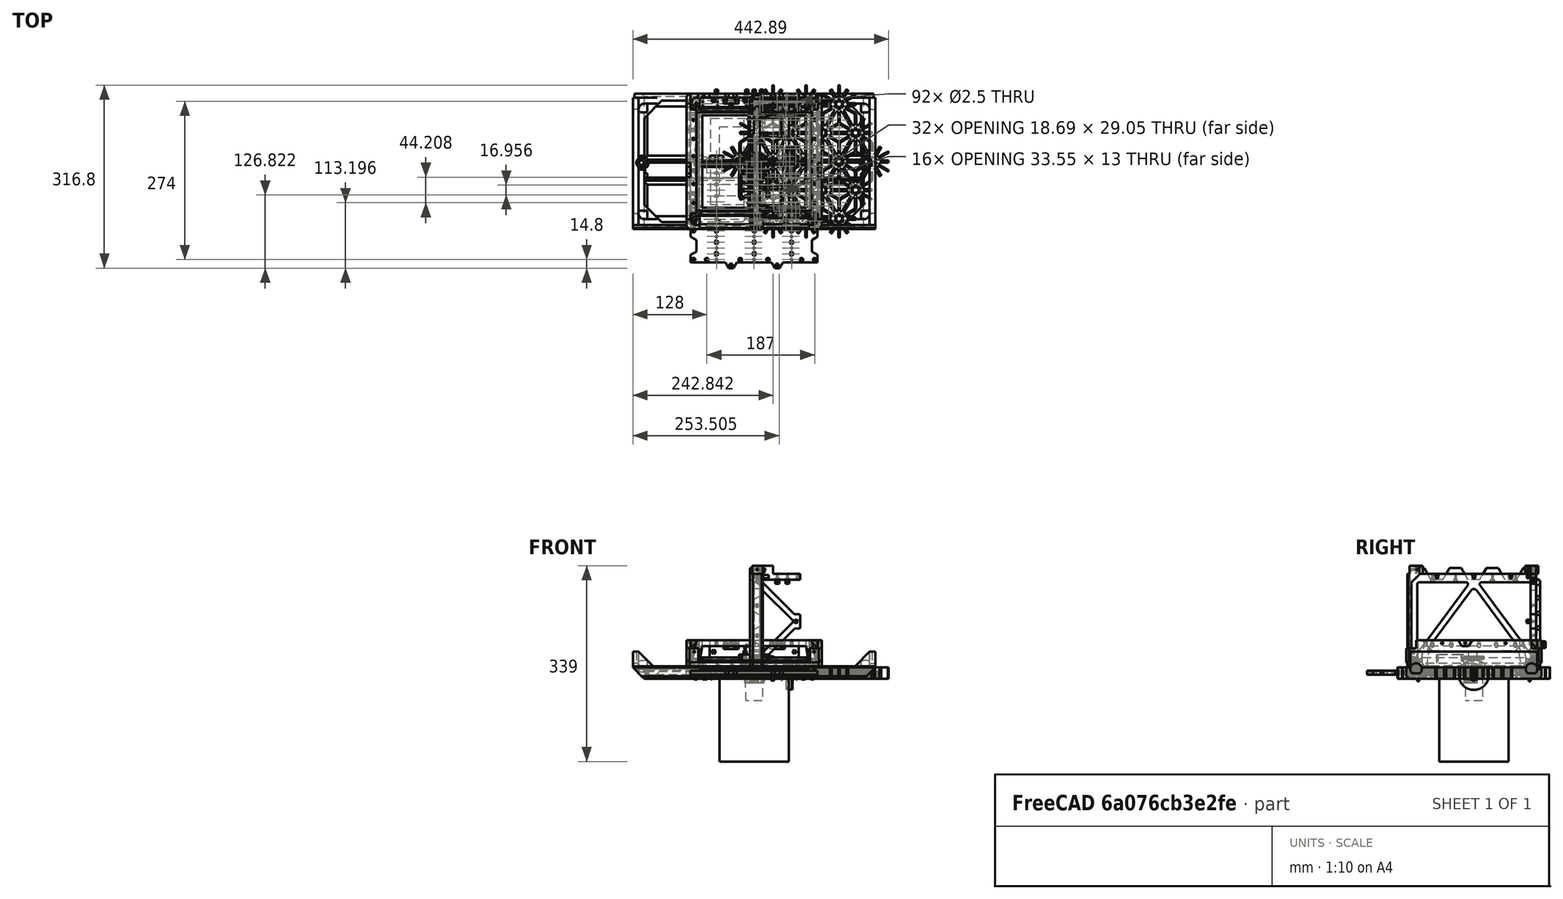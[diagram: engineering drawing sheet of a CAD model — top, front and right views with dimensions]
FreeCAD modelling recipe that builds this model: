
FCSTD DOCUMENT  (FreeCAD 0.20R29177 (Git))
Label: miniXY-Frame
License: All rights reserved
LicenseURL: http://en.wikipedia.org/wiki/All_rights_reserved
objects: Sketcher::SketchObject×115, Part::FeaturePython×91, PartDesign::Pad×45, PartDesign::CoordinateSystem×41, PartDesign::Pocket×41, PartDesign::Hole×37, PartDesign::Body×31, App::Link×25, App::Part×25, PartDesign::ShapeBinder×13, PartDesign::SubShapeBinder×9, PartDesign::Boolean×9, PartDesign::AdditiveBox×5, PartDesign::AdditivePrism×5, PartDesign::Chamfer×4, PartDesign::SubtractiveBox×4, PartDesign::Line×4, Part::Mirroring×4, App::DocumentObjectGroup×3, PartDesign::PolarPattern×3, +8 more types
note: 623 computed .brp shape members not serialized (recipe doc carries the construction recipe); baked Part::Feature solids carry a one-line shape summary decoded from their .brp
EXTERNAL_REF file=../../AppData/Local/Temp/FreeCAD/Cache/FreeCAD_Doc_066654b6-2272-45e0-8b84-83cefede7382_da39a3_1616 obj=Assembly
EXTERNAL_REF file=MGN9.FCStd obj=Assembly
EXTERNAL_REF file=../../AppData/Local/Temp/FreeCAD/Cache/FreeCAD_Doc_a19bdf6e-7e4a-4f2c-907a-7fb10fbe9d93_da39a3_1616 obj=Assembly
EXTERNAL_REF file=../../AppData/Local/Temp/FreeCAD/Cache/FreeCAD_Doc_1e8708ad-fd8b-4a5b-8716-75e4b405d050_da39a3_1616 obj=Assembly
EXTERNAL_REF file=Drive.FCStd obj=LCS_Nema17_Origin
EXTERNAL_REF file=Drive.FCStd obj=Part
EXTERNAL_REF file=../../AppData/Local/Temp/FreeCAD/Cache/FreeCAD_Doc_5f10fd76-f536-416b-8568-16cb6060fa77_da39a3_1616 obj=Assembly
EXTERNAL_REF file=../../AppData/Local/Temp/FreeCAD/Cache/FreeCAD_Doc_b771bde3-d604-4bf0-b2c0-fa68c06b88b6_da39a3_1616 obj=Assembly
EXTERNAL_REF file=../../AppData/Local/Temp/FreeCAD/Cache/FreeCAD_Doc_0e739f10-988f-47ea-a0ae-2bb79bd32ce8_da39a3_1616 obj=Assembly
EXTERNAL_REF file=miniXY-ZDrive.FCStd obj=LCS_Origin
EXTERNAL_REF file=miniXY-ZDrive.FCStd obj=Model

FEATURE [PartDesign::CoordinateSystem] LCS_Origin
  AttacherType = Attacher::AttachEngine3D
  MapMode = 2
  Support = -> [X_Axis]
FEATURE [App::FeaturePython] Variables  # WARN: FeaturePython — macro-defined, semantics opaque (R4)
  CavitySpacingX = 10
  CavitySpacingY = 10
  FittingGap = 0.2
  GantorySpacing = 200
  HeightFromBase = 230
  KumikoBaseWidth = 3
  M3TapDiameter = 2.5
  PositionX = 0
  PositionY = 0
  PositionZ = 0
  PrintBedPosition = 140
  PullyDiameterDrive = 12.73
  PullyDiameterIdler = 12.73
  TopThickness = 10
  Type = App::PropertyContainer
  WallThickness = 7
FEATURE [App::DocumentObjectGroup] Constraints
FEATURE [App::DocumentObjectGroup] Configurations
FEATURE [Part::FeaturePython] MGN9_X  # link proxy (typed FeaturePython)
  AttachedBy = #LCS_Origin
  AttachedTo = Gantory#LCS_GantoryOrigin
  Length = 175
  LinkedObject = -> <external ../../AppData/Local/Temp/FreeCAD/Cache/FreeCAD_Doc_066654b6-2272-45e0-8b84-83cefede7382_da39a3_1616>#Assembly
  Placement = pos=(-2.4e-15,0,-20) rot=(0,0,1;0rad)
  Position = 0
  SolverId = Asm4EE
  SourceObject = -> <external MGN9.FCStd>#Assembly
  expr: Placement = Gantory.Placement * LCS_GantoryOrigin.Placement * AttachmentOffset * varTmpDoc_6#LCS_Origin.Placement ^ -1
FEATURE [PartDesign::CoordinateSystem] LCS_GantoryOrigin
  AttacherType = Attacher::AttachEngine3D
  MapMode = 2
  Support = -> [X_Axis001]
FEATURE [App::Link] Gantory  label="Gantory001"
  AssemblyType = Part::Link
  AttachedBy = #LCS_GantoryOrigin
  AttachedTo = TopPanel#LCS_TopPanelGantoryOrigin
  LinkPlacement = pos=(-2.4e-15,0,-20) rot=(0,0,1;0rad)
  LinkedObject = -> Part
  Placement = pos=(-2.4e-15,0,-20) rot=(0,0,1;0rad)
  SolverId = Asm4EE
  expr: Placement = TopPanel.Placement * LCS_TopPanelGantoryOrigin.Placement * AttachmentOffset * LCS_GantoryOrigin.Placement ^ -1
FEATURE [PartDesign::CoordinateSystem] LCS_LeftRailOrigin
  AttacherType = Attacher::AttachEngine3D
  AttachmentOffset = pos=(0,-100,-10) rot=(0,0,1;0rad)
  MapMode = 3
  Placement = pos=(-100,2.33e-14,10) rot=(0.707107,0.707107,0;3.14159rad)
  Support = -> [Y_Axis001]
  expr: .AttachmentOffset.Base.y = -<<Variables>>.GantorySpacing / 2
FEATURE [PartDesign::CoordinateSystem] LCS_RightRailOrigin
  AttacherType = Attacher::AttachEngine3D
  AttachmentOffset = pos=(0,100,-10) rot=(0,0,1;0rad)
  MapMode = 3
  Placement = pos=(100,-2.11e-14,10) rot=(0.707107,0.707107,0;3.14159rad)
  Support = -> [Y_Axis001]
  expr: .AttachmentOffset.Base.y = <<Variables>>.GantorySpacing / 2
FEATURE [Part::FeaturePython] MGN9_Y_Left  # link proxy (typed FeaturePython)
  AttachedBy = #LCS_Origin
  AttachedTo = Gantory#LCS_LeftRailOrigin
  Length = 175
  LinkedObject = -> <external ../../AppData/Local/Temp/FreeCAD/Cache/FreeCAD_Doc_a19bdf6e-7e4a-4f2c-907a-7fb10fbe9d93_da39a3_1616>#Assembly
  Placement = pos=(-100,2.33e-14,-10) rot=(0.707107,0.707107,0;3.14159rad)
  Position = 0
  SolverId = Asm4EE
  SourceObject = -> <external MGN9.FCStd>#Assembly
  expr: Placement = Gantory.Placement * LCS_LeftRailOrigin.Placement * AttachmentOffset * varTmpDoc_7#LCS_Origin.Placement ^ -1
FEATURE [Part::FeaturePython] MGN9_Y_Right  # link proxy (typed FeaturePython)
  AttachedBy = #LCS_Origin
  AttachedTo = Gantory#LCS_RightRailOrigin
  Length = 175
  LinkedObject = -> <external ../../AppData/Local/Temp/FreeCAD/Cache/FreeCAD_Doc_1e8708ad-fd8b-4a5b-8716-75e4b405d050_da39a3_1616>#Assembly
  Placement = pos=(100,-2.11e-14,-10) rot=(0.707107,0.707107,0;3.14159rad)
  Position = 0
  SolverId = Asm4EE
  SourceObject = -> <external MGN9.FCStd>#Assembly
  expr: Placement = Gantory.Placement * LCS_RightRailOrigin.Placement * AttachmentOffset * varTmpDoc_8#LCS_Origin.Placement ^ -1
FEATURE [Sketcher::SketchObject] Sketch
  FullyConstrained = true
  MapMode = 5
  Support = -> [XY_Plane006]
  sketch-geometry (19):
    g0: LineSegment StartX=-7.5 StartY=16 StartZ=0 EndX=7.5 EndY=16 EndZ=0
    g1: LineSegment StartX=7.5 StartY=-16 StartZ=0 EndX=-7.5 EndY=-16 EndZ=0
    g2: LineSegment StartX=-10 StartY=-13.5 StartZ=0 EndX=-10 EndY=13.5 EndZ=0
    g3: LineSegment StartX=20.7665 StartY=5 StartZ=0 EndX=48 EndY=5 EndZ=0
    g4: LineSegment StartX=50 StartY=3 StartZ=0 EndX=50 EndY=-3 EndZ=0
    g5: LineSegment StartX=48 StartY=-5 StartZ=0 EndX=20.7665 EndY=-5 EndZ=0
    g6: ArcOfCircle CenterX=20.7665 CenterY=-16 CenterZ=0 NormalX=0 NormalY=0 NormalZ=1 AngleXU=0 Radius=11 StartAngle=1.5708 EndAngle=2.95533
    g7: ArcOfCircle CenterX=20.7665 CenterY=16 CenterZ=0 NormalX=0 NormalY=0 NormalZ=1 AngleXU=0 Radius=11 StartAngle=3.32785 EndAngle=4.71239
    g8: ArcOfCircle CenterX=-7.5 CenterY=13.5 CenterZ=0 NormalX=0 NormalY=0 NormalZ=1 AngleXU=0 Radius=2.5 StartAngle=1.5708 EndAngle=3.14159
    g9: GeomPoint X=-10 Y=16 Z=0
    g10: ArcOfCircle CenterX=-7.5 CenterY=-13.5 CenterZ=0 NormalX=0 NormalY=0 NormalZ=1 AngleXU=0 Radius=2.5 StartAngle=3.14159 EndAngle=4.71239
    g11: GeomPoint X=-10 Y=-16 Z=0
    g12: ArcOfCircle CenterX=7.5 CenterY=-13.5 CenterZ=0 NormalX=0 NormalY=0 NormalZ=1 AngleXU=0 Radius=2.5 StartAngle=4.71239 EndAngle=6.09693
    g13: ArcOfCircle CenterX=7.5 CenterY=13.5 CenterZ=0 NormalX=0 NormalY=0 NormalZ=1 AngleXU=0 Radius=2.5 StartAngle=0.18626 EndAngle=1.5708
    g14: GeomPoint X=10 Y=16 Z=0
    g15: ArcOfCircle CenterX=48 CenterY=3 CenterZ=0 NormalX=0 NormalY=0 NormalZ=1 AngleXU=0 Radius=2 StartAngle=-9e-16 EndAngle=1.5708
    g16: GeomPoint X=50 Y=5 Z=0
    g17: ArcOfCircle CenterX=48 CenterY=-3 CenterZ=0 NormalX=0 NormalY=0 NormalZ=1 AngleXU=0 Radius=2 StartAngle=4.71239 EndAngle=6.28319
    g18: GeomPoint X=50 Y=-5 Z=0
  constraints (40):
    c: Horizontal(g3)
    c: Symmetric(g9,g11,g-1)
    c: Symmetric(g16,g18,g-1)
    c: DistanceY(g11,g9) = 32
    c: Symmetric(g9,g14,g-2)
    c: DistanceY(g18,g16) = 10
    c: DistanceX(g-1,g16) = 50
    c: Symmetric(g7,g6,g-1)
    c: PointOnObject(g9,g0)
    c: PointOnObject(g9,g2)
    c: Tangent(g0,g8) = 1.5708
    c: Tangent(g2,g8) = 1.5708
    c: PointOnObject(g11,g2)
    c: PointOnObject(g11,g1)
    c: Tangent(g2,g10) = 1.5708
    c: Tangent(g1,g10) = 1.5708
    c: Tangent(g1,g12) = 1.5708
    c: PointOnObject(g14,g0)
    c: Tangent(g0,g13) = 1.5708
    c: Equal(g8,g10)
    c: Equal(g8,g12)
    c: Radius(g8) = 2.5
    c: DistanceX(g9,g14) = 20
    c: Tangent(g13,g7) = 1.5708
    c: Tangent(g12,g6) = 1.5708
    c: PointOnObject(g7,g0)
    c: Symmetric(g8,g13,g-2)
    c: Symmetric(g12,g13,g-1)
    c: Tangent(g7,g3) = -1.5708
    c: Tangent(g6,g5) = -1.5708
    c: PointOnObject(g16,g3)
    c: PointOnObject(g16,g4)
    c: Tangent(g3,g15) = 1.5708
    c: Tangent(g4,g15) = 1.5708
    c: PointOnObject(g18,g5)
    c: PointOnObject(g18,g4)
    c: Tangent(g5,g17) = 1.5708
    c: Tangent(g4,g17) = 1.5708
    c: Equal(g15,g17)
    c: Radius(g15) = 2
FEATURE [PartDesign::Pad] Pad
  Direction = (0,0,1)
  Length = 7
  Length2 = 10
  Profile = -> Sketch
  ReferenceAxis = -> Sketch [N_Axis]
  Type = 0
FEATURE [Sketcher::SketchObject] Sketch005
  AttachmentOffset = pos=(0,0,10) rot=(0,0,1;0rad)
  FullyConstrained = true
  MapMode = 5
  Placement = pos=(0,0,10) rot=(0,0,1;0rad)
  Support = -> [XY_Plane006]
  sketch-geometry (4):
    g0: Circle CenterX=-7.5 CenterY=5 CenterZ=0 NormalX=0 NormalY=0 NormalZ=1 AngleXU=0 Radius=1.5
    g1: Circle CenterX=-7.5 CenterY=-5 CenterZ=0 NormalX=0 NormalY=0 NormalZ=1 AngleXU=0 Radius=1.5
    g2: Circle CenterX=7.5 CenterY=-5 CenterZ=0 NormalX=0 NormalY=0 NormalZ=1 AngleXU=0 Radius=1.5
    g3: Circle CenterX=7.5 CenterY=5 CenterZ=0 NormalX=0 NormalY=0 NormalZ=1 AngleXU=0 Radius=1.5
  constraints (9):
    c: Symmetric(g0,g1,g-1)
    c: Symmetric(g3,g2,g-1)
    c: Symmetric(g0,g3,g-2)
    c: DistanceX(g0,g3) = 15
    c: DistanceY(g1,g0) = 10
    c: Equal(g0,g1)
    c: Equal(g0,g2)
    c: Equal(g0,g3)
    c: Diameter(g0) = 3
FEATURE [Sketcher::SketchObject] Sketch006
  FullyConstrained = true
  MapMode = 5
  Support = -> [XY_Plane006]
  sketch-geometry (2):
    g0: Circle CenterX=0 CenterY=0 CenterZ=0 NormalX=0 NormalY=0 NormalZ=1 AngleXU=0 Radius=1.5
    g1: Circle CenterX=12.73 CenterY=0 CenterZ=0 NormalX=0 NormalY=0 NormalZ=1 AngleXU=0 Radius=1.5
  constraints (5):
    c: Coincident(g0,g-1)
    c: PointOnObject(g1,g-1)
    c: Equal(g0,g1)
    c: Diameter(g0) = 3
    c: DistanceX(g0,g1) = 12.73
FEATURE [PartDesign::Chamfer] Chamfer
  Angle = 45
  Base = -> Pad [Face16]
  BaseFeature = -> Pad
  ChamferType = 0
  FlipDirection = false
  Size = 1
  Size2 = 1
  SupportTransform = false
  UseAllEdges = false
FEATURE [Sketcher::SketchObject] Sketch007
  FullyConstrained = true
  MapMode = 5
  Support = -> [XY_Plane006]
  sketch-geometry (2):
    g0: Circle CenterX=20 CenterY=0 CenterZ=0 NormalX=0 NormalY=0 NormalZ=1 AngleXU=0 Radius=1.5
    g1: Circle CenterX=40 CenterY=0 CenterZ=0 NormalX=0 NormalY=0 NormalZ=1 AngleXU=0 Radius=1.5
  constraints (6):
    c: PointOnObject(g0,g-1)
    c: PointOnObject(g1,g-1)
    c: DistanceX(g-1,g0) = 20
    c: DistanceX(g0,g1) = 20
    c: Equal(g0,g1)
    c: Diameter(g0) = 3
FEATURE [Sketcher::SketchObject] Sketch008
  AttachmentOffset = pos=(0,0,16.5) rot=(0,0,1;0rad)
  FullyConstrained = true
  MapMode = 5
  Placement = pos=(0,0,16.5) rot=(0,0,1;0rad)
  Support = -> [XY_Plane006]
  sketch-geometry (6):
    g0: LineSegment StartX=9.5 StartY=5 StartZ=0 EndX=26 EndY=5 EndZ=0
    g1: LineSegment StartX=24 StartY=3 StartZ=0 EndX=24 EndY=-3 EndZ=0
    g2: LineSegment StartX=26 StartY=-5 StartZ=0 EndX=9.5 EndY=-5 EndZ=0
    g3: LineSegment StartX=9.5 StartY=-5 StartZ=0 EndX=9.5 EndY=5 EndZ=0
    g4: ArcOfCircle CenterX=26 CenterY=3 CenterZ=0 NormalX=0 NormalY=0 NormalZ=1 AngleXU=0 Radius=2 StartAngle=1.5708 EndAngle=3.14159
    g5: ArcOfCircle CenterX=26 CenterY=-3 CenterZ=0 NormalX=0 NormalY=0 NormalZ=1 AngleXU=0 Radius=2 StartAngle=3.14159 EndAngle=4.71239
  constraints (14):
    c: Horizontal(g0)
    c: Coincident(g0,g3)
    c: Symmetric(g2,g0,g-1)
    c: Coincident(g3,g2)
    c: Tangent(g4,g1) = -1.5708
    c: Tangent(g4,g0) = 1.5708
    c: Tangent(g5,g1) = -1.5708
    c: Tangent(g5,g2) = 1.5708
    c: Symmetric(g4,g5,g-1)
    c: Equal(g4,g5)
    c: Radius(g4) = 2
    c: DistanceY(g3,g3) = 10
    c: DistanceX(g0,g1) = 14.5
    c: DistanceX(g-1,g0) = 9.5
FEATURE [Sketcher::SketchObject] Sketch009
  FullyConstrained = true
  MapMode = 5
  Support = -> [XY_Plane006]
  sketch-geometry (36):
    g0: LineSegment StartX=11.5 StartY=5 StartZ=0 EndX=30 EndY=5 EndZ=0
    g1: LineSegment StartX=32 StartY=3 StartZ=0 EndX=32 EndY=-3 EndZ=0
    g2: LineSegment StartX=30 StartY=-5 StartZ=0 EndX=11.5 EndY=-5 EndZ=0
    g3: LineSegment StartX=9.5 StartY=-3 StartZ=0 EndX=9.5 EndY=3 EndZ=0
    g4: LineSegment StartX=-3 StartY=16 StartZ=0 EndX=3 EndY=16 EndZ=0
    g5: LineSegment StartX=5 StartY=14 StartZ=0 EndX=5 EndY=12 EndZ=0
    g6: LineSegment StartX=3 StartY=10 StartZ=0 EndX=-3 EndY=10 EndZ=0
    g7: LineSegment StartX=-5 StartY=12 StartZ=0 EndX=-5 EndY=14 EndZ=0
    g8: LineSegment StartX=-3 StartY=-10 StartZ=0 EndX=3 EndY=-10 EndZ=0
    g9: LineSegment StartX=5 StartY=-12 StartZ=0 EndX=5 EndY=-14 EndZ=0
    g10: LineSegment StartX=3 StartY=-16 StartZ=0 EndX=-3 EndY=-16 EndZ=0
    g11: LineSegment StartX=-5 StartY=-14 StartZ=0 EndX=-5 EndY=-12 EndZ=0
    g12: ArcOfCircle CenterX=-3 CenterY=14 CenterZ=0 NormalX=0 NormalY=0 NormalZ=1 AngleXU=0 Radius=2 StartAngle=1.5708 EndAngle=3.14159
    g13: GeomPoint X=-5 Y=16 Z=0
    g14: ArcOfCircle CenterX=-3 CenterY=12 CenterZ=0 NormalX=0 NormalY=0 NormalZ=1 AngleXU=0 Radius=2 StartAngle=3.14159 EndAngle=4.71239
    g15: GeomPoint X=-5 Y=10 Z=0
    g16: ArcOfCircle CenterX=3 CenterY=12 CenterZ=0 NormalX=0 NormalY=0 NormalZ=1 AngleXU=0 Radius=2 StartAngle=4.71239 EndAngle=6.28319
    g17: GeomPoint X=5 Y=10 Z=0
    g18: ArcOfCircle CenterX=3 CenterY=14 CenterZ=0 NormalX=0 NormalY=0 NormalZ=1 AngleXU=0 Radius=2 StartAngle=1e-16 EndAngle=1.5708
    g19: GeomPoint X=5 Y=16 Z=0
    g20: ArcOfCircle CenterX=-3 CenterY=-12 CenterZ=0 NormalX=0 NormalY=0 NormalZ=1 AngleXU=0 Radius=2 StartAngle=1.5708 EndAngle=3.14159
    g21: GeomPoint X=-5 Y=-10 Z=0
    g22: ArcOfCircle CenterX=-3 CenterY=-14 CenterZ=0 NormalX=0 NormalY=0 NormalZ=1 AngleXU=0 Radius=2 StartAngle=3.14159 EndAngle=4.71239
    g23: GeomPoint X=-5 Y=-16 Z=0
    g24: ArcOfCircle CenterX=3 CenterY=-14 CenterZ=0 NormalX=0 NormalY=0 NormalZ=1 AngleXU=0 Radius=2 StartAngle=4.71239 EndAngle=6.28319
    g25: GeomPoint X=5 Y=-16 Z=0
    g26: ArcOfCircle CenterX=3 CenterY=-12 CenterZ=0 NormalX=0 NormalY=0 NormalZ=1 AngleXU=0 Radius=2 StartAngle=0 EndAngle=1.5708
    g27: GeomPoint X=5 Y=-10 Z=0
    g28: ArcOfCircle CenterX=11.5 CenterY=3 CenterZ=0 NormalX=0 NormalY=0 NormalZ=1 AngleXU=0 Radius=2 StartAngle=1.5708 EndAngle=3.14159
    g29: GeomPoint X=9.5 Y=5 Z=0
    g30: ArcOfCircle CenterX=11.5 CenterY=-3 CenterZ=0 NormalX=0 NormalY=0 NormalZ=1 AngleXU=0 Radius=2 StartAngle=3.14159 EndAngle=4.71239
    g31: GeomPoint X=9.5 Y=-5 Z=0
    g32: ArcOfCircle CenterX=30 CenterY=-3 CenterZ=0 NormalX=0 NormalY=0 NormalZ=1 AngleXU=0 Radius=2 StartAngle=4.71239 EndAngle=6.28319
    g33: GeomPoint X=32 Y=-5 Z=0
    g34: ArcOfCircle CenterX=30 CenterY=3 CenterZ=0 NormalX=0 NormalY=0 NormalZ=1 AngleXU=0 Radius=2 StartAngle=3e-16 EndAngle=1.5708
    g35: GeomPoint X=32 Y=5 Z=0
  constraints (76):
    c: Horizontal(g0)
    c: Symmetric(g29,g31,g-1)
    c: Symmetric(g35,g33,g-1)
    c: DistanceY(g31,g29) = 10
    c: DistanceX(g29,g35) = 22.5
    c: Vertical(g7)
    c: Symmetric(g13,g19,g-2)
    c: Symmetric(g15,g17,g-2)
    c: Symmetric(g21,g15,g-1)
    c: Symmetric(g13,g23,g-1)
    c: Symmetric(g17,g27,g-1)
    c: Symmetric(g19,g25,g-1)
    c: DistanceY(g23,g13) = 32
    c: DistanceX(g13,g19) = 10
    c: DistanceY(g15,g13) = 6
    c: DistanceX(g-1,g35) = 32
    c: PointOnObject(g13,g4)
    c: PointOnObject(g13,g7)
    c: Tangent(g4,g12) = 1.5708
    c: Tangent(g7,g12) = 1.5708
    c: PointOnObject(g15,g7)
    c: PointOnObject(g15,g6)
    c: Tangent(g7,g14) = 1.5708
    c: Tangent(g6,g14) = 1.5708
    c: PointOnObject(g17,g6)
    c: PointOnObject(g17,g5)
    c: Tangent(g6,g16) = 1.5708
    c: Tangent(g5,g16) = 1.5708
    c: PointOnObject(g19,g5)
    c: PointOnObject(g19,g4)
    c: Tangent(g5,g18) = 1.5708
    c: Tangent(g4,g18) = 1.5708
    c: PointOnObject(g21,g8)
    c: PointOnObject(g21,g11)
    c: Tangent(g8,g20) = 1.5708
    c: Tangent(g11,g20) = 1.5708
    c: PointOnObject(g23,g11)
    c: PointOnObject(g23,g10)
    c: Tangent(g11,g22) = 1.5708
    c: Tangent(g10,g22) = 1.5708
    c: PointOnObject(g25,g10)
    c: PointOnObject(g25,g9)
    c: Tangent(g10,g24) = 1.5708
    c: Tangent(g9,g24) = 1.5708
    c: PointOnObject(g27,g9)
    c: PointOnObject(g27,g8)
    c: Tangent(g9,g26) = 1.5708
    c: Tangent(g8,g26) = 1.5708
    c: PointOnObject(g29,g0)
    c: PointOnObject(g29,g3)
    c: Tangent(g0,g28) = 1.5708
    c: Tangent(g3,g28) = 1.5708
    c: PointOnObject(g31,g3)
    c: PointOnObject(g31,g2)
    c: Tangent(g3,g30) = 1.5708
    c: Tangent(g2,g30) = 1.5708
    c: PointOnObject(g33,g2)
    c: PointOnObject(g33,g1)
    c: Tangent(g2,g32) = 1.5708
    c: Tangent(g1,g32) = 1.5708
    c: PointOnObject(g35,g1)
    c: PointOnObject(g35,g0)
    c: Tangent(g1,g34) = 1.5708
    c: Tangent(g0,g34) = 1.5708
    c: Equal(g12,g14)
    c: Equal(g12,g16)
    c: Equal(g12,g18)
    c: Equal(g12,g20)
    c: Equal(g12,g22)
    c: Equal(g12,g24)
    c: Equal(g12,g26)
    c: Equal(g12,g28)
    c: Equal(g12,g30)
    c: Equal(g12,g32)
    c: Equal(g12,g34)
    c: Radius(g12) = 2
FEATURE [Sketcher::SketchObject] Sketch010
  FullyConstrained = true
  MapMode = 5
  Support = -> [XY_Plane006]
  sketch-geometry (2):
    g0: Circle CenterX=0 CenterY=13 CenterZ=0 NormalX=0 NormalY=0 NormalZ=1 AngleXU=0 Radius=1.5
    g1: Circle CenterX=0 CenterY=-13 CenterZ=0 NormalX=0 NormalY=0 NormalZ=1 AngleXU=0 Radius=1.5
  constraints (5):
    c: PointOnObject(g0,g-2)
    c: Symmetric(g0,g1,g-1)
    c: DistanceY(g1,g0) = 26
    c: Equal(g0,g1)
    c: Diameter(g0) = 3
FEATURE [Sketcher::SketchObject] Sketch011
  AttachmentOffset = pos=(0,0,27) rot=(0,0,1;0rad)
  FullyConstrained = true
  MapMode = 5
  Placement = pos=(0,0,27) rot=(0,0,1;0rad)
  Support = -> [XY_Plane008]
  sketch-geometry (8):
    g0: LineSegment StartX=-5 StartY=18 StartZ=0 EndX=5 EndY=18 EndZ=0
    g1: LineSegment StartX=5 StartY=-18 StartZ=0 EndX=-5 EndY=-18 EndZ=0
    g2: LineSegment StartX=-5 StartY=-18 StartZ=0 EndX=-5 EndY=18 EndZ=0
    g3: LineSegment StartX=18.5 StartY=4.5 StartZ=0 EndX=34 EndY=4.5 EndZ=0
    g4: LineSegment StartX=34 StartY=4.5 StartZ=0 EndX=34 EndY=-4.5 EndZ=0
    g5: LineSegment StartX=34 StartY=-4.5 StartZ=0 EndX=18.5 EndY=-4.5 EndZ=0
    g6: ArcOfCircle CenterX=18.5 CenterY=-18 CenterZ=0 NormalX=0 NormalY=0 NormalZ=1 AngleXU=0 Radius=13.5 StartAngle=1.5708 EndAngle=3.14159
    g7: ArcOfCircle CenterX=18.5 CenterY=18 CenterZ=0 NormalX=0 NormalY=0 NormalZ=1 AngleXU=0 Radius=13.5 StartAngle=3.14159 EndAngle=4.71239
  constraints (21):
    c: Coincident(g1,g2)
    c: Coincident(g2,g0)
    c: Coincident(g3,g4)
    c: Coincident(g4,g5)
    c: Horizontal(g3)
    c: Symmetric(g0,g1,g-1)
    c: Symmetric(g3,g5,g-1)
    c: Symmetric(g3,g4,g-1)
    c: DistanceY(g2,g2) = 36
    c: DistanceX(g0,g0) = 10
    c: Symmetric(g0,g0,g-2)
    c: DistanceY(g4,g4) = 9
    c: Symmetric(g0,g1,g-1)
    c: DistanceX(g-1,g3) = 34
    c: Coincident(g6,g5)
    c: Coincident(g6,g1)
    c: Coincident(g7,g0)
    c: Coincident(g7,g3)
    c: Symmetric(g7,g6,g-1)
    c: Vertical(g7,g3)
    c: Horizontal(g0,g7)
FEATURE [PartDesign::Pad] Pad003
  Direction = (0,0,1)
  Length = 5
  Length2 = 10
  Profile = -> Sketch011
  ReferenceAxis = -> Sketch011 [N_Axis]
  Type = 0
FEATURE [PartDesign::SubtractiveBox] Box003
  AttacherType = Attacher::AttachEngine3D
  AttachmentOffset = pos=(-3.1,9.9,0) rot=(0,0,1;0rad)
  BaseFeature = -> Pad003
  Height = 28
  Length = 6.2
  MapMode = 5
  Placement = pos=(-3.1,9.9,0) rot=(0,0,1;0rad)
  Support = -> [XY_Plane008]
  Width = 6.2
FEATURE [PartDesign::SubtractiveBox] Box004
  AttacherType = Attacher::AttachEngine3D
  AttachmentOffset = pos=(-3.1,-16.1,0) rot=(0,0,1;0rad)
  BaseFeature = -> Box003
  Height = 28
  Length = 6.2
  MapMode = 5
  Placement = pos=(-3.1,-16.1,0) rot=(0,0,1;0rad)
  Support = -> [XY_Plane008]
  Width = 6.2
FEATURE [PartDesign::SubtractiveBox] Box005
  AttacherType = Attacher::AttachEngine3D
  AttachmentOffset = pos=(23.9,-3.1,0) rot=(0,0,1;0rad)
  BaseFeature = -> Box004
  Height = 28
  Length = 8.2
  MapMode = 5
  Placement = pos=(23.9,-3.1,0) rot=(0,0,1;0rad)
  Support = -> [XY_Plane008]
  Width = 6.2
FEATURE [PartDesign::Fillet] Fillet002
  Base = -> Box005 [Edge41,Edge57,Edge49,Edge39,Edge55,Edge47,Edge45,Edge37,Edge53,Edge59,Edge51,Edge43]
  BaseFeature = -> Box005
  Placement = pos=(23.9,-3.1,0) rot=(0,0,1;0rad)
  Radius = 0.8
  SupportTransform = false
  UseAllEdges = false
FEATURE [PartDesign::Fillet] Fillet003
  Base = -> Fillet002 [Edge56,Edge52,Edge62,Edge50,Edge49,Edge58]
  BaseFeature = -> Fillet002
  Placement = pos=(23.9,-3.1,0) rot=(0,0,1;0rad)
  Radius = 2.5
  SupportTransform = false
  UseAllEdges = false
FEATURE [PartDesign::Chamfer] Chamfer001
  Angle = 45
  Base = -> Fillet003 [Edge4]
  BaseFeature = -> Fillet003
  ChamferType = 0
  FlipDirection = false
  Placement = pos=(23.9,-3.1,0) rot=(0,0,1;0rad)
  Size = 1
  Size2 = 1
  SupportTransform = false
  UseAllEdges = false
FEATURE [PartDesign::Chamfer] Chamfer002
  Angle = 45
  Base = -> Chamfer001 [Edge116]
  BaseFeature = -> Chamfer001
  ChamferType = 0
  FlipDirection = false
  Placement = pos=(23.9,-3.1,0) rot=(0,0,1;0rad)
  Size = 1
  Size2 = 1
  SupportTransform = false
  UseAllEdges = false
FEATURE [Sketcher::SketchObject] Sketch012
  AttachmentOffset = pos=(0,0,32) rot=(0,0,1;0rad)
  FullyConstrained = true
  MapMode = 5
  Placement = pos=(0,0,32) rot=(0,0,1;0rad)
  Support = -> [XY_Plane008]
  expr: Constraints[4] = <<Variables>>.PullyDiameterIdler
  sketch-geometry (2):
    g0: Circle CenterX=0 CenterY=0 CenterZ=0 NormalX=0 NormalY=0 NormalZ=1 AngleXU=0 Radius=1.5
    g1: Circle CenterX=12.73 CenterY=0 CenterZ=0 NormalX=0 NormalY=0 NormalZ=1 AngleXU=0 Radius=1.5
  constraints (5):
    c: Coincident(g0,g-1)
    c: PointOnObject(g1,g-1)
    c: Equal(g0,g1)
    c: Diameter(g0) = 3
    c: DistanceX(g0,g1) = 12.73
FEATURE [PartDesign::Hole] Hole004
  BaseFeature = -> Chamfer002
  CustomThreadClearance = 0
  Depth = 98.3182
  DepthType = 1
  Diameter = 5.5
  DrillForDepth = false
  DrillPoint = 1
  DrillPointAngle = 118
  HoleCutCountersinkAngle = 90
  HoleCutCustomValues = false
  HoleCutDepth = 5.4
  HoleCutDiameter = 10.1
  HoleCutType = 0
  ModelThread = false
  Placement = pos=(23.9,-3.1,0) rot=(0,0,1;0rad)
  Profile = -> Sketch012
  Tapered = false
  TaperedAngle = 90
  ThreadClass = 0
  ThreadDepth = 98.3182
  ThreadDepthType = 0
  ThreadDirection = 0
  ThreadFit = 0
  ThreadSize = 13
  ThreadType = 1
  Threaded = false
  UseCustomThreadClearance = false
FEATURE [Sketcher::SketchObject] Sketch013
  AttachmentOffset = pos=(0,0,32) rot=(0,0,1;0rad)
  FullyConstrained = true
  MapMode = 5
  Placement = pos=(0,0,32) rot=(0,0,1;0rad)
  Support = -> [XY_Plane008]
  sketch-geometry (3):
    g0: Circle CenterX=0 CenterY=13 CenterZ=0 NormalX=0 NormalY=0 NormalZ=1 AngleXU=0 Radius=1.5
    g1: Circle CenterX=0 CenterY=-13 CenterZ=0 NormalX=0 NormalY=0 NormalZ=1 AngleXU=0 Radius=1.5
    g2: Circle CenterX=28 CenterY=0 CenterZ=0 NormalX=0 NormalY=0 NormalZ=1 AngleXU=0 Radius=1.5
  constraints (8):
    c: PointOnObject(g0,g-2)
    c: PointOnObject(g2,g-1)
    c: Symmetric(g0,g1,g-1)
    c: DistanceY(g1,g0) = 26
    c: DistanceX(g-1,g2) = 28
    c: Equal(g0,g1)
    c: Equal(g0,g2)
    c: Diameter(g0) = 3
FEATURE [PartDesign::Hole] Hole005
  BaseFeature = -> Hole004
  CustomThreadClearance = 0
  Depth = 98.3182
  DepthType = 1
  Diameter = 3.4
  DrillForDepth = false
  DrillPoint = 1
  DrillPointAngle = 118
  HoleCutCountersinkAngle = 90
  HoleCutCustomValues = false
  HoleCutDepth = 1.7
  HoleCutDiameter = 6
  HoleCutType = 9
  ModelThread = false
  Placement = pos=(23.9,-3.1,0) rot=(0,0,1;0rad)
  Profile = -> Sketch013
  Tapered = false
  TaperedAngle = 90
  ThreadClass = 0
  ThreadDepth = 98.3182
  ThreadDepthType = 0
  ThreadDirection = 0
  ThreadFit = 0
  ThreadSize = 9
  ThreadType = 1
  Threaded = false
  UseCustomThreadClearance = false
FEATURE [PartDesign::CoordinateSystem] GarriageLeftPartOrigin
  AttacherType = Attacher::AttachEngine3D
  AttachmentOffset = pos=(0,0,0) rot=(0,0,-1;1.5708rad)
  MapMode = 2
  Placement = pos=(0,0,0) rot=(0,0,-1;1.5708rad)
  Support = -> [X_Axis004]
FEATURE [PartDesign::CoordinateSystem] LCS_GantoryPosition
  AttacherType = Attacher::AttachEngine3D
  MapMode = 2
  Support = -> [X_Axis001]
  expr: .AttachmentOffset.Base.y = <<Variables>>.PositionX
FEATURE [PartDesign::CoordinateSystem] LCS_LeftCarriagePosition
  AttacherType = Attacher::AttachEngine3D
  AttachmentOffset = pos=(0,-100,0) rot=(0,0,1;0rad)
  MapMode = 3
  Placement = pos=(-100,2.22e-14,-1.11e-14) rot=(0.707107,0.707107,0;3.14159rad)
  Support = -> [Y_Axis001]
  expr: .AttachmentOffset.Base.y = -<<Variables>>.GantorySpacing / 2
FEATURE [App::Link] CarriageLeftOuterIdler
  AssemblyType = Part::Link
  AttachedBy = #LCS_PullyIdlerOrigin
  AttachedTo = Gantory#LCS_LeftCarriagePosition
  AttachmentOffset = pos=(0,0,11.75) rot=(0,0,1;0rad)
  LinkPlacement = pos=(-100,2.09e-14,-31.75) rot=(0.707107,0.707107,0;3.14159rad)
  LinkedObject = -> Part001
  Placement = pos=(-100,2.09e-14,-31.75) rot=(0.707107,0.707107,0;3.14159rad)
  SolverId = Asm4EE
  expr: Placement = Gantory.Placement * LCS_LeftCarriagePosition.Placement * AttachmentOffset * LCS_PullyIdlerOrigin.Placement ^ -1
FEATURE [PartDesign::CoordinateSystem] LCS_PullyIdlerOrigin
  AttacherType = Attacher::AttachEngine3D
  MapMode = 2
  Support = -> [X_Axis002]
FEATURE [App::Link] CarriageLeftInnerIdler
  AssemblyType = Part::Link
  AttachedBy = #LCS_PullyIdlerOrigin
  AttachedTo = Gantory#LCS_LeftCarriagePosition
  AttachmentOffset = pos=(0,12.73,21.25) rot=(0,0,1;0rad)
  LinkPlacement = pos=(-87.27,1.7e-14,-41.25) rot=(0.707107,0.707107,0;3.14159rad)
  LinkedObject = -> Part001
  Placement = pos=(-87.27,1.7e-14,-41.25) rot=(0.707107,0.707107,0;3.14159rad)
  SolverId = Asm4EE
  expr: .AttachmentOffset.Base.y = <<Variables>>.PullyDiameterIdler
  expr: Placement = Gantory.Placement * LCS_LeftCarriagePosition.Placement * AttachmentOffset * LCS_PullyIdlerOrigin.Placement ^ -1
FEATURE [Sketcher::SketchObject] Sketch014
  FullyConstrained = true
  MapMode = 2
  Placement = pos=(0,0,0) rot=(0,1,0;3.14159rad)
  Support = -> [XY_Plane010]
  expr: Constraints[5] = <<Variables>>.GantorySpacing / 2
  sketch-geometry (18):
    g0: Circle CenterX=-100 CenterY=0 CenterZ=0 NormalX=0 NormalY=0 NormalZ=1 AngleXU=0 Radius=3.2
    g1: Circle CenterX=100 CenterY=0 CenterZ=0 NormalX=0 NormalY=0 NormalZ=1 AngleXU=0 Radius=3.2
    g2: Circle CenterX=-100 CenterY=20 CenterZ=0 NormalX=0 NormalY=0 NormalZ=1 AngleXU=0 Radius=3.2
    g3: Circle CenterX=-100 CenterY=40 CenterZ=0 NormalX=0 NormalY=0 NormalZ=1 AngleXU=0 Radius=3.2
    g4: Circle CenterX=-100 CenterY=60 CenterZ=0 NormalX=0 NormalY=0 NormalZ=1 AngleXU=0 Radius=3.2
    g5: Circle CenterX=-100 CenterY=80 CenterZ=0 NormalX=0 NormalY=0 NormalZ=1 AngleXU=0 Radius=3.2
    g6: Circle CenterX=-100 CenterY=-20 CenterZ=0 NormalX=0 NormalY=0 NormalZ=1 AngleXU=0 Radius=3.2
    g7: Circle CenterX=-100 CenterY=-40 CenterZ=0 NormalX=0 NormalY=0 NormalZ=1 AngleXU=0 Radius=3.2
    g8: Circle CenterX=-100 CenterY=-60 CenterZ=0 NormalX=0 NormalY=0 NormalZ=1 AngleXU=0 Radius=3.2
    g9: Circle CenterX=-100 CenterY=-80 CenterZ=0 NormalX=0 NormalY=0 NormalZ=1 AngleXU=0 Radius=3.2
    g10: Circle CenterX=100 CenterY=20 CenterZ=0 NormalX=0 NormalY=0 NormalZ=1 AngleXU=0 Radius=3.2
    g11: Circle CenterX=100 CenterY=40 CenterZ=0 NormalX=0 NormalY=0 NormalZ=1 AngleXU=0 Radius=3.2
    g12: Circle CenterX=100 CenterY=60 CenterZ=0 NormalX=0 NormalY=0 NormalZ=1 AngleXU=0 Radius=3.2
    g13: Circle CenterX=100 CenterY=80 CenterZ=0 NormalX=0 NormalY=0 NormalZ=1 AngleXU=0 Radius=3.2
    g14: Circle CenterX=100 CenterY=-20 CenterZ=0 NormalX=0 NormalY=0 NormalZ=1 AngleXU=0 Radius=3.2
    g15: Circle CenterX=100 CenterY=-40 CenterZ=0 NormalX=0 NormalY=0 NormalZ=1 AngleXU=0 Radius=3.2
    g16: Circle CenterX=100 CenterY=-60 CenterZ=0 NormalX=0 NormalY=0 NormalZ=1 AngleXU=0 Radius=3.2
    g17: Circle CenterX=100 CenterY=-80 CenterZ=0 NormalX=0 NormalY=0 NormalZ=1 AngleXU=0 Radius=3.2
  constraints (25):
    c: PointOnObject(g0,g-1)
    c: Vertical(g0,g2)
    c: Vertical(g2,g3)
    c: Vertical(g3,g4)
    c: Vertical(g4,g5)
    c: DistanceX(g0,g-1) = 100
    c: Equal(g0, g1-g17) x17
    c: Diameter(g0) = 6.4
    c: Symmetric(g1,g0,g-2)
    c: Symmetric(g2,g10,g-2)
    c: Symmetric(g3,g11,g-2)
    c: Symmetric(g4,g12,g-2)
    c: Symmetric(g5,g13,g-2)
    c: Symmetric(g6,g14,g-2)
    c: Symmetric(g7,g15,g-2)
    c: Symmetric(g8,g16,g-2)
    c: Symmetric(g9,g17,g-2)
    c: DistanceY(g0,g2) = 20
    c: DistanceY(g2,g3) = 20
    c: DistanceY(g3,g4) = 20
    c: DistanceY(g4,g5) = 20
    c: Symmetric(g6,g2,g-1)
    c: Symmetric(g7,g3,g-1)
    c: Symmetric(g8,g4,g-1)
    c: Symmetric(g9,g5,g-1)
FEATURE [PartDesign::CoordinateSystem] Local_CS
  AttacherType = Attacher::AttachEngine3D
  AttachmentOffset = pos=(0,0,16) rot=(0,0,1;0rad)
  MapMode = 2
  Placement = pos=(0,0,16) rot=(0,0,1;0rad)
  Support = -> [X_Axis010]
FEATURE [PartDesign::CoordinateSystem] LCS_TopPanelOrigin
  AttacherType = Attacher::AttachEngine3D
  MapMode = 2
  Placement = pos=(0,0,0) rot=(0,1,0;3.14159rad)
  Support = -> [X_Axis010]
FEATURE [PartDesign::CoordinateSystem] LCS_TopPanelGantoryOrigin
  AttacherType = Attacher::AttachEngine3D
  AttachmentOffset = pos=(0,0,-20) rot=(0,0,1;0rad)
  MapMode = 2
  Placement = pos=(0,0,20) rot=(0,1,0;3.14159rad)
  Support = -> [X_Axis009]
FEATURE [App::Link] TopPanel  label="TopPanel001"
  AssemblyType = Part::Link
  AttachedBy = #LCS_TopPanelOrigin
  AttachedTo = Parent Assembly#LCS_Origin
  LinkPlacement = pos=(0,0,0) rot=(0,-1,0;3.14159rad)
  LinkedObject = -> Part004
  Placement = pos=(0,0,0) rot=(0,-1,0;3.14159rad)
  SolverId = Asm4EE
  expr: Placement = LCS_Origin.Placement * AttachmentOffset * LCS_TopPanelOrigin.Placement ^ -1
FEATURE [App::Link] PullyIdlerFrontLeft
  AssemblyType = Part::Link
  AttachedBy = #LCS_PullyIdlerOrigin
  AttachedTo = Parent Assembly#LCS_Origin
  AttachmentOffset = pos=(-100,-100,-41.25) rot=(0,0,1;0rad)
  LinkPlacement = pos=(-100,-100,-41.25) rot=(0,0,1;0rad)
  LinkedObject = -> Part001
  Placement = pos=(-100,-100,-41.25) rot=(0,0,1;0rad)
  SolverId = Asm4EE
  expr: Placement = LCS_Origin.Placement * AttachmentOffset * LCS_PullyIdlerOrigin.Placement ^ -1
FEATURE [App::Link] PullyIdlerFrontRight
  AssemblyType = Part::Link
  AttachedBy = #LCS_PullyIdlerOrigin
  AttachedTo = Parent Assembly#LCS_Origin
  AttachmentOffset = pos=(-100,-100,-31.75) rot=(0,0,1;0rad)
  LinkPlacement = pos=(-100,-100,-31.75) rot=(0,0,1;0rad)
  LinkedObject = -> Part001
  Placement = pos=(-100,-100,-31.75) rot=(0,0,1;0rad)
  SolverId = Asm4EE
  expr: Placement = LCS_Origin.Placement * AttachmentOffset * LCS_PullyIdlerOrigin.Placement ^ -1
FEATURE [App::Link] StepperLeft
  AssemblyType = Part::Link
  AttachedBy = #LCS_Nema17_Origin
  AttachedTo = StepperMountLeft001#LCS_StepperLeftOrigin
  LinkPlacement = pos=(-100,143.5,-51) rot=(0,0,1;0rad)
  LinkedObject = -> <external Drive.FCStd>#Part
  Placement = pos=(-100,143.5,-51) rot=(0,0,1;0rad)
  SolverId = Asm4EE
  expr: Placement = StepperMountLeft001.Placement * LCS_StepperLeftOrigin.Placement * AttachmentOffset * Drive#LCS_Nema17_Origin.Placement ^ -1
FEATURE [PartDesign::CoordinateSystem] LCS_RearPanelOrigin
  AttacherType = Attacher::AttachEngine3D
  AttachmentOffset = pos=(0,-110,235) rot=(0,0,1;0rad)
  MapMode = 3
  Placement = pos=(0,-235,-110) rot=(1,0,0;1.5708rad)
  Support = -> [X_Axis011]
  expr: .AttachmentOffset.Base.y = -(<<Variables>>.GantorySpacing / 2 + <<Variables>>.CavitySpacingY)
FEATURE [App::Link] RearPanel  label="RearPanel001"
  AssemblyType = Part::Link
  AttachedBy = #LCS_RearPanelOrigin
  AttachedTo = Parent Assembly#LCS_Origin
  LinkPlacement = pos=(0,110,-235) rot=(-1,0,0;1.5708rad)
  LinkedObject = -> Part005
  Placement = pos=(0,110,-235) rot=(-1,0,0;1.5708rad)
  SolverId = Asm4EE
  expr: Placement = LCS_Origin.Placement * AttachmentOffset * LCS_RearPanelOrigin.Placement ^ -1
FEATURE [Sketcher::SketchObject] Sketch016
  FullyConstrained = false
  MapMode = 5
  Support = -> [XY_Plane011]
  sketch-geometry (24):
    g0: LineSegment StartX=-17.8707 StartY=32.7328 StartZ=0 EndX=17.8707 EndY=32.7328 EndZ=0
    g1: LineSegment StartX=17.8707 StartY=32.7328 StartZ=0 EndX=17.8707 EndY=0 EndZ=0
    g2: LineSegment StartX=17.8707 StartY=0 StartZ=0 EndX=-17.8707 EndY=0 EndZ=0
    g3: LineSegment StartX=-17.8707 StartY=0 StartZ=0 EndX=-17.8707 EndY=3.2494 EndZ=0
    g4: ArcOfCircle CenterX=-2.36196 CenterY=17.0463 CenterZ=0 NormalX=0 NormalY=0 NormalZ=1 AngleXU=0 Radius=10.6953 StartAngle=1.5708 EndAngle=4.71239
    g5: ArcOfCircle CenterX=2.36196 CenterY=17.0463 CenterZ=0 NormalX=0 NormalY=0 NormalZ=1 AngleXU=0 Radius=10.6953 StartAngle=4.71239 EndAngle=7.85398
    g6: LineSegment StartX=-2.36196 StartY=6.35103 StartZ=0 EndX=2.36196 EndY=6.35103 EndZ=0
    g7: LineSegment StartX=2.36196 StartY=27.7416 StartZ=0 EndX=-2.36196 EndY=27.7416 EndZ=0
    g8: ArcOfCircle CenterX=-13.9129 CenterY=28.3121 CenterZ=0 NormalX=0 NormalY=0 NormalZ=1 AngleXU=0 Radius=0.962578 StartAngle=4.71239 EndAngle=7.85398
    g9: LineSegment StartX=-17.8707 StartY=27.3495 StartZ=0 EndX=-13.9129 EndY=27.3495 EndZ=0
    g10: LineSegment StartX=-13.9129 StartY=29.2746 StartZ=0 EndX=-17.8707 EndY=29.2746 EndZ=0
    g11: ArcOfCircle CenterX=-14.0555 CenterY=4.21198 CenterZ=0 NormalX=0 NormalY=0 NormalZ=1 AngleXU=0 Radius=0.962576 StartAngle=4.71239 EndAngle=7.85398
    g12: LineSegment StartX=-17.8707 StartY=3.2494 StartZ=0 EndX=-14.0555 EndY=3.2494 EndZ=0
    g13: LineSegment StartX=-14.0555 StartY=5.17455 StartZ=0 EndX=-17.8707 EndY=5.17455 EndZ=0
    g14: ArcOfCircle CenterX=9.90199 CenterY=3.35635 CenterZ=0 NormalX=0 NormalY=0 NormalZ=1 AngleXU=0 Radius=1.28344 StartAngle=1.5708 EndAngle=4.71239
    g15: ArcOfCircle CenterX=15.0357 CenterY=3.35635 CenterZ=0 NormalX=0 NormalY=0 NormalZ=1 AngleXU=0 Radius=1.28344 StartAngle=4.71239 EndAngle=7.85398
    g16: LineSegment StartX=9.90199 StartY=2.07292 StartZ=0 EndX=15.0357 EndY=2.07292 EndZ=0
    g17: LineSegment StartX=15.0357 StartY=4.63979 StartZ=0 EndX=9.90199 EndY=4.63979 EndZ=0
    g18: ArcOfCircle CenterX=10.1872 CenterY=29.7381 CenterZ=0 NormalX=0 NormalY=0 NormalZ=1 AngleXU=0 Radius=1.17648 StartAngle=1.5708 EndAngle=4.71239
    g19: ArcOfCircle CenterX=14.8931 CenterY=29.7381 CenterZ=0 NormalX=0 NormalY=0 NormalZ=1 AngleXU=0 Radius=1.17648 StartAngle=4.71239 EndAngle=7.85398
    g20: LineSegment StartX=10.1872 StartY=28.5616 StartZ=0 EndX=14.8931 EndY=28.5616 EndZ=0
    g21: LineSegment StartX=14.8931 StartY=30.9146 StartZ=0 EndX=10.1872 EndY=30.9146 EndZ=0
    g22: LineSegment StartX=-17.8707 StartY=29.2746 StartZ=0 EndX=-17.8707 EndY=32.7328 EndZ=0
    g23: LineSegment StartX=-17.8707 StartY=5.17455 StartZ=0 EndX=-17.8707 EndY=27.3495 EndZ=0
  constraints (36):
    c: Coincident(g0,g1)
    c: Coincident(g1,g2)
    c: Coincident(g2,g3)
    c: Coincident(g22,g0)
    c: Vertical(g3)
    c: PointOnObject(g1,g-1)
    c: Symmetric(g2,g1,g-2)
    c: Symmetric(g0,g0,g-2)
    c: Tangent(g4,g6) = -1.5708
    c: Tangent(g6,g5) = -1.5708
    c: Tangent(g5,g7) = -1.5708
    c: Tangent(g7,g4) = -1.5708
    c: Equal(g4,g5)
    c: Symmetric(g4,g5,g-2)
    c: Tangent(g9,g8) = -1.5708
    c: Tangent(g8,g10) = -1.5708
    c: Horizontal(g9)
    c: Tangent(g12,g11) = -1.5708
    c: Tangent(g11,g13) = -1.5708
    c: Horizontal(g12)
    c: Tangent(g14,g16) = -1.5708
    c: Tangent(g16,g15) = -1.5708
    c: Tangent(g15,g17) = -1.5708
    c: Tangent(g17,g14) = -1.5708
    c: Equal(g14,g15)
    c: Horizontal(g16)
    c: Tangent(g18,g20) = -1.5708
    c: Tangent(g20,g19) = -1.5708
    c: Tangent(g19,g21) = -1.5708
    c: Tangent(g21,g18) = -1.5708
    c: Equal(g18,g19)
    c: Horizontal(g20)
    c: PointOnObject(g23,g9)
    c: PointOnObject(g22,g10)
    c: PointOnObject(g3,g12)
    c: PointOnObject(g23,g13)
FEATURE [PartDesign::CoordinateSystem] LCS_LeftPanelOrigin  label="LCS_LeftPanelOrigin_1st"
  AttacherType = Attacher::AttachEngine3D
  AttachmentOffset = pos=(110,0,235) rot=(0,0,1;0rad)
  MapMode = 2
  Placement = pos=(110,0,235) rot=(0,0,1;0rad)
  Support = -> [X_Axis013]
  expr: .AttachmentOffset.Base.x = (<<Variables>>.GantorySpacing + 20) / 2
FEATURE [App::Link] LeftPanel  label="LeftPanel001"
  AssemblyType = Part::Link
  AttachedBy = #LCS_LeftPanelOrigin
  AttachedTo = Parent Assembly#LCS_Origin
  LinkPlacement = pos=(-110,0,-235) rot=(0,0,1;0rad)
  LinkedObject = -> Part006
  Placement = pos=(-110,0,-235) rot=(0,0,1;0rad)
  SolverId = Asm4EE
  expr: Placement = LCS_Origin.Placement * AttachmentOffset * LCS_LeftPanelOrigin.Placement ^ -1
FEATURE [PartDesign::CoordinateSystem] LCS_RightPanelOrigin
  AttacherType = Attacher::AttachEngine3D
  AttachmentOffset = pos=(60,0,110) rot=(0,1,0;1.5708rad)
  MapMode = 2
  Placement = pos=(60,0,110) rot=(0,1,0;1.5708rad)
  Support = -> [X_Axis035]
  expr: .AttachmentOffset.Base.x = 60
  expr: .AttachmentOffset.Base.z = (<<Variables>>.GantorySpacing + 20) / 2
FEATURE [App::Link] RightPanel  label="RightPanel001"
  AssemblyType = Part::Link
  AttachedBy = #LCS_RightPanelOrigin
  AttachedTo = Parent Assembly#LCS_Origin
  LinkPlacement = pos=(110,0,-60) rot=(0,-1,0;1.5708rad)
  LinkedObject = -> Part007
  Placement = pos=(110,0,-60) rot=(0,-1,0;1.5708rad)
  SolverId = Asm4EE
  expr: Placement = LCS_Origin.Placement * AttachmentOffset * LCS_RightPanelOrigin.Placement ^ -1
FEATURE [PartDesign::CoordinateSystem] LCS_BottomPanelOrigin
  AttacherType = Attacher::AttachEngine3D
  AttachmentOffset = pos=(0,0,270) rot=(0,0,1;0rad)
  MapMode = 2
  Placement = pos=(0,0,270) rot=(0,0,1;0rad)
  Support = -> [X_Axis017]
FEATURE [App::Link] BottomPanel  label="BottomPanel001"
  AssemblyType = Part::Link
  AttachedBy = #LCS_BottomPanelOrigin
  AttachedTo = Parent Assembly#LCS_Origin
  LinkPlacement = pos=(0,0,-270) rot=(0,0,1;0rad)
  LinkedObject = -> Part008
  Placement = pos=(0,0,-270) rot=(0,0,1;0rad)
  SolverId = Asm4EE
  expr: Placement = LCS_Origin.Placement * AttachmentOffset * LCS_BottomPanelOrigin.Placement ^ -1
FEATURE [PartDesign::AdditiveBox] Box037
  AttacherType = Attacher::AttachEngine3D
  AttachmentOffset = pos=(-95,-5,0) rot=(0,0,1;0rad)
  Height = 30
  Length = 190
  MapMode = 5
  Placement = pos=(-95,-5,0) rot=(0,0,1;0rad)
  Support = -> [XY_Plane020]
  Width = 5
  expr: .AttachmentOffset.Base.x = -(<<Variables>>.GantorySpacing - 10) / 2
  expr: .AttachmentOffset.Base.y = -(<<Variables>>.WallThickness - 2)
  expr: Length = <<Variables>>.GantorySpacing - 10
  expr: Width = <<Variables>>.WallThickness - 2
FEATURE [PartDesign::CoordinateSystem] LCS_FrontPanelOrigin
  AttacherType = Attacher::AttachEngine3D
  AttachmentOffset = pos=(0,110,270) rot=(0,0,1;0rad)
  MapMode = 2
  Placement = pos=(0,110,270) rot=(0,0,1;0rad)
  Support = -> [X_Axis019]
  expr: .AttachmentOffset.Base.y = <<Variables>>.GantorySpacing / 2 + <<Variables>>.CavitySpacingY
FEATURE [App::Link] FrontPanel  label="FrontPanel001"
  AssemblyType = Part::Link
  AttachedBy = #LCS_FrontPanelOrigin
  AttachedTo = Parent Assembly#LCS_Origin
  LinkPlacement = pos=(0,-110,-270) rot=(0,0,1;0rad)
  LinkedObject = -> Part009
  Placement = pos=(0,-110,-270) rot=(0,0,1;0rad)
  SolverId = Asm4EE
  expr: Placement = LCS_Origin.Placement * AttachmentOffset * LCS_FrontPanelOrigin.Placement ^ -1
FEATURE [PartDesign::CoordinateSystem] LCS_HatOrigin
  AttacherType = Attacher::AttachEngine3D
  MapMode = 2
  Support = -> [X_Axis021]
FEATURE [Sketcher::SketchObject] Sketch017
  FullyConstrained = true
  MapMode = 5
  Placement = pos=(0,0,0) rot=(0.57735,0.57735,0.57735;2.0944rad)
  Support = -> [YZ_Plane022]
  expr: Constraints[15] = <<Variables>>.GantorySpacing - 30
  expr: Constraints[8] = <<Variables>>.GantorySpacing - 10
  expr: Constraints[9] = <<Variables>>.GantorySpacing - 30
  sketch-geometry (8):
    g0: LineSegment StartX=-85 StartY=60 StartZ=0 EndX=85 EndY=60 EndZ=0
    g1: LineSegment StartX=85 StartY=60 StartZ=0 EndX=95 EndY=0 EndZ=0
    g2: LineSegment StartX=95 StartY=0 StartZ=0 EndX=85 EndY=0 EndZ=0
    g3: LineSegment StartX=-95 StartY=0 StartZ=0 EndX=-85 EndY=60 EndZ=0
    g4: LineSegment StartX=-85 StartY=0 StartZ=0 EndX=-76.6667 EndY=50 EndZ=0
    g5: LineSegment StartX=-76.6667 StartY=50 StartZ=0 EndX=76.6667 EndY=50 EndZ=0
    g6: LineSegment StartX=76.6667 StartY=50 StartZ=0 EndX=85 EndY=0 EndZ=0
    g7: LineSegment StartX=-85 StartY=0 StartZ=0 EndX=-95 EndY=0 EndZ=0
  constraints (20):
    c: Coincident(g0,g1)
    c: Coincident(g1,g2)
    c: Coincident(g7,g3)
    c: Coincident(g3,g0)
    c: PointOnObject(g1,g-1)
    c: Symmetric(g0,g0,g-2)
    c: Symmetric(g7,g1,g-2)
    c: DistanceY(g-1,g0) = 60
    c: DistanceX(g7,g1) = 190
    c: DistanceX(g0,g0) = 170
    c: Coincident(g5,g4)
    c: Coincident(g6,g5)
    c: Symmetric(g4,g5,g-2)
    c: Symmetric(g4,g6,g-2)
    c: Parallel(g4,g3)
    c: DistanceX(g4,g6) = 170
    c: DistanceY(g-1,g4) = 50
    c: Coincident(g7,g4)
    c: Coincident(g2,g6)
    c: PointOnObject(g4,g-1)
FEATURE [PartDesign::Pad] Pad005
  Direction = (1,-2e-16,3e-16)
  Length = 220
  Length2 = 10
  Midplane = true
  Placement = pos=(0,0,0) rot=(0.57735,0.57735,0.57735;2.0944rad)
  Profile = -> Sketch017
  ReferenceAxis = -> Sketch017 [N_Axis]
  Type = 0
  expr: Length = <<Variables>>.GantorySpacing + 20
FEATURE [Sketcher::SketchObject] Sketch018
  FullyConstrained = true
  MapMode = 5
  Placement = pos=(0,0,0) rot=(1,0,0;1.5708rad)
  Support = -> [XZ_Plane022]
  expr: Constraints[26] = <<Variables>>.GantorySpacing + 20
  expr: Constraints[28] = <<Variables>>.GantorySpacing
  expr: Constraints[7] = <<Variables>>.GantorySpacing - 20
  sketch-geometry (12):
    g0: LineSegment StartX=-90 StartY=50 StartZ=0 EndX=90 EndY=50 EndZ=0
    g1: LineSegment StartX=90 StartY=50 StartZ=0 EndX=98.3333 EndY=0 EndZ=0
    g2: LineSegment StartX=98.3333 StartY=0 StartZ=0 EndX=-98.3333 EndY=0 EndZ=0
    g3: LineSegment StartX=-98.3333 StartY=0 StartZ=0 EndX=-90 EndY=50 EndZ=0
    g4: LineSegment StartX=-130 StartY=60 StartZ=0 EndX=-100 EndY=60 EndZ=0
    g5: LineSegment StartX=-100 StartY=60 StartZ=0 EndX=-110 EndY=0 EndZ=0
    g6: LineSegment StartX=-110 StartY=0 StartZ=0 EndX=-130 EndY=0 EndZ=0
    g7: LineSegment StartX=-130 StartY=0 StartZ=0 EndX=-130 EndY=60 EndZ=0
    g8: LineSegment StartX=100 StartY=60 StartZ=0 EndX=130 EndY=60 EndZ=0
    g9: LineSegment StartX=130 StartY=60 StartZ=0 EndX=130 EndY=0 EndZ=0
    g10: LineSegment StartX=130 StartY=0 StartZ=0 EndX=110 EndY=0 EndZ=0
    g11: LineSegment StartX=110 StartY=0 StartZ=0 EndX=100 EndY=60 EndZ=0
  constraints (30):
    c: Coincident(g0,g1)
    c: Coincident(g1,g2)
    c: Coincident(g2,g3)
    c: Coincident(g3,g0)
    c: Symmetric(g2,g1,g-2)
    c: Symmetric(g0,g0,g-2)
    c: DistanceY(g-1,g0) = 50
    c: DistanceX(g0,g0) = 180
    c: Coincident(g4,g5)
    c: Coincident(g5,g6)
    c: Coincident(g6,g7)
    c: Coincident(g7,g4)
    c: Horizontal(g4)
    c: Horizontal(g6)
    c: PointOnObject(g5,g-1)
    c: DistanceY(g7,g7) = 60
    c: DistanceX(g6,g6) = 20
    c: Vertical(g7)
    c: Coincident(g8,g9)
    c: Coincident(g9,g10)
    c: Coincident(g10,g11)
    c: Coincident(g11,g8)
    c: Symmetric(g5,g10,g-2)
    c: Symmetric(g4,g8,g-2)
    c: Symmetric(g4,g8,g-2)
    c: Symmetric(g6,g9,g-2)
    c: DistanceX(g5,g10) = 220
    c: Parallel(g5,g3)
    c: DistanceX(g4,g8) = 200
    c: DistanceY(g-1,g2) = 0
FEATURE [PartDesign::Pocket] Pocket
  BaseFeature = -> Pad005
  Direction = (0,1,2e-16)
  Length = 200
  Length2 = 5
  Midplane = true
  Placement = pos=(0,0,0) rot=(0.57735,0.57735,0.57735;2.0944rad)
  Profile = -> Sketch018
  ReferenceAxis = -> Sketch018 [N_Axis]
  Type = 0
  expr: Length = <<Variables>>.GantorySpacing
FEATURE [PartDesign::SubtractiveBox] Box038
  AttacherType = Attacher::AttachEngine3D
  AttachmentOffset = pos=(-90,-80,0) rot=(0,0,1;0rad)
  BaseFeature = -> Pocket
  Height = 100
  Length = 180
  MapMode = 5
  Placement = pos=(-90,-80,0) rot=(0,0,1;0rad)
  Support = -> [XY_Plane022]
  Width = 160
  expr: .AttachmentOffset.Base.x = -(<<Variables>>.GantorySpacing - 20) / 2
  expr: .AttachmentOffset.Base.y = -(<<Variables>>.GantorySpacing - 40) / 2
  expr: Length = <<Variables>>.GantorySpacing - 20
  expr: Width = <<Variables>>.GantorySpacing - 40
FEATURE [PartDesign::Body] Body010  label="HatFrame"
  Group = -> [Sketch017,Pad005,Sketch018,Pocket,Box038]
  Origin = -> Origin022
  Tip = -> Box038
FEATURE [App::Part] Part010  label="Hat"
  Group = -> [Body010,LCS_HatOrigin]
  Origin = -> Origin021
FEATURE [App::Link] Hat  label="Hat001"
  AssemblyType = Part::Link
  AttachedBy = #LCS_HatOrigin
  AttachedTo = Parent Assembly#LCS_Origin
  LinkedObject = -> Part010
  SolverId = Asm4EE
  expr: Placement = LCS_Origin.Placement * AttachmentOffset * LCS_HatOrigin.Placement ^ -1
FEATURE [Sketcher::SketchObject] Sketch019
  FullyConstrained = true
  MapMode = 5
  Placement = pos=(0,0,0) rot=(1,0,0;1.5708rad)
  Support = -> [XZ_Plane024]
  sketch-geometry (4):
    g0: LineSegment StartX=-15 StartY=0 StartZ=0 EndX=15 EndY=2e-16 EndZ=0
    g1: LineSegment StartX=15 StartY=2e-16 StartZ=0 EndX=14 EndY=-45 EndZ=0
    g2: LineSegment StartX=14 StartY=-45 StartZ=0 EndX=-14 EndY=-45 EndZ=0
    g3: LineSegment StartX=-14 StartY=-45 StartZ=0 EndX=-15 EndY=0 EndZ=0
  constraints (10):
    c: Coincident(g0,g1)
    c: Coincident(g1,g2)
    c: Coincident(g2,g3)
    c: Coincident(g3,g0)
    c: PointOnObject(g0,g-1)
    c: Symmetric(g0,g0,g-2)
    c: Symmetric(g2,g1,g-2)
    c: DistanceX(g2,g2) = 28
    c: DistanceX(g0,g0) = 30
    c: DistanceY(g3,g3) = 45
FEATURE [PartDesign::Pad] Pad006
  Direction = (0,-1,2e-16)
  Length = 30
  Length2 = 10
  Midplane = true
  Placement = pos=(0,0,0) rot=(1,0,0;1.5708rad)
  Profile = -> Sketch019
  ReferenceAxis = -> Sketch019 [N_Axis]
  Type = 0
FEATURE [PartDesign::Body] Body011  label="FootBody"
  Group = -> [Sketch019,Pad006]
  Origin = -> Origin024
  Tip = -> Pad006
FEATURE [App::Part] Part011  label="Foot"
  Group = -> [Body011]
  Origin = -> Origin023
FEATURE [Sketcher::SketchObject] Sketch021
  FullyConstrained = true
  MapMode = 5
  Placement = pos=(0,0,0) rot=(0.57735,0.57735,0.57735;2.0944rad)
  Support = -> [YZ_Plane016]
  expr: Constraints[15] = sqrt(2) * 10
  expr: Constraints[91] = <<Variables>>.TopThickness + 10
  expr: Constraints[93] = <<Variables>>.GantorySpacing + 16 - 20
  expr: Constraints[94] = <<Variables>>.GantorySpacing + 16 - 20
  sketch-geometry (43):
    g0: LineSegment StartX=-98 StartY=190 StartZ=0 EndX=98 EndY=190 EndZ=0
    g1: LineSegment StartX=98 StartY=190 StartZ=0 EndX=98 EndY=175 EndZ=0
    g2: LineSegment StartX=92.0562 StartY=20 StartZ=0 EndX=-92.0562 EndY=20 EndZ=0
    g3: LineSegment StartX=-98 StartY=45.951 StartZ=0 EndX=-98 EndY=157 EndZ=0
    g4: LineSegment StartX=-98 StartY=175 StartZ=0 EndX=98 EndY=175 EndZ=0
    g5: LineSegment StartX=95 StartY=160 StartZ=0 EndX=13.0149 EndY=160 EndZ=0
    g6: LineSegment StartX=-10.6014 StartY=155.218 StartZ=0 EndX=-92.5865 EndY=44.1691 EndZ=0
    g7: LineSegment StartX=10.6014 StartY=155.218 StartZ=0 EndX=92.5865 EndY=44.1691 EndZ=0
    g8: LineSegment StartX=-94.4697 StartY=24.7818 StartZ=0 EndX=-91.5166 EndY=28.7818 EndZ=0
    g9: LineSegment StartX=4.82702 StartY=146.203 StartZ=0 EndX=79.7041 EndY=44.7818 EndZ=0
    g10: LineSegment StartX=-98 StartY=175 StartZ=0 EndX=-98 EndY=190 EndZ=0
    g11: LineSegment StartX=-13.0149 StartY=160 StartZ=0 EndX=-95 EndY=160 EndZ=0
    g12: LineSegment StartX=98 StartY=157 StartZ=0 EndX=98 EndY=45.951 EndZ=0
    g13: ArcOfCircle CenterX=-95 CenterY=45.951 CenterZ=0 NormalX=0 NormalY=0 NormalZ=1 AngleXU=0 Radius=3 StartAngle=3.14159 EndAngle=5.64723
    g14: GeomPoint X=-98 Y=36.8365 Z=0
    g15: ArcOfCircle CenterX=-95 CenterY=157 CenterZ=0 NormalX=0 NormalY=0 NormalZ=1 AngleXU=0 Radius=3 StartAngle=1.5708 EndAngle=3.14159
    g16: GeomPoint X=-98 Y=160 Z=0
    g17: ArcOfCircle CenterX=-13.0149 CenterY=157 CenterZ=0 NormalX=0 NormalY=0 NormalZ=1 AngleXU=0 Radius=3 StartAngle=5.64723 EndAngle=7.85398
    g18: GeomPoint X=-7.07107 Y=160 Z=0
    g19: ArcOfCircle CenterX=13.0149 CenterY=157 CenterZ=0 NormalX=0 NormalY=0 NormalZ=1 AngleXU=0 Radius=3 StartAngle=1.5708 EndAngle=3.77755
    g20: GeomPoint X=7.07107 Y=160 Z=0
    g21: ArcOfCircle CenterX=95 CenterY=45.951 CenterZ=0 NormalX=0 NormalY=0 NormalZ=1 AngleXU=0 Radius=3 StartAngle=3.77755 EndAngle=6.28319
    g22: GeomPoint X=98 Y=36.8365 Z=0
    g23: ArcOfCircle CenterX=95 CenterY=157 CenterZ=0 NormalX=0 NormalY=0 NormalZ=1 AngleXU=0 Radius=3 StartAngle=-3.6e-15 EndAngle=1.5708
    g24: GeomPoint X=98 Y=160 Z=0
    g25: LineSegment StartX=-77.2906 StartY=40 StartZ=0 EndX=77.2906 EndY=40 EndZ=0
    g26: LineSegment StartX=-89.103 StartY=30 StartZ=0 EndX=89.103 EndY=30 EndZ=0
    g27: LineSegment StartX=-79.7041 StartY=44.7818 StartZ=0 EndX=-4.82702 EndY=146.203 EndZ=0
    g28: LineSegment StartX=91.5166 StartY=28.7818 StartZ=0 EndX=94.4697 EndY=24.7818 EndZ=0
    g29: ArcOfCircle CenterX=-89.103 CenterY=27 CenterZ=0 NormalX=0 NormalY=0 NormalZ=1 AngleXU=0 Radius=3 StartAngle=1.5708 EndAngle=2.50564
    g30: GeomPoint X=-90.6172 Y=30 Z=0
    g31: ArcOfCircle CenterX=89.103 CenterY=27 CenterZ=0 NormalX=0 NormalY=0 NormalZ=1 AngleXU=0 Radius=3 StartAngle=0.635957 EndAngle=1.5708
    g32: GeomPoint X=90.6172 Y=30 Z=0
    g33: ArcOfCircle CenterX=-77.2906 CenterY=43 CenterZ=0 NormalX=0 NormalY=0 NormalZ=1 AngleXU=0 Radius=3 StartAngle=2.50564 EndAngle=4.71239
    g34: GeomPoint X=-83.2344 Y=40 Z=0
    g35: ArcOfCircle CenterX=0 CenterY=142.639 CenterZ=0 NormalX=0 NormalY=0 NormalZ=1 AngleXU=0 Radius=6 StartAngle=0.635957 EndAngle=2.50564
    g36: GeomPoint X=2.3e-15 Y=152.741 Z=0
    g37: ArcOfCircle CenterX=-92.0562 CenterY=23 CenterZ=0 NormalX=0 NormalY=0 NormalZ=1 AngleXU=0 Radius=3 StartAngle=2.50564 EndAngle=4.71239
    g38: GeomPoint X=-98 Y=20 Z=0
    g39: ArcOfCircle CenterX=92.0562 CenterY=23 CenterZ=0 NormalX=0 NormalY=0 NormalZ=1 AngleXU=0 Radius=3 StartAngle=4.71239 EndAngle=6.91914
    g40: GeomPoint X=98 Y=20 Z=0
    g41: ArcOfCircle CenterX=77.2906 CenterY=43 CenterZ=0 NormalX=0 NormalY=0 NormalZ=1 AngleXU=0 Radius=3 StartAngle=4.71239 EndAngle=6.91914
    g42: GeomPoint X=83.2344 Y=40 Z=0
  constraints (95):
    c: Coincident(g0,g1)
    c: Coincident(g10,g0)
    c: Coincident(g10,g4)
    c: Coincident(g4,g1)
    c: Symmetric(g0,g0,g-2)
    c: Symmetric(g4,g1,g-2)
    c: Vertical(g10)
    c: Symmetric(g18,g20,g-2)
    c: Symmetric(g16,g24,g-2)
    c: Symmetric(g14,g22,g-2)
    c: Vertical(g3)
    c: Horizontal(g11)
    c: DistanceY(g16,g4) = 15
    c: DistanceY(g-1,g0) = 190
    c: DistanceY(g-1,g4) = 175
    c: DistanceX(g18,g20) = 14.1421
    c: PointOnObject(g14,g3)
    c: PointOnObject(g14,g6)
    c: Tangent(g3,g13) = 1.5708
    c: Tangent(g6,g13) = 1.5708
    c: PointOnObject(g16,g3)
    c: PointOnObject(g16,g11)
    c: Tangent(g3,g15) = 1.5708
    c: Tangent(g11,g15) = -1.5708
    c: PointOnObject(g18,g11)
    c: PointOnObject(g18,g6)
    c: Tangent(g11,g17) = -1.5708
    c: Tangent(g6,g17) = 1.5708
    c: PointOnObject(g20,g7)
    c: PointOnObject(g20,g5)
    c: Tangent(g7,g19) = -1.5708
    c: Tangent(g5,g19) = -1.5708
    c: PointOnObject(g22,g7)
    c: PointOnObject(g22,g12)
    c: Tangent(g7,g21) = -1.5708
    c: Tangent(g12,g21) = 1.5708
    c: PointOnObject(g24,g5)
    c: PointOnObject(g24,g12)
    c: Tangent(g5,g23) = -1.5708
    c: Tangent(g12,g23) = 1.5708
    c: PointOnObject(g30,g8)
    c: PointOnObject(g30,g26)
    c: Tangent(g8,g29) = 1.5708
    c: Tangent(g26,g29) = 1.5708
    c: PointOnObject(g32,g26)
    c: PointOnObject(g32,g28)
    c: Tangent(g26,g31) = 1.5708
    c: Tangent(g28,g31) = 1.5708
    c: PointOnObject(g34,g25)
    c: PointOnObject(g34,g27)
    c: Tangent(g25,g33) = -1.5708
    c: Tangent(g27,g33) = 1.5708
    c: Distance(g34,g26) = 10
    c: Symmetric(g29,g31,g-2)
    c: PointOnObject(g36,g27)
    c: PointOnObject(g36,g9)
    c: Tangent(g27,g35) = 1.5708
    c: Tangent(g9,g35) = 1.5708
    c: PointOnObject(g35,g-2)
    c: Radius(g35) = 6
    c: PointOnObject(g38,g8)
    c: PointOnObject(g38,g2)
    c: Tangent(g8,g37) = 1.5708
    c: Tangent(g2,g37) = 1.5708
    c: PointOnObject(g40,g28)
    c: PointOnObject(g40,g2)
    c: Tangent(g28,g39) = 1.5708
    c: Tangent(g2,g39) = 1.5708
    c: Symmetric(g38,g40,g-2)
    c: Vertical(g38,g3)
    c: Equal(g15,g23)
    c: Radius(g15) = 3
    c: Equal(g17,g19)
    c: Radius(g17) = 3
    c: Equal(g13,g21)
    c: Radius(g13) = 3
    c: PointOnObject(g42,g9)
    c: PointOnObject(g42,g25)
    c: Tangent(g9,g41) = 1.5708
    c: Tangent(g25,g41) = -1.5708
    c: Symmetric(g34,g42,g-2)
    c: Equal(g33,g41)
    c: Radius(g33) = 3
    c: Equal(g29,g31)
    c: Radius(g29) = 3
    c: Equal(g37,g39)
    c: Radius(g37) = 3
    c: Parallel(g6,g27)
    c: Parallel(g6,g8)
    c: Distance(g36,g6) = 10
    c: Distance(g30,g6) = 10
    c: DistanceY(g-1,g38) = 20
    c: DistanceY(g-1,g34) = 40
    c: DistanceX(g16,g24) = 196
    c: DistanceX(g0,g0) = 196
FEATURE [Sketcher::SketchObject] Sketch022
  FullyConstrained = true
  MapMode = 5
  Placement = pos=(0,0,0) rot=(1,0,0;1.5708rad)
  Support = -> [XZ_Plane010]
  expr: Constraints[10] = <<Variables>>.TopThickness
  expr: Constraints[11] = <<Variables>>.GantorySpacing + <<Variables>>.CavitySpacingX * 2
  expr: Constraints[12] = <<Variables>>.GantorySpacing + <<Variables>>.CavitySpacingX * 2 + 4
  expr: Constraints[15] = <<Variables>>.GantorySpacing + <<Variables>>.CavitySpacingX * 2
  expr: Constraints[17] = <<Variables>>.GantorySpacing
  sketch-geometry (38):
    g0: LineSegment StartX=110 StartY=41.0294 StartZ=0 EndX=110 EndY=30.2426 EndZ=0
    g1: LineSegment StartX=108.757 StartY=10 StartZ=0 EndX=-108.757 EndY=10 EndZ=0
    g2: LineSegment StartX=-111.121 StartY=27.8787 StartZ=0 EndX=-110.879 EndY=28.1213 EndZ=0
    g3: LineSegment StartX=112 StartY=25.7574 StartZ=0 EndX=112 EndY=13.2426 EndZ=0
    g4: LineSegment StartX=111.121 StartY=11.1213 StartZ=0 EndX=110.879 EndY=10.8787 EndZ=0
    g5: LineSegment StartX=-112 StartY=13.2426 StartZ=0 EndX=-112 EndY=25.7574 EndZ=0
    g6: LineSegment StartX=-106.485 StartY=49.5147 StartZ=0 EndX=-101.757 EndY=54.2426 EndZ=0
    g7: LineSegment StartX=-100 StartY=60 StartZ=0 EndX=-100 EndY=58.4853 EndZ=0
    g8: LineSegment StartX=106.485 StartY=49.5147 StartZ=0 EndX=101.757 EndY=54.2426 EndZ=0
    g9: LineSegment StartX=100 StartY=60 StartZ=0 EndX=100 EndY=58.4853 EndZ=0
    g10: LineSegment StartX=110.879 StartY=28.1213 StartZ=0 EndX=111.121 EndY=27.8787 EndZ=0
    g11: LineSegment StartX=-110 StartY=30.2426 StartZ=0 EndX=-110 EndY=41.0294 EndZ=0
    g12: LineSegment StartX=-110.879 StartY=10.8787 StartZ=0 EndX=-111.121 EndY=11.1213 EndZ=0
    g13: ArcOfCircle CenterX=-98 CenterY=41.0294 CenterZ=0 NormalX=0 NormalY=0 NormalZ=1 AngleXU=0 Radius=12 StartAngle=2.35619 EndAngle=3.14159
    g14: GeomPoint X=-110 Y=46 Z=0
    g15: ArcOfCircle CenterX=98 CenterY=41.0294 CenterZ=0 NormalX=0 NormalY=0 NormalZ=1 AngleXU=0 Radius=12 StartAngle=-1.8e-15 EndAngle=0.785398
    g16: GeomPoint X=110 Y=46 Z=0
    g17: ArcOfCircle CenterX=113 CenterY=30.2426 CenterZ=0 NormalX=0 NormalY=0 NormalZ=1 AngleXU=0 Radius=3 StartAngle=3.14159 EndAngle=3.92699
    g18: GeomPoint X=110 Y=29 Z=0
    g19: ArcOfCircle CenterX=109 CenterY=25.7574 CenterZ=0 NormalX=0 NormalY=0 NormalZ=1 AngleXU=0 Radius=3 StartAngle=-9e-16 EndAngle=0.785398
    g20: GeomPoint X=112 Y=27 Z=0
    g21: ArcOfCircle CenterX=-113 CenterY=30.2426 CenterZ=0 NormalX=0 NormalY=0 NormalZ=1 AngleXU=0 Radius=3 StartAngle=5.49779 EndAngle=6.28319
    g22: GeomPoint X=-110 Y=29 Z=0
    g23: ArcOfCircle CenterX=-109 CenterY=25.7574 CenterZ=0 NormalX=0 NormalY=0 NormalZ=1 AngleXU=0 Radius=3 StartAngle=2.35619 EndAngle=3.14159
    g24: GeomPoint X=-112 Y=27 Z=0
    g25: ArcOfCircle CenterX=-109 CenterY=13.2426 CenterZ=0 NormalX=0 NormalY=0 NormalZ=1 AngleXU=0 Radius=3 StartAngle=3.14159 EndAngle=3.92699
    g26: GeomPoint X=-112 Y=12 Z=0
    g27: ArcOfCircle CenterX=-108.757 CenterY=13 CenterZ=0 NormalX=0 NormalY=0 NormalZ=1 AngleXU=0 Radius=3 StartAngle=3.92699 EndAngle=4.71239
    g28: GeomPoint X=-110 Y=10 Z=0
    g29: ArcOfCircle CenterX=109 CenterY=13.2426 CenterZ=0 NormalX=0 NormalY=0 NormalZ=1 AngleXU=0 Radius=3 StartAngle=5.49779 EndAngle=6.28319
    g30: GeomPoint X=112 Y=12 Z=0
    g31: ArcOfCircle CenterX=108.757 CenterY=13 CenterZ=0 NormalX=0 NormalY=0 NormalZ=1 AngleXU=0 Radius=3 StartAngle=4.71239 EndAngle=5.49779
    g32: GeomPoint X=110 Y=10 Z=0
    g33: ArcOfCircle CenterX=-106 CenterY=58.4853 CenterZ=0 NormalX=0 NormalY=0 NormalZ=1 AngleXU=0 Radius=6 StartAngle=5.49779 EndAngle=6.28319
    g34: GeomPoint X=-100 Y=56 Z=0
    g35: ArcOfCircle CenterX=106 CenterY=58.4853 CenterZ=0 NormalX=0 NormalY=0 NormalZ=1 AngleXU=0 Radius=6 StartAngle=3.14159 EndAngle=3.92699
    g36: GeomPoint X=100 Y=56 Z=0
    g37: LineSegment StartX=-100 StartY=60 StartZ=0 EndX=100 EndY=60 EndZ=0
  constraints (83):
    c: Symmetric(g28,g32,g-2)
    c: Symmetric(g26,g30,g-2)
    c: Symmetric(g24,g20,g-2)
    c: Symmetric(g22,g18,g-2)
    c: Symmetric(g14,g16,g-2)
    c: Symmetric(g34,g36,g-2)
    c: Symmetric(g7,g9,g-2)
    c: Vertical(g5)
    c: Vertical(g11)
    c: Vertical(g7)
    c: DistanceY(g-1,g28) = 10
    c: DistanceX(g28,g32) = 220
    c: DistanceX(g26,g30) = 224
    c: Angle(g12) = 2.35619
    c: Angle(g2) = 0.785398
    c: DistanceX(g22,g18) = 220
    c: Angle(g6) = 0.785398
    c: DistanceX(g7,g9) = 200
    c: DistanceY(g28,g22) = 19
    c: DistanceY(g-1,g7) = 60
    c: DistanceY(g28,g14) = 36
    c: PointOnObject(g14,g6)
    c: PointOnObject(g14,g11)
    c: Tangent(g6,g13) = 1.5708
    c: Tangent(g11,g13) = 1.5708
    c: PointOnObject(g16,g8)
    c: PointOnObject(g16,g0)
    c: Tangent(g8,g15) = -1.5708
    c: Tangent(g0,g15) = 1.5708
    c: Equal(g13,g15)
    c: Radius(g13) = 12
    c: PointOnObject(g18,g0)
    c: PointOnObject(g18,g10)
    c: Tangent(g0,g17) = -1.5708
    c: Tangent(g10,g17) = -1.5708
    c: PointOnObject(g20,g10)
    c: PointOnObject(g20,g3)
    c: Tangent(g10,g19) = 1.5708
    c: Tangent(g3,g19) = 1.5708
    c: PointOnObject(g22,g11)
    c: PointOnObject(g22,g2)
    c: Tangent(g11,g21) = -1.5708
    c: Tangent(g2,g21) = -1.5708
    c: PointOnObject(g24,g2)
    c: PointOnObject(g24,g5)
    c: Tangent(g2,g23) = 1.5708
    c: Tangent(g5,g23) = 1.5708
    c: Equal(g17,g19)
    c: Equal(g17,g21)
    c: Equal(g17,g23)
    c: Radius(g17) = 3
    c: PointOnObject(g26,g5)
    c: PointOnObject(g26,g12)
    c: Tangent(g5,g25) = 1.5708
    c: Tangent(g12,g25) = 1.5708
    c: PointOnObject(g28,g12)
    c: PointOnObject(g28,g1)
    c: Tangent(g12,g27) = 1.5708
    c: Tangent(g1,g27) = 1.5708
    c: PointOnObject(g30,g3)
    c: PointOnObject(g30,g4)
    c: Tangent(g3,g29) = 1.5708
    c: Tangent(g4,g29) = 1.5708
    c: PointOnObject(g32,g4)
    c: PointOnObject(g32,g1)
    c: Tangent(g4,g31) = 1.5708
    c: Tangent(g1,g31) = 1.5708
    c: Equal(g25,g27)
    c: Equal(g25,g29)
    c: Equal(g25,g31)
    c: Radius(g25) = 3
    c: PointOnObject(g34,g6)
    c: PointOnObject(g34,g7)
    c: Tangent(g6,g33) = -1.5708
    c: Tangent(g7,g33) = 1.5708
    c: PointOnObject(g36,g9)
    c: PointOnObject(g36,g8)
    c: Tangent(g9,g35) = -1.5708
    c: Tangent(g8,g35) = 1.5708
    c: Equal(g33,g35)
    c: Radius(g33) = 6
    c: Coincident(g37,g7)
    c: Coincident(g37,g9)
FEATURE [Sketcher::SketchObject] Sketch023
  FullyConstrained = true
  MapMode = 5
  Placement = pos=(0,0,0) rot=(0.57735,0.57735,0.57735;2.0944rad)
  Support = -> [YZ_Plane010]
  expr: Constraints[16] = <<Variables>>.TopThickness
  expr: Constraints[17] = <<Variables>>.GantorySpacing - 12
  expr: Constraints[18] = <<Variables>>.GantorySpacing - 20
  expr: Constraints[19] = <<Variables>>.TopThickness + 17 + 19 - 6
  expr: Constraints[21] = <<Variables>>.GantorySpacing + <<Variables>>.CavitySpacingY * 2
  sketch-geometry (12):
    g0: LineSegment StartX=-110 StartY=60 StartZ=0 EndX=-90 EndY=60 EndZ=0
    g1: LineSegment StartX=110 StartY=45 StartZ=0 EndX=110 EndY=26 EndZ=0
    g2: LineSegment StartX=94 StartY=10 StartZ=0 EndX=-94 EndY=10 EndZ=0
    g3: LineSegment StartX=-110 StartY=26 StartZ=0 EndX=-110 EndY=60 EndZ=0
    g4: LineSegment StartX=-110 StartY=26 StartZ=0 EndX=-94 EndY=10 EndZ=0
    g5: LineSegment StartX=94 StartY=10 StartZ=0 EndX=110 EndY=26 EndZ=0
    g6: LineSegment StartX=-70 StartY=40 StartZ=0 EndX=70 EndY=40 EndZ=0
    g7: LineSegment StartX=-90 StartY=60 StartZ=0 EndX=-70 EndY=40 EndZ=0
    g8: LineSegment StartX=70 StartY=40 StartZ=0 EndX=90 EndY=60 EndZ=0
    g9: LineSegment StartX=90 StartY=60 StartZ=0 EndX=100 EndY=60 EndZ=0
    g10: LineSegment StartX=110 StartY=45 StartZ=0 EndX=100 EndY=55 EndZ=0
    g11: LineSegment StartX=100 StartY=60 StartZ=0 EndX=100 EndY=55 EndZ=0
  constraints (32):
    c: Coincident(g2,g4)
    c: Coincident(g3,g4)
    c: Coincident(g1,g5)
    c: Coincident(g5,g2)
    c: Coincident(g7,g0)
    c: Coincident(g7,g6)
    c: Coincident(g8,g6)
    c: Coincident(g9,g8)
    c: Symmetric(g2,g2,g-2)
    c: Symmetric(g3,g1,g-2)
    c: Symmetric(g0,g8,g-2)
    c: Symmetric(g6,g6,g-2)
    c: Vertical(g3)
    c: Angle(g4) = -0.785398
    c: Angle(g7) = -0.785398
    c: Horizontal(g0)
    c: DistanceY(g-1,g2) = 10
    c: DistanceX(g2,g2) = 188
    c: DistanceX(g0,g8) = 180
    c: DistanceY(g-1,g6) = 40
    c: Angle(g10) = 2.35619
    c: DistanceX(g3,g1) = 220
    c: Vertical(g11)
    c: DistanceY(g-1,g0) = 60
    c: Coincident(g10,g1)
    c: Coincident(g9,g11)
    c: Horizontal(g9)
    c: Coincident(g10,g11)
    c: Vertical(g1)
    c: Coincident(g3,g0)
    c: DistanceX(g9,g1) = 10
    c: DistanceY(g1,g9) = 15
FEATURE [Part::FeaturePython] MGN9_Z  # link proxy (typed FeaturePython)
  Length = 175
  LinkedObject = -> <external ../../AppData/Local/Temp/FreeCAD/Cache/FreeCAD_Doc_5f10fd76-f536-416b-8568-16cb6060fa77_da39a3_1616>#Assembly
  Placement = pos=(-1.27554e-05,107,-135) rot=(-0.57735,0.57735,-0.57735;4.18879rad)
  Position = 50
  SourceObject = -> <external MGN9.FCStd>#Assembly
FEATURE [Sketcher::SketchObject] Sketch025
  AttachmentOffset = pos=(0,0,117) rot=(0,0,1;0rad)
  FullyConstrained = true
  MapMode = 5
  Placement = pos=(117,-2.6e-14,2.6e-14) rot=(0.57735,0.57735,0.57735;2.0944rad)
  Support = -> [YZ_Plane010]
  expr: .AttachmentOffset.Base.z = (<<Variables>>.GantorySpacing + 20) / 2 + <<Variables>>.WallThickness
  expr: Constraints[16] = <<Variables>>.GantorySpacing + (<<Variables>>.CavitySpacingY + <<Variables>>.WallThickness) * 2
  expr: Constraints[39] = <<Variables>>.GantorySpacing + 10
  sketch-geometry (15):
    g0: LineSegment StartX=-117 StartY=60 StartZ=0 EndX=-27 EndY=60 EndZ=0
    g1: LineSegment StartX=-27 StartY=60 StartZ=0 EndX=-21.2265 EndY=50 EndZ=0
    g2: LineSegment StartX=-21.2265 StartY=50 StartZ=0 EndX=-8.7735 EndY=50 EndZ=0
    g3: LineSegment StartX=-8.7735 StartY=50 StartZ=0 EndX=-3 EndY=60 EndZ=0
    g4: LineSegment StartX=-3 StartY=60 StartZ=0 EndX=117 EndY=60 EndZ=0
    g5: LineSegment StartX=117 StartY=60 StartZ=0 EndX=117 EndY=100 EndZ=0
    g6: LineSegment StartX=117 StartY=100 StartZ=0 EndX=-117 EndY=100 EndZ=0
    g7: LineSegment StartX=-117 StartY=100 StartZ=0 EndX=-117 EndY=60 EndZ=0
    g8: LineSegment StartX=-15 StartY=0 StartZ=0 EndX=-15 EndY=100 EndZ=0
    g9: Circle CenterX=-15 CenterY=55 CenterZ=0 NormalX=0 NormalY=0 NormalZ=1 AngleXU=0 Radius=0.5
    g10: LineSegment StartX=-117 StartY=55 StartZ=0 EndX=117 EndY=55 EndZ=0
    g11: Circle CenterX=-55 CenterY=55 CenterZ=0 NormalX=0 NormalY=0 NormalZ=1 AngleXU=0 Radius=0.5
    g12: Circle CenterX=55 CenterY=55 CenterZ=0 NormalX=0 NormalY=0 NormalZ=1 AngleXU=0 Radius=0.5
    g13: Circle CenterX=105 CenterY=25 CenterZ=0 NormalX=0 NormalY=0 NormalZ=1 AngleXU=0 Radius=0.5
    g14: Circle CenterX=-105 CenterY=25 CenterZ=0 NormalX=0 NormalY=0 NormalZ=1 AngleXU=0 Radius=0.5
  constraints (40):
    c: Horizontal(g0)
    c: Coincident(g0,g1)
    c: Coincident(g1,g2)
    c: Coincident(g2,g3)
    c: Coincident(g3,g4)
    c: Coincident(g4,g5)
    c: Coincident(g5,g6)
    c: Coincident(g6,g7)
    c: Coincident(g7,g0)
    c: Vertical(g7)
    c: Angle(g1) = -1.0472
    c: Symmetric(g0,g4,g-2)
    c: Symmetric(g6,g5,g-2)
    c: DistanceY(g0) = 60
    c: DistanceY(g6) = 100
    c: DistanceX(g0,g3) = 24
    c: DistanceX(g6,g6) = 234
    c: DistanceY(g1,g0) = 10
    c: PointOnObject(g8,g-1)
    c: Vertical(g8)
    c: PointOnObject(g8,g6)
    c: DistanceX(g8) = -15
    c: Symmetric(g1,g2,g8)
    c: Symmetric(g0,g3,g8)
    c: PointOnObject(g9,g8)
    c: Diameter(g9) = 1
    c: Symmetric(g10,g10,g-2)
    c: PointOnObject(g10,g7)
    c: DistanceY(g10) = 55
    c: PointOnObject(g9,g10)
    c: Equal(g11,g9)
    c: Equal(g9,g12)
    c: PointOnObject(g11,g10)
    c: DistanceX(g11,g12) = 110
    c: Symmetric(g11,g12,g-2)
    c: DistanceY(g13) = 25
    c: Equal(g13,g9)
    c: Equal(g9,g14)
    c: Symmetric(g14,g13,g-2)
    c: DistanceX(g14,g13) = 210
FEATURE [Sketcher::SketchObject] Sketch026
  FullyConstrained = true
  MapMode = 5
  Placement = pos=(0,0,0) rot=(0.57735,0.57735,0.57735;2.0944rad)
  Support = -> [YZ_Plane015]
  expr: Constraints[16] = <<Variables>>.WallThickness
  expr: Constraints[19] = -<<Variables>>.WallThickness
  expr: Constraints[56] = <<Variables>>.WallThickness
  expr: Constraints[57] = <<Variables>>.GantorySpacing + <<Variables>>.CavitySpacingY * 2
  sketch-geometry (25):
    g0: LineSegment StartX=-110 StartY=15 StartZ=0 EndX=-115 EndY=15 EndZ=0
    g1: LineSegment StartX=-117 StartY=13 StartZ=0 EndX=-115 EndY=15 EndZ=0
    g2: LineSegment StartX=-117 StartY=13 StartZ=0 EndX=-117 EndY=-2 EndZ=0
    g3: LineSegment StartX=-117 StartY=-2 StartZ=0 EndX=-112 EndY=-7 EndZ=0
    g4: LineSegment StartX=-112 StartY=-7 StartZ=0 EndX=112 EndY=-7 EndZ=0
    g5: LineSegment StartX=112 StartY=-7 StartZ=0 EndX=117 EndY=-2 EndZ=0
    g6: LineSegment StartX=117 StartY=-2 StartZ=0 EndX=117 EndY=10 EndZ=0
    g7: LineSegment StartX=117 StartY=10 StartZ=0 EndX=105 EndY=10 EndZ=0
    g8: LineSegment StartX=-110 StartY=10 StartZ=0 EndX=-110 EndY=15 EndZ=0
    g9: LineSegment StartX=-40 StartY=0 StartZ=0 EndX=-95 EndY=0 EndZ=0
    g10: LineSegment StartX=-33 StartY=7 StartZ=0 EndX=-40 EndY=0 EndZ=0
    g11: LineSegment StartX=-29.5 StartY=7 StartZ=0 EndX=-33 EndY=7 EndZ=0
    g12: LineSegment StartX=-2 StartY=0 StartZ=0 EndX=-28 EndY=0 EndZ=0
    g13: LineSegment StartX=3 StartY=7 StartZ=0 EndX=-0.5 EndY=7 EndZ=0
    g14: LineSegment StartX=10 StartY=0 StartZ=0 EndX=3 EndY=7 EndZ=0
    g15: LineSegment StartX=-95 StartY=0 StartZ=0 EndX=-105 EndY=10 EndZ=0
    g16: LineSegment StartX=-105 StartY=10 StartZ=0 EndX=-110 EndY=10 EndZ=0
    g17: LineSegment StartX=-28 StartY=0 StartZ=0 EndX=-28 EndY=5.5 EndZ=0
    g18: LineSegment StartX=-28 StartY=5.5 StartZ=0 EndX=-29.5 EndY=7 EndZ=0
    g19: LineSegment StartX=-0.5 StartY=7 StartZ=0 EndX=-2 EndY=5.5 EndZ=0
    g20: LineSegment StartX=-2 StartY=5.5 StartZ=0 EndX=-2 EndY=0 EndZ=0
    g21: LineSegment StartX=105 StartY=10 StartZ=0 EndX=95 EndY=0 EndZ=0
    g22: LineSegment StartX=95 StartY=0 StartZ=0 EndX=10 EndY=0 EndZ=0
    g23: GeomPoint X=110 Y=10 Z=0
    g24: LineSegment StartX=-15 StartY=60 StartZ=0 EndX=-15 EndY=-60 EndZ=0
  constraints (66):
    c: Coincident(g9,g15)
    c: Coincident(g8,g0)
    c: Horizontal(g0)
    c: Vertical(g2)
    c: Coincident(g2,g3)
    c: Coincident(g3,g4)
    c: Coincident(g4,g5)
    c: Coincident(g5,g6)
    c: Vertical(g6)
    c: Coincident(g6,g7)
    c: Horizontal(g7)
    c: Angle(g5) = 0.785398
    c: Angle(g3) = -0.785398
    c: Angle(g1) = 0.785398
    c: Coincident(g0,g1)
    c: Coincident(g2,g1)
    c: DistanceX(g1,g8) = 7
    c: DistanceX(g1,g1) = 2
    c: DistanceX(g3,g3) = 5
    c: DistanceY(g3) = -7
    c: DistanceY(g0) = 15
    c: DistanceY(g6) = 10
    c: Coincident(g16,g8)
    c: Vertical(g8)
    c: Coincident(g10,g9)
    c: Coincident(g11,g10)
    c: Coincident(g18,g11)
    c: Coincident(g12,g17)
    c: Coincident(g20,g12)
    c: Coincident(g13,g19)
    c: Coincident(g14,g13)
    c: Coincident(g22,g14)
    c: Coincident(g15,g16)
    c: Parallel(g15,g3)
    c: Coincident(g17,g18)
    c: Coincident(g19,g20)
    c: Coincident(g21,g7)
    c: Coincident(g21,g22)
    c: Symmetric(g9,g21,g-2)
    c: Symmetric(g15,g7,g-2)
    c: Horizontal(g16)
    c: PointOnObject(g9,g-1)
    c: PointOnObject(g9,g-1)
    c: PointOnObject(g12,g-1)
    c: Parallel(g10,g1)
    c: Horizontal(g11)
    c: Vertical(g17)
    c: Parallel(g18,g3)
    c: DistanceX(g12,g12) = 26
    c: DistanceX(g11,g17) = 1.5
    c: DistanceX(g10,g17) = 5
    c: DistanceY(g10) = 7
    c: DistanceX(g16,g16) = 5
    c: Symmetric(g4,g3,g-2)
    c: Symmetric(g2,g5,g-2)
    c: PointOnObject(g23,g7)
    c: DistanceX(g23,g6) = 7
    c: DistanceX(g8,g23) = 220
    c: Symmetric(g24,g24,g-1)
    c: DistanceX(g24) = -15
    c: DistanceY(g24) = -60
    c: Symmetric(g12,g12,g24)
    c: Symmetric(g17,g19,g24)
    c: Symmetric(g11,g13,g24)
    c: Symmetric(g10,g13,g24)
    c: Symmetric(g9,g14,g24)
FEATURE [Sketcher::SketchObject] Sketch027
  FullyConstrained = true
  MapMode = 5
  Placement = pos=(0,0,0) rot=(1,0,0;1.5708rad)
  Support = -> [XZ_Plane010]
  expr: Constraints[13] = <<Variables>>.GantorySpacing + (<<Variables>>.CavitySpacingY + <<Variables>>.WallThickness) * 2
  sketch-geometry (6):
    g0: LineSegment StartX=-117 StartY=2 StartZ=0 EndX=-115 EndY=0 EndZ=0
    g1: LineSegment StartX=-115 StartY=0 StartZ=0 EndX=115 EndY=0 EndZ=0
    g2: LineSegment StartX=115 StartY=0 StartZ=0 EndX=117 EndY=2 EndZ=0
    g3: LineSegment StartX=117 StartY=2 StartZ=0 EndX=117 EndY=-2 EndZ=0
    g4: LineSegment StartX=117 StartY=-2 StartZ=0 EndX=-117 EndY=-2 EndZ=0
    g5: LineSegment StartX=-117 StartY=-2 StartZ=0 EndX=-117 EndY=2 EndZ=0
  constraints (14):
    c: Coincident(g0,g1)
    c: Coincident(g1,g2)
    c: Coincident(g2,g3)
    c: Coincident(g3,g4)
    c: Coincident(g4,g5)
    c: Coincident(g5,g0)
    c: Angle(g0) = -0.785398
    c: PointOnObject(g0,g-1)
    c: Symmetric(g0,g1,g-2)
    c: Symmetric(g0,g2,g-2)
    c: Symmetric(g4,g3,g-2)
    c: Symmetric(g4,g0,g-1)
    c: DistanceX(g0,g0) = 2
    c: DistanceX(g4,g4) = 234
FEATURE [Sketcher::SketchObject] Sketch028
  FullyConstrained = true
  MapMode = 5
  Support = -> [XY_Plane010]
  expr: Constraints[24] = <<Variables>>.GantorySpacing
  expr: Constraints[25] = <<Variables>>.GantorySpacing
  expr: Constraints[26] = <<Variables>>.GantorySpacing + <<Variables>>.CavitySpacingX * 2
  expr: Constraints[27] = <<Variables>>.GantorySpacing + <<Variables>>.CavitySpacingY * 2
  sketch-geometry (32):
    g0: ArcOfCircle CenterX=-100 CenterY=-100 CenterZ=0 NormalX=0 NormalY=0 NormalZ=1 AngleXU=0 Radius=6 StartAngle=-9e-16 EndAngle=2.73056
    g1: LineSegment StartX=-94 StartY=-100 StartZ=0 EndX=-94 EndY=-109.5 EndZ=0
    g2: ArcOfCircle CenterX=100 CenterY=-100 CenterZ=0 NormalX=0 NormalY=0 NormalZ=1 AngleXU=0 Radius=6 StartAngle=0.411029 EndAngle=3.14159
    g3: ArcOfCircle CenterX=-100 CenterY=100 CenterZ=0 NormalX=0 NormalY=0 NormalZ=1 AngleXU=0 Radius=6 StartAngle=3.55262 EndAngle=6.28319
    g4: ArcOfCircle CenterX=100 CenterY=100 CenterZ=0 NormalX=0 NormalY=0 NormalZ=1 AngleXU=0 Radius=6 StartAngle=3.14159 EndAngle=5.87216
    g5: LineSegment StartX=94 StartY=-100 StartZ=0 EndX=94 EndY=-109.5 EndZ=0
    g6: LineSegment StartX=94 StartY=100 StartZ=0 EndX=94 EndY=107 EndZ=0
    g7: LineSegment StartX=-94 StartY=107 StartZ=0 EndX=-94 EndY=100 EndZ=0
    g8: LineSegment StartX=-110 StartY=110 StartZ=0 EndX=-91 EndY=110 EndZ=0
    g9: LineSegment StartX=-107.936 StartY=98.064 StartZ=0 EndX=-110 EndY=96 EndZ=0
    g10: LineSegment StartX=-110 StartY=96 StartZ=0 EndX=-110 EndY=110 EndZ=0
    g11: LineSegment StartX=110 StartY=110 StartZ=0 EndX=110 EndY=96 EndZ=0
    g12: LineSegment StartX=110 StartY=96 StartZ=0 EndX=107.936 EndY=98.064 EndZ=0
    g13: LineSegment StartX=91 StartY=110 StartZ=0 EndX=110 EndY=110 EndZ=0
    g14: LineSegment StartX=-110 StartY=-110 StartZ=0 EndX=-110 EndY=-96 EndZ=0
    g15: LineSegment StartX=-110 StartY=-96 StartZ=0 EndX=-107.936 EndY=-98.064 EndZ=0
    g16: LineSegment StartX=-94.5 StartY=-110 StartZ=0 EndX=-110 EndY=-110 EndZ=0
    g17: LineSegment StartX=110 StartY=-110 StartZ=0 EndX=110 EndY=-96 EndZ=0
    g18: LineSegment StartX=110 StartY=-96 StartZ=0 EndX=107.936 EndY=-98.064 EndZ=0
    g19: LineSegment StartX=94.5 StartY=-110 StartZ=0 EndX=110 EndY=-110 EndZ=0
    g20: ArcOfCircle CenterX=-106.875 CenterY=-97.0034 CenterZ=0 NormalX=0 NormalY=0 NormalZ=1 AngleXU=0 Radius=1.5 StartAngle=3.92699 EndAngle=5.87216
    g21: ArcOfCircle CenterX=-94.5 CenterY=-109.5 CenterZ=0 NormalX=0 NormalY=0 NormalZ=1 AngleXU=0 Radius=0.5 StartAngle=4.71239 EndAngle=6.28319
    g22: ArcOfCircle CenterX=-106.875 CenterY=97.0034 CenterZ=0 NormalX=0 NormalY=0 NormalZ=1 AngleXU=0 Radius=1.5 StartAngle=0.411029 EndAngle=2.35619
    g23: ArcOfCircle CenterX=-91 CenterY=107 CenterZ=0 NormalX=0 NormalY=0 NormalZ=1 AngleXU=0 Radius=3 StartAngle=1.5708 EndAngle=3.14159
    g24: ArcOfCircle CenterX=91 CenterY=107 CenterZ=0 NormalX=0 NormalY=0 NormalZ=1 AngleXU=0 Radius=3 StartAngle=1.5e-15 EndAngle=1.5708
    g25: ArcOfCircle CenterX=106.875 CenterY=97.0034 CenterZ=0 NormalX=0 NormalY=0 NormalZ=1 AngleXU=0 Radius=1.5 StartAngle=0.785398 EndAngle=2.73056
    g26: ArcOfCircle CenterX=94.5 CenterY=-109.5 CenterZ=0 NormalX=0 NormalY=0 NormalZ=1 AngleXU=0 Radius=0.5 StartAngle=3.14159 EndAngle=4.71239
    g27: ArcOfCircle CenterX=106.875 CenterY=-97.0034 CenterZ=0 NormalX=0 NormalY=0 NormalZ=1 AngleXU=0 Radius=1.5 StartAngle=3.55262 EndAngle=5.49779
    g28: Circle CenterX=-100 CenterY=100 CenterZ=0 NormalX=0 NormalY=0 NormalZ=1 AngleXU=0 Radius=1.25
    g29: Circle CenterX=100 CenterY=100 CenterZ=0 NormalX=0 NormalY=0 NormalZ=1 AngleXU=0 Radius=1.25
    g30: Circle CenterX=-100 CenterY=-100 CenterZ=0 NormalX=0 NormalY=0 NormalZ=1 AngleXU=0 Radius=1.25
    g31: Circle CenterX=100 CenterY=-100 CenterZ=0 NormalX=0 NormalY=0 NormalZ=1 AngleXU=0 Radius=1.25
  constraints (68):
    c: Coincident(g9,g10)
    c: Coincident(g10,g8)
    c: Coincident(g11,g12)
    c: Coincident(g13,g11)
    c: Coincident(g14,g15)
    c: Coincident(g16,g14)
    c: Coincident(g17,g18)
    c: Coincident(g19,g17)
    c: Tangent(g20,g15) = -1.5708
    c: Tangent(g20,g0) = 1.5708
    c: Tangent(g22,g3) = 1.5708
    c: Tangent(g9,g22) = -1.5708
    c: Tangent(g8,g23) = 1.5708
    c: Tangent(g23,g7) = -1.5708
    c: Tangent(g24,g13) = 1.5708
    c: Tangent(g24,g6) = -1.5708
    c: Tangent(g12,g25) = -1.5708
    c: Tangent(g25,g4) = 1.5708
    c: Tangent(g18,g27) = 1.5708
    c: Tangent(g27,g2) = 1.5708
    c: Tangent(g2,g5) = -1.5708
    c: Tangent(g3,g7) = 1.5708
    c: Tangent(g4,g6) = 1.5708
    c: Tangent(g0,g1) = 1.5708
    c: DistanceX(g0,g2) = 200
    c: DistanceY(g0,g3) = 200
    c: DistanceX(g14,g17) = 220
    c: DistanceY(g14,g8) = 220
    c: Angle(g15) = -0.785398
    c: DistanceY(g14,g14) = 14
    c: Vertical(g14)
    c: Horizontal(g16)
    c: Vertical(g1)
    c: Diameter(g0) = 12
    c: Diameter(g20) = 3
    c: Diameter(g21) = 1
    c: Symmetric(g14,g17,g-2)
    c: Symmetric(g14,g8,g-1)
    c: Symmetric(g14,g11,g-1)
    c: Symmetric(g14,g17,g-2)
    c: Symmetric(g14,g9,g-1)
    c: Symmetric(g14,g11,g-1)
    c: Symmetric(g0,g2,g-2)
    c: Symmetric(g0,g3,g-1)
    c: Symmetric(g0,g4,g-1)
    c: Symmetric(g16,g19,g-2)
    c: Symmetric(g15,g18,g-2)
    c: Symmetric(g15,g9,g-1)
    c: Symmetric(g15,g12,g-1)
    c: Symmetric(g1,g5,g-2)
    c: Diameter(g23) = 6
    c: Tangent(g21,g16) = 1.5708
    c: Tangent(g21,g1) = 1.5708
    c: Tangent(g26,g19) = -1.5708
    c: Tangent(g26,g5) = -1.5708
    c: Symmetric(g8,g13,g-2)
    c: Symmetric(g7,g6,g-2)
    c: Vertical(g7)
    c: Horizontal(g8)
    c: Equal(g0,g3)
    c: Coincident(g28,g3)
    c: Coincident(g29,g4)
    c: Coincident(g30,g0)
    c: Coincident(g31,g2)
    c: Equal(g28,g29)
    c: Equal(g28,g30)
    c: Equal(g28,g31)
    c: Diameter(g28) = 2.5
FEATURE [Sketcher::SketchObject] Sketch029
  AttachmentOffset = pos=(0,0,-185) rot=(0,0,1;0rad)
  FullyConstrained = true
  MapMode = 5
  Placement = pos=(-185,4.11e-14,-4.11e-14) rot=(0.57735,0.57735,0.57735;2.0944rad)
  Support = -> [YZ_Plane015]
  expr: Constraints[1] = <<Variables>>.GantorySpacing
  sketch-geometry (6):
    g0: ArcOfCircle CenterX=-100 CenterY=10 CenterZ=0 NormalX=0 NormalY=0 NormalZ=1 AngleXU=0 Radius=15 StartAngle=0 EndAngle=1.5708
    g1: ArcOfCircle CenterX=100 CenterY=10 CenterZ=0 NormalX=0 NormalY=0 NormalZ=1 AngleXU=0 Radius=15 StartAngle=1.5708 EndAngle=3.14159
    g2: LineSegment StartX=-100 StartY=25 StartZ=0 EndX=-100 EndY=10 EndZ=0
    g3: LineSegment StartX=-100 StartY=10 StartZ=0 EndX=-85 EndY=10 EndZ=0
    g4: LineSegment StartX=85 StartY=10 StartZ=0 EndX=100 EndY=10 EndZ=0
    g5: LineSegment StartX=100 StartY=25 StartZ=0 EndX=100 EndY=10 EndZ=0
  constraints (17):
    c: Symmetric(g0,g1,g-2)
    c: DistanceX(g0,g1) = 200
    c: DistanceY(g0) = 10
    c: Coincident(g0,g2)
    c: Coincident(g3,g2)
    c: Coincident(g0,g3)
    c: Coincident(g1,g5)
    c: Coincident(g1,g4)
    c: Coincident(g4,g5)
    c: Equal(g0,g1)
    c: Diameter(g0) = 30
    c: Symmetric(g2,g4,g-2)
    c: Vertical(g2)
    c: Horizontal(g3)
    c: Coincident(g2,g0)
    c: Vertical(g5)
    c: Horizontal(g4)
FEATURE [Sketcher::SketchObject] Sketch030
  AttachmentOffset = pos=(0,0,60) rot=(0,0,1;0rad)
  FullyConstrained = true
  MapMode = 5
  Placement = pos=(0,0,60) rot=(0,0,1;0rad)
  Support = -> [XY_Plane010]
  expr: Constraints[14] = <<Variables>>.GantorySpacing + <<Variables>>.CavitySpacingX * 2
  expr: Constraints[23] = Variables.GantorySpacing + (<<Variables>>.CavitySpacingX + <<Variables>>.WallThickness) * 2
  expr: Constraints[24] = <<Variables>>.GantorySpacing / 2 + <<Variables>>.CavitySpacingY
  expr: Constraints[41] = Variables.GantorySpacing / 2 - 6
  expr: Constraints[49] = <<Variables>>.WallThickness
  sketch-geometry (22):
    g0: LineSegment StartX=-110 StartY=122 StartZ=0 EndX=-76.5 EndY=122 EndZ=0
    g1: LineSegment StartX=110 StartY=94 StartZ=0 EndX=-110 EndY=94 EndZ=0
    g2: LineSegment StartX=-110 StartY=94 StartZ=0 EndX=-110 EndY=122 EndZ=0
    g3: LineSegment StartX=76.5 StartY=122 StartZ=0 EndX=110 EndY=122 EndZ=0
    g4: LineSegment StartX=110 StartY=122 StartZ=0 EndX=110 EndY=94 EndZ=0
    g5: LineSegment StartX=-27 StartY=110 StartZ=0 EndX=27 EndY=110 EndZ=0
    g6: LineSegment StartX=27 StartY=110 StartZ=0 EndX=27 EndY=100 EndZ=0
    g7: LineSegment StartX=-27 StartY=100 StartZ=0 EndX=-27 EndY=110 EndZ=0
    g8: LineSegment StartX=-117 StartY=110 StartZ=0 EndX=117 EndY=110 EndZ=0
    g9: LineSegment StartX=-117 StartY=100 StartZ=0 EndX=117 EndY=100 EndZ=0
    g10: LineSegment StartX=-77 StartY=116.5 StartZ=0 EndX=-77 EndY=110 EndZ=0
    g11: LineSegment StartX=-77 StartY=110 StartZ=0 EndX=-53 EndY=110 EndZ=0
    g12: LineSegment StartX=-53 StartY=110 StartZ=0 EndX=-53 EndY=100 EndZ=0
    g13: LineSegment StartX=-53 StartY=100 StartZ=0 EndX=-27 EndY=100 EndZ=0
    g14: LineSegment StartX=27 StartY=100 StartZ=0 EndX=53 EndY=100 EndZ=0
    g15: LineSegment StartX=53 StartY=100 StartZ=0 EndX=53 EndY=110 EndZ=0
    g16: LineSegment StartX=53 StartY=110 StartZ=0 EndX=77 EndY=110 EndZ=0
    g17: LineSegment StartX=76.5 StartY=117 StartZ=0 EndX=76.5 EndY=122 EndZ=0
    g18: ArcOfCircle CenterX=-76.5 CenterY=116.5 CenterZ=0 NormalX=0 NormalY=0 NormalZ=1 AngleXU=0 Radius=0.5 StartAngle=1.5708 EndAngle=3.14159
    g19: LineSegment StartX=-76.5 StartY=122 StartZ=0 EndX=-76.5 EndY=117 EndZ=0
    g20: ArcOfCircle CenterX=76.5 CenterY=116.5 CenterZ=0 NormalX=0 NormalY=0 NormalZ=1 AngleXU=0 Radius=0.5 StartAngle=9e-16 EndAngle=1.5708
    g21: LineSegment StartX=77 StartY=110 StartZ=0 EndX=77 EndY=116.5 EndZ=0
  constraints (57):
    c: Coincident(g1,g2)
    c: Coincident(g2,g0)
    c: Horizontal(g0)
    c: Vertical(g2)
    c: Coincident(g3,g4)
    c: Coincident(g17,g3)
    c: Coincident(g5,g6)
    c: Coincident(g7,g5)
    c: Symmetric(g5,g5,g-2)
    c: Vertical(g7)
    c: Symmetric(g7,g6,g-2)
    c: Symmetric(g0,g3,g-2)
    c: Symmetric(g0,g3,g-2)
    c: Symmetric(g1,g4,g-2)
    c: DistanceX(g0,g3) = 220
    c: DistanceX(g5,g5) = 54
    c: Coincident(g1,g4)
    c: Coincident(g12,g11)
    c: Coincident(g13,g7)
    c: Coincident(g14,g6)
    c: Coincident(g15,g16)
    c: Symmetric(g11,g16,g-2)
    c: Symmetric(g8,g8,g-2)
    c: DistanceX(g8,g8) = 234
    c: DistanceY(g8) = 110
    c: Symmetric(g9,g9,g-2)
    c: Equal(g8,g9)
    c: DistanceY(g9,g8) = 10
    c: PointOnObject(g5,g8)
    c: Coincident(g10,g11)
    c: Vertical(g10)
    c: Coincident(g12,g13)
    c: Coincident(g14,g15)
    c: PointOnObject(g10,g8)
    c: PointOnObject(g11,g8)
    c: Vertical(g12)
    c: Symmetric(g10,g16,g-2)
    c: Symmetric(g12,g14,g-2)
    c: DistanceX(g11,g11) = 24
    c: PointOnObject(g12,g9)
    c: PointOnObject(g7,g9)
    c: DistanceY(g1) = 94
    c: DistanceX(g1,g10) = 33
    c: Tangent(g18,g10) = -1.5708
    c: Coincident(g19,g0)
    c: Vertical(g19)
    c: PointOnObject(g18,g19)
    c: Coincident(g18,g19)
    c: Diameter(g18) = 1
    c: DistanceY(g10,g18) = 7
    c: DistanceY(g19,g19) = 5
    c: Coincident(g20,g17)
    c: Coincident(g21,g16)
    c: Tangent(g21,g20) = -1.5708
    c: PointOnObject(g20,g17)
    c: Symmetric(g18,g20,g-2)
    c: Equal(g20,g18)
FEATURE [Sketcher::SketchObject] Sketch031
  AttachmentOffset = pos=(0,0,-117) rot=(0,0,1;0rad)
  FullyConstrained = true
  MapMode = 5
  Placement = pos=(0,117,2.6e-14) rot=(1,0,0;1.5708rad)
  Support = -> [XZ_Plane010]
  expr: .AttachmentOffset.Base.z = -(<<Variables>>.GantorySpacing / 2 + Variables.CavitySpacingY + <<Variables>>.WallThickness)
  expr: Constraints[26] = <<Variables>>.GantorySpacing + <<Variables>>.CavitySpacingX * 2
  expr: Constraints[68] = <<Variables>>.PullyDiameterDrive + <<Variables>>.PullyDiameterIdler
  sketch-geometry (39):
    g0: LineSegment StartX=-110 StartY=100 StartZ=0 EndX=-110 EndY=60 EndZ=0
    g1: LineSegment StartX=-110 StartY=60 StartZ=0 EndX=-50 EndY=60 EndZ=0
    g2: LineSegment StartX=-50 StartY=60 StartZ=0 EndX=-44.2265 EndY=50 EndZ=0
    g3: LineSegment StartX=-44.2265 StartY=50 StartZ=0 EndX=-35.7735 EndY=50 EndZ=0
    g4: LineSegment StartX=-35.7735 StartY=50 StartZ=0 EndX=-30 EndY=60 EndZ=0
    g5: LineSegment StartX=-30 StartY=60 StartZ=0 EndX=30 EndY=60 EndZ=0
    g6: LineSegment StartX=30 StartY=60 StartZ=0 EndX=35.7735 EndY=50 EndZ=0
    g7: LineSegment StartX=35.7735 StartY=50 StartZ=0 EndX=44.2265 EndY=50 EndZ=0
    g8: LineSegment StartX=44.2265 StartY=50 StartZ=0 EndX=50 EndY=60 EndZ=0
    g9: LineSegment StartX=50 StartY=60 StartZ=0 EndX=110 EndY=60 EndZ=0
    g10: LineSegment StartX=110 StartY=60 StartZ=0 EndX=110 EndY=100 EndZ=0
    g11: LineSegment StartX=110 StartY=100 StartZ=0 EndX=-110 EndY=100 EndZ=0
    g12: Circle CenterX=0 CenterY=55 CenterZ=0 NormalX=0 NormalY=0 NormalZ=1 AngleXU=0 Radius=1.25
    g13: Circle CenterX=-40 CenterY=55 CenterZ=0 NormalX=0 NormalY=0 NormalZ=1 AngleXU=0 Radius=1.25
    g14: Circle CenterX=40 CenterY=55 CenterZ=0 NormalX=0 NormalY=0 NormalZ=1 AngleXU=0 Radius=1.25
    g15: Circle CenterX=12.73 CenterY=50 CenterZ=0 NormalX=0 NormalY=0 NormalZ=1 AngleXU=0 Radius=1.25
    g16: Circle CenterX=-12.73 CenterY=50 CenterZ=0 NormalX=0 NormalY=0 NormalZ=1 AngleXU=0 Radius=1.25
    g17: Circle CenterX=-65 CenterY=55 CenterZ=0 NormalX=0 NormalY=0 NormalZ=1 AngleXU=0 Radius=1.25
    g18: Circle CenterX=65 CenterY=55 CenterZ=0 NormalX=0 NormalY=0 NormalZ=1 AngleXU=0 Radius=1.25
    g19: Circle CenterX=-15.9 CenterY=40 CenterZ=0 NormalX=0 NormalY=0 NormalZ=1 AngleXU=0 Radius=1.25
    g20: Circle CenterX=15.9 CenterY=40 CenterZ=0 NormalX=0 NormalY=0 NormalZ=1 AngleXU=0 Radius=1.25
    g21: LineSegment StartX=-117.5 StartY=55 StartZ=0 EndX=117.5 EndY=55 EndZ=0
    g22: LineSegment StartX=-117.5 StartY=45.9 StartZ=0 EndX=117.5 EndY=45.9 EndZ=0
    g23: LineSegment StartX=-15.9 StartY=0 StartZ=0 EndX=-15.9 EndY=100 EndZ=0
    g24: LineSegment StartX=15.9 StartY=0 StartZ=0 EndX=15.9 EndY=100 EndZ=0
    g25: LineSegment StartX=-65 StartY=0 StartZ=0 EndX=-65 EndY=100 EndZ=0
    g26: LineSegment StartX=65 StartY=0 StartZ=0 EndX=65 EndY=100 EndZ=0
    g27: LineSegment StartX=-12.73 StartY=0 StartZ=0 EndX=-12.73 EndY=100 EndZ=0
    g28: LineSegment StartX=12.73 StartY=0 StartZ=0 EndX=12.73 EndY=100 EndZ=0
    g29: LineSegment StartX=-117.5 StartY=30 StartZ=0 EndX=117.5 EndY=30 EndZ=0
    g30: Circle CenterX=-15.9 CenterY=30 CenterZ=0 NormalX=0 NormalY=0 NormalZ=1 AngleXU=0 Radius=1.25
    g31: Circle CenterX=15.9 CenterY=30 CenterZ=0 NormalX=0 NormalY=0 NormalZ=1 AngleXU=0 Radius=1.25
    g32: Circle CenterX=-15.9 CenterY=45.9 CenterZ=0 NormalX=0 NormalY=0 NormalZ=1 AngleXU=0 Radius=1.25
    g33: Circle CenterX=15.9 CenterY=45.9 CenterZ=0 NormalX=0 NormalY=0 NormalZ=1 AngleXU=0 Radius=1.25
    g34: LineSegment StartX=-117.5 StartY=40 StartZ=0 EndX=117.5 EndY=40 EndZ=0
    g35: Circle CenterX=-70 CenterY=40 CenterZ=0 NormalX=0 NormalY=0 NormalZ=1 AngleXU=0 Radius=1.25
    g36: Circle CenterX=70 CenterY=40 CenterZ=0 NormalX=0 NormalY=0 NormalZ=1 AngleXU=0 Radius=1.25
    g37: LineSegment StartX=-70 StartY=100 StartZ=0 EndX=-70 EndY=0 EndZ=0
    g38: LineSegment StartX=70 StartY=100 StartZ=0 EndX=70 EndY=0 EndZ=0
  constraints (104):
    c: Vertical(g0)
    c: Coincident(g0,g1)
    c: Coincident(g2,g3)
    c: Coincident(g3,g4)
    c: Coincident(g4,g5)
    c: Coincident(g5,g6)
    c: Coincident(g6,g7)
    c: Coincident(g7,g8)
    c: Coincident(g9,g10)
    c: Coincident(g10,g11)
    c: Coincident(g11,g0)
    c: Horizontal(g1)
    c: Horizontal(g3)
    c: Symmetric(g4,g5,g-2)
    c: Symmetric(g3,g6,g-2)
    c: Symmetric(g2,g7,g-2)
    c: Symmetric(g2,g8,g-2)
    c: Symmetric(g0,g9,g-2)
    c: Symmetric(g0,g10,g-2)
    c: DistanceX(g5,g5) = 60
    c: Horizontal(g4,g2)
    c: Angle(g4) = 1.0472
    c: Angle(g2) = -1.0472
    c: DistanceX(g2,g4) = 20
    c: DistanceY(g-1,g4) = 60
    c: DistanceY(g-1,g0) = 100
    c: DistanceX(g11,g11) = 220
    c: DistanceY(g3,g4) = 10
    c: PointOnObject(g12,g-2)
    c: Symmetric(g13,g14,g-2)
    c: DistanceX(g13,g14) = 80
    c: Equal(g12,g13)
    c: Equal(g12,g14)
    c: Diameter(g12) = 2.5
    c: Symmetric(g16,g15,g-2)
    c: DistanceY(g16) = 50
    c: Equal(g15,g16)
    c: Diameter(g15) = 2.5
    c: Symmetric(g17,g18,g-2)
    c: Equal(g17,g18)
    c: Diameter(g17) = 2.5
    c: Symmetric(g19,g20,g-2)
    c: Coincident(g1,g2)
    c: Coincident(g9,g8)
    c: Symmetric(g21,g21,g-2)
    c: Symmetric(g22,g22,g-2)
    c: PointOnObject(g23,g-1)
    c: Vertical(g23)
    c: PointOnObject(g25,g-1)
    c: Vertical(g25)
    c: Symmetric(g23,g24,g-2)
    c: Symmetric(g23,g24,g-2)
    c: DistanceY(g23,g23) = 100
    c: Symmetric(g25,g26,g-2)
    c: Symmetric(g25,g26,g-2)
    c: Equal(g23,g25)
    c: DistanceX(g23,g24) = 31.8
    c: DistanceX(g25,g26) = 130
    c: DistanceY(g21) = 55
    c: DistanceY(g22) = 45.9
    c: PointOnObject(g13,g21)
    c: PointOnObject(g12,g21)
    c: PointOnObject(g17,g21)
    c: PointOnObject(g17,g25)
    c: PointOnObject(g27,g-1)
    c: Vertical(g27)
    c: Symmetric(g27,g28,g-2)
    c: Symmetric(g27,g28,g-2)
    c: DistanceX(g27,g28) = 25.46
    c: Equal(g27,g23)
    c: PointOnObject(g16,g27)
    c: DistanceX(g22,g22) = 235
    c: Equal(g22,g21)
    c: Symmetric(g29,g29,g-2)
    c: Equal(g22,g29)
    c: DistanceY(g29) = 30
    c: Equal(g17,g19)
    c: Equal(g17,g20)
    c: Equal(g32,g12)
    c: Equal(g12,g33)
    c: Equal(g12,g30)
    c: Equal(g12,g31)
    c: Symmetric(g32,g33,g-2)
    c: Symmetric(g30,g31,g-2)
    c: PointOnObject(g30,g23)
    c: PointOnObject(g32,g23)
    c: PointOnObject(g30,g29)
    c: PointOnObject(g32,g22)
    c: PointOnObject(g19,g23)
    c: Symmetric(g34,g34,g-2)
    c: Equal(g34,g22)
    c: DistanceY(g34) = 40
    c: PointOnObject(g19,g34)
    c: PointOnObject(g35,g34)
    c: Symmetric(g35,g36,g-2)
    c: Equal(g35,g16)
    c: Equal(g36,g12)
    c: PointOnObject(g37,g11)
    c: PointOnObject(g37,g-1)
    c: Vertical(g37)
    c: Symmetric(g37,g38,g-2)
    c: Symmetric(g37,g38,g-2)
    c: DistanceX(g37,g38) = 140
    c: PointOnObject(g35,g37)
FEATURE [Sketcher::SketchObject] Sketch032
  AttachmentOffset = pos=(0,0,45) rot=(0,0,1;0rad)
  FullyConstrained = true
  MapMode = 5
  Placement = pos=(0,0,45) rot=(0,0,1;0rad)
  Support = -> [XY_Plane010]
  expr: Constraints[25] = <<Variables>>.GantorySpacing / 2 + <<Variables>>.CavitySpacingY - 4
  expr: Constraints[26] = <<Variables>>.GantorySpacing
  expr: Constraints[8] = <<Variables>>.GantorySpacing + <<Variables>>.CavitySpacingX * 2 - 10
  sketch-geometry (18):
    g0: Circle CenterX=-48 CenterY=106 CenterZ=0 NormalX=0 NormalY=0 NormalZ=1 AngleXU=0 Radius=2.5
    g1: Circle CenterX=-32 CenterY=106 CenterZ=0 NormalX=0 NormalY=0 NormalZ=1 AngleXU=0 Radius=2.5
    g2: Circle CenterX=48 CenterY=106 CenterZ=0 NormalX=0 NormalY=0 NormalZ=1 AngleXU=0 Radius=2.5
    g3: Circle CenterX=32 CenterY=106 CenterZ=0 NormalX=0 NormalY=0 NormalZ=1 AngleXU=0 Radius=2.5
    g4: Circle CenterX=-105 CenterY=9 CenterZ=0 NormalX=0 NormalY=0 NormalZ=1 AngleXU=0 Radius=2.5
    g5: Circle CenterX=-105 CenterY=-39 CenterZ=0 NormalX=0 NormalY=0 NormalZ=1 AngleXU=0 Radius=2.5
    g6: Circle CenterX=105 CenterY=9 CenterZ=0 NormalX=0 NormalY=0 NormalZ=1 AngleXU=0 Radius=2.5
    g7: Circle CenterX=105 CenterY=-39 CenterZ=0 NormalX=0 NormalY=0 NormalZ=1 AngleXU=0 Radius=2.5
    g8: Circle CenterX=105 CenterY=-72 CenterZ=0 NormalX=0 NormalY=0 NormalZ=1 AngleXU=0 Radius=2.5
    g9: Circle CenterX=105 CenterY=72 CenterZ=0 NormalX=0 NormalY=0 NormalZ=1 AngleXU=0 Radius=2.5
    g10: Circle CenterX=-105 CenterY=72 CenterZ=0 NormalX=0 NormalY=0 NormalZ=1 AngleXU=0 Radius=2.5
    g11: Circle CenterX=-105 CenterY=-72 CenterZ=0 NormalX=0 NormalY=0 NormalZ=1 AngleXU=0 Radius=2.5
    g12: LineSegment StartX=-100 StartY=106 StartZ=0 EndX=100 EndY=106 EndZ=0
    g13: GeomPoint X=-40 Y=106 Z=0
    g14: GeomPoint X=40 Y=106 Z=0
    g15: LineSegment StartX=-100 StartY=-15 StartZ=0 EndX=100 EndY=-15 EndZ=0
    g16: Circle CenterX=-105 CenterY=39 CenterZ=0 NormalX=0 NormalY=0 NormalZ=1 AngleXU=0 Radius=2.5
    g17: Circle CenterX=105 CenterY=39 CenterZ=0 NormalX=0 NormalY=0 NormalZ=1 AngleXU=0 Radius=2.5
  constraints (30):
    c: Symmetric(g1,g3,g-2)
    c: Symmetric(g0,g2,g-2)
    c: Symmetric(g10,g9,g-2)
    c: Symmetric(g4,g6,g-2)
    c: Symmetric(g5,g7,g-2)
    c: Symmetric(g11,g8,g-2)
    c: Symmetric(g10,g11,g-1)
    c: Vertical(g10,g4)
    c: DistanceX(g4,g6) = 210
    c: DistanceY(g5,g4) = 48
    c: DistanceY(g11,g10) = 144
    c: DistanceX(g0,g1) = 16
    c: Equal(g0, g1-g11) x11
    c: Diameter(g0) = 5
    c: Symmetric(g12,g12,g-2)
    c: DistanceY(g12) = 106
    c: DistanceX(g12,g12) = 200
    c: PointOnObject(g13,g12)
    c: Symmetric(g13,g14,g-2)
    c: DistanceX(g13,g14) = 80
    c: Symmetric(g0,g1,g13)
    c: PointOnObject(g0,g12)
    c: Symmetric(g15,g15,g-2)
    c: Equal(g15,g12)
    c: Symmetric(g4,g5,g15)
    c: DistanceY(g15) = -15
    c: Equal(g16,g0)
    c: Equal(g0,g17)
    c: Symmetric(g16,g17,g-2)
    c: Symmetric(g5,g16,g-1)
FEATURE [Sketcher::SketchObject] Sketch033
  AttachmentOffset = pos=(0,0,60) rot=(0,0,1;0rad)
  FullyConstrained = true
  MapMode = 5
  Placement = pos=(0,0,60) rot=(0,0,1;0rad)
  Support = -> [XY_Plane010]
  expr: Constraints[32] = <<Variables>>.GantorySpacing + (<<Variables>>.CavitySpacingY + <<Variables>>.WallThickness) * 2
  expr: Constraints[33] = <<Variables>>.GantorySpacing + (<<Variables>>.CavitySpacingX + <<Variables>>.WallThickness) * 2
  expr: Constraints[34] = Variables.GantorySpacing - 10
  expr: Constraints[35] = <<Variables>>.GantorySpacing + <<Variables>>.CavitySpacingY * 2 - 20
  sketch-geometry (16):
    g0: LineSegment StartX=-117 StartY=-100 StartZ=0 EndX=-95 EndY=-100 EndZ=0
    g1: LineSegment StartX=-95 StartY=-100 StartZ=0 EndX=-95 EndY=-117 EndZ=0
    g2: LineSegment StartX=-95 StartY=-117 StartZ=0 EndX=-117 EndY=-117 EndZ=0
    g3: LineSegment StartX=-117 StartY=-117 StartZ=0 EndX=-117 EndY=-100 EndZ=0
    g4: LineSegment StartX=95 StartY=-100 StartZ=0 EndX=117 EndY=-100 EndZ=0
    g5: LineSegment StartX=117 StartY=-100 StartZ=0 EndX=117 EndY=-117 EndZ=0
    g6: LineSegment StartX=117 StartY=-117 StartZ=0 EndX=95 EndY=-117 EndZ=0
    g7: LineSegment StartX=95 StartY=-117 StartZ=0 EndX=95 EndY=-100 EndZ=0
    g8: LineSegment StartX=95 StartY=117 StartZ=0 EndX=117 EndY=117 EndZ=0
    g9: LineSegment StartX=117 StartY=117 StartZ=0 EndX=117 EndY=100 EndZ=0
    g10: LineSegment StartX=117 StartY=100 StartZ=0 EndX=95 EndY=100 EndZ=0
    g11: LineSegment StartX=95 StartY=100 StartZ=0 EndX=95 EndY=117 EndZ=0
    g12: LineSegment StartX=-117 StartY=100 StartZ=0 EndX=-95 EndY=100 EndZ=0
    g13: LineSegment StartX=-95 StartY=100 StartZ=0 EndX=-95 EndY=117 EndZ=0
    g14: LineSegment StartX=-95 StartY=117 StartZ=0 EndX=-117 EndY=117 EndZ=0
    g15: LineSegment StartX=-117 StartY=117 StartZ=0 EndX=-117 EndY=100 EndZ=0
  constraints (36):
    c: Coincident(g0,g1)
    c: Coincident(g1,g2)
    c: Coincident(g2,g3)
    c: Coincident(g3,g0)
    c: Horizontal(g0)
    c: Horizontal(g2)
    c: Vertical(g1)
    c: Vertical(g3)
    c: Coincident(g4,g5)
    c: Coincident(g5,g6)
    c: Coincident(g6,g7)
    c: Coincident(g7,g4)
    c: Coincident(g8,g9)
    c: Coincident(g9,g10)
    c: Coincident(g10,g11)
    c: Coincident(g11,g8)
    c: Coincident(g12,g13)
    c: Coincident(g13,g14)
    c: Coincident(g14,g15)
    c: Coincident(g15,g12)
    c: Symmetric(g0,g12,g-1)
    c: Symmetric(g12,g0,g-1)
    c: Symmetric(g2,g14,g-1)
    c: Symmetric(g1,g13,g-1)
    c: Symmetric(g0,g4,g-2)
    c: Symmetric(g1,g6,g-2)
    c: Symmetric(g0,g4,g-2)
    c: Symmetric(g2,g5,g-2)
    c: Symmetric(g0,g10,g-1)
    c: Symmetric(g0,g9,g-1)
    c: Symmetric(g1,g8,g-1)
    c: Symmetric(g2,g8,g-1)
    c: DistanceY(g2,g14) = 234
    c: DistanceX(g2,g5) = 234
    c: DistanceX(g1,g6) = 190
    c: DistanceY(g0,g12) = 200
FEATURE [Sketcher::SketchObject] Sketch035
  FullyConstrained = true
  MapMode = 5
  Support = -> [XY_Plane015]
  expr: Constraints[10] = <<Variables>>.GantorySpacing + <<Variables>>.CavitySpacingY * 2
  expr: Constraints[14] = <<Variables>>.PullyDiameterDrive + <<Variables>>.PullyDiameterIdler
  sketch-geometry (28):
    g0: LineSegment StartX=-25 StartY=110 StartZ=0 EndX=-10 EndY=95 EndZ=0
    g1: LineSegment StartX=-10 StartY=95 StartZ=0 EndX=-10 EndY=-95 EndZ=0
    g2: LineSegment StartX=0 StartY=-110 StartZ=0 EndX=0 EndY=110 EndZ=0
    g3: LineSegment StartX=0 StartY=110 StartZ=0 EndX=-25 EndY=110 EndZ=0
    g4: LineSegment StartX=-25 StartY=-110 StartZ=0 EndX=-10 EndY=-95 EndZ=0
    g5: LineSegment StartX=0 StartY=-110 StartZ=0 EndX=-25 EndY=-110 EndZ=0
    g6: Circle CenterX=-5 CenterY=-2.27 CenterZ=0 NormalX=0 NormalY=0 NormalZ=1 AngleXU=0 Radius=1.25
    g7: Circle CenterX=-5 CenterY=-27.73 CenterZ=0 NormalX=0 NormalY=0 NormalZ=1 AngleXU=0 Radius=1.25
    g8: LineSegment StartX=-100 StartY=110 StartZ=0 EndX=-100 EndY=-110 EndZ=0
    g9: LineSegment StartX=-190 StartY=75 StartZ=0 EndX=-155 EndY=110 EndZ=0
    g10: LineSegment StartX=-155 StartY=110 StartZ=0 EndX=-200 EndY=110 EndZ=0
    g11: LineSegment StartX=-200 StartY=110 StartZ=0 EndX=-200 EndY=8.63871 EndZ=0
    g12: LineSegment StartX=-200 StartY=-110 StartZ=0 EndX=-155 EndY=-110 EndZ=0
    g13: LineSegment StartX=-155 StartY=-110 StartZ=0 EndX=-190 EndY=-75 EndZ=0
    g14: GeomPoint X=-195 Y=-27.73 Z=0
    g15: ArcOfCircle CenterX=-195 CenterY=-2.27 CenterZ=0 NormalX=0 NormalY=0 NormalZ=1 AngleXU=0 Radius=12 StartAngle=5.27493 EndAngle=7.29145
    g16: ArcOfCircle CenterX=-187 CenterY=10.4186 CenterZ=0 NormalX=0 NormalY=0 NormalZ=1 AngleXU=0 Radius=3 StartAngle=3.14159 EndAngle=4.14985
    g17: ArcOfCircle CenterX=-187 CenterY=-14.9586 CenterZ=0 NormalX=0 NormalY=0 NormalZ=1 AngleXU=0 Radius=3 StartAngle=2.13333 EndAngle=3.14159
    g18: LineSegment StartX=-190 StartY=-75 StartZ=0 EndX=-190 EndY=-14.9586 EndZ=0
    g19: LineSegment StartX=-190 StartY=10.4186 StartZ=0 EndX=-190 EndY=75 EndZ=0
    g20: LineSegment StartX=-200 StartY=-13.1787 StartZ=0 EndX=-200 EndY=-110 EndZ=0
    g21: ArcOfCircle CenterX=-195 CenterY=-2.27 CenterZ=0 NormalX=0 NormalY=0 NormalZ=1 AngleXU=0 Radius=12 StartAngle=2.00057 EndAngle=4.28261
    g22: GeomPoint X=-195 Y=-2.27 Z=0
    g23: LineSegment StartX=-188.5 StartY=-20 StartZ=0 EndX=-11.5 EndY=-20 EndZ=0
    g24: LineSegment StartX=-11.5 StartY=-20 StartZ=0 EndX=-11.5 EndY=-10 EndZ=0
    g25: LineSegment StartX=-11.5 StartY=-10 StartZ=0 EndX=-188.5 EndY=-10 EndZ=0
    g26: LineSegment StartX=-188.5 StartY=-10 StartZ=0 EndX=-188.5 EndY=-20 EndZ=0
    g27: LineSegment StartX=-200 StartY=-15 StartZ=0 EndX=0 EndY=-15 EndZ=0
  constraints (67):
    c: Coincident(g0,g1)
    c: PointOnObject(g2,g-2)
    c: Coincident(g2,g3)
    c: Coincident(g3,g0)
    c: Horizontal(g3)
    c: Coincident(g5,g4)
    c: Angle(g0) = -0.785398
    c: Symmetric(g5,g2,g-1)
    c: Symmetric(g0,g4,g-1)
    c: Symmetric(g0,g4,g-1)
    c: DistanceY(g5,g2) = 220
    c: DistanceX(g1) = -10
    c: DistanceX(g0,g0) = 15
    c: DistanceX(g6) = -5
    c: DistanceY(g7,g6) = 25.46
    c: Equal(g6,g7)
    c: Diameter(g6) = 2.5
    c: Coincident(g2,g5)
    c: Coincident(g1,g4)
    c: Symmetric(g8,g8,g-1)
    c: DistanceX(g8) = -100
    c: PointOnObject(g8,g3)
    c: Coincident(g9,g10)
    c: Coincident(g10,g11)
    c: Coincident(g20,g12)
    c: Coincident(g12,g13)
    c: Coincident(g13,g18)
    c: Coincident(g19,g9)
    c: Symmetric(g10,g2,g8)
    c: Symmetric(g20,g2,g8)
    c: Symmetric(g14,g7,g8)
    c: Tangent(g15,g16) = 1.5708
    c: Tangent(g16,g19) = 1.5708
    c: Diameter(g16) = 6
    c: Diameter(g15) = 24
    c: Vertical(g19)
    c: Vertical(g18)
    c: Coincident(g11,g21)
    c: Coincident(g20,g21)
    c: Diameter(g21) = 24
    c: Vertical(g20)
    c: Vertical(g11)
    c: Coincident(g22,g15)
    c: Symmetric(g15,g6,g8)
    c: Coincident(g22,g21)
    c: Coincident(g23,g24)
    c: Coincident(g24,g25)
    c: Coincident(g25,g26)
    c: Coincident(g26,g23)
    c: Symmetric(g25,g24,g8)
    c: DistanceY(g26,g26) = 10
    c: DistanceX(g25,g25) = 177
    c: Tangent(g17,g18) = 1.5708
    c: Equal(g17,g16)
    c: DistanceX(g10,g9) = 10
    c: Parallel(g13,g0)
    c: Symmetric(g13,g9,g-1)
    c: Symmetric(g9,g12,g-1)
    c: Horizontal(g10)
    c: DistanceX(g9,g9) = 35
    c: Tangent(g15,g17) = 1.5708
    c: Symmetric(g27,g27,g8)
    c: PointOnObject(g27,g-2)
    c: DistanceY(g27) = -15
    c: Symmetric(g6,g7,g27)
    c: Symmetric(g25,g23,g27)
    c: Symmetric(g24,g23,g27)
FEATURE [Sketcher::SketchObject] Sketch036
  FullyConstrained = true
  MapMode = 5
  Support = -> [XY_Plane010]
  expr: Constraints[13] = <<Variables>>.GantorySpacing + (<<Variables>>.CavitySpacingY + <<Variables>>.WallThickness) * 2
  expr: Constraints[14] = <<Variables>>.GantorySpacing + (<<Variables>>.CavitySpacingX + <<Variables>>.WallThickness) * 2
  sketch-geometry (8):
    g0: LineSegment StartX=-112 StartY=117 StartZ=0 EndX=112 EndY=117 EndZ=0
    g1: LineSegment StartX=117 StartY=112 StartZ=0 EndX=117 EndY=-112 EndZ=0
    g2: LineSegment StartX=112 StartY=-117 StartZ=0 EndX=-112 EndY=-117 EndZ=0
    g3: LineSegment StartX=-117 StartY=-112 StartZ=0 EndX=-117 EndY=112 EndZ=0
    g4: LineSegment StartX=-117 StartY=112 StartZ=0 EndX=-112 EndY=117 EndZ=0
    g5: LineSegment StartX=112 StartY=117 StartZ=0 EndX=117 EndY=112 EndZ=0
    g6: LineSegment StartX=-117 StartY=-112 StartZ=0 EndX=-112 EndY=-117 EndZ=0
    g7: LineSegment StartX=117 StartY=-112 StartZ=0 EndX=112 EndY=-117 EndZ=0
  constraints (18):
    c: Coincident(g4,g0)
    c: Coincident(g4,g3)
    c: Coincident(g5,g1)
    c: Coincident(g2,g7)
    c: Coincident(g7,g1)
    c: Coincident(g6,g3)
    c: Coincident(g6,g2)
    c: Symmetric(g3,g3,g-1)
    c: Symmetric(g2,g0,g-1)
    c: Symmetric(g2,g2,g-2)
    c: Symmetric(g3,g1,g-2)
    c: Symmetric(g2,g5,g-1)
    c: Symmetric(g3,g1,g-1)
    c: DistanceY(g2,g0) = 234
    c: DistanceX(g3,g1) = 234
    c: Angle(g6) = -0.785398
    c: DistanceX(g3,g2) = 5
    c: Coincident(g0,g5)
FEATURE [PartDesign::Pad] Pad011  label="Pad TopPanel Base"
  Direction = (0,0,1)
  Length = 100
  Length2 = 10
  Profile = -> Sketch036
  ReferenceAxis = -> Sketch036 [N_Axis]
  Type = 0
FEATURE [Sketcher::SketchObject] Sketch037
  AttachmentOffset = pos=(0,0,60) rot=(0,0,1;0rad)
  FullyConstrained = true
  MapMode = 5
  Placement = pos=(0,0,60) rot=(0,0,1;0rad)
  Support = -> [XY_Plane010]
  expr: Constraints[3] = <<Variables>>.GantorySpacing
  expr: Constraints[4] = <<Variables>>.GantorySpacing
  expr: Constraints[6] = <<Variables>>.GantorySpacing - <<Variables>>.PullyDiameterDrive * 2
  expr: Constraints[7] = <<Variables>>.GantorySpacing / 2 + <<Variables>>.PullyDiameterIdler
  sketch-geometry (6):
    g0: ArcOfCircle CenterX=-100 CenterY=100 CenterZ=0 NormalX=0 NormalY=0 NormalZ=1 AngleXU=0 Radius=10 StartAngle=1.23609 EndAngle=6.61789
    g1: ArcOfCircle CenterX=-87.27 CenterY=112.73 CenterZ=0 NormalX=0 NormalY=0 NormalZ=1 AngleXU=0 Radius=10 StartAngle=4.37768 EndAngle=9.75949
    g2: ArcOfCircle CenterX=87.27 CenterY=112.73 CenterZ=0 NormalX=0 NormalY=0 NormalZ=1 AngleXU=0 Radius=10 StartAngle=5.94848 EndAngle=11.3303
    g3: ArcOfCircle CenterX=100 CenterY=100 CenterZ=0 NormalX=0 NormalY=0 NormalZ=1 AngleXU=0 Radius=10 StartAngle=2.80688 EndAngle=8.18869
    g4: Circle CenterX=-100 CenterY=-100 CenterZ=0 NormalX=0 NormalY=0 NormalZ=1 AngleXU=0 Radius=10
    g5: Circle CenterX=100 CenterY=-100 CenterZ=0 NormalX=0 NormalY=0 NormalZ=1 AngleXU=0 Radius=10
  constraints (14):
    c: Symmetric(g0,g4,g-1)
    c: Symmetric(g0,g3,g-2)
    c: Symmetric(g4,g5,g-2)
    c: DistanceY(g4,g0) = 200
    c: DistanceX(g4,g5) = 200
    c: Symmetric(g1,g2,g-2)
    c: DistanceX(g1,g2) = 174.54
    c: DistanceY(g-1,g1) = 112.73
    c: Equal(g0, g1-g5) x5
    c: Diameter(g0) = 20
    c: Coincident(g1,g0)
    c: Coincident(g1,g0)
    c: Coincident(g2,g3)
    c: Coincident(g2,g3)
FEATURE [PartDesign::SubShapeBinder] Binder002
  BindCopyOnChange = 0
  BindMode = 0
  ClaimChildren = false
  Context = -> Part004 [Body004.Hole007.Binder002.]
  Fuse = false
  MakeFace = true
  OffsetFill = false
  OffsetIntersection = false
  OffsetJoinType = 0
  OffsetOpenResult = false
  PartialLoad = false
  Placement = pos=(0,0,-60) rot=(0,0,1;0rad)
  Relative = true
  Support = -> [Pocket012[Sketch037.]]
  _Version = 2
FEATURE [Sketcher::SketchObject] Sketch038
  AttachmentOffset = pos=(0,0,2) rot=(0,0,1;0rad)
  FullyConstrained = true
  MapMode = 5
  Placement = pos=(0,0,2) rot=(0,0,1;0rad)
  Support = -> [XY_Plane010]
  expr: Constraints[5] = <<Variables>>.GantorySpacing - 10
  expr: Constraints[7] = -(<<Variables>>.GantorySpacing - 10) / 2 + 6
  expr: Constraints[8] = (<<Variables>>.GantorySpacing - 10) / 2 - 6
  sketch-geometry (4):
    g0: LineSegment StartX=-95 StartY=89 StartZ=0 EndX=95 EndY=89 EndZ=0
    g1: LineSegment StartX=95 StartY=89 StartZ=0 EndX=95 EndY=-89 EndZ=0
    g2: LineSegment StartX=95 StartY=-89 StartZ=0 EndX=-95 EndY=-89 EndZ=0
    g3: LineSegment StartX=-95 StartY=-89 StartZ=0 EndX=-95 EndY=89 EndZ=0
  constraints (10):
    c: Coincident(g0,g1)
    c: Coincident(g1,g2)
    c: Coincident(g2,g3)
    c: Coincident(g3,g0)
    c: Symmetric(g0,g0,g-2)
    c: DistanceX(g0,g0) = 190
    c: Symmetric(g2,g1,g-2)
    c: DistanceY(g2) = -89
    c: DistanceY(g0) = 89
    c: Vertical(g3)
FEATURE [Sketcher::SketchObject] Sketch039
  AttachmentOffset = pos=(0,0,10) rot=(0,0,1;0rad)
  FullyConstrained = true
  MapMode = 5
  Placement = pos=(0,0,10) rot=(0,0,1;0rad)
  Support = -> [XY_Plane015]
  expr: .AttachmentOffset.Base.z = Variables.CavitySpacingX
  expr: Constraints[1] = <<Variables>>.PullyDiameterDrive + <<Variables>>.PullyDiameterIdler
  sketch-geometry (4):
    g0: GeomPoint X=-195 Y=-27.73 Z=0
    g1: GeomPoint X=-195 Y=-2.27 Z=0
    g2: Circle CenterX=-195 CenterY=-2.27 CenterZ=0 NormalX=0 NormalY=0 NormalZ=1 AngleXU=0 Radius=8
    g3: LineSegment StartX=0 StartY=-15 StartZ=0 EndX=-250 EndY=-15 EndZ=0
  constraints (9):
    c: DistanceX(g1) = -195
    c: DistanceY(g0,g1) = 25.46
    c: Coincident(g2,g1)
    c: Diameter(g2) = 16
    c: PointOnObject(g3,g-2)
    c: Horizontal(g3)
    c: DistanceX(g3,g3) = 250
    c: DistanceY(g3) = -15
    c: Symmetric(g2,g0,g3)
FEATURE [Sketcher::SketchObject] Sketch040
  AttachmentOffset = pos=(0,0,117) rot=(1,0,0;0.785398rad)
  FullyConstrained = true
  MapMode = 5
  Placement = pos=(0,-117,-2.6e-14) rot=(1,0,0;2.35619rad)
  Support = -> [XZ_Plane010]
  expr: .AttachmentOffset.Base.z = <<Variables>>.GantorySpacing / 2 + <<Variables>>.CavitySpacingY + <<Variables>>.WallThickness
  sketch-geometry (2):
    g0: Circle CenterX=-60 CenterY=0 CenterZ=0 NormalX=0 NormalY=0 NormalZ=1 AngleXU=0 Radius=1.25
    g1: Circle CenterX=60 CenterY=3.6e-15 CenterZ=0 NormalX=0 NormalY=0 NormalZ=1 AngleXU=0 Radius=1.25
  constraints (5):
    c: Symmetric(g1,g0,g-2)
    c: Equal(g0,g1)
    c: Diameter(g0) = 2.5
    c: DistanceX(g0,g1) = 120
    c: PointOnObject(g0,g-1)
FEATURE [Sketcher::SketchObject] Sketch041
  AttachmentOffset = pos=(0,0,-117) rot=(-1,0,0;0.785398rad)
  FullyConstrained = true
  MapMode = 5
  Placement = pos=(0,117,2.6e-14) rot=(1,0,0;0.785398rad)
  Support = -> [XZ_Plane010]
  expr: .AttachmentOffset.Base.z = -(<<Variables>>.GantorySpacing / 2 + <<Variables>>.CavitySpacingY + <<Variables>>.WallThickness)
  expr: Constraints[20] = <<Variables>>.GantorySpacing
  sketch-geometry (18):
    g0: Circle CenterX=-38.1 CenterY=4.75 CenterZ=0 NormalX=0 NormalY=0 NormalZ=1 AngleXU=0 Radius=1.25
    g1: Circle CenterX=-38.1 CenterY=-4.75 CenterZ=0 NormalX=0 NormalY=0 NormalZ=1 AngleXU=0 Radius=1.25
    g2: Circle CenterX=-12.7 CenterY=4.75 CenterZ=0 NormalX=0 NormalY=0 NormalZ=1 AngleXU=0 Radius=1.25
    g3: Circle CenterX=-12.7 CenterY=-4.75 CenterZ=0 NormalX=0 NormalY=0 NormalZ=1 AngleXU=0 Radius=1.25
    g4: Circle CenterX=12.7 CenterY=4.75 CenterZ=0 NormalX=0 NormalY=0 NormalZ=1 AngleXU=0 Radius=1.25
    g5: Circle CenterX=12.7 CenterY=-4.75 CenterZ=0 NormalX=0 NormalY=0 NormalZ=1 AngleXU=0 Radius=1.25
    g6: Circle CenterX=38.1 CenterY=4.75 CenterZ=0 NormalX=0 NormalY=0 NormalZ=1 AngleXU=0 Radius=1.25
    g7: Circle CenterX=38.1 CenterY=-4.75 CenterZ=0 NormalX=0 NormalY=0 NormalZ=1 AngleXU=0 Radius=1.25
    g8: LineSegment StartX=-100 StartY=4.75 StartZ=0 EndX=100 EndY=4.75 EndZ=0
    g9: LineSegment StartX=-100 StartY=-4.75 StartZ=0 EndX=100 EndY=-4.75 EndZ=0
    g10: Circle CenterX=-63.5 CenterY=4.75 CenterZ=0 NormalX=0 NormalY=0 NormalZ=1 AngleXU=0 Radius=1.25
    g11: Circle CenterX=-63.5 CenterY=-4.75 CenterZ=0 NormalX=0 NormalY=0 NormalZ=1 AngleXU=0 Radius=1.25
    g12: Circle CenterX=63.5 CenterY=4.75 CenterZ=0 NormalX=0 NormalY=0 NormalZ=1 AngleXU=0 Radius=1.25
    g13: Circle CenterX=63.5 CenterY=-4.75 CenterZ=0 NormalX=0 NormalY=0 NormalZ=1 AngleXU=0 Radius=1.25
    g14: Circle CenterX=-88.9 CenterY=4.75 CenterZ=0 NormalX=0 NormalY=0 NormalZ=1 AngleXU=0 Radius=1.25
    g15: Circle CenterX=-88.9 CenterY=-4.75 CenterZ=0 NormalX=0 NormalY=0 NormalZ=1 AngleXU=0 Radius=1.25
    g16: Circle CenterX=88.9 CenterY=4.75 CenterZ=0 NormalX=0 NormalY=0 NormalZ=1 AngleXU=0 Radius=1.25
    g17: Circle CenterX=88.9 CenterY=-4.75 CenterZ=0 NormalX=0 NormalY=0 NormalZ=1 AngleXU=0 Radius=1.25
  constraints (32):
    c: Symmetric(g2,g4,g-2)
    c: Symmetric(g3,g5,g-2)
    c: Symmetric(g0,g6,g-2)
    c: Symmetric(g1,g7,g-2)
    c: DistanceX(g1,g3) = 25.4
    c: DistanceX(g3,g5) = 25.4
    c: Equal(g0, g1-g7) x7
    c: Diameter(g0) = 2.5
    c: Symmetric(g0,g1,g-1)
    c: Symmetric(g2,g3,g-1)
    c: Symmetric(g8,g8,g-2)
    c: Symmetric(g9,g9,g-2)
    c: Symmetric(g9,g8,g-1)
    c: DistanceY(g9,g8) = 9.5
    c: DistanceX(g8,g8) = 200
    c: PointOnObject(g0,g8)
    c: PointOnObject(g2,g8)
    c: PointOnObject(g10,g8)
    c: Equal(g0, g10-g13) x4
    c: Symmetric(g10,g11,g-1)
    c: Symmetric(g10,g12,g-2)
    c: Symmetric(g11,g13,g-2)
    c: DistanceX(g10,g0) = 25.4
    c: PointOnObject(g14,g8)
    c: Equal(g14,g0)
    c: Equal(g15,g0)
    c: Equal(g16,g0)
    c: Equal(g17,g0)
    c: Symmetric(g14,g15,g-1)
    c: Symmetric(g14,g16,g-2)
    c: Symmetric(g15,g17,g-2)
    c: DistanceX(g14,g10) = 25.4
FEATURE [Sketcher::SketchObject] Sketch042
  FullyConstrained = true
  MapMode = 5
  Support = -> [XY_Plane010]
  expr: Constraints[10] = -<<Variables>>.GantorySpacing / 2 + 4.5 + 5
  expr: Constraints[19] = <<Variables>>.GantorySpacing
  expr: Constraints[66] = <<Variables>>.GantorySpacing + <<Variables>>.CavitySpacingY * 2
  expr: Constraints[67] = Variables.GantorySpacing + <<Variables>>.CavitySpacingX * 2
  sketch-geometry (27):
    g0: LineSegment StartX=95.7 StartY=-88.7 StartZ=0 EndX=110 EndY=-88.7 EndZ=0
    g1: LineSegment StartX=110 StartY=-88.7 StartZ=0 EndX=110 EndY=-110 EndZ=0
    g2: LineSegment StartX=110 StartY=-110 StartZ=0 EndX=95.7 EndY=-110 EndZ=0
    g3: LineSegment StartX=95.7 StartY=-110 StartZ=0 EndX=95.7 EndY=-88.7 EndZ=0
    g4: Circle CenterX=98.7 CenterY=-90.5 CenterZ=0 NormalX=0 NormalY=0 NormalZ=1 AngleXU=0 Radius=0.5
    g5: Circle CenterX=105.2 CenterY=-90.5 CenterZ=0 NormalX=0 NormalY=0 NormalZ=1 AngleXU=0 Radius=0.5
    g6: LineSegment StartX=-100 StartY=-90.5 StartZ=0 EndX=100 EndY=-90.5 EndZ=0
    g7: LineSegment StartX=100 StartY=90.5 StartZ=0 EndX=100 EndY=-90.5 EndZ=0
    g8: Circle CenterX=-98.7 CenterY=-90.5 CenterZ=0 NormalX=0 NormalY=0 NormalZ=1 AngleXU=0 Radius=0.5
    g9: Circle CenterX=-105.2 CenterY=-90.5 CenterZ=0 NormalX=0 NormalY=0 NormalZ=1 AngleXU=0 Radius=0.5
    g10: LineSegment StartX=-100 StartY=90.5 StartZ=0 EndX=-100 EndY=-90.5 EndZ=0
    g11: LineSegment StartX=-110 StartY=-88.7 StartZ=0 EndX=-95.7 EndY=-88.7 EndZ=0
    g12: LineSegment StartX=-95.7 StartY=-88.7 StartZ=0 EndX=-95.7 EndY=-110 EndZ=0
    g13: LineSegment StartX=-95.7 StartY=-110 StartZ=0 EndX=-110 EndY=-110 EndZ=0
    g14: LineSegment StartX=-110 StartY=-110 StartZ=0 EndX=-110 EndY=-88.7 EndZ=0
    g15: LineSegment StartX=-110 StartY=110 StartZ=0 EndX=-95.7 EndY=110 EndZ=0
    g16: LineSegment StartX=-95.7 StartY=110 StartZ=0 EndX=-95.7 EndY=88.7 EndZ=0
    g17: LineSegment StartX=-95.7 StartY=88.7 StartZ=0 EndX=-110 EndY=88.7 EndZ=0
    g18: LineSegment StartX=-110 StartY=88.7 StartZ=0 EndX=-110 EndY=110 EndZ=0
    g19: LineSegment StartX=95.7 StartY=110 StartZ=0 EndX=110 EndY=110 EndZ=0
    g20: LineSegment StartX=110 StartY=110 StartZ=0 EndX=110 EndY=88.7 EndZ=0
    g21: LineSegment StartX=110 StartY=88.7 StartZ=0 EndX=95.7 EndY=88.7 EndZ=0
    g22: LineSegment StartX=95.7 StartY=88.7 StartZ=0 EndX=95.7 EndY=110 EndZ=0
    g23: Circle CenterX=-98.7 CenterY=90.5 CenterZ=0 NormalX=0 NormalY=0 NormalZ=1 AngleXU=0 Radius=0.5
    g24: Circle CenterX=-105.2 CenterY=90.5 CenterZ=0 NormalX=0 NormalY=0 NormalZ=1 AngleXU=0 Radius=0.5
    g25: Circle CenterX=98.7 CenterY=90.5 CenterZ=0 NormalX=0 NormalY=0 NormalZ=1 AngleXU=0 Radius=0.5
    g26: Circle CenterX=105.2 CenterY=90.5 CenterZ=0 NormalX=0 NormalY=0 NormalZ=1 AngleXU=0 Radius=0.5
  constraints (68):
    c: Coincident(g0,g1)
    c: Coincident(g1,g2)
    c: Coincident(g2,g3)
    c: Coincident(g3,g0)
    c: Horizontal(g2)
    c: Vertical(g1)
    c: Vertical(g3)
    c: Equal(g4,g5)
    c: Diameter(g4) = 1
    c: DistanceX(g4,g5) = 6.5
    c: DistanceY(g6) = -90.5
    c: PointOnObject(g4,g6)
    c: PointOnObject(g5,g6)
    c: DistanceX(g4,g7) = 1.3
    c: Horizontal(g0)
    c: DistanceX(g0,g4) = 3
    c: DistanceY(g4,g0) = 1.8
    c: Symmetric(g6,g6,g-2)
    c: Symmetric(g10,g7,g-2)
    c: DistanceX(g10,g7) = 200
    c: Equal(g9,g4)
    c: Equal(g4,g8)
    c: Coincident(g11,g12)
    c: Coincident(g12,g13)
    c: Coincident(g13,g14)
    c: Coincident(g14,g11)
    c: Horizontal(g11)
    c: Horizontal(g13)
    c: Vertical(g12)
    c: Vertical(g14)
    c: Symmetric(g13,g1,g-2)
    c: Symmetric(g11,g0,g-2)
    c: Symmetric(g8,g4,g-2)
    c: Symmetric(g5,g9,g-2)
    c: Symmetric(g10,g10,g-1)
    c: Symmetric(g7,g7,g-1)
    c: PointOnObject(g6,g7)
    c: PointOnObject(g7,g6)
    c: Coincident(g15,g16)
    c: Coincident(g16,g17)
    c: Coincident(g17,g18)
    c: Coincident(g18,g15)
    c: Horizontal(g15)
    c: Horizontal(g17)
    c: Vertical(g16)
    c: Vertical(g18)
    c: Coincident(g19,g20)
    c: Coincident(g20,g21)
    c: Coincident(g21,g22)
    c: Coincident(g22,g19)
    c: Horizontal(g19)
    c: Horizontal(g21)
    c: Vertical(g20)
    c: Vertical(g22)
    c: Symmetric(g15,g13,g-1)
    c: Symmetric(g16,g11,g-1)
    c: Symmetric(g19,g1,g-1)
    c: Symmetric(g21,g0,g-1)
    c: Symmetric(g25,g4,g-1)
    c: Symmetric(g26,g5,g-1)
    c: Symmetric(g23,g8,g-1)
    c: Symmetric(g24,g9,g-1)
    c: Equal(g25,g4)
    c: Equal(g4,g26)
    c: Equal(g4,g23)
    c: Equal(g4,g24)
    c: DistanceY(g1,g19) = 220
    c: DistanceX(g13,g1) = 220
FEATURE [Sketcher::SketchObject] Sketch043
  FullyConstrained = true
  MapMode = 5
  Support = -> [XY_Plane016]
  expr: Constraints[13] = <<Variables>>.WallThickness
  expr: Constraints[16] = (<<Variables>>.GantorySpacing + 20) / 2
  expr: Constraints[20] = <<Variables>>.GantorySpacing + <<Variables>>.WallThickness * 2 + 16
  expr: Constraints[21] = <<Variables>>.WallThickness
  expr: Constraints[23] = <<Variables>>.WallThickness + 10
  expr: Constraints[29] = <<Variables>>.WallThickness
  sketch-geometry (11):
    g0: LineSegment StartX=-7 StartY=110 StartZ=0 EndX=-2 EndY=115 EndZ=0
    g1: LineSegment StartX=-2 StartY=115 StartZ=0 EndX=10 EndY=115 EndZ=0
    g2: LineSegment StartX=10 StartY=115 StartZ=0 EndX=10 EndY=108 EndZ=0
    g3: LineSegment StartX=10 StartY=108 StartZ=0 EndX=110 EndY=108 EndZ=0
    g4: LineSegment StartX=110 StartY=108 StartZ=0 EndX=110 EndY=-108 EndZ=0
    g5: LineSegment StartX=110 StartY=-108 StartZ=0 EndX=15 EndY=-108 EndZ=0
    g6: LineSegment StartX=15 StartY=-108 StartZ=0 EndX=15 EndY=-113 EndZ=0
    g7: LineSegment StartX=13 StartY=-115 StartZ=0 EndX=-2 EndY=-115 EndZ=0
    g8: LineSegment StartX=-2 StartY=-115 StartZ=0 EndX=-7 EndY=-110 EndZ=0
    g9: LineSegment StartX=-7 StartY=-110 StartZ=0 EndX=-7 EndY=110 EndZ=0
    g10: LineSegment StartX=13 StartY=-115 StartZ=0 EndX=15 EndY=-113 EndZ=0
  constraints (31):
    c: Coincident(g0,g1)
    c: Horizontal(g1)
    c: Coincident(g1,g2)
    c: Coincident(g2,g3)
    c: Horizontal(g3)
    c: Coincident(g3,g4)
    c: Coincident(g4,g5)
    c: Coincident(g5,g6)
    c: Coincident(g7,g8)
    c: Coincident(g8,g9)
    c: Coincident(g9,g0)
    c: Vertical(g2)
    c: Angle(g0) = 0.785398
    c: DistanceY(g2,g2) = 7
    c: Symmetric(g0,g7,g-1)
    c: Symmetric(g0,g8,g-1)
    c: DistanceX(g-1,g3) = 110
    c: Horizontal(g5)
    c: Horizontal(g7)
    c: Vertical(g6)
    c: DistanceY(g7,g0) = 230
    c: DistanceX(g0,g-1) = 7
    c: DistanceY(g0,g0) = 5
    c: DistanceX(g0,g1) = 17
    c: Vertical(g4)
    c: DistanceX(g-1,g6) = 15
    c: Coincident(g10,g7)
    c: Coincident(g10,g6)
    c: Angle(g10) = 0.785398
    c: DistanceY(g7,g5) = 7
    c: DistanceY(g7,g6) = 2
FEATURE [PartDesign::Pad] Pad013  label="Pad MainObject"
  Direction = (0,0,1)
  Length = 190
  Length2 = 10
  Profile = -> Sketch043
  ReferenceAxis = -> Sketch043 [N_Axis]
  Type = 0
FEATURE [Sketcher::SketchObject] Sketch044
  FullyConstrained = true
  MapMode = 5
  Placement = pos=(0,0,0) rot=(1,0,0;1.5708rad)
  Support = -> [XZ_Plane016]
  expr: Constraints[18] = (<<Variables>>.GantorySpacing + 20 - 100) / 2
  expr: Constraints[19] = <<Variables>>.TopThickness
  expr: Constraints[20] = <<Variables>>.TopThickness / 2
  expr: Constraints[22] = (<<Variables>>.GantorySpacing + 20) / 2
  expr: Constraints[30] = <<Variables>>.TopThickness / 2
  sketch-geometry (12):
    g0: LineSegment StartX=10 StartY=190 StartZ=0 EndX=10 EndY=10 EndZ=0
    g1: LineSegment StartX=10 StartY=10 StartZ=0 EndX=40 EndY=10 EndZ=0
    g2: LineSegment StartX=60 StartY=10 StartZ=0 EndX=60 EndY=5 EndZ=0
    g3: LineSegment StartX=60 StartY=5 StartZ=0 EndX=50 EndY=5 EndZ=0
    g4: LineSegment StartX=50 StartY=5 StartZ=0 EndX=50 EndY=0 EndZ=0
    g5: LineSegment StartX=50 StartY=0 StartZ=0 EndX=110 EndY=0 EndZ=0
    g6: LineSegment StartX=110 StartY=0 StartZ=0 EndX=110 EndY=190 EndZ=0
    g7: LineSegment StartX=110 StartY=190 StartZ=0 EndX=10 EndY=190 EndZ=0
    g8: LineSegment StartX=60 StartY=10 StartZ=0 EndX=70 EndY=10 EndZ=0
    g9: LineSegment StartX=70 StartY=10 StartZ=0 EndX=60 EndY=16 EndZ=0
    g10: LineSegment StartX=60 StartY=16 StartZ=0 EndX=50 EndY=16 EndZ=0
    g11: LineSegment StartX=50 StartY=16 StartZ=0 EndX=40 EndY=10 EndZ=0
  constraints (36):
    c: Vertical(g0)
    c: Coincident(g0,g1)
    c: Horizontal(g1)
    c: Vertical(g2)
    c: Coincident(g2,g3)
    c: Horizontal(g3)
    c: Coincident(g3,g4)
    c: PointOnObject(g4,g-1)
    c: Coincident(g4,g5)
    c: Horizontal(g5)
    c: Coincident(g5,g6)
    c: Vertical(g6)
    c: Coincident(g6,g7)
    c: Coincident(g7,g0)
    c: Horizontal(g7)
    c: DistanceY(g6,g6) = 190
    c: Vertical(g4)
    c: DistanceX(g-1,g0) = 10
    c: DistanceX(g-1,g2) = 60
    c: DistanceY(g-1,g0) = 10
    c: DistanceY(g4,g4) = 5
    c: DistanceX(g3,g3) = 10
    c: DistanceX(g-1,g5) = 110
    c: Coincident(g2,g8)
    c: Horizontal(g8)
    c: Coincident(g8,g9)
    c: Coincident(g9,g10)
    c: Horizontal(g10)
    c: Coincident(g10,g11)
    c: Coincident(g1,g11)
    c: DistanceY(g2,g2) = 5
    c: Vertical(g9,g2)
    c: DistanceX(g10,g10) = 10
    c: DistanceY(g2,g9) = 6
    c: DistanceX(g1,g10) = 10
    c: DistanceX(g9,g8) = 10
FEATURE [Sketcher::SketchObject] Sketch045  label="SketchDummy"
  FullyConstrained = true
  MapMode = 5
  Placement = pos=(0,0,0) rot=(1,0,0;1.5708rad)
  Support = -> [XZ_Plane016]
  expr: Constraints[58] = <<Variables>>.TopThickness + 10
  expr: Constraints[79] = (<<Variables>>.GantorySpacing + 20) / 2
  expr: Constraints[86] = <<Variables>>.TopThickness
  expr: Constraints[92] = (<<Variables>>.GantorySpacing + 20 - 100) / 2
  expr: Constraints[94] = <<Variables>>.TopThickness / 2
  sketch-geometry (38):
    g0: LineSegment StartX=110 StartY=190 StartZ=0 EndX=33 EndY=190 EndZ=0
    g1: LineSegment StartX=80 StartY=175 StartZ=0 EndX=80 EndY=10 EndZ=0
    g2: LineSegment StartX=66.2365 StartY=94.6213 StartZ=0 EndX=15.1213 EndY=145.737 EndZ=0
    g3: LineSegment StartX=10 StartY=143.615 StartZ=0 EndX=10 EndY=41.3848 EndZ=0
    g4: LineSegment StartX=15.1213 StartY=39.2635 StartZ=0 EndX=66.2365 EndY=90.3787 EndZ=0
    g5: LineSegment StartX=80 StartY=10 StartZ=0 EndX=60 EndY=10 EndZ=0
    g6: LineSegment StartX=110 StartY=190 StartZ=0 EndX=110 EndY=0 EndZ=0
    g7: LineSegment StartX=33 StartY=190 StartZ=0 EndX=33 EndY=175 EndZ=0
    g8: LineSegment StartX=33 StartY=175 StartZ=0 EndX=80 EndY=175 EndZ=0
    g9: LineSegment StartX=70 StartY=162 StartZ=0 EndX=70 EndY=112.243 EndZ=0
    g10: LineSegment StartX=64.8787 StartY=110.121 StartZ=0 EndX=15.1213 EndY=159.879 EndZ=0
    g11: LineSegment StartX=17.2426 StartY=165 StartZ=0 EndX=67 EndY=165 EndZ=0
    g12: GeomPoint X=70 Y=165 Z=0
    g13: GeomPoint X=70 Y=105 Z=0
    g14: ArcOfCircle CenterX=13 CenterY=143.615 CenterZ=0 NormalX=0 NormalY=0 NormalZ=1 AngleXU=0 Radius=3 StartAngle=0.785398 EndAngle=3.14159
    g15: GeomPoint X=10 Y=150.858 Z=0
    g16: ArcOfCircle CenterX=17.2426 CenterY=162 CenterZ=0 NormalX=0 NormalY=0 NormalZ=1 AngleXU=0 Radius=3 StartAngle=1.5708 EndAngle=3.92699
    g17: GeomPoint X=10 Y=165 Z=0
    g18: ArcOfCircle CenterX=67 CenterY=162 CenterZ=0 NormalX=0 NormalY=0 NormalZ=1 AngleXU=0 Radius=3 StartAngle=-2.7e-15 EndAngle=1.5708
    g19: GeomPoint X=70 Y=165 Z=0
    g20: ArcOfCircle CenterX=67 CenterY=112.243 CenterZ=0 NormalX=0 NormalY=0 NormalZ=1 AngleXU=0 Radius=3 StartAngle=3.92699 EndAngle=6.28319
    g21: GeomPoint X=70 Y=105 Z=0
    g22: ArcOfCircle CenterX=13 CenterY=41.3848 CenterZ=0 NormalX=0 NormalY=0 NormalZ=1 AngleXU=0 Radius=3 StartAngle=3.14159 EndAngle=5.49779
    g23: GeomPoint X=10 Y=34.1421 Z=0
    g24: LineSegment StartX=15.1213 StartY=25.1213 StartZ=0 EndX=64.8787 EndY=74.8787 EndZ=0
    g25: LineSegment StartX=70 StartY=72.7574 StartZ=0 EndX=70 EndY=23 EndZ=0
    g26: LineSegment StartX=67 StartY=20 StartZ=0 EndX=17.2426 EndY=20 EndZ=0
    g27: ArcOfCircle CenterX=67 CenterY=72.7574 CenterZ=0 NormalX=0 NormalY=0 NormalZ=1 AngleXU=0 Radius=3 StartAngle=-1.8e-15 EndAngle=2.35619
    g28: GeomPoint X=70 Y=80 Z=0
    g29: ArcOfCircle CenterX=67 CenterY=23 CenterZ=0 NormalX=0 NormalY=0 NormalZ=1 AngleXU=0 Radius=3 StartAngle=4.71239 EndAngle=6.28319
    g30: GeomPoint X=70 Y=20 Z=0
    g31: ArcOfCircle CenterX=17.2426 CenterY=23 CenterZ=0 NormalX=0 NormalY=0 NormalZ=1 AngleXU=0 Radius=3 StartAngle=2.35619 EndAngle=4.71239
    g32: GeomPoint X=10 Y=20 Z=0
    g33: ArcOfCircle CenterX=64.1152 CenterY=92.5 CenterZ=0 NormalX=0 NormalY=0 NormalZ=1 AngleXU=0 Radius=3 StartAngle=5.49779 EndAngle=7.06858
    g34: LineSegment StartX=110 StartY=0 StartZ=0 EndX=50 EndY=0 EndZ=0
    g35: LineSegment StartX=60 StartY=5 StartZ=0 EndX=60 EndY=10 EndZ=0
    g36: LineSegment StartX=50 StartY=0 StartZ=0 EndX=50 EndY=5 EndZ=0
    g37: LineSegment StartX=50 StartY=5 StartZ=0 EndX=60 EndY=5 EndZ=0
  constraints (95):
    c: Horizontal(g0)
    c: Vertical(g1)
    c: Vertical(g3)
    c: Horizontal(g5)
    c: Coincident(g6,g0)
    c: Vertical(g6)
    c: DistanceX(g-1,g23) = 10
    c: DistanceX(g1,g0) = 30
    c: Coincident(g0,g7)
    c: Vertical(g7)
    c: Coincident(g7,g8)
    c: Coincident(g8,g1)
    c: Horizontal(g8)
    c: DistanceY(g-1,g1) = 175
    c: DistanceX(g-1,g0) = 33
    c: Vertical(g9)
    c: Horizontal(g11)
    c: PointOnObject(g12,g11)
    c: PointOnObject(g12,g9)
    c: PointOnObject(g13,g9)
    c: PointOnObject(g13,g10)
    c: DistanceY(g17,g7) = 10
    c: PointOnObject(g15,g2)
    c: PointOnObject(g15,g3)
    c: Tangent(g2,g14) = -1.5708
    c: Tangent(g3,g14) = -1.5708
    c: Coincident(g1,g5)
    c: PointOnObject(g17,g11)
    c: PointOnObject(g17,g10)
    c: Tangent(g11,g16) = 1.5708
    c: Tangent(g10,g16) = 1.5708
    c: PointOnObject(g19,g11)
    c: PointOnObject(g19,g9)
    c: Tangent(g11,g18) = 1.5708
    c: Tangent(g9,g18) = 1.5708
    c: PointOnObject(g21,g10)
    c: PointOnObject(g21,g9)
    c: Tangent(g10,g20) = 1.5708
    c: Tangent(g9,g20) = 1.5708
    c: Equal(g16,g18)
    c: Equal(g16,g20)
    c: Radius(g16) = 3
    c: DistanceX(g12,g1) = 10
    c: Angle(g10) = 2.35619
    c: Parallel(g2,g10)
    c: Distance(g15,g10) = 10
    c: PointOnObject(g23,g4)
    c: PointOnObject(g23,g3)
    c: Tangent(g4,g22) = -1.5708
    c: Tangent(g3,g22) = -1.5708
    c: Equal(g14,g22)
    c: Radius(g14) = 3
    c: Vertical(g25)
    c: Horizontal(g26)
    c: Angle(g24) = 0.785398
    c: Parallel(g24,g4)
    c: DistanceX(g30,g1) = 10
    c: Distance(g4,g24) = 10
    c: DistanceY(g-1,g32) = 20
    c: DistanceX(g-1,g17) = 10
    c: DistanceX(g-1,g32) = 10
    c: PointOnObject(g28,g24)
    c: PointOnObject(g28,g25)
    c: Tangent(g24,g27) = 1.5708
    c: Tangent(g25,g27) = 1.5708
    c: PointOnObject(g30,g25)
    c: PointOnObject(g30,g26)
    c: Tangent(g25,g29) = 1.5708
    c: Tangent(g26,g29) = 1.5708
    c: PointOnObject(g32,g26)
    c: PointOnObject(g32,g24)
    c: Tangent(g26,g31) = 1.5708
    c: Tangent(g24,g31) = 1.5708
    c: Equal(g27,g29)
    c: Equal(g27,g31)
    c: Radius(g27) = 3
    c: Tangent(g2,g33) = -1.5708
    c: Tangent(g4,g33) = -1.5708
    c: Radius(g33) = 3
    c: DistanceX(g-1,g0) = 110
    c: Coincident(g34,g6)
    c: Horizontal(g34)
    c: Coincident(g35,g5)
    c: Vertical(g35)
    c: PointOnObject(g6,g-1)
    c: DistanceY(g6,g6) = 190
    c: DistanceY(g-1,g5) = 10
    c: Coincident(g36,g34)
    c: Vertical(g36)
    c: Coincident(g37,g36)
    c: Coincident(g37,g35)
    c: Horizontal(g37)
    c: DistanceX(g-1,g5) = 60
    c: DistanceX(g37,g37) = 10
    c: DistanceY(g36,g36) = 5
FEATURE [Sketcher::SketchObject] Sketch046
  FullyConstrained = true
  MapMode = 5
  Placement = pos=(0,0,0) rot=(1,0,0;1.5708rad)
  Support = -> [XZ_Plane016]
  expr: Constraints[18] = <<Variables>>.TopThickness / 2
  expr: Constraints[26] = <<Variables>>.TopThickness
  expr: Constraints[28] = (<<Variables>>.GantorySpacing + 20 - 100) / 2
  expr: Constraints[9] = (<<Variables>>.GantorySpacing + 20) / 2
  sketch-geometry (15):
    g0: LineSegment StartX=10 StartY=190 StartZ=0 EndX=10 EndY=42.4853 EndZ=0
    g1: LineSegment StartX=11.7574 StartY=38.2426 StartZ=0 EndX=28.2426 EndY=21.7574 EndZ=0
    g2: LineSegment StartX=50 StartY=0 StartZ=0 EndX=110 EndY=0 EndZ=0
    g3: LineSegment StartX=110 StartY=0 StartZ=0 EndX=110 EndY=10 EndZ=0
    g4: LineSegment StartX=110 StartY=190 StartZ=0 EndX=10 EndY=190 EndZ=0
    g5: LineSegment StartX=50 StartY=0 StartZ=0 EndX=50 EndY=5 EndZ=0
    g6: LineSegment StartX=50 StartY=5 StartZ=0 EndX=60 EndY=5 EndZ=0
    g7: LineSegment StartX=60 StartY=5 StartZ=0 EndX=60 EndY=10 EndZ=0
    g8: LineSegment StartX=110 StartY=20 StartZ=0 EndX=32.4853 EndY=20 EndZ=0
    g9: LineSegment StartX=60 StartY=10 StartZ=0 EndX=110 EndY=10 EndZ=0
    g10: LineSegment StartX=110 StartY=20 StartZ=0 EndX=110 EndY=190 EndZ=0
    g11: ArcOfCircle CenterX=16 CenterY=42.4853 CenterZ=0 NormalX=0 NormalY=0 NormalZ=1 AngleXU=0 Radius=6 StartAngle=3.14159 EndAngle=3.92699
    g12: GeomPoint X=10 Y=40 Z=0
    g13: ArcOfCircle CenterX=32.4853 CenterY=26 CenterZ=0 NormalX=0 NormalY=0 NormalZ=1 AngleXU=0 Radius=6 StartAngle=3.92699 EndAngle=4.71239
    g14: GeomPoint X=30 Y=20 Z=0
  constraints (41):
    c: Vertical(g0)
    c: Horizontal(g2)
    c: Coincident(g2,g3)
    c: Vertical(g3)
    c: Coincident(g10,g4)
    c: Coincident(g4,g0)
    c: Horizontal(g4)
    c: Angle(g1) = -0.785398
    c: DistanceX(g-1,g0) = 10
    c: DistanceX(g-1,g10) = 110
    c: Coincident(g2,g5)
    c: Vertical(g5)
    c: Coincident(g5,g6)
    c: Horizontal(g6)
    c: Coincident(g6,g7)
    c: Vertical(g7)
    c: Horizontal(g8)
    c: DistanceX(g6,g6) = 10
    c: DistanceY(g5,g5) = 5
    c: PointOnObject(g2,g-1)
    c: DistanceY(g3,g10) = 190
    c: DistanceY(g-1,g12) = 40
    c: Horizontal(g9)
    c: Coincident(g7,g9)
    c: Coincident(g3,g9)
    c: Vertical(g10,g3)
    c: DistanceY(g3,g3) = 10
    c: DistanceY(g3,g10) = 10
    c: DistanceX(g-1,g7) = 60
    c: Vertical(g10)
    c: Coincident(g8,g10)
    c: PointOnObject(g12,g0)
    c: PointOnObject(g12,g1)
    c: Tangent(g0,g11) = -1.5708
    c: Tangent(g1,g11) = -1.5708
    c: Radius(g11) = 6
    c: PointOnObject(g14,g1)
    c: PointOnObject(g14,g8)
    c: Tangent(g1,g13) = -1.5708
    c: Tangent(g8,g13) = 1.5708
    c: Radius(g13) = 6
FEATURE [Sketcher::SketchObject] Sketch047
  FullyConstrained = true
  MapMode = 5
  Placement = pos=(0,0,0) rot=(0.57735,0.57735,0.57735;2.0944rad)
  Support = -> [YZ_Plane016]
  sketch-geometry (16):
    g0: ArcOfCircle CenterX=-75 CenterY=41 CenterZ=0 NormalX=0 NormalY=0 NormalZ=1 AngleXU=0 Radius=1 StartAngle=1.5708 EndAngle=4.71239
    g1: ArcOfCircle CenterX=-50 CenterY=41 CenterZ=0 NormalX=0 NormalY=0 NormalZ=1 AngleXU=0 Radius=1 StartAngle=4.71239 EndAngle=7.85398
    g2: LineSegment StartX=-75 StartY=40 StartZ=0 EndX=-50 EndY=40 EndZ=0
    g3: LineSegment StartX=-50 StartY=42 StartZ=0 EndX=-75 EndY=42 EndZ=0
    g4: ArcOfCircle CenterX=50 CenterY=41 CenterZ=0 NormalX=0 NormalY=0 NormalZ=1 AngleXU=0 Radius=1 StartAngle=1.5708 EndAngle=4.71239
    g5: ArcOfCircle CenterX=75 CenterY=41 CenterZ=0 NormalX=0 NormalY=0 NormalZ=1 AngleXU=0 Radius=1 StartAngle=4.71239 EndAngle=7.85398
    g6: LineSegment StartX=50 StartY=40 StartZ=0 EndX=75 EndY=40 EndZ=0
    g7: LineSegment StartX=75 StartY=42 StartZ=0 EndX=50 EndY=42 EndZ=0
    g8: ArcOfCircle CenterX=-75 CenterY=11 CenterZ=0 NormalX=0 NormalY=0 NormalZ=1 AngleXU=0 Radius=1 StartAngle=1.5708 EndAngle=4.71239
    g9: ArcOfCircle CenterX=-50 CenterY=11 CenterZ=0 NormalX=0 NormalY=0 NormalZ=1 AngleXU=0 Radius=1 StartAngle=4.71239 EndAngle=7.85398
    g10: LineSegment StartX=-75 StartY=10 StartZ=0 EndX=-50 EndY=10 EndZ=0
    g11: LineSegment StartX=-50 StartY=12 StartZ=0 EndX=-75 EndY=12 EndZ=0
    g12: ArcOfCircle CenterX=50 CenterY=11 CenterZ=0 NormalX=0 NormalY=0 NormalZ=1 AngleXU=0 Radius=1 StartAngle=1.5708 EndAngle=4.71239
    g13: ArcOfCircle CenterX=75 CenterY=11 CenterZ=0 NormalX=0 NormalY=0 NormalZ=1 AngleXU=0 Radius=1 StartAngle=4.71239 EndAngle=7.85398
    g14: LineSegment StartX=50 StartY=10 StartZ=0 EndX=75 EndY=10 EndZ=0
    g15: LineSegment StartX=75 StartY=12 StartZ=0 EndX=50 EndY=12 EndZ=0
  constraints (36):
    c: Tangent(g0,g2) = -1.5708
    c: Tangent(g2,g1) = -1.5708
    c: Tangent(g1,g3) = -1.5708
    c: Tangent(g3,g0) = -1.5708
    c: Equal(g0,g1)
    c: Horizontal(g2)
    c: Tangent(g4,g6) = -1.5708
    c: Tangent(g6,g5) = -1.5708
    c: Tangent(g5,g7) = -1.5708
    c: Tangent(g7,g4) = -1.5708
    c: Equal(g4,g5)
    c: Tangent(g8,g10) = -1.5708
    c: Tangent(g10,g9) = -1.5708
    c: Tangent(g9,g11) = -1.5708
    c: Tangent(g11,g8) = -1.5708
    c: Equal(g8,g9)
    c: Horizontal(g10)
    c: Tangent(g12,g14) = -1.5708
    c: Tangent(g14,g13) = -1.5708
    c: Tangent(g13,g15) = -1.5708
    c: Tangent(g15,g12) = -1.5708
    c: Equal(g12,g13)
    c: Symmetric(g9,g12,g-2)
    c: Symmetric(g1,g4,g-2)
    c: DistanceX(g2,g2) = 25
    c: Radius(g1) = 1
    c: Radius(g4) = 1
    c: Symmetric(g0,g5,g-2)
    c: DistanceY(g-1,g1) = 41
    c: Symmetric(g8,g13,g-2)
    c: Radius(g9) = 1
    c: Radius(g12) = 1
    c: DistanceX(g0,g5) = 150
    c: DistanceX(g8,g13) = 150
    c: DistanceX(g10,g10) = 25
    c: DistanceY(g-1,g8) = 11
FEATURE [Sketcher::SketchObject] Sketch048  label="Sketch SideTopPanelFitting"
  FullyConstrained = true
  MapMode = 5
  Placement = pos=(0,0,0) rot=(0.57735,0.57735,0.57735;2.0944rad)
  Support = -> [YZ_Plane030]
  expr: Constraints[29] = <<Variables>>.GantorySpacing + <<Variables>>.WallThickness * 2 + 20
  sketch-geometry (24):
    g0: LineSegment StartX=-106.226 StartY=185 StartZ=0 EndX=-85.7735 EndY=185 EndZ=0
    g1: LineSegment StartX=-74.2265 StartY=165 StartZ=0 EndX=-53.7735 EndY=165 EndZ=0
    g2: LineSegment StartX=-42.2265 StartY=185 StartZ=0 EndX=-21.7735 EndY=185 EndZ=0
    g3: LineSegment StartX=53.7735 StartY=165 StartZ=0 EndX=74.2265 EndY=165 EndZ=0
    g4: LineSegment StartX=74.2265 StartY=165 StartZ=0 EndX=85.7735 EndY=185 EndZ=0
    g5: LineSegment StartX=85.7735 StartY=185 StartZ=0 EndX=106.226 EndY=185 EndZ=0
    g6: LineSegment StartX=117 StartY=175 StartZ=0 EndX=117 EndY=235 EndZ=0
    g7: LineSegment StartX=117 StartY=235 StartZ=0 EndX=-117 EndY=235 EndZ=0
    g8: LineSegment StartX=-117 StartY=235 StartZ=0 EndX=-117 EndY=175 EndZ=0
    g9: LineSegment StartX=-10.2265 StartY=165 StartZ=0 EndX=10.2265 EndY=165 EndZ=0
    g10: LineSegment StartX=21.7735 StartY=185 StartZ=0 EndX=42.2265 EndY=185 EndZ=0
    g11: LineSegment StartX=42.2265 StartY=185 StartZ=0 EndX=53.7735 EndY=165 EndZ=0
    g12: LineSegment StartX=-85.7735 StartY=185 StartZ=0 EndX=-80 EndY=175 EndZ=0
    g13: LineSegment StartX=-80 StartY=175 StartZ=0 EndX=-74.2265 EndY=165 EndZ=0
    g14: LineSegment StartX=-53.7735 StartY=165 StartZ=0 EndX=-48 EndY=175 EndZ=0
    g15: LineSegment StartX=-48 StartY=175 StartZ=0 EndX=-42.2265 EndY=185 EndZ=0
    g16: LineSegment StartX=-21.7735 StartY=185 StartZ=0 EndX=-16 EndY=175 EndZ=0
    g17: LineSegment StartX=-16 StartY=175 StartZ=0 EndX=-10.2265 EndY=165 EndZ=0
    g18: LineSegment StartX=10.2265 StartY=165 StartZ=0 EndX=16 EndY=175 EndZ=0
    g19: LineSegment StartX=16 StartY=175 StartZ=0 EndX=21.7735 EndY=185 EndZ=0
    g20: LineSegment StartX=-112 StartY=175 StartZ=0 EndX=-106.226 EndY=185 EndZ=0
    g21: LineSegment StartX=106.226 StartY=185 StartZ=0 EndX=112 EndY=175 EndZ=0
    g22: LineSegment StartX=-117 StartY=175 StartZ=0 EndX=-112 EndY=175 EndZ=0
    g23: LineSegment StartX=117 StartY=175 StartZ=0 EndX=112 EndY=175 EndZ=0
  constraints (58):
    c: Coincident(g0,g12)
    c: Coincident(g13,g1)
    c: Coincident(g1,g14)
    c: Coincident(g15,g2)
    c: Coincident(g3,g4)
    c: Coincident(g4,g5)
    c: Coincident(g6,g7)
    c: Coincident(g7,g8)
    c: Coincident(g2,g16)
    c: Coincident(g17,g9)
    c: Coincident(g9,g18)
    c: Coincident(g19,g10)
    c: Coincident(g10,g11)
    c: Coincident(g11,g3)
    c: Horizontal(g1)
    c: Horizontal(g0)
    c: Vertical(g8)
    c: Horizontal(g1,g17)
    c: Horizontal(g2)
    c: Symmetric(g7,g6,g-2)
    c: Symmetric(g8,g6,g-2)
    c: Symmetric(g0,g5,g-2)
    c: Symmetric(g0,g4,g-2)
    c: Symmetric(g13,g3,g-2)
    c: Symmetric(g1,g3,g-2)
    c: Symmetric(g15,g10,g-2)
    c: Symmetric(g2,g19,g-2)
    c: Symmetric(g17,g9,g-2)
    c: Horizontal(g15,g0)
    c: DistanceX(g7,g7) = 234
    c: DistanceY(g-1,g0) = 185
    c: Coincident(g12,g13)
    c: Symmetric(g0,g1,g12)
    c: Coincident(g14,g15)
    c: Coincident(g16,g17)
    c: Symmetric(g2,g1,g14)
    c: Coincident(g18,g19)
    c: Symmetric(g2,g9,g16)
    c: Symmetric(g10,g9,g18)
    c: DistanceY(g1,g12) = 10
    c: DistanceX(g12,g14) = 32
    c: DistanceX(g14,g16) = 32
    c: DistanceX(g16,g18) = 32
    c: Angle(g17) = -1.0472
    c: Angle(g14) = 1.0472
    c: Angle(g13) = -1.0472
    c: DistanceY(g-1,g7) = 235
    c: Coincident(g20,g0)
    c: Coincident(g21,g5)
    c: Angle(g20) = 1.0472
    c: Coincident(g22,g8)
    c: Coincident(g22,g20)
    c: Coincident(g23,g6)
    c: Coincident(g23,g21)
    c: Horizontal(g22)
    c: Symmetric(g20,g21,g-2)
    c: Horizontal(g20,g12)
    c: DistanceX(g20,g12) = 32
FEATURE [PartDesign::Pocket] Pocket018  label="Pocket TopSideFitting"
  BaseFeature = -> Pad013
  Direction = (-1,2e-16,-3e-16)
  Length = 6
  Length2 = 5
  Profile = -> Sketch048
  ReferenceAxis = -> Sketch048 [N_Axis]
  Type = 1
FEATURE [Sketcher::SketchObject] Sketch049
  FullyConstrained = true
  MapMode = 5
  Placement = pos=(0,0,0) rot=(1,0,0;1.5708rad)
  Support = -> [XZ_Plane016]
  expr: Constraints[11] = <<Variables>>.WallThickness / 2
  sketch-geometry (4):
    g0: LineSegment StartX=-3.5 StartY=185 StartZ=0 EndX=0 EndY=185 EndZ=0
    g1: LineSegment StartX=0 StartY=185 StartZ=0 EndX=0 EndY=175 EndZ=0
    g2: LineSegment StartX=0 StartY=175 StartZ=0 EndX=-3.5 EndY=175 EndZ=0
    g3: LineSegment StartX=-3.5 StartY=175 StartZ=0 EndX=-3.5 EndY=185 EndZ=0
  constraints (12):
    c: Coincident(g0,g1)
    c: Coincident(g1,g2)
    c: Coincident(g2,g3)
    c: Coincident(g3,g0)
    c: Horizontal(g0)
    c: Horizontal(g2)
    c: Vertical(g1)
    c: Vertical(g3)
    c: DistanceY(g-1,g2) = 175
    c: PointOnObject(g1,g-2)
    c: DistanceY(g3,g3) = 10
    c: DistanceX(g0,g0) = 3.5
FEATURE [PartDesign::Pocket] Pocket019  label="Pocket TopFitting"
  BaseFeature = -> Pocket018
  Direction = (0,1,2e-16)
  Length = 177
  Length2 = 5
  Midplane = true
  Profile = -> Sketch049
  ReferenceAxis = -> Sketch049 [N_Axis]
  Type = 0
  expr: Length = <<Variables>>.GantorySpacing + <<Variables>>.WallThickness + 16 - 46
FEATURE [PartDesign::Pocket] Pocket002  label="Pocket SideBeam"
  BaseFeature = -> Pocket019
  Direction = (-1,2e-16,-3e-16)
  Length = 20
  Length2 = 5
  Profile = -> Sketch021
  ReferenceAxis = -> Sketch021 [N_Axis]
  Reversed = true
  Type = 0
FEATURE [PartDesign::Pocket] Pocket014  label="Pocket Cavity"
  BaseFeature = -> Pocket002
  Direction = (0,1,2e-16)
  Length = 196
  Length2 = 5
  Midplane = true
  Profile = -> Sketch044
  ReferenceAxis = -> Sketch044 [N_Axis]
  Type = 0
  expr: Length = <<Variables>>.GantorySpacing + 16 - 20
FEATURE [PartDesign::Pocket] Pocket016  label="Pocket FrontAperture"
  BaseFeature = -> Pocket014
  Direction = (0,1,2e-16)
  Length = 108
  Length2 = 5
  Profile = -> Sketch046
  ReferenceAxis = -> Sketch046 [N_Axis]
  Reversed = true
  Type = 0
  expr: Length = (<<Variables>>.GantorySpacing + 16) / 2
FEATURE [Sketcher::SketchObject] Sketch050
  AttachmentOffset = pos=(0,0,190) rot=(0,0,1;0rad)
  FullyConstrained = true
  MapMode = 5
  Placement = pos=(0,0,190) rot=(0,0,1;0rad)
  Support = -> [XY_Plane016]
  expr: Constraints[36] = (<<Variables>>.GantorySpacing + <<Variables>>.WallThickness + 16) / 2
  expr: Constraints[38] = (<<Variables>>.GantorySpacing + <<Variables>>.WallThickness + 16) / 2
  expr: Constraints[4] = <<Variables>>.WallThickness / 2
  expr: Constraints[9] = <<Variables>>.GantorySpacing
  sketch-geometry (15):
    g0: LineSegment StartX=15 StartY=-111.5 StartZ=0 EndX=-3.5 EndY=-111.5 EndZ=0
    g1: LineSegment StartX=-3.5 StartY=-111.5 StartZ=0 EndX=-3.5 EndY=-88.5 EndZ=0
    g2: LineSegment StartX=-3.5 StartY=111.5 StartZ=0 EndX=16 EndY=111.5 EndZ=0
    g3: LineSegment StartX=-3.5 StartY=88.5 StartZ=0 EndX=-3.5 EndY=111.5 EndZ=0
    g4: ArcOfCircle CenterX=10 CenterY=-100 CenterZ=0 NormalX=0 NormalY=0 NormalZ=1 AngleXU=0 Radius=6 StartAngle=5.8073 EndAngle=8.26327
    g5: ArcOfCircle CenterX=10 CenterY=100 CenterZ=0 NormalX=0 NormalY=0 NormalZ=1 AngleXU=0 Radius=6 StartAngle=4.30311 EndAngle=6.28319
    g6: LineSegment StartX=16 StartY=111.5 StartZ=0 EndX=16 EndY=100 EndZ=0
    g7: LineSegment StartX=15 StartY=-111.5 StartZ=0 EndX=15 EndY=-104.123 EndZ=0
    g8: ArcOfCircle CenterX=5.44531 CenterY=-89.5 CenterZ=0 NormalX=0 NormalY=0 NormalZ=1 AngleXU=0 Radius=5.44531 StartAngle=3.14159 EndAngle=5.12167
    g9: ArcOfCircle CenterX=5.44531 CenterY=89.5 CenterZ=0 NormalX=0 NormalY=0 NormalZ=1 AngleXU=0 Radius=5.44531 StartAngle=1.16151 EndAngle=3.14159
    g10: LineSegment StartX=-3.5 StartY=-88.5 StartZ=0 EndX=0 EndY=-88.5 EndZ=0
    g11: LineSegment StartX=0 StartY=-88.5 StartZ=0 EndX=0 EndY=-89.5 EndZ=0
    g12: ArcOfCircle CenterX=18 CenterY=-104.123 CenterZ=0 NormalX=0 NormalY=0 NormalZ=1 AngleXU=0 Radius=3 StartAngle=2.66571 EndAngle=3.14159
    g13: LineSegment StartX=-3.5 StartY=88.5 StartZ=0 EndX=0 EndY=88.5 EndZ=0
    g14: LineSegment StartX=0 StartY=88.5 StartZ=0 EndX=0 EndY=89.5 EndZ=0
  constraints (41):
    c: Coincident(g0,g1)
    c: Horizontal(g0)
    c: Vertical(g1)
    c: DistanceY(g1,g1) = 23
    c: DistanceX(g0,g-1) = 3.5
    c: Coincident(g3,g2)
    c: Horizontal(g2)
    c: Symmetric(g3,g1,g-1)
    c: Symmetric(g5,g4,g-1)
    c: DistanceY(g4,g5) = 200
    c: DistanceX(g-1,g4) = 10
    c: Diameter(g4) = 12
    c: Diameter(g5) = 12
    c: Vertical(g6)
    c: Coincident(g7,g0)
    c: Vertical(g7)
    c: Tangent(g9,g5) = 1.5708
    c: Tangent(g8,g4) = 1.5708
    c: Coincident(g10,g1)
    c: PointOnObject(g10,g-2)
    c: Horizontal(g10)
    c: Coincident(g11,g10)
    c: Tangent(g8,g11) = -1.5708
    c: Vertical(g11)
    c: DistanceY(g11,g11) = 1
    c: DistanceX(g-1,g0) = 15
    c: Tangent(g12,g4) = 1.5708
    c: Tangent(g12,g7) = 1.5708
    c: Diameter(g12) = 6
    c: Coincident(g3,g13)
    c: PointOnObject(g13,g-2)
    c: Horizontal(g13)
    c: Coincident(g13,g14)
    c: DistanceY(g14,g14) = 1
    c: Tangent(g14,g9) = 1.5708
    c: Vertical(g14)
    c: DistanceY(g0,g-1) = 111.5
    c: Vertical(g3)
    c: DistanceY(g-1,g2) = 111.5
    c: Coincident(g6,g2)
    c: Tangent(g5,g6) = 1.5708
FEATURE [Sketcher::SketchObject] Sketch051
  FullyConstrained = true
  MapMode = 5
  Placement = pos=(0,0,0) rot=(0.57735,0.57735,0.57735;2.0944rad)
  Support = -> [YZ_Plane016]
  expr: Constraints[30] = <<Variables>>.WallThickness / 2
  expr: Constraints[6] = <<Variables>>.WallThickness / 2 + 0
  expr: Constraints[7] = (<<Variables>>.GantorySpacing + <<Variables>>.WallThickness * 2 + 16) / 2
  expr: Constraints[8] = 235 - <<Variables>>.TopThickness - 17 - 19
  sketch-geometry (13):
    g0: LineSegment StartX=-115 StartY=174.9 StartZ=0 EndX=-111.5 EndY=174.9 EndZ=0
    g1: LineSegment StartX=-111.5 StartY=174.9 StartZ=0 EndX=-111.5 EndY=189 EndZ=0
    g2: LineSegment StartX=-115 StartY=204.9 StartZ=0 EndX=-115 EndY=174.9 EndZ=0
    g3: LineSegment StartX=-88.5 StartY=189 StartZ=0 EndX=-88.5 EndY=185 EndZ=0
    g4: LineSegment StartX=-88.5 StartY=185 StartZ=0 EndX=88.5 EndY=185 EndZ=0
    g5: LineSegment StartX=88.5 StartY=185 StartZ=0 EndX=88.5 EndY=189 EndZ=0
    g6: LineSegment StartX=88.5 StartY=189 StartZ=0 EndX=111.5 EndY=189 EndZ=0
    g7: LineSegment StartX=111.5 StartY=189 StartZ=0 EndX=111.5 EndY=174.9 EndZ=0
    g8: LineSegment StartX=111.5 StartY=174.9 StartZ=0 EndX=115 EndY=174.9 EndZ=0
    g9: LineSegment StartX=115 StartY=174.9 StartZ=0 EndX=115 EndY=204.9 EndZ=0
    g10: LineSegment StartX=115 StartY=204.9 StartZ=0 EndX=-115 EndY=204.9 EndZ=0
    g11: LineSegment StartX=-111.5 StartY=189 StartZ=0 EndX=-108 EndY=189 EndZ=0
    g12: LineSegment StartX=-108 StartY=189 StartZ=0 EndX=-88.5 EndY=189 EndZ=0
  constraints (34):
    c: Coincident(g0,g1)
    c: Vertical(g1)
    c: Coincident(g1,g11)
    c: Coincident(g2,g0)
    c: Vertical(g2)
    c: Horizontal(g0)
    c: DistanceX(g0,g0) = 3.5
    c: DistanceX(g2,g-1) = 115
    c: DistanceY(g-1,g12) = 189
    c: DistanceY(g2,g2) = 30
    c: DistanceY(g-1,g0) = 174.9
    c: Coincident(g12,g3)
    c: Vertical(g3)
    c: Coincident(g3,g4)
    c: Coincident(g4,g5)
    c: Coincident(g5,g6)
    c: Coincident(g6,g7)
    c: Coincident(g7,g8)
    c: Coincident(g8,g9)
    c: Coincident(g9,g10)
    c: Coincident(g10,g2)
    c: Symmetric(g2,g9,g-2)
    c: Symmetric(g0,g8,g-2)
    c: Symmetric(g12,g5,g-2)
    c: Symmetric(g3,g4,g-2)
    c: DistanceY(g-1,g3) = 185
    c: DistanceX(g1,g12) = 23
    c: Coincident(g11,g12)
    c: Horizontal(g11)
    c: Horizontal(g12)
    c: DistanceX(g11,g11) = 3.5
    c: Vertical(g7)
    c: Horizontal(g8)
    c: Symmetric(g6,g1,g-2)
FEATURE [PartDesign::Pad] Pad014  label="Pad IdlerNutHolder"
  BaseFeature = -> Pocket016
  Direction = (0,0,1)
  Length = 30
  Length2 = 10
  Profile = -> Sketch050
  ReferenceAxis = -> Sketch050 [N_Axis]
  Reversed = true
  Type = 0
FEATURE [Sketcher::SketchObject] Sketch052
  AttachmentOffset = pos=(0,0,10) rot=(0,0,1;0rad)
  FullyConstrained = true
  MapMode = 5
  Placement = pos=(10,-2.2e-15,2.2e-15) rot=(0.57735,0.57735,0.57735;2.0944rad)
  Support = -> [YZ_Plane016]
  expr: Constraints[10] = <<Variables>>.GantorySpacing + 16
  sketch-geometry (6):
    g0: LineSegment StartX=-33 StartY=235 StartZ=0 EndX=-108 EndY=160 EndZ=0
    g1: LineSegment StartX=-108 StartY=160 StartZ=0 EndX=98 EndY=160 EndZ=0
    g2: LineSegment StartX=98 StartY=160 StartZ=0 EndX=98 EndY=170 EndZ=0
    g3: LineSegment StartX=98 StartY=170 StartZ=0 EndX=33 EndY=235 EndZ=0
    g4: LineSegment StartX=33 StartY=235 StartZ=0 EndX=-33 EndY=235 EndZ=0
    g5: GeomPoint X=108 Y=160 Z=0
  constraints (16):
    c: Coincident(g0,g1)
    c: Coincident(g1,g2)
    c: Vertical(g2)
    c: Coincident(g2,g3)
    c: Coincident(g3,g4)
    c: Coincident(g4,g0)
    c: Angle(g0) = -2.35619
    c: Angle(g3) = 2.35619
    c: PointOnObject(g5,g1)
    c: PointOnObject(g5,g3)
    c: DistanceX(g0,g5) = 216
    c: Symmetric(g0,g5,g-2)
    c: DistanceX(g1,g5) = 10
    c: DistanceY(g0) = 160
    c: Horizontal(g4)
    c: DistanceY(g0) = 235
FEATURE [PartDesign::Pocket] Pocket021  label="Pocket IdlerNutHolderChamfer"
  BaseFeature = -> Pad014
  Direction = (-1,2e-16,-3e-16)
  Length = 34
  Length2 = 5
  Profile = -> Sketch052
  ReferenceAxis = -> Sketch052 [N_Axis]
  Reversed = true
  Type = 1
FEATURE [PartDesign::Pocket] Pocket020  label="Pocket IdlerFitting"
  BaseFeature = -> Pocket021
  Direction = (-1,2e-16,-3e-16)
  Length = 77
  Length2 = 5
  Midplane = true
  Profile = -> Sketch051
  ReferenceAxis = -> Sketch051 [N_Axis]
  Type = 1
FEATURE [Sketcher::SketchObject] Sketch053
  AttachmentOffset = pos=(0,0,-108) rot=(0,0,1;0rad)
  FullyConstrained = true
  MapMode = 5
  Placement = pos=(0,108,2.4e-14) rot=(1,0,0;1.5708rad)
  Support = -> [XZ_Plane013]
  expr: .AttachmentOffset.Base.z = -(<<Variables>>.GantorySpacing + 16) / 2
  expr: Constraints[29] = (<<Variables>>.GantorySpacing + 20) / 2
  expr: Constraints[37] = <<Variables>>.WallThickness
  sketch-geometry (18):
    g0: LineSegment StartX=110 StartY=190 StartZ=0 EndX=0 EndY=190 EndZ=0
    g1: LineSegment StartX=-7 StartY=165.815 StartZ=0 EndX=10 EndY=156 EndZ=0
    g2: LineSegment StartX=10 StartY=156 StartZ=0 EndX=10 EndY=136 EndZ=0
    g3: LineSegment StartX=10 StartY=136 StartZ=0 EndX=0 EndY=130.226 EndZ=0
    g4: LineSegment StartX=0 StartY=130.226 StartZ=0 EndX=0 EndY=109.774 EndZ=0
    g5: LineSegment StartX=0 StartY=109.774 StartZ=0 EndX=10 EndY=104 EndZ=0
    g6: LineSegment StartX=10 StartY=104 StartZ=0 EndX=10 EndY=84 EndZ=0
    g7: LineSegment StartX=10 StartY=84 StartZ=0 EndX=0 EndY=78.2265 EndZ=0
    g8: LineSegment StartX=0 StartY=78.2265 StartZ=0 EndX=0 EndY=57.7735 EndZ=0
    g9: LineSegment StartX=0 StartY=0 StartZ=0 EndX=110 EndY=0 EndZ=0
    g10: LineSegment StartX=110 StartY=0 StartZ=0 EndX=110 EndY=190 EndZ=0
    g11: LineSegment StartX=0 StartY=57.7735 StartZ=0 EndX=10 EndY=52 EndZ=0
    g12: LineSegment StartX=-7 StartY=175 StartZ=0 EndX=-7 EndY=165.815 EndZ=0
    g13: LineSegment StartX=0 StartY=190 StartZ=0 EndX=0 EndY=175 EndZ=0
    g14: LineSegment StartX=0 StartY=175 StartZ=0 EndX=-7 EndY=175 EndZ=0
    g15: LineSegment StartX=10 StartY=52 StartZ=0 EndX=10 EndY=32 EndZ=0
    g16: LineSegment StartX=10 StartY=32 StartZ=0 EndX=0 EndY=26.2265 EndZ=0
    g17: LineSegment StartX=0 StartY=26.2265 StartZ=0 EndX=0 EndY=0 EndZ=0
  constraints (53):
    c: Horizontal(g0)
    c: Coincident(g0,g13)
    c: Coincident(g12,g1)
    c: Coincident(g1,g2)
    c: Coincident(g2,g3)
    c: Coincident(g3,g4)
    c: Vertical(g4)
    c: Coincident(g4,g5)
    c: Coincident(g5,g6)
    c: Coincident(g6,g7)
    c: Coincident(g7,g8)
    c: Vertical(g8)
    c: Coincident(g8,g11)
    c: Coincident(g17,g9)
    c: Horizontal(g9)
    c: Coincident(g9,g10)
    c: Coincident(g10,g0)
    c: Vertical(g10)
    c: Angle(g1) = -0.523599
    c: Vertical(g2)
    c: Angle(g3) = -2.61799
    c: Angle(g5) = -0.523599
    c: Vertical(g6)
    c: Angle(g7) = -2.61799
    c: Vertical(g4,g7)
    c: Coincident(g11,g15)
    c: Vertical(g11,g6)
    c: Vertical(g5,g2)
    c: Angle(g11) = -0.523599
    c: DistanceX(g9) = 110
    c: DistanceY(g10,g10) = 190
    c: Coincident(g14,g12)
    c: Vertical(g12)
    c: Coincident(g13,g14)
    c: Vertical(g13)
    c: PointOnObject(g0,g-2)
    c: Horizontal(g14)
    c: DistanceX(g14,g14) = 7
    c: DistanceY(g13) = 175
    c: DistanceY(g2,g2) = 20
    c: DistanceY(g5,g2) = 32
    c: DistanceY(g6,g6) = 20
    c: DistanceY(g11,g6) = 32
    c: Coincident(g15,g16)
    c: Vertical(g15)
    c: Coincident(g16,g17)
    c: Vertical(g17)
    c: Angle(g16) = -2.61799
    c: Vertical(g16,g8)
    c: Coincident(g9,g-1)
    c: DistanceY(g15,g15) = 20
    c: DistanceY(g15) = 32
    c: DistanceX(g15) = 10
FEATURE [Sketcher::SketchObject] Sketch055
  FullyConstrained = true
  MapMode = 5
  Placement = pos=(0,0,0) rot=(0.57735,0.57735,0.57735;2.0944rad)
  Support = -> [YZ_Plane016]
  sketch-geometry (3):
    g0: Circle CenterX=-64 CenterY=170 CenterZ=0 NormalX=0 NormalY=0 NormalZ=1 AngleXU=0 Radius=1.25
    g1: Circle CenterX=0 CenterY=170 CenterZ=0 NormalX=0 NormalY=0 NormalZ=1 AngleXU=0 Radius=1.25
    g2: Circle CenterX=64 CenterY=170 CenterZ=0 NormalX=0 NormalY=0 NormalZ=1 AngleXU=0 Radius=1.25
  constraints (8):
    c: PointOnObject(g1,g-2)
    c: DistanceY(g1) = 170
    c: Symmetric(g0,g2,g-2)
    c: Horizontal(g0,g1)
    c: DistanceX(g0,g2) = 128
    c: Equal(g0,g1)
    c: Equal(g0,g2)
    c: Diameter(g0) = 2.5
FEATURE [Sketcher::SketchObject] Sketch056
  AttachmentOffset = pos=(0,0,175) rot=(0,0,1;0rad)
  FullyConstrained = true
  MapMode = 5
  Placement = pos=(0,0,175) rot=(0,0,1;0rad)
  Support = -> [XY_Plane016]
  expr: Constraints[17] = (<<Variables>>.GantorySpacing + 16) / 2 - 4
  sketch-geometry (7):
    g0: Circle CenterX=40 CenterY=104 CenterZ=0 NormalX=0 NormalY=0 NormalZ=1 AngleXU=0 Radius=1.25
    g1: Circle CenterX=57.5 CenterY=104 CenterZ=0 NormalX=0 NormalY=0 NormalZ=1 AngleXU=0 Radius=1.25
    g2: Circle CenterX=75 CenterY=104 CenterZ=0 NormalX=0 NormalY=0 NormalZ=1 AngleXU=0 Radius=1.25
    g3: Circle CenterX=5 CenterY=72 CenterZ=0 NormalX=0 NormalY=0 NormalZ=1 AngleXU=0 Radius=1.25
    g4: Circle CenterX=5 CenterY=32 CenterZ=0 NormalX=0 NormalY=0 NormalZ=1 AngleXU=0 Radius=1.25
    g5: Circle CenterX=5 CenterY=-32 CenterZ=0 NormalX=0 NormalY=0 NormalZ=1 AngleXU=0 Radius=1.25
    g6: Circle CenterX=5 CenterY=-72 CenterZ=0 NormalX=0 NormalY=0 NormalZ=1 AngleXU=0 Radius=1.25
  constraints (13):
    c: Horizontal(g0,g1)
    c: Symmetric(g4,g5,g-1)
    c: Symmetric(g3,g6,g-1)
    c: Vertical(g3,g4)
    c: Equal(g0, g1-g6) x6
    c: Diameter(g0) = 2.5
    c: DistanceX(g3) = 5
    c: DistanceY(g5,g4) = 64
    c: DistanceY(g6,g5) = 40
    c: Symmetric(g0,g2,g1)
    c: DistanceX(g0,g2) = 35
    c: DistanceX(g1) = 57.5
    c: DistanceY(g1) = 104
FEATURE [Sketcher::SketchObject] Sketch058
  AttachmentOffset = pos=(0,0,115) rot=(0,0,1;0rad)
  FullyConstrained = true
  MapMode = 5
  Placement = pos=(0,-115,-2.55e-14) rot=(1,0,0;1.5708rad)
  Support = -> [XZ_Plane016]
  expr: .AttachmentOffset.Base.z = (<<Variables>>.GantorySpacing + <<Variables>>.WallThickness * 2 + 16) / 2
  sketch-geometry (1):
    g0: Circle CenterX=5.5 CenterY=182.5 CenterZ=0 NormalX=0 NormalY=0 NormalZ=1 AngleXU=0 Radius=1.25
  constraints (3):
    c: DistanceX(g0) = 5.5
    c: DistanceY(g0) = 182.5
    c: Diameter(g0) = 2.5
FEATURE [Sketcher::SketchObject] Sketch059
  FullyConstrained = true
  MapMode = 5
  Support = -> [XY_Plane016]
  expr: Constraints[14] = <<Variables>>.GantorySpacing + 16 - 10
  expr: Constraints[22] = (<<Variables>>.GantorySpacing + 20) / 2 - 30 - 5
  expr: Constraints[23] = (<<Variables>>.GantorySpacing + 20) / 2 - 5
  sketch-geometry (9):
    g0: Circle CenterX=55 CenterY=80 CenterZ=0 NormalX=0 NormalY=0 NormalZ=1 AngleXU=0 Radius=1.25
    g1: Circle CenterX=55 CenterY=40 CenterZ=0 NormalX=0 NormalY=0 NormalZ=1 AngleXU=0 Radius=1.25
    g2: Circle CenterX=55 CenterY=0 CenterZ=0 NormalX=0 NormalY=0 NormalZ=1 AngleXU=0 Radius=1.25
    g3: Circle CenterX=55 CenterY=-40 CenterZ=0 NormalX=0 NormalY=0 NormalZ=1 AngleXU=0 Radius=1.25
    g4: Circle CenterX=55 CenterY=-80 CenterZ=0 NormalX=0 NormalY=0 NormalZ=1 AngleXU=0 Radius=1.25
    g5: Circle CenterX=55 CenterY=-103 CenterZ=0 NormalX=0 NormalY=0 NormalZ=1 AngleXU=0 Radius=1.25
    g6: Circle CenterX=55 CenterY=103 CenterZ=0 NormalX=0 NormalY=0 NormalZ=1 AngleXU=0 Radius=1.25
    g7: Circle CenterX=75 CenterY=103 CenterZ=0 NormalX=0 NormalY=0 NormalZ=1 AngleXU=0 Radius=1.25
    g8: Circle CenterX=105 CenterY=-103 CenterZ=0 NormalX=0 NormalY=0 NormalZ=1 AngleXU=0 Radius=1.25
  constraints (19):
    c: PointOnObject(g2,g-1)
    c: Symmetric(g1,g3,g-1)
    c: Symmetric(g0,g4,g-1)
    c: Symmetric(g6,g5,g-1)
    c: Vertical(g2,g1)
    c: Vertical(g1,g0)
    c: Vertical(g0,g6)
    c: Equal(g0, g1-g6) x6
    c: Diameter(g0) = 2.5
    c: DistanceY(g5,g6) = 206
    c: DistanceX(g2) = 55
    c: DistanceY(g3,g1) = 80
    c: DistanceY(g4,g3) = 40
    c: Horizontal(g8,g5)
    c: Horizontal(g7,g6)
    c: Equal(g7,g8)
    c: Diameter(g7) = 2.5
    c: DistanceX(g7) = 75
    c: DistanceX(g8) = 105
FEATURE [Sketcher::SketchObject] Sketch060
  FullyConstrained = true
  MapMode = 5
  Support = -> [XY_Plane016]
  expr: Constraints[4] = <<Variables>>.GantorySpacing + 16 - 30
  sketch-geometry (2):
    g0: Circle CenterX=15 CenterY=93 CenterZ=0 NormalX=0 NormalY=0 NormalZ=1 AngleXU=0 Radius=2.25
    g1: Circle CenterX=15 CenterY=-93 CenterZ=0 NormalX=0 NormalY=0 NormalZ=1 AngleXU=0 Radius=2.25
  constraints (5):
    c: Symmetric(g0,g1,g-1)
    c: Equal(g0,g1)
    c: Diameter(g0) = 4.5
    c: DistanceX(g1) = 15
    c: DistanceY(g1,g0) = 186
FEATURE [Sketcher::SketchObject] Sketch061
  AttachmentOffset = pos=(0,0,108) rot=(0,0,1;0rad)
  FullyConstrained = true
  MapMode = 5
  Placement = pos=(0,-108,-2.4e-14) rot=(1,0,0;1.5708rad)
  Support = -> [XZ_Plane016]
  expr: .AttachmentOffset.Base.z = (<<Variables>>.GantorySpacing + 16) / 2
  sketch-geometry (3):
    g0: Circle CenterX=20 CenterY=25 CenterZ=0 NormalX=0 NormalY=0 NormalZ=1 AngleXU=0 Radius=1.25
    g1: Circle CenterX=20 CenterY=5 CenterZ=0 NormalX=0 NormalY=0 NormalZ=1 AngleXU=0 Radius=1.25
    g2: Circle CenterX=75 CenterY=15 CenterZ=0 NormalX=0 NormalY=0 NormalZ=1 AngleXU=0 Radius=1.25
  constraints (9):
    c: Vertical(g1,g0)
    c: DistanceY(g1) = 5
    c: DistanceY(g0) = 25
    c: DistanceY(g2) = 15
    c: DistanceX(g2) = 75
    c: DistanceX(g1) = 20
    c: Equal(g0,g1)
    c: Equal(g0,g2)
    c: Diameter(g0) = 2.5
FEATURE [Sketcher::SketchObject] Sketch062
  AttachmentOffset = pos=(0,0,-108) rot=(0,0,1;0rad)
  FullyConstrained = true
  MapMode = 5
  Placement = pos=(0,108,2.4e-14) rot=(1,0,0;1.5708rad)
  Support = -> [XZ_Plane016]
  expr: .AttachmentOffset.Base.z = -(<<Variables>>.GantorySpacing + 16) / 2
  sketch-geometry (9):
    g0: Circle CenterX=16 CenterY=180 CenterZ=0 NormalX=0 NormalY=0 NormalZ=1 AngleXU=0 Radius=1.25
    g1: Circle CenterX=5 CenterY=170 CenterZ=0 NormalX=0 NormalY=0 NormalZ=1 AngleXU=0 Radius=1.25
    g2: Circle CenterX=72.5 CenterY=92.5 CenterZ=0 NormalX=0 NormalY=0 NormalZ=1 AngleXU=0 Radius=1.25
    g3: Circle CenterX=5 CenterY=20 CenterZ=0 NormalX=0 NormalY=0 NormalZ=1 AngleXU=0 Radius=1.25
    g4: Circle CenterX=5 CenterY=5 CenterZ=0 NormalX=0 NormalY=0 NormalZ=1 AngleXU=0 Radius=1.25
    g5: Circle CenterX=65 CenterY=15 CenterZ=0 NormalX=0 NormalY=0 NormalZ=1 AngleXU=0 Radius=1.25
    g6: Circle CenterX=35 CenterY=5 CenterZ=0 NormalX=0 NormalY=0 NormalZ=1 AngleXU=0 Radius=1.25
    g7: Circle CenterX=5 CenterY=120 CenterZ=0 NormalX=0 NormalY=0 NormalZ=1 AngleXU=0 Radius=1.25
    g8: Circle CenterX=5 CenterY=68 CenterZ=0 NormalX=0 NormalY=0 NormalZ=1 AngleXU=0 Radius=1.25
  constraints (20):
    c: Equal(g0, g1-g8) x8
    c: Diameter(g0) = 2.5
    c: Vertical(g7,g8)
    c: Vertical(g8,g3)
    c: Vertical(g3,g4)
    c: DistanceX(g4) = 5
    c: DistanceY(g8) = 68
    c: DistanceY(g7) = 120
    c: DistanceY(g1) = 170
    c: DistanceY(g2) = 92.5
    c: DistanceY(g5) = 15
    c: DistanceX(g5) = 65
    c: DistanceY(g3) = 20
    c: DistanceY(g4) = 5
    c: DistanceY(g6) = 5
    c: DistanceX(g6) = 35
    c: DistanceX(g2) = 72.5
    c: DistanceY(g0) = 180
    c: DistanceX(g0) = 16
    c: Vertical(g1,g7)
FEATURE [Sketcher::SketchObject] Sketch063
  FullyConstrained = true
  MapMode = 5
  Placement = pos=(0,0,0) rot=(1,0,0;1.5708rad)
  Support = -> [XZ_Plane020]
  expr: Constraints[7] = <<Variables>>.GantorySpacing - 20
  sketch-geometry (6):
    g0: Circle CenterX=-90 CenterY=25 CenterZ=0 NormalX=0 NormalY=0 NormalZ=1 AngleXU=0 Radius=1.5
    g1: Circle CenterX=-90 CenterY=5 CenterZ=0 NormalX=0 NormalY=0 NormalZ=1 AngleXU=0 Radius=1.5
    g2: Circle CenterX=-35 CenterY=15 CenterZ=0 NormalX=0 NormalY=0 NormalZ=1 AngleXU=0 Radius=1.5
    g3: Circle CenterX=35 CenterY=15 CenterZ=0 NormalX=0 NormalY=0 NormalZ=1 AngleXU=0 Radius=1.5
    g4: Circle CenterX=90 CenterY=25 CenterZ=0 NormalX=0 NormalY=0 NormalZ=1 AngleXU=0 Radius=1.5
    g5: Circle CenterX=90 CenterY=5 CenterZ=0 NormalX=0 NormalY=0 NormalZ=1 AngleXU=0 Radius=1.5
  constraints (11):
    c: Vertical(g1,g0)
    c: Symmetric(g0,g4,g-2)
    c: Symmetric(g1,g5,g-2)
    c: Symmetric(g2,g3,g-2)
    c: DistanceY(g2) = 15
    c: DistanceY(g1) = 5
    c: DistanceY(g0) = 25
    c: DistanceX(g1,g5) = 180
    c: DistanceX(g2,g3) = 70
    c: Equal(g0, g1-g5) x5
    c: Diameter(g0) = 3
FEATURE [PartDesign::Hole] Hole024
  BaseFeature = -> Box037
  CustomThreadClearance = 0
  Depth = 396.347
  DepthType = 1
  Diameter = 3.4
  DrillForDepth = false
  DrillPoint = 1
  DrillPointAngle = 118
  HoleCutCountersinkAngle = 90
  HoleCutCustomValues = false
  HoleCutDepth = 0
  HoleCutDiameter = 6.1
  HoleCutType = 0
  ModelThread = false
  Placement = pos=(-95,-5,0) rot=(0,0,1;0rad)
  Profile = -> Sketch063
  Reversed = true
  Tapered = false
  TaperedAngle = 90
  ThreadClass = 0
  ThreadDepth = 396.347
  ThreadDepthType = 0
  ThreadDirection = 0
  ThreadFit = 0
  ThreadSize = 9
  ThreadType = 1
  Threaded = false
  UseCustomThreadClearance = false
FEATURE [PartDesign::Body] Body009  label="FrontPanelPlate"
  Group = -> [Box037,Sketch063,Hole024]
  Origin = -> Origin020
  Tip = -> Hole024
FEATURE [App::Part] Part009  label="FrontPanel"
  Group = -> [Body009,LCS_FrontPanelOrigin]
  Origin = -> Origin019
FEATURE [PartDesign::AdditivePrism] Prism017
  AttacherType = Attacher::AttachEngine3D
  Circumradius = 3.35
  FirstAngle = 0
  Height = 10
  MapMode = 5
  Polygon = 6
  SecondAngle = 0
  Support = -> [XY_Plane027]
FEATURE [PartDesign::Body] Body013  label="M3 inserted Nut"
  Group = -> [Prism017]
  Origin = -> Origin027
  Tip = -> Prism017
FEATURE [Sketcher::SketchObject] Sketch065
  FullyConstrained = true
  MapMode = 5
  Support = -> [XY_Plane028]
  sketch-geometry (8):
    g0: LineSegment StartX=-1.67432 StartY=-2.9 StartZ=0 EndX=1.67432 EndY=-2.9 EndZ=0
    g1: LineSegment StartX=1.67432 StartY=2.9 StartZ=0 EndX=-1.67432 EndY=2.9 EndZ=0
    g2: LineSegment StartX=-1.67432 StartY=2.9 StartZ=0 EndX=-3.34863 EndY=-1.3e-15 EndZ=0
    g3: LineSegment StartX=-3.34863 StartY=-1.3e-15 StartZ=0 EndX=-1.67432 EndY=-2.9 EndZ=0
    g4: Circle CenterX=0 CenterY=0 CenterZ=0 NormalX=0 NormalY=0 NormalZ=1 AngleXU=0 Radius=3.34863
    g5: LineSegment StartX=1.67432 StartY=2.9 StartZ=0 EndX=20 EndY=2.9 EndZ=0
    g6: LineSegment StartX=1.67432 StartY=-2.9 StartZ=0 EndX=20 EndY=-2.9 EndZ=0
    g7: LineSegment StartX=20 StartY=2.9 StartZ=0 EndX=20 EndY=-2.9 EndZ=0
  constraints (23):
    c: Coincident(g1,g2)
    c: Coincident(g2,g3)
    c: Coincident(g3,g0)
    c: Equal(g0,g1)
    c: Equal(g0,g2)
    c: Equal(g0,g3)
    c: PointOnObject(g0,g4)
    c: PointOnObject(g1,g4)
    c: PointOnObject(g1,g4)
    c: PointOnObject(g2,g4)
    c: PointOnObject(g3,g4)
    c: Coincident(g6,g0)
    c: Parallel(g0,g6)
    c: Parallel(g5,g1)
    c: Coincident(g7,g5)
    c: Coincident(g7,g6)
    c: Equal(g5,g6)
    c: Distance(g1,g0) = 5.8
    c: Distance(g4,g7) = 20
    c: Coincident(g4,g-1)
    c: Parallel(g5,g-1)
    c: Angle(g3,g2) = 2.0944
    c: Coincident(g5,g1)
FEATURE [PartDesign::Pad] Pad015
  Direction = (0,0,1)
  Length = 3
  Length2 = 10
  Profile = -> Sketch065
  ReferenceAxis = -> Sketch065 [N_Axis]
  Type = 0
FEATURE [PartDesign::Body] Body014  label="M3 grooved Nut"
  Group = -> [Sketch065,Pad015]
  Origin = -> Origin028
  Tip = -> Pad015
FEATURE [Part::FeaturePython] Clone  label="M3 inserted Nut TopBeam 1"  # Draft clone (typed FeaturePython)
  AttacherType = Attacher::AttachEngine3D
  Fuse = false
  Objects = -> [Body013]
  Placement = pos=(5,0,170) rot=(0.57735,0.57735,0.57735;2.0944rad)
  Scale = (1,1,1)
FEATURE [Part::FeaturePython] Clone001  label="M3 inserted Nut TopBeam 2"  # Draft clone (typed FeaturePython)
  AttacherType = Attacher::AttachEngine3D
  Fuse = false
  Objects = -> [Body013]
  Placement = pos=(5,-64,170) rot=(0.57735,0.57735,0.57735;2.0944rad)
  Scale = (1,1,1)
FEATURE [Part::FeaturePython] Clone002  label="M3 inserted Nut TopBeam 3"  # Draft clone (typed FeaturePython)
  AttacherType = Attacher::AttachEngine3D
  Fuse = false
  Objects = -> [Clone001]
  Placement = pos=(5,64,170) rot=(0.57735,0.57735,0.57735;2.0944rad)
  Scale = (1,1,1)
FEATURE [Part::FeaturePython] Clone003  label="M3 inserted Nut TopBeam 4"  # Draft clone (typed FeaturePython)
  AttacherType = Attacher::AttachEngine3D
  Fuse = false
  Objects = -> [Clone002]
  Placement = pos=(5,-32,165) rot=(0.707107,0.707107,0;3.14159rad)
  Scale = (1,1,1)
FEATURE [Part::FeaturePython] Clone004  label="M3 inserted Nut TopBeam 5"  # Draft clone (typed FeaturePython)
  AttacherType = Attacher::AttachEngine3D
  Fuse = false
  Objects = -> [Clone003]
  Placement = pos=(5,-72,165) rot=(0.707107,0.707107,0;3.14159rad)
  Scale = (1,1,1)
FEATURE [Part::FeaturePython] Clone005  label="M3 inserted Nut TopBeam 6"  # Draft clone (typed FeaturePython)
  AttacherType = Attacher::AttachEngine3D
  Fuse = false
  Objects = -> [Clone004]
  Placement = pos=(5,32,165) rot=(0.707107,0.707107,0;3.14159rad)
  Scale = (1,1,1)
FEATURE [Part::FeaturePython] Clone006  label="M3 inserted Nut TopBeam 7"  # Draft clone (typed FeaturePython)
  AttacherType = Attacher::AttachEngine3D
  Fuse = false
  Objects = -> [Clone005]
  Placement = pos=(5,72,165) rot=(0.707107,0.707107,0;3.14159rad)
  Scale = (1,1,1)
FEATURE [Part::FeaturePython] Clone007  label="M3 inserted Nut TopFront 1"  # Draft clone (typed FeaturePython)
  AttacherType = Attacher::AttachEngine3D
  Fuse = false
  Objects = -> [Clone006]
  Placement = pos=(5.5,-97,182.5) rot=(-1,0,0;1.5708rad)
  Scale = (1,1,1)
FEATURE [Part::FeaturePython] Clone008  label="M3 inserted Nut Front 1"  # Draft clone (typed FeaturePython)
  AttacherType = Attacher::AttachEngine3D
  Fuse = false
  Objects = -> [Clone007]
  Placement = pos=(20,-101,25) rot=(-1,0,0;1.5708rad)
  Scale = (1,1,1)
FEATURE [Part::FeaturePython] Clone009  label="M3 inserted Nut Front 2"  # Draft clone (typed FeaturePython)
  AttacherType = Attacher::AttachEngine3D
  Fuse = false
  Objects = -> [Clone008]
  Placement = pos=(75,-101,15) rot=(-1,0,0;1.5708rad)
  Scale = (1,1,1)
FEATURE [Part::FeaturePython] Clone010  label="M3 inserted Nut Bottom 1"  # Draft clone (typed FeaturePython)
  AttacherType = Attacher::AttachEngine3D
  Fuse = false
  Objects = -> [Clone009]
  Placement = pos=(55,-103,15) rot=(0,0,1;0rad)
  Scale = (1,1,1)
FEATURE [Part::FeaturePython] Clone011  label="M3 inserted Nut Bottom 2"  # Draft clone (typed FeaturePython)
  AttacherType = Attacher::AttachEngine3D
  Fuse = false
  Objects = -> [Body013]
  Placement = pos=(105,-103,17) rot=(0,0,1;0rad)
  Scale = (1,1,1)
FEATURE [Part::FeaturePython] Clone012  label="M3 inserted Nut Bottom 3"  # Draft clone (typed FeaturePython)
  AttacherType = Attacher::AttachEngine3D
  Fuse = false
  Objects = -> [Clone011]
  Placement = pos=(55,-80,13.5) rot=(0,0,1;0rad)
  Scale = (1,1,1)
FEATURE [Part::FeaturePython] Clone013  label="M3 inserted Nut Bottom 4"  # Draft clone (typed FeaturePython)
  AttacherType = Attacher::AttachEngine3D
  Fuse = false
  Objects = -> [Clone012]
  Placement = pos=(55,-40,13.5) rot=(0,0,1;0rad)
  Scale = (1,1,1)
FEATURE [Part::FeaturePython] Clone014  label="M3 inserted Nut Bottom 5"  # Draft clone (typed FeaturePython)
  AttacherType = Attacher::AttachEngine3D
  Fuse = false
  Objects = -> [Clone013]
  Placement = pos=(55,0,13.5) rot=(0,0,1;0rad)
  Scale = (1,1,1)
FEATURE [Part::FeaturePython] Clone015  label="M3 inserted Nut Bottom 6"  # Draft clone (typed FeaturePython)
  AttacherType = Attacher::AttachEngine3D
  Fuse = false
  Objects = -> [Clone014]
  Placement = pos=(55,40,13.5) rot=(0,0,1;0rad)
  Scale = (1,1,1)
FEATURE [Part::FeaturePython] Clone016  label="M3 inserted Nut Bottom 7"  # Draft clone (typed FeaturePython)
  AttacherType = Attacher::AttachEngine3D
  Fuse = false
  Objects = -> [Clone015]
  Placement = pos=(55,80,13.5) rot=(0,0,1;0rad)
  Scale = (1,1,1)
FEATURE [Part::FeaturePython] Clone017  label="M3 inserted Nut Bottom 8"  # Draft clone (typed FeaturePython)
  AttacherType = Attacher::AttachEngine3D
  Fuse = false
  Objects = -> [Clone016]
  Placement = pos=(55,103,15) rot=(0,0,1;0rad)
  Scale = (1,1,1)
FEATURE [Part::FeaturePython] Clone018  label="M3 inserted Nut Rear 1"  # Draft clone (typed FeaturePython)
  AttacherType = Attacher::AttachEngine3D
  Fuse = false
  Objects = -> [Clone017]
  Placement = pos=(16,103,180) rot=(1,0,0;1.5708rad)
  Scale = (1,1,1)
FEATURE [Part::FeaturePython] Clone019  label="M3 inserted Nut RearTop 1"  # Draft clone (typed FeaturePython)
  AttacherType = Attacher::AttachEngine3D
  Fuse = false
  Objects = -> [Body013]
  Placement = pos=(40,104,168) rot=(0,1,0;3.14159rad)
  Scale = (1,1,1)
FEATURE [Part::FeaturePython] Clone020  label="M3 inserted Nut RearTop 2"  # Draft clone (typed FeaturePython)
  AttacherType = Attacher::AttachEngine3D
  Fuse = false
  Objects = -> [Body013]
  Placement = pos=(57.5,104,168) rot=(0,1,0;3.14159rad)
  Scale = (1,1,1)
FEATURE [PartDesign::AdditivePrism] Prism018
  AttacherType = Attacher::AttachEngine3D
  Circumradius = 3.35
  FirstAngle = 0
  Height = 6
  MapMode = 5
  Polygon = 6
  SecondAngle = 0
  Support = -> [XY_Plane029]
FEATURE [PartDesign::Body] Body015  label="M3 inserted Nut L6"
  Group = -> [Prism018]
  Origin = -> Origin029
  Tip = -> Prism018
FEATURE [Part::FeaturePython] Clone021  label="M3 inserted Nut Rear 3"  # Draft clone (typed FeaturePython)
  AttacherType = Attacher::AttachEngine3D
  Fuse = false
  Objects = -> [Body013]
  Placement = pos=(5,101,120) rot=(1,0,0;1.5708rad)
  Scale = (1,1,1)
FEATURE [Part::FeaturePython] Clone022  label="M3 inserted Nut Rear 4"  # Draft clone (typed FeaturePython)
  AttacherType = Attacher::AttachEngine3D
  Fuse = false
  Objects = -> [Clone021]
  Placement = pos=(5,101,68) rot=(1,0,0;1.5708rad)
  Scale = (1,1,1)
FEATURE [Part::FeaturePython] Clone023  label="M3 inserted Nut Rear 5"  # Draft clone (typed FeaturePython)
  AttacherType = Attacher::AttachEngine3D
  Fuse = false
  Objects = -> [Clone022]
  Placement = pos=(5,101,20) rot=(1,0,0;1.5708rad)
  Scale = (1,1,1)
FEATURE [Part::FeaturePython] Clone024  label="M3 inserted Nut Rear 2"  # Draft clone (typed FeaturePython)
  AttacherType = Attacher::AttachEngine3D
  Fuse = false
  Objects = -> [Body015]
  Placement = pos=(5,101,170) rot=(1,0,0;1.5708rad)
  Scale = (1,1,1)
FEATURE [Part::FeaturePython] Clone025  label="M3 inserted Nut Front 3"  # Draft clone (typed FeaturePython)
  AttacherType = Attacher::AttachEngine3D
  Fuse = false
  Objects = -> [Body015]
  Placement = pos=(20,-95,5) rot=(0.862856,0.357407,-0.357407;1.71777rad)
  Scale = (1,1,1)
FEATURE [Part::FeaturePython] Clone026  label="M3 inserted Nut Rear 6"  # Draft clone (typed FeaturePython)
  AttacherType = Attacher::AttachEngine3D
  Fuse = false
  Objects = -> [Clone025]
  Placement = pos=(5,101,5) rot=(0.862856,0.357407,-0.357407;1.71777rad)
  Scale = (1,1,1)
FEATURE [Part::FeaturePython] Clone027  label="M3 inserted Nut Rear 8"  # Draft clone (typed FeaturePython)
  AttacherType = Attacher::AttachEngine3D
  Fuse = false
  Objects = -> [Clone026]
  Placement = pos=(65,101,15) rot=(1,0,0;1.5708rad)
  Scale = (1,1,1)
FEATURE [Part::FeaturePython] Clone028  label="M3 grooved Nut Idler 1"  # Draft clone (typed FeaturePython)
  AttacherType = Attacher::AttachEngine3D
  Fuse = false
  Objects = -> [Body014]
  Placement = pos=(10,-100,184) rot=(0.965926,0.258819,0;3.14159rad)
  Scale = (1,1,1)
FEATURE [Part::FeaturePython] Clone029  label="M3 grooved Nut Idler 2"  # Draft clone (typed FeaturePython)
  AttacherType = Attacher::AttachEngine3D
  Fuse = false
  Objects = -> [Clone028]
  Placement = pos=(10,100,184) rot=(0.965926,-0.258819,0;3.14159rad)
  Scale = (1,1,1)
FEATURE [Part::FeaturePython] Clone030  label="M3 grooved Nut RearTop 3"  # Draft clone (typed FeaturePython)
  AttacherType = Attacher::AttachEngine3D
  Fuse = false
  Objects = -> [Clone029]
  Placement = pos=(75,104,168) rot=(1,0,0;3.14159rad)
  Scale = (1,1,1)
FEATURE [Part::FeaturePython] Clone031  label="M3 grooved Nut Front 3"  # Draft clone (typed FeaturePython)
  AttacherType = Attacher::AttachEngine3D
  Fuse = false
  Objects = -> [Clone030]
  Placement = pos=(20,-98,5) rot=(-0.862856,0.357407,0.357407;1.71777rad)
  Scale = (1,1,1)
FEATURE [Part::FeaturePython] Clone032  label="M3 grooved Nut Rear 2"  # Draft clone (typed FeaturePython)
  AttacherType = Attacher::AttachEngine3D
  Fuse = false
  Objects = -> [Body014]
  Placement = pos=(5,95,170) rot=(1,0,0;1.5708rad)
  Scale = (1,1,1)
FEATURE [Part::FeaturePython] Clone033  label="M3 grooved Nut Rear 6"  # Draft clone (typed FeaturePython)
  AttacherType = Attacher::AttachEngine3D
  Fuse = false
  Objects = -> [Body014]
  Placement = pos=(5,98,5) rot=(0.862856,0.357407,-0.357407;1.71777rad)
  Scale = (1,1,1)
FEATURE [Part::FeaturePython] Clone034  label="M3 inserted Nut Rear 7"  # Draft clone (typed FeaturePython)
  AttacherType = Attacher::AttachEngine3D
  Fuse = false
  Objects = -> [Body013]
  Placement = pos=(72.5,101,92.5) rot=(1,0,0;1.5708rad)
  Scale = (1,1,1)
FEATURE [Part::FeaturePython] Clone035  label="M3 inserted Nut Rear 9"  # Draft clone (typed FeaturePython)
  AttacherType = Attacher::AttachEngine3D
  Fuse = false
  Objects = -> [Body015]
  Placement = pos=(35,101,5) rot=(0.862856,0.357407,-0.357407;1.71777rad)
  Scale = (1,1,1)
FEATURE [Part::FeaturePython] Clone036  label="M3 grooved Nut Rear 9"  # Draft clone (typed FeaturePython)
  AttacherType = Attacher::AttachEngine3D
  Fuse = false
  Objects = -> [Body014]
  Placement = pos=(35,98,5) rot=(0.862856,0.357407,-0.357407;1.71777rad)
  Scale = (1,1,1)
FEATURE [Sketcher::SketchObject] Sketch066
  FullyConstrained = true
  MapMode = 5
  Support = -> [XY_Plane016]
  expr: Constraints[17] = (<<Variables>>.GantorySpacing + 16 - 10) / 2
  expr: Constraints[18] = -(<<Variables>>.GantorySpacing + 16 - 10) / 2
  sketch-geometry (7):
    g0: Circle CenterX=5 CenterY=80 CenterZ=0 NormalX=0 NormalY=0 NormalZ=1 AngleXU=0 Radius=1.25
    g1: Circle CenterX=5 CenterY=-80 CenterZ=0 NormalX=0 NormalY=0 NormalZ=1 AngleXU=0 Radius=1.25
    g2: Circle CenterX=5 CenterY=0 CenterZ=0 NormalX=0 NormalY=0 NormalZ=1 AngleXU=0 Radius=1.25
    g3: Circle CenterX=5 CenterY=40 CenterZ=0 NormalX=0 NormalY=0 NormalZ=1 AngleXU=0 Radius=1.25
    g4: Circle CenterX=5 CenterY=-40 CenterZ=0 NormalX=0 NormalY=0 NormalZ=1 AngleXU=0 Radius=1.25
    g5: Circle CenterX=5 CenterY=-103 CenterZ=0 NormalX=0 NormalY=0 NormalZ=1 AngleXU=0 Radius=1.25
    g6: Circle CenterX=15 CenterY=103 CenterZ=0 NormalX=0 NormalY=0 NormalZ=1 AngleXU=0 Radius=1.25
  constraints (14):
    c: PointOnObject(g2,g-1)
    c: DistanceX(g2) = 5
    c: DistanceY(g1,g0) = 160
    c: DistanceY(g4,g3) = 80
    c: Symmetric(g3,g4,g-1)
    c: Symmetric(g0,g1,g-1)
    c: Vertical(g2,g4)
    c: Vertical(g4,g1)
    c: Equal(g0, g1-g6) x6
    c: Diameter(g0) = 2.5
    c: DistanceX(g6) = 15
    c: DistanceX(g5) = 5
    c: DistanceY(g6) = 103
    c: DistanceY(g5) = -103
FEATURE [Part::FeaturePython] Clone037  label="M3 grooved Nut Rear 10"  # Draft clone (typed FeaturePython)
  AttacherType = Attacher::AttachEngine3D
  Fuse = false
  Objects = -> [Body014]
  Placement = pos=(75,103,17) rot=(0,0,1;0rad)
  Scale = (1,1,1)
FEATURE [Part::FeaturePython] Clone038  label="M3 grooved Nut Skirt 1"  # Draft clone (typed FeaturePython)
  AttacherType = Attacher::AttachEngine3D
  Fuse = false
  Objects = -> [Clone037]
  Placement = pos=(5,-103,10) rot=(0,0,1;0.785398rad)
  Scale = (1,1,1)
FEATURE [Part::FeaturePython] Clone039  label="M3 grooved Nut Skirt 2"  # Draft clone (typed FeaturePython)
  AttacherType = Attacher::AttachEngine3D
  Fuse = false
  Objects = -> [Clone038]
  Placement = pos=(5,-80,10) rot=(0,0,1;0rad)
  Scale = (1,1,1)
FEATURE [Part::FeaturePython] Clone040  label="M3 grooved Nut Skirt 3"  # Draft clone (typed FeaturePython)
  AttacherType = Attacher::AttachEngine3D
  Fuse = false
  Objects = -> [Clone039]
  Placement = pos=(5,-40,10) rot=(0,0,1;0rad)
  Scale = (1,1,1)
FEATURE [Part::FeaturePython] Clone041  label="M3 grooved Nut Skirt 4"  # Draft clone (typed FeaturePython)
  AttacherType = Attacher::AttachEngine3D
  Fuse = false
  Objects = -> [Clone040]
  Placement = pos=(5,0,10) rot=(0,0,1;0rad)
  Scale = (1,1,1)
FEATURE [Part::FeaturePython] Clone042  label="M3 grooved Nut Skirt 5"  # Draft clone (typed FeaturePython)
  AttacherType = Attacher::AttachEngine3D
  Fuse = false
  Objects = -> [Clone041]
  Placement = pos=(5,40,10) rot=(0,0,1;0rad)
  Scale = (1,1,1)
FEATURE [Part::FeaturePython] Clone043  label="M3 grooved Nut Skirt 6"  # Draft clone (typed FeaturePython)
  AttacherType = Attacher::AttachEngine3D
  Fuse = false
  Objects = -> [Clone042]
  Placement = pos=(5,80,10) rot=(0,0,1;0rad)
  Scale = (1,1,1)
FEATURE [Part::FeaturePython] Clone044  label="M3 grooved Nut Skirt 7"  # Draft clone (typed FeaturePython)
  AttacherType = Attacher::AttachEngine3D
  Fuse = false
  Objects = -> [Clone043]
  Placement = pos=(15,103,10) rot=(0,0,-1;0.785398rad)
  Scale = (1,1,1)
FEATURE [Sketcher::SketchObject] Sketch067
  FullyConstrained = true
  MapMode = 5
  Placement = pos=(0,0,0) rot=(1,0,0;1.5708rad)
  Support = -> [XZ_Plane016]
  expr: Constraints[12] = Sketch045.Constraints[13]
  expr: Constraints[13] = Sketch045.Constraints[14]
  expr: Constraints[17] = Sketch045.Constraints[21]
  expr: Constraints[33] = Sketch045.Constraints[41]
  expr: Constraints[34] = Sketch045.Constraints[43]
  expr: Constraints[36] = Sketch045.Constraints[45]
  expr: Constraints[42] = Sketch045.Constraints[51]
  expr: Constraints[44] = Sketch045.Constraints[54]
  expr: Constraints[46] = Sketch045.Constraints[57]
  expr: Constraints[47] = Sketch045.Constraints[58]
  expr: Constraints[48] = Sketch045.Constraints[59]
  expr: Constraints[49] = Sketch045.Constraints[60]
  expr: Constraints[59] = Sketch045.Constraints[75]
  expr: Constraints[5] = Sketch045.Constraints[6]
  expr: Constraints[62] = Sketch045.Constraints[78]
  expr: Constraints[63] = Sketch045.Constraints[79]
  expr: Constraints[69] = Sketch045.Constraints[85]
  expr: Constraints[6] = Sketch045.Constraints[7]
  expr: Constraints[70] = Sketch045.Constraints[86]
  expr: Constraints[76] = Sketch045.Constraints[92]
  expr: Constraints[77] = Sketch045.Constraints[93]
  expr: Constraints[78] = Sketch045.Constraints[94]
  sketch-geometry (37):
    g0: LineSegment StartX=110 StartY=190 StartZ=0 EndX=33 EndY=190 EndZ=0
    g1: LineSegment StartX=66.2365 StartY=94.6213 StartZ=0 EndX=15.1213 EndY=145.737 EndZ=0
    g2: LineSegment StartX=10 StartY=143.615 StartZ=0 EndX=10 EndY=41.3848 EndZ=0
    g3: LineSegment StartX=15.1213 StartY=39.2635 StartZ=0 EndX=66.2365 EndY=90.3787 EndZ=0
    g4: LineSegment StartX=80 StartY=10 StartZ=0 EndX=60 EndY=10 EndZ=0
    g5: LineSegment StartX=110 StartY=190 StartZ=0 EndX=110 EndY=0 EndZ=0
    g6: LineSegment StartX=33 StartY=190 StartZ=0 EndX=33 EndY=175 EndZ=0
    g7: LineSegment StartX=33 StartY=175 StartZ=0 EndX=80 EndY=175 EndZ=0
    g8: LineSegment StartX=77 StartY=105 StartZ=0 EndX=71.2426 EndY=105 EndZ=0
    g9: LineSegment StartX=69.1213 StartY=105.879 StartZ=0 EndX=15.1213 EndY=159.879 EndZ=0
    g10: LineSegment StartX=17.2426 StartY=165 StartZ=0 EndX=80 EndY=165 EndZ=0
    g11: GeomPoint X=70 Y=105 Z=0
    g12: ArcOfCircle CenterX=13 CenterY=143.615 CenterZ=0 NormalX=0 NormalY=0 NormalZ=1 AngleXU=0 Radius=3 StartAngle=0.785398 EndAngle=3.14159
    g13: GeomPoint X=10 Y=150.858 Z=0
    g14: ArcOfCircle CenterX=17.2426 CenterY=162 CenterZ=0 NormalX=0 NormalY=0 NormalZ=1 AngleXU=0 Radius=3 StartAngle=1.5708 EndAngle=3.92699
    g15: GeomPoint X=10 Y=165 Z=0
    g16: ArcOfCircle CenterX=77 CenterY=102 CenterZ=0 NormalX=0 NormalY=0 NormalZ=1 AngleXU=0 Radius=3 StartAngle=-9e-16 EndAngle=1.5708
    g17: ArcOfCircle CenterX=71.2426 CenterY=108 CenterZ=0 NormalX=0 NormalY=0 NormalZ=1 AngleXU=0 Radius=3 StartAngle=3.92699 EndAngle=4.71239
    g18: GeomPoint X=70 Y=105 Z=0
    g19: ArcOfCircle CenterX=13 CenterY=41.3848 CenterZ=0 NormalX=0 NormalY=0 NormalZ=1 AngleXU=0 Radius=3 StartAngle=3.14159 EndAngle=5.49779
    g20: GeomPoint X=10 Y=34.1421 Z=0
    g21: LineSegment StartX=15.1213 StartY=25.1213 StartZ=0 EndX=69.1213 EndY=79.1213 EndZ=0
    g22: LineSegment StartX=71.2426 StartY=80 StartZ=0 EndX=77 EndY=80 EndZ=0
    g23: LineSegment StartX=80 StartY=20 StartZ=0 EndX=17.2426 EndY=20 EndZ=0
    g24: ArcOfCircle CenterX=71.2426 CenterY=77 CenterZ=0 NormalX=0 NormalY=0 NormalZ=1 AngleXU=0 Radius=3 StartAngle=1.5708 EndAngle=2.35619
    g25: GeomPoint X=70 Y=80 Z=0
    g26: ArcOfCircle CenterX=77 CenterY=83 CenterZ=0 NormalX=0 NormalY=0 NormalZ=1 AngleXU=0 Radius=3 StartAngle=4.71239 EndAngle=6.28319
    g27: ArcOfCircle CenterX=17.2426 CenterY=23 CenterZ=0 NormalX=0 NormalY=0 NormalZ=1 AngleXU=0 Radius=3 StartAngle=2.35619 EndAngle=4.71239
    g28: GeomPoint X=10 Y=20 Z=0
    g29: ArcOfCircle CenterX=64.1152 CenterY=92.5 CenterZ=0 NormalX=0 NormalY=0 NormalZ=1 AngleXU=0 Radius=3 StartAngle=5.49779 EndAngle=7.06858
    g30: LineSegment StartX=110 StartY=0 StartZ=0 EndX=50 EndY=0 EndZ=0
    g31: LineSegment StartX=60 StartY=5 StartZ=0 EndX=60 EndY=10 EndZ=0
    g32: LineSegment StartX=50 StartY=0 StartZ=0 EndX=50 EndY=5 EndZ=0
    g33: LineSegment StartX=50 StartY=5 StartZ=0 EndX=60 EndY=5 EndZ=0
    g34: LineSegment StartX=80 StartY=175 StartZ=0 EndX=80 EndY=165 EndZ=0
    g35: LineSegment StartX=80 StartY=102 StartZ=0 EndX=80 EndY=83 EndZ=0
    g36: LineSegment StartX=80 StartY=20 StartZ=0 EndX=80 EndY=10 EndZ=0
  constraints (95):
    c: Horizontal(g0)
    c: Vertical(g2)
    c: Horizontal(g4)
    c: Coincident(g5,g0)
    c: Vertical(g5)
    c: DistanceX(g-1,g20) = 10
    c: DistanceX(g34,g0) = 30
    c: Coincident(g0,g6)
    c: Vertical(g6)
    c: Coincident(g6,g7)
    c: Coincident(g7,g34)
    c: Horizontal(g7)
    c: DistanceY(g-1,g34) = 175
    c: DistanceX(g-1,g0) = 33
    c: Horizontal(g10)
    c: PointOnObject(g11,g8)
    c: PointOnObject(g11,g9)
    c: DistanceY(g15,g6) = 10
    c: PointOnObject(g13,g1)
    c: PointOnObject(g13,g2)
    c: Tangent(g1,g12) = -1.5708
    c: Tangent(g2,g12) = -1.5708
    c: Coincident(g36,g4)
    c: PointOnObject(g15,g10)
    c: PointOnObject(g15,g9)
    c: Tangent(g10,g14) = 1.5708
    c: Tangent(g9,g14) = 1.5708
    c: PointOnObject(g18,g9)
    c: PointOnObject(g18,g8)
    c: Tangent(g9,g17) = 1.5708
    c: Tangent(g8,g17) = 1.5708
    c: Equal(g14,g16)
    c: Equal(g14,g17)
    c: Radius(g14) = 3
    c: Angle(g9) = 2.35619
    c: Parallel(g1,g9)
    c: Distance(g13,g9) = 10
    c: PointOnObject(g20,g3)
    c: PointOnObject(g20,g2)
    c: Tangent(g3,g19) = -1.5708
    c: Tangent(g2,g19) = -1.5708
    c: Equal(g12,g19)
    c: Radius(g12) = 3
    c: Horizontal(g23)
    c: Angle(g21) = 0.785398
    c: Parallel(g21,g3)
    c: Distance(g3,g21) = 10
    c: DistanceY(g-1,g28) = 20
    c: DistanceX(g-1,g15) = 10
    c: DistanceX(g-1,g28) = 10
    c: PointOnObject(g25,g21)
    c: PointOnObject(g25,g22)
    c: Tangent(g21,g24) = 1.5708
    c: PointOnObject(g28,g23)
    c: PointOnObject(g28,g21)
    c: Tangent(g23,g27) = 1.5708
    c: Tangent(g21,g27) = 1.5708
    c: Equal(g24,g26)
    c: Equal(g24,g27)
    c: Radius(g24) = 3
    c: Tangent(g1,g29) = -1.5708
    c: Tangent(g3,g29) = -1.5708
    c: Radius(g29) = 3
    c: DistanceX(g-1,g0) = 110
    c: Coincident(g30,g5)
    c: Horizontal(g30)
    c: Coincident(g31,g4)
    c: Vertical(g31)
    c: PointOnObject(g5,g-1)
    c: DistanceY(g5,g5) = 190
    c: DistanceY(g-1,g4) = 10
    c: Coincident(g32,g30)
    c: Vertical(g32)
    c: Coincident(g33,g32)
    c: Coincident(g33,g31)
    c: Horizontal(g33)
    c: DistanceX(g-1,g4) = 60
    c: DistanceX(g33,g33) = 10
    c: DistanceY(g32,g32) = 5
    c: Vertical(g34)
    c: Coincident(g10,g34)
    c: Horizontal(g8)
    c: Tangent(g8,g16) = -1.5708
    c: DistanceX(g11,g7) = 10
    c: Tangent(g16,g35) = 1.5708
    c: Tangent(g22,g24) = 1.5708
    c: Horizontal(g22)
    c: Tangent(g26,g22) = -1.5708
    c: Vertical(g35)
    c: Vertical(g36)
    c: Tangent(g26,g35) = 1.5708
    c: Vertical(g25,g11)
    c: Coincident(g23,g36)
    c: PointOnObject(g16,g34)
    c: PointOnObject(g23,g34)
FEATURE [PartDesign::Pocket] Pocket015  label="Pocket RearBeam"
  BaseFeature = -> Pocket020
  Direction = (0,1,2e-16)
  Length = 5
  Length2 = 5
  Profile = -> Sketch067
  ReferenceAxis = -> Sketch067 [N_Axis]
  Type = 1
FEATURE [PartDesign::Pocket] Pocket022  label="Pocket RearPanelFitting"
  BaseFeature = -> Pocket015
  Direction = (0,1,2e-16)
  Length = 7
  Length2 = 5
  Profile = -> Sketch053
  ReferenceAxis = -> Sketch053 [N_Axis]
  Type = 0
  expr: Length = <<Variables>>.WallThickness
FEATURE [PartDesign::Hole] Hole017  label="Hole Idler"
  BaseFeature = -> Pocket022
  CustomThreadClearance = 0
  Depth = 14
  DepthType = 0
  Diameter = 2.5
  DrillForDepth = false
  DrillPoint = 1
  DrillPointAngle = 118
  HoleCutCountersinkAngle = 90
  HoleCutCustomValues = false
  HoleCutDepth = 0
  HoleCutDiameter = 6.1
  HoleCutType = 0
  ModelThread = false
  Profile = -> Sketch050
  Tapered = false
  TaperedAngle = 90
  ThreadClass = 0
  ThreadDepth = 14
  ThreadDepthType = 0
  ThreadDirection = 0
  ThreadFit = 0
  ThreadSize = 9
  ThreadType = 1
  Threaded = true
  UseCustomThreadClearance = false
FEATURE [PartDesign::Hole] Hole019  label="Hole TopFitting"
  BaseFeature = -> Hole017
  CustomThreadClearance = 0
  Depth = 15
  DepthType = 0
  Diameter = 2.5
  DrillForDepth = false
  DrillPoint = 1
  DrillPointAngle = 118
  HoleCutCountersinkAngle = 90
  HoleCutCustomValues = false
  HoleCutDepth = 0
  HoleCutDiameter = 6.1
  HoleCutType = 0
  ModelThread = false
  Profile = -> Sketch056
  Tapered = false
  TaperedAngle = 90
  ThreadClass = 0
  ThreadDepth = 15
  ThreadDepthType = 0
  ThreadDirection = 0
  ThreadFit = 0
  ThreadSize = 9
  ThreadType = 1
  Threaded = true
  UseCustomThreadClearance = false
FEATURE [PartDesign::Hole] Hole018  label="Hole SideFitting"
  BaseFeature = -> Hole019
  CustomThreadClearance = 0
  Depth = 646.116
  DepthType = 1
  Diameter = 2.5
  DrillForDepth = false
  DrillPoint = 1
  DrillPointAngle = 118
  HoleCutCountersinkAngle = 90
  HoleCutCustomValues = false
  HoleCutDepth = 0
  HoleCutDiameter = 6.1
  HoleCutType = 0
  ModelThread = false
  Profile = -> Sketch055
  Reversed = true
  Tapered = false
  TaperedAngle = 90
  ThreadClass = 0
  ThreadDepth = 646.116
  ThreadDepthType = 0
  ThreadDirection = 0
  ThreadFit = 0
  ThreadSize = 9
  ThreadType = 1
  Threaded = true
  UseCustomThreadClearance = false
FEATURE [PartDesign::Hole] Hole020  label="Hole TopFrontFitting"
  BaseFeature = -> Hole018
  CustomThreadClearance = 0
  Depth = 25
  DepthType = 0
  Diameter = 2.5
  DrillForDepth = false
  DrillPoint = 1
  DrillPointAngle = 118
  HoleCutCountersinkAngle = 90
  HoleCutCustomValues = false
  HoleCutDepth = 0
  HoleCutDiameter = 6.1
  HoleCutType = 0
  ModelThread = false
  Profile = -> Sketch058
  Tapered = false
  TaperedAngle = 90
  ThreadClass = 0
  ThreadDepth = 25
  ThreadDepthType = 0
  ThreadDirection = 0
  ThreadFit = 0
  ThreadSize = 9
  ThreadType = 1
  Threaded = true
  UseCustomThreadClearance = false
FEATURE [PartDesign::Hole] Hole021  label="Hole BottomFitting"
  BaseFeature = -> Hole020
  CustomThreadClearance = 0
  Depth = 25
  DepthType = 0
  Diameter = 2.5
  DrillForDepth = false
  DrillPoint = 1
  DrillPointAngle = 118
  HoleCutCountersinkAngle = 90
  HoleCutCustomValues = false
  HoleCutDepth = 0
  HoleCutDiameter = 6.1
  HoleCutType = 0
  ModelThread = false
  Profile = -> Sketch059
  Reversed = true
  Tapered = false
  TaperedAngle = 90
  ThreadClass = 0
  ThreadDepth = 25
  ThreadDepthType = 0
  ThreadDirection = 0
  ThreadFit = 0
  ThreadSize = 9
  ThreadType = 1
  Threaded = true
  UseCustomThreadClearance = false
FEATURE [PartDesign::Hole] Hole023  label="Hole FrontFitting"
  BaseFeature = -> Hole021
  CustomThreadClearance = 0
  Depth = 15
  DepthType = 0
  Diameter = 2.5
  DrillForDepth = false
  DrillPoint = 1
  DrillPointAngle = 118
  HoleCutCountersinkAngle = 90
  HoleCutCustomValues = false
  HoleCutDepth = 0
  HoleCutDiameter = 6.1
  HoleCutType = 0
  ModelThread = false
  Profile = -> Sketch061
  Tapered = false
  TaperedAngle = 90
  ThreadClass = 0
  ThreadDepth = 15
  ThreadDepthType = 0
  ThreadDirection = 0
  ThreadFit = 0
  ThreadSize = 9
  ThreadType = 1
  Threaded = true
  UseCustomThreadClearance = false
FEATURE [PartDesign::Hole] Hole025  label="Hole RearFitting"
  BaseFeature = -> Hole023
  CustomThreadClearance = 0
  Depth = 16
  DepthType = 0
  Diameter = 2.5
  DrillForDepth = false
  DrillPoint = 1
  DrillPointAngle = 118
  HoleCutCountersinkAngle = 90
  HoleCutCustomValues = false
  HoleCutDepth = 0
  HoleCutDiameter = 6.1
  HoleCutType = 0
  ModelThread = false
  Profile = -> Sketch062
  Reversed = true
  Tapered = false
  TaperedAngle = 90
  ThreadClass = 0
  ThreadDepth = 16
  ThreadDepthType = 0
  ThreadDirection = 0
  ThreadFit = 0
  ThreadSize = 9
  ThreadType = 1
  Threaded = true
  UseCustomThreadClearance = false
FEATURE [PartDesign::Hole] Hole022  label="Hole Foot"
  BaseFeature = -> Hole025
  CustomThreadClearance = 0
  Depth = 25
  DepthType = 0
  Diameter = 4.2
  DrillForDepth = false
  DrillPoint = 1
  DrillPointAngle = 118
  HoleCutCountersinkAngle = 90
  HoleCutCustomValues = false
  HoleCutDepth = 0
  HoleCutDiameter = 6.1
  HoleCutType = 0
  ModelThread = false
  Profile = -> Sketch060
  Reversed = true
  Tapered = false
  TaperedAngle = 90
  ThreadClass = 0
  ThreadDepth = 25
  ThreadDepthType = 0
  ThreadDirection = 0
  ThreadFit = 0
  ThreadSize = 13
  ThreadType = 1
  Threaded = true
  UseCustomThreadClearance = false
FEATURE [PartDesign::Hole] Hole026  label="Hole Skirt"
  BaseFeature = -> Hole022
  CustomThreadClearance = 0
  Depth = 16
  DepthType = 0
  Diameter = 2.5
  DrillForDepth = false
  DrillPoint = 1
  DrillPointAngle = 118
  HoleCutCountersinkAngle = 90
  HoleCutCustomValues = false
  HoleCutDepth = 0
  HoleCutDiameter = 6.1
  HoleCutType = 0
  ModelThread = false
  Profile = -> Sketch066
  Reversed = true
  Tapered = false
  TaperedAngle = 90
  ThreadClass = 0
  ThreadDepth = 16
  ThreadDepthType = 0
  ThreadDirection = 0
  ThreadFit = 0
  ThreadSize = 9
  ThreadType = 1
  Threaded = true
  UseCustomThreadClearance = false
FEATURE [Sketcher::SketchObject] Sketch068
  FullyConstrained = true
  MapMode = 5
  Placement = pos=(0,0,0) rot=(0.57735,0.57735,0.57735;2.0944rad)
  Support = -> [YZ_Plane016]
  sketch-geometry (8):
    g0: LineSegment StartX=-82.5 StartY=10 StartZ=0 EndX=-75.5718 EndY=14 EndZ=0
    g1: LineSegment StartX=-75.5718 StartY=14 StartZ=0 EndX=-49.4282 EndY=14 EndZ=0
    g2: LineSegment StartX=-49.4282 StartY=14 StartZ=0 EndX=-42.5 EndY=10 EndZ=0
    g3: LineSegment StartX=-42.5 StartY=10 StartZ=0 EndX=-82.5 EndY=10 EndZ=0
    g4: LineSegment StartX=42.5 StartY=10 StartZ=0 EndX=49.4282 EndY=14 EndZ=0
    g5: LineSegment StartX=49.4282 StartY=14 StartZ=0 EndX=75.5718 EndY=14 EndZ=0
    g6: LineSegment StartX=75.5718 StartY=14 StartZ=0 EndX=82.5 EndY=10 EndZ=0
    g7: LineSegment StartX=82.5 StartY=10 StartZ=0 EndX=42.5 EndY=10 EndZ=0
  constraints (20):
    c: Coincident(g0,g1)
    c: Horizontal(g1)
    c: Coincident(g1,g2)
    c: Coincident(g2,g3)
    c: Coincident(g3,g0)
    c: Horizontal(g3)
    c: Coincident(g4,g5)
    c: Coincident(g5,g6)
    c: Coincident(g6,g7)
    c: Coincident(g7,g4)
    c: Symmetric(g2,g4,g-2)
    c: Symmetric(g1,g4,g-2)
    c: Symmetric(g0,g6,g-2)
    c: Symmetric(g0,g5,g-2)
    c: DistanceX(g3,g3) = 40
    c: Angle(g2,g3) = 0.523599
    c: Equal(g2,g0)
    c: DistanceY(g2) = 10
    c: DistanceY(g0) = 14
    c: DistanceX(g2,g4) = 85
FEATURE [PartDesign::Pad] Pad016  label="Pad LashingBeltCover"
  BaseFeature = -> Hole026
  Direction = (1,-2e-16,3e-16)
  Length = 50
  Length2 = 10
  Profile = -> Sketch068
  ReferenceAxis = -> Sketch068 [N_Axis]
  Type = 0
FEATURE [PartDesign::Pocket] Pocket017  label="Pocket LashingBelt"
  BaseFeature = -> Pad016
  Direction = (-1,2e-16,-3e-16)
  Length = 5
  Length2 = 5
  Midplane = true
  Profile = -> Sketch047
  ReferenceAxis = -> Sketch047 [N_Axis]
  Type = 1
FEATURE [PartDesign::Boolean] Boolean
  BaseFeature = -> Pocket017
  Group = -> [Clone028,Clone029,Clone,Clone001,Clone002,Clone003,Clone004,Clone005,Clone006,Clone007,Clone008,Clone009,Clone025,Clone031,Clone010,Clone011,Clone012,Clone013,Clone014,Clone015,Clone016,Clone017,Clone019,Clone020,Clone030,Clone018,Clone032,Clone024,Clone021,Clone022,Clone023,Clone033,Clone026,Clone034,Clone027,Clone035,Clone036,Clone037,Clone038,Clone039,Clone040,Clone041,Clone042,Clone043,+1 more]
  Refine = true
  Type = 1
FEATURE [PartDesign::Body] Body007  label="LeftPanelPlate"
  Group = -> [Pad013,Pocket018,Pocket019,Pocket002,Pocket014,Pocket016,Pad014,Pocket021,Pocket020,Pocket015,Pocket022,Hole017,Hole019,Hole018,Hole020,Hole021,Hole023,Hole025,Hole022,Hole026,Pad016,Pocket017,Sketch021,Sketch043,Sketch044,Sketch045,Sketch046,Sketch047,Sketch049,Sketch050,Sketch051,Sketch052,Sketch053,Sketch055,Sketch056,Sketch058,Sketch059,Sketch060,Sketch061,Sketch062,Boolean,Sketch066,+2 more]
  Origin = -> Origin016
  Tip = -> Boolean
FEATURE [Sketcher::SketchObject] Sketch069
  FullyConstrained = true
  MapMode = 5
  Placement = pos=(0,0,0) rot=(1,0,0;1.5708rad)
  Support = -> [XZ_Plane015]
  sketch-geometry (13):
    g0: LineSegment StartX=-210 StartY=40 StartZ=0 EndX=-200 EndY=40 EndZ=0
    g1: LineSegment StartX=0 StartY=-0.2 StartZ=0 EndX=-210 EndY=-0.2 EndZ=0
    g2: LineSegment StartX=-210 StartY=-0.2 StartZ=0 EndX=-210 EndY=40 EndZ=0
    g3: LineSegment StartX=-200 StartY=40 StartZ=0 EndX=-171.757 EndY=11.7574 EndZ=0
    g4: LineSegment StartX=-167.515 StartY=10 StartZ=0 EndX=-190 EndY=10 EndZ=0
    g5: LineSegment StartX=-190 StartY=10 StartZ=0 EndX=-190 EndY=5 EndZ=0
    g6: LineSegment StartX=-190 StartY=5 StartZ=0 EndX=-185 EndY=0 EndZ=0
    g7: ArcOfCircle CenterX=-167.515 CenterY=16 CenterZ=0 NormalX=0 NormalY=0 NormalZ=1 AngleXU=0 Radius=6 StartAngle=3.92699 EndAngle=4.71239
    g8: LineSegment StartX=0 StartY=-0.2 StartZ=0 EndX=0 EndY=10 EndZ=0
    g9: LineSegment StartX=0 StartY=10 StartZ=0 EndX=-10 EndY=10 EndZ=0
    g10: LineSegment StartX=-10 StartY=10 StartZ=0 EndX=-10 EndY=8 EndZ=0
    g11: LineSegment StartX=-18 StartY=0 StartZ=0 EndX=-10 EndY=8 EndZ=0
    g12: LineSegment StartX=-18 StartY=0 StartZ=0 EndX=-185 EndY=0 EndZ=0
  constraints (38):
    c: Coincident(g0,g3)
    c: Horizontal(g1)
    c: Coincident(g2,g0)
    c: Horizontal(g0)
    c: Vertical(g2)
    c: DistanceY(g0) = 40
    c: Coincident(g2,g1)
    c: PointOnObject(g6,g-1)
    c: DistanceX(g0,g0) = 10
    c: DistanceX(g1) = -210
    c: Coincident(g4,g5)
    c: Coincident(g5,g6)
    c: Horizontal(g4)
    c: Vertical(g5)
    c: Angle(g3) = -0.785398
    c: Parallel(g3,g6)
    c: DistanceY(g4) = 10
    c: DistanceY(g5) = 5
    c: DistanceX(g1,g4) = 20
    c: Tangent(g7,g3) = -1.5708
    c: Tangent(g7,g4) = 1.5708
    c: Diameter(g7) = 12
    c: DistanceY(g1) = -0.2
    c: Coincident(g8,g9)
    c: Horizontal(g9)
    c: Coincident(g9,g10)
    c: Vertical(g10)
    c: Coincident(g8,g1)
    c: PointOnObject(g1,g-2)
    c: PointOnObject(g8,g-2)
    c: Coincident(g12,g6)
    c: Horizontal(g12)
    c: Angle(g11) = 0.785398
    c: Coincident(g11,g12)
    c: Coincident(g11,g10)
    c: DistanceY(g10) = 8
    c: DistanceY(g8) = 10
    c: DistanceX(g9) = -10
FEATURE [PartDesign::Body] Body016  label="PanelFitting"
  Group = -> [Sketch048]
  Origin = -> Origin030
FEATURE [Sketcher::SketchObject] Sketch071  label="Sketch LinearGuideHoles"
  FullyConstrained = true
  MapMode = 5
  Support = -> [XY_Plane032]
  sketch-geometry (9):
    g0: Circle CenterX=0 CenterY=0 CenterZ=0 NormalX=0 NormalY=0 NormalZ=1 AngleXU=0 Radius=1.25
    g1: Circle CenterX=0 CenterY=20 CenterZ=0 NormalX=0 NormalY=0 NormalZ=1 AngleXU=0 Radius=1.25
    g2: Circle CenterX=0 CenterY=-20 CenterZ=0 NormalX=0 NormalY=0 NormalZ=1 AngleXU=0 Radius=1.25
    g3: Circle CenterX=0 CenterY=40 CenterZ=0 NormalX=0 NormalY=0 NormalZ=1 AngleXU=0 Radius=1.25
    g4: Circle CenterX=0 CenterY=-40 CenterZ=0 NormalX=0 NormalY=0 NormalZ=1 AngleXU=0 Radius=1.25
    g5: Circle CenterX=0 CenterY=60 CenterZ=0 NormalX=0 NormalY=0 NormalZ=1 AngleXU=0 Radius=1.25
    g6: Circle CenterX=0 CenterY=-60 CenterZ=0 NormalX=0 NormalY=0 NormalZ=1 AngleXU=0 Radius=1.25
    g7: Circle CenterX=0 CenterY=80 CenterZ=0 NormalX=0 NormalY=0 NormalZ=1 AngleXU=0 Radius=1.25
    g8: Circle CenterX=0 CenterY=-80 CenterZ=0 NormalX=0 NormalY=0 NormalZ=1 AngleXU=0 Radius=1.25
  constraints (22):
    c: Coincident(g0,g-1)
    c: PointOnObject(g1,g-2)
    c: PointOnObject(g3,g-2)
    c: PointOnObject(g5,g-2)
    c: PointOnObject(g7,g-2)
    c: Symmetric(g1,g2,g-1)
    c: Symmetric(g3,g4,g-1)
    c: Symmetric(g5,g6,g-1)
    c: Symmetric(g7,g8,g-1)
    c: Diameter(g0) = 2.5
    c: Equal(g0,g1)
    c: Equal(g1,g2)
    c: Equal(g2,g3)
    c: Equal(g3,g4)
    c: Equal(g4,g5)
    c: Equal(g5,g6)
    c: Equal(g6,g7)
    c: Equal(g7,g8)
    c: DistanceY(g1) = 20
    c: DistanceY(g3) = 40
    c: DistanceY(g5) = 60
    c: DistanceY(g7) = 80
FEATURE [PartDesign::Body] Body017  label="LinearGuideHoles"
  Group = -> [Sketch071]
  Origin = -> Origin032
FEATURE [App::Part] Part013  label="Fittings"
  Group = -> [Body016,Body017]
  Origin = -> Origin031
FEATURE [Sketcher::SketchObject] Sketch072
  FullyConstrained = true
  MapMode = 5
  Support = -> [XY_Plane015]
  sketch-geometry (6):
    g0: LineSegment StartX=-188.5 StartY=-9.5 StartZ=0 EndX=-11.5 EndY=-9.5 EndZ=0
    g1: LineSegment StartX=-11.5 StartY=-9.5 StartZ=0 EndX=-11.5 EndY=-20.5 EndZ=0
    g2: LineSegment StartX=-11.5 StartY=-20.5 StartZ=0 EndX=-188.5 EndY=-20.5 EndZ=0
    g3: LineSegment StartX=-188.5 StartY=-20.5 StartZ=0 EndX=-188.5 EndY=-9.5 EndZ=0
    g4: GeomPoint X=-100 Y=-15 Z=0
    g5: LineSegment StartX=0 StartY=-15 StartZ=0 EndX=-250 EndY=-15 EndZ=0
  constraints (15):
    c: Coincident(g0,g1)
    c: Coincident(g1,g2)
    c: Coincident(g2,g3)
    c: Coincident(g3,g0)
    c: Horizontal(g0)
    c: DistanceX(g0,g0) = 177
    c: DistanceY(g3,g3) = 11
    c: Symmetric(g0,g1,g4)
    c: DistanceX(g4) = -100
    c: PointOnObject(g5,g-2)
    c: Horizontal(g5)
    c: DistanceX(g5) = -250
    c: DistanceY(g5) = -15
    c: Symmetric(g0,g1,g5)
    c: Symmetric(g0,g2,g5)
FEATURE [Sketcher::SketchObject] Sketch073
  FullyConstrained = false
  MapMode = 5
  Placement = pos=(0,0,0) rot=(0.57735,0.57735,0.57735;2.0944rad)
  Support = -> [YZ_Plane033]
  sketch-geometry (103):
    g0: Circle CenterX=0.0699947 CenterY=0.068893 CenterZ=0 NormalX=0 NormalY=0 NormalZ=1 AngleXU=0 Radius=131.534
    g1: LineSegment StartX=-1.42e-14 StartY=131.603 StartZ=0 EndX=-56.9383 EndY=98.6889 EndZ=0
    g2: LineSegment StartX=-56.9383 StartY=98.6889 StartZ=0 EndX=-113.877 EndY=65.7751 EndZ=0
    g3: LineSegment StartX=-113.877 StartY=65.7751 StartZ=0 EndX=-113.842 EndY=0.00827587 EndZ=0
    g4: LineSegment StartX=-113.842 StartY=0.00827587 StartZ=0 EndX=-113.807 EndY=-65.7586 EndZ=0
    g5: LineSegment StartX=-113.807 StartY=-65.7586 StartZ=0 EndX=-56.8333 EndY=-98.6117 EndZ=0
    g6: LineSegment StartX=-56.8333 StartY=-98.6117 StartZ=0 EndX=0.139989 EndY=-131.465 EndZ=0
    g7: LineSegment StartX=0.139989 StartY=-131.465 StartZ=0 EndX=57.0783 EndY=-98.5511 EndZ=0
    g8: LineSegment StartX=57.0783 StartY=-98.5511 StartZ=0 EndX=114.017 EndY=-65.6374 EndZ=0
    g9: LineSegment StartX=114.017 StartY=-65.6374 StartZ=0 EndX=113.982 EndY=0.12951 EndZ=0
    g10: LineSegment StartX=113.982 StartY=0.12951 StartZ=0 EndX=113.947 EndY=65.8964 EndZ=0
    g11: LineSegment StartX=113.947 StartY=65.8964 StartZ=0 EndX=56.9733 EndY=98.7495 EndZ=0
    g12: LineSegment StartX=56.9733 StartY=98.7495 StartZ=0 EndX=-1.42e-14 EndY=131.603 EndZ=0
    g13: LineSegment StartX=-56.9383 StartY=98.6889 StartZ=0 EndX=57.0783 EndY=-98.5511 EndZ=0
    g14: LineSegment StartX=-113.842 StartY=0.00827587 StartZ=0 EndX=113.982 EndY=0.12951 EndZ=0
    g15: LineSegment StartX=-56.8333 StartY=-98.6117 StartZ=0 EndX=56.9733 EndY=98.7495 EndZ=0
    g16: LineSegment StartX=-1.42e-14 StartY=131.603 StartZ=0 EndX=0.139989 EndY=-131.465 EndZ=0
    g17: LineSegment StartX=-113.877 StartY=65.7751 StartZ=0 EndX=114.017 EndY=-65.6374 EndZ=0
    g18: LineSegment StartX=-113.807 StartY=-65.7586 StartZ=0 EndX=113.947 EndY=65.8964 EndZ=0
    g19: LineSegment StartX=-113.877 StartY=65.7751 StartZ=0 EndX=113.947 EndY=65.8964 EndZ=0
    g20: LineSegment StartX=-113.807 StartY=-65.7586 StartZ=0 EndX=114.017 EndY=-65.6374 EndZ=0
    g21: LineSegment StartX=-113.807 StartY=-65.7586 StartZ=0 EndX=-1.42e-14 EndY=131.603 EndZ=0
    g22: LineSegment StartX=113.947 StartY=65.8964 StartZ=0 EndX=0.139989 EndY=-131.465 EndZ=0
    g23: LineSegment StartX=114.017 StartY=-65.6374 StartZ=0 EndX=-1.42e-14 EndY=131.603 EndZ=0
    g24: LineSegment StartX=-113.877 StartY=65.7751 StartZ=0 EndX=0.139989 EndY=-131.465 EndZ=0
    g25: Circle CenterX=0 CenterY=0 CenterZ=0 NormalX=0 NormalY=0 NormalZ=1 AngleXU=0 Radius=91.7169
    g26: LineSegment StartX=-3.02004 StartY=169.257 StartZ=0 EndX=-2.94564 EndY=29.4449 EndZ=0
    g27: LineSegment StartX=2.97996 StartY=169.26 StartZ=0 EndX=3 EndY=29.4449 EndZ=0
    g28: LineSegment StartX=-131.819 StartY=72.6586 StartZ=0 EndX=-26.9591 EndY=12.1919 EndZ=0
    g29: LineSegment StartX=-128.822 StartY=77.8563 StartZ=0 EndX=-24 EndY=17.3205 EndZ=0
    g30: LineSegment StartX=-131.789 StartY=-72.6881 StartZ=0 EndX=-27.0053 EndY=-11.895 EndZ=0
    g31: LineSegment StartX=-128.786 StartY=-77.8827 StartZ=0 EndX=-24.0138 EndY=-17.3182 EndZ=0
    g32: LineSegment StartX=-144.527 StartY=51.5227 StartZ=0 EndX=25.8767 EndY=150.026 EndZ=0
    g33: LineSegment StartX=-141.524 StartY=46.3281 StartZ=0 EndX=28.8795 EndY=144.832 EndZ=0
    g34: LineSegment StartX=-116.895 StartY=101.077 StartZ=0 EndX=-116.789 EndY=-98.565 EndZ=0
    g35: LineSegment StartX=-110.895 StartY=101.08 StartZ=0 EndX=-110.789 EndY=-98.5619 EndZ=0
    g36: LineSegment StartX=-153.169 StartY=-46.5239 StartZ=0 EndX=54.8796 EndY=-166.493 EndZ=0
    g37: LineSegment StartX=-150.171 StartY=-41.3262 StartZ=0 EndX=57.8768 EndY=-161.295 EndZ=0
    g38: LineSegment StartX=-64.6212 StartY=-149.593 StartZ=0 EndX=155.377 EndY=-36.4206 EndZ=0
    g39: LineSegment StartX=-42.9386 StartY=-161.227 StartZ=0 EndX=155.377 EndY=-66.5646 EndZ=0
    g40: LineSegment StartX=109.368 StartY=-110.987 StartZ=0 EndX=96.6757 EndY=111.126 EndZ=0
    g41: LineSegment StartX=132.108 StartY=-100.939 StartZ=0 EndX=121.531 EndY=104.251 EndZ=0
    g42: LineSegment StartX=140.57 StartY=49.2519 StartZ=0 EndX=-27.0734 EndY=148.145 EndZ=0
    g43: LineSegment StartX=142.156 StartY=64.5883 StartZ=0 EndX=-16.4965 EndY=158.193 EndZ=0
    g44: LineSegment StartX=-86.8849 StartY=81.378 StartZ=0 EndX=-113.893 EndY=96.9521 EndZ=0
    g45: LineSegment StartX=-113.893 StartY=96.9521 StartZ=0 EndX=-140.885 EndY=81.3492 EndZ=0
    g46: LineSegment StartX=-140.885 StartY=81.3492 StartZ=0 EndX=-140.868 EndY=50.1723 EndZ=0
    g47: LineSegment StartX=-140.868 StartY=50.1723 StartZ=0 EndX=-113.86 EndY=34.5982 EndZ=0
    g48: LineSegment StartX=-113.86 StartY=34.5982 StartZ=0 EndX=-86.8683 EndY=50.2011 EndZ=0
    g49: LineSegment StartX=-86.8683 StartY=50.2011 StartZ=0 EndX=-86.8849 EndY=81.378 EndZ=0
    g50: Circle CenterX=-113.877 CenterY=65.7751 CenterZ=0 NormalX=0 NormalY=0 NormalZ=1 AngleXU=0 Radius=31.1769
    g51: LineSegment StartX=-95.8821 StartY=76.177 StartZ=0 EndX=-113.888 EndY=86.5597 EndZ=0
    g52: LineSegment StartX=-113.888 StartY=86.5597 StartZ=0 EndX=-131.882 EndY=76.1579 EndZ=0
    g53: LineSegment StartX=-131.882 StartY=76.1579 StartZ=0 EndX=-131.871 EndY=55.3733 EndZ=0
    g54: LineSegment StartX=-131.871 StartY=55.3733 StartZ=0 EndX=-113.865 EndY=44.9905 EndZ=0
    g55: LineSegment StartX=-113.865 StartY=44.9905 StartZ=0 EndX=-95.871 EndY=55.3924 EndZ=0
    g56: LineSegment StartX=-95.871 StartY=55.3924 StartZ=0 EndX=-95.8821 EndY=76.177 EndZ=0
    g57: Circle CenterX=-113.877 CenterY=65.7751 CenterZ=0 NormalX=0 NormalY=0 NormalZ=1 AngleXU=0 Radius=20.7846
    g58: LineSegment StartX=24 StartY=17.3205 StartZ=0 EndX=128.922 EndY=78.0193 EndZ=0
    g59: LineSegment StartX=-3 StartY=-29.4449 StartZ=0 EndX=-2.83152 EndY=-164.149 EndZ=0
    g60: LineSegment StartX=3 StartY=-29.4449 StartZ=0 EndX=3.14628 EndY=-164.146 EndZ=0
    g61: LineSegment StartX=27 StartY=-12.1244 StartZ=0 EndX=140.074 EndY=-77.1955 EndZ=0
    g62: LineSegment StartX=24 StartY=-17.3205 StartZ=0 EndX=137.073 EndY=-82.4005 EndZ=0
    g63: LineSegment StartX=27 StartY=12.1244 StartZ=0 EndX=131.925 EndY=72.8228 EndZ=0
    g64: LineSegment StartX=-4.94815 StartY=18.3688 StartZ=0 EndX=-13.2924 EndY=13.5416 EndZ=0
    g65: LineSegment StartX=-18.2955 StartY=4.84125 StartZ=0 EndX=-18.2705 EndY=-4.79865 EndZ=0
    g66: LineSegment StartX=-13.2223 StartY=-13.4729 StartZ=0 EndX=-4.85316 EndY=-18.2568 EndZ=0
    g67: LineSegment StartX=4.99315 StartY=-18.2568 StartZ=0 EndX=13.3623 EndY=-13.4729 EndZ=0
    g68: LineSegment StartX=18.4105 StartY=-4.79865 StartZ=0 EndX=18.4355 EndY=4.84125 EndZ=0
    g69: LineSegment StartX=13.4324 StartY=13.5416 StartZ=0 EndX=5.08814 EndY=18.3688 EndZ=0
    g70: Circle CenterX=0.0699947 CenterY=0.068893 CenterZ=0 NormalX=0 NormalY=0 NormalZ=1 AngleXU=0 Radius=18.9754
    g71: LineSegment StartX=-4.94815 StartY=18.3688 StartZ=0 EndX=5.08814 EndY=18.3688 EndZ=0
    g72: LineSegment StartX=13.4324 StartY=13.5416 StartZ=0 EndX=18.4355 EndY=4.84125 EndZ=0
    g73: LineSegment StartX=18.4105 StartY=-4.79865 StartZ=0 EndX=13.3623 EndY=-13.4729 EndZ=0
    g74: LineSegment StartX=4.99315 StartY=-18.2568 StartZ=0 EndX=-5.04303 EndY=-18.2117 EndZ=0
    g75: LineSegment StartX=-13.2223 StartY=-13.4729 StartZ=0 EndX=-18.2705 EndY=-4.79865 EndZ=0
    g76: LineSegment StartX=-18.2955 StartY=4.84125 StartZ=0 EndX=-13.2924 EndY=13.5416 EndZ=0
    g77: LineSegment StartX=-6.47535 StartY=24.9585 StartZ=0 EndX=-18.0433 EndY=18.3513 EndZ=0
    g78: LineSegment StartX=-24.7577 StartY=6.84527 StartZ=0 EndX=-24.8196 EndY=-6.47645 EndZ=0
    g79: LineSegment StartX=-18.2124 StartY=-18.0444 StartZ=0 EndX=-6.70638 EndY=-24.7588 EndZ=0
    g80: LineSegment StartX=6.61534 StartY=-24.8207 StartZ=0 EndX=18.1832 EndY=-18.2135 EndZ=0
    g81: LineSegment StartX=24.8977 StartY=-6.70748 StartZ=0 EndX=24.9596 EndY=6.61424 EndZ=0
    g82: LineSegment StartX=18.3524 StartY=18.1821 StartZ=0 EndX=6.84637 EndY=24.8966 EndZ=0
    g83: Circle CenterX=0.0699947 CenterY=0.068893 CenterZ=0 NormalX=0 NormalY=0 NormalZ=1 AngleXU=0 Radius=25.7359
    g84: LineSegment StartX=5.05199 StartY=8.69797 StartZ=0 EndX=-4.912 EndY=8.69797 EndZ=0
    g85: LineSegment StartX=-4.912 StartY=8.69797 StartZ=0 EndX=-9.894 EndY=0.068893 EndZ=0
    g86: LineSegment StartX=-9.894 StartY=0.068893 StartZ=0 EndX=-4.912 EndY=-8.56018 EndZ=0
    g87: LineSegment StartX=-4.912 StartY=-8.56018 StartZ=0 EndX=5.05199 EndY=-8.56018 EndZ=0
    g88: LineSegment StartX=5.05199 StartY=-8.56018 StartZ=0 EndX=10.034 EndY=0.068893 EndZ=0
    g89: LineSegment StartX=10.034 StartY=0.068893 StartZ=0 EndX=5.05199 EndY=8.69797 EndZ=0
    g90: Circle CenterX=0.0699947 CenterY=0.068893 CenterZ=0 NormalX=0 NormalY=0 NormalZ=1 AngleXU=0 Radius=9.964
    g91: LineSegment StartX=-13.2924 StartY=13.5416 StartZ=0 EndX=-4.912 EndY=8.69797 EndZ=0
    g92: LineSegment StartX=-4.94815 StartY=18.3688 StartZ=0 EndX=-4.912 EndY=8.69797 EndZ=0
    g93: LineSegment StartX=5.08814 StartY=18.3688 StartZ=0 EndX=5.05199 EndY=8.69797 EndZ=0
    g94: LineSegment StartX=13.4324 StartY=13.5416 StartZ=0 EndX=5.05199 EndY=8.69797 EndZ=0
    g95: LineSegment StartX=18.4355 StartY=4.84125 StartZ=0 EndX=10.034 EndY=0.068893 EndZ=0
    g96: LineSegment StartX=18.4105 StartY=-4.79865 StartZ=0 EndX=10.034 EndY=0.068893 EndZ=0
    g97: LineSegment StartX=13.3623 StartY=-13.4729 StartZ=0 EndX=5.05199 EndY=-8.56018 EndZ=0
    g98: LineSegment StartX=4.99315 StartY=-18.2568 StartZ=0 EndX=5.05199 EndY=-8.56018 EndZ=0
    g99: LineSegment StartX=-4.85316 StartY=-18.2568 StartZ=0 EndX=-4.912 EndY=-8.56018 EndZ=0
    g100: LineSegment StartX=-13.2223 StartY=-13.4729 StartZ=0 EndX=-4.912 EndY=-8.56018 EndZ=0
    g101: LineSegment StartX=-18.2705 StartY=-4.79865 StartZ=0 EndX=-9.894 EndY=0.068893 EndZ=0
    g102: LineSegment StartX=-18.2955 StartY=4.84125 StartZ=0 EndX=-9.894 EndY=0.068893 EndZ=0
  constraints (199):
    c: Coincident(g2,g3)
    c: Coincident(g4,g5)
    c: Coincident(g6,g7)
    c: Coincident(g8,g9)
    c: Coincident(g10,g11)
    c: Coincident(g12,g1)
    c: PointOnObject(g2,g0)
    c: PointOnObject(g4,g0)
    c: PointOnObject(g6,g0)
    c: PointOnObject(g8,g0)
    c: PointOnObject(g10,g0)
    c: PointOnObject(g12,g0)
    c: PointOnObject(g12,g-2)
    c: Coincident(g1,g2)
    c: Coincident(g3,g4)
    c: Coincident(g5,g6)
    c: Coincident(g7,g8)
    c: Coincident(g9,g10)
    c: Coincident(g11,g12)
    c: Parallel(g2,g1)
    c: Parallel(g3,g4)
    c: Parallel(g5,g6)
    c: Parallel(g7,g8)
    c: Parallel(g9,g10)
    c: Parallel(g11,g12)
    c: Equal(g1,g2)
    c: Equal(g2,g3)
    c: Equal(g3,g4)
    c: Equal(g4,g5)
    c: Equal(g5,g6)
    c: Equal(g6,g7)
    c: Equal(g7,g8)
    c: Equal(g8,g9)
    c: Equal(g9,g10)
    c: Equal(g10,g11)
    c: Equal(g11,g12)
    c: Coincident(g13,g1)
    c: Coincident(g13,g7)
    c: Coincident(g14,g3)
    c: Coincident(g14,g9)
    c: Coincident(g15,g5)
    c: Coincident(g15,g11)
    c: Coincident(g16,g1)
    c: Coincident(g16,g6)
    c: Coincident(g17,g2)
    c: Coincident(g17,g8)
    c: Coincident(g18,g4)
    c: Coincident(g18,g10)
    c: Coincident(g19,g2)
    c: Coincident(g19,g10)
    c: Coincident(g20,g4)
    c: Coincident(g20,g8)
    c: Coincident(g21,g4)
    c: Coincident(g22,g10)
    c: Coincident(g23,g8)
    c: Coincident(g24,g2)
    c: Coincident(g21,g1)
    c: Coincident(g23,g1)
    c: Coincident(g24,g6)
    c: Coincident(g22,g6)
    c: Symmetric(g59,g60,g16)
    c: Symmetric(g26,g27,g16)
    c: Distance(g26,g27) = 6
    c: Parallel(g26,g16)
    c: Symmetric(g28,g29,g17)
    c: Symmetric(g62,g61,g17)
    c: Parallel(g28,g17)
    c: Distance(g28,g29) = 6
    c: Symmetric(g31,g30,g18)
    c: Symmetric(g58,g63,g18)
    c: Parallel(g31,g18)
    c: Distance(g31,g30) = 6
    c: Symmetric(g32,g33,g2)
    c: Symmetric(g32,g33,g1)
    c: Parallel(g33,g2)
    c: Distance(g32,g33) = 6
    c: Symmetric(g34,g35,g3)
    c: Symmetric(g34,g35,g4)
    c: Parallel(g34,g3)
    c: Distance(g34,g35) = 6
    c: Symmetric(g36,g37,g5)
    c: Symmetric(g36,g37,g6)
    c: Parallel(g37,g5)
    c: Distance(g36,g37) = 6
    c: Coincident(g44,g45)
    c: Coincident(g45,g46)
    c: Coincident(g46,g47)
    c: Coincident(g47,g48)
    c: Coincident(g48,g49)
    c: Coincident(g49,g44)
    c: Equal(g44, g45-g49) x5
    c: PointOnObject(g44,g50)
    c: PointOnObject(g45,g50)
    c: PointOnObject(g46,g50)
    c: PointOnObject(g47,g50)
    c: PointOnObject(g48,g50)
    c: PointOnObject(g49,g50)
    c: Coincident(g50,g2)
    c: PointOnObject(g49,g2)
    c: Coincident(g51,g52)
    c: Coincident(g52,g53)
    c: Coincident(g53,g54)
    c: Coincident(g54,g55)
    c: Coincident(g55,g56)
    c: Coincident(g56,g51)
    c: Equal(g51, g52-g56) x5
    c: PointOnObject(g51,g57)
    c: PointOnObject(g52,g57)
    c: PointOnObject(g53,g57)
    c: PointOnObject(g54,g57)
    c: PointOnObject(g55,g57)
    c: PointOnObject(g56,g57)
    c: Coincident(g57,g2)
    c: PointOnObject(g56,g2)
    c: Distance(g51,g45) = 9
    c: Distance(g2,g53) = 18
    c: PointOnObject(g64,g70)
    c: PointOnObject(g64,g70)
    c: PointOnObject(g65,g70)
    c: PointOnObject(g65,g70)
    c: PointOnObject(g66,g70)
    c: PointOnObject(g66,g70)
    c: PointOnObject(g67,g70)
    c: PointOnObject(g67,g70)
    c: PointOnObject(g68,g70)
    c: PointOnObject(g68,g70)
    c: PointOnObject(g69,g70)
    c: PointOnObject(g69,g70)
    c: Coincident(g70,g0)
    c: Coincident(g71,g64)
    c: Coincident(g71,g69)
    c: Horizontal(g71)
    c: Coincident(g72,g69)
    c: Coincident(g72,g68)
    c: Coincident(g73,g68)
    c: Coincident(g73,g67)
    c: Coincident(g74,g67)
    c: Coincident(g75,g66)
    c: Coincident(g75,g65)
    c: Coincident(g76,g65)
    c: Coincident(g76,g64)
    c: Equal(g64,g69)
    c: Equal(g69,g68)
    c: Equal(g68,g67)
    c: Equal(g67,g66)
    c: Equal(g66,g65)
    c: Equal(g71,g72)
    c: Equal(g72,g73)
    c: Equal(g73,g74)
    c: Equal(g74,g75)
    c: Equal(g75,g76)
    c: PointOnObject(g77,g83)
    c: PointOnObject(g77,g83)
    c: PointOnObject(g78,g83)
    c: PointOnObject(g78,g83)
    c: PointOnObject(g79,g83)
    c: PointOnObject(g79,g83)
    c: PointOnObject(g80,g83)
    c: PointOnObject(g80,g83)
    c: PointOnObject(g81,g83)
    c: PointOnObject(g81,g83)
    c: PointOnObject(g82,g83)
    c: PointOnObject(g82,g83)
    c: Coincident(g83,g0)
    c: Coincident(g84,g85)
    c: Coincident(g85,g86)
    c: Coincident(g86,g87)
    c: Coincident(g87,g88)
    c: Coincident(g88,g89)
    c: Coincident(g89,g84)
    c: Equal(g84, g85-g89) x5
    c: PointOnObject(g84,g90)
    c: PointOnObject(g85,g90)
    c: PointOnObject(g86,g90)
    c: PointOnObject(g87,g90)
    c: PointOnObject(g88,g90)
    c: PointOnObject(g89,g90)
    c: Coincident(g90,g0)
    c: Horizontal(g84)
    c: Coincident(g91,g64)
    c: Coincident(g91,g84)
    c: Coincident(g92,g64)
    c: Coincident(g93,g69)
    c: Coincident(g94,g69)
    c: Coincident(g94,g93)
    c: Coincident(g95,g68)
    c: Coincident(g95,g88)
    c: Coincident(g96,g68)
    c: Coincident(g96,g95)
    c: Coincident(g97,g67)
    c: Coincident(g97,g87)
    c: Coincident(g98,g67)
    c: Coincident(g99,g66)
    c: Coincident(g100,g66)
    c: Coincident(g100,g99)
    c: Coincident(g101,g65)
    c: Coincident(g101,g85)
    c: Coincident(g102,g65)
    c: Coincident(g102,g101)
FEATURE [Sketcher::SketchObject] Sketch074
  FullyConstrained = false
  MapMode = 5
  Placement = pos=(0,0,0) rot=(0.57735,0.57735,0.57735;2.0944rad)
  Support = -> [YZ_Plane033]
  sketch-geometry (389):
    g0: LineSegment StartX=3 StartY=5.19615 StartZ=0 EndX=-3 EndY=5.19615 EndZ=0
    g1: LineSegment StartX=-3 StartY=5.19615 StartZ=0 EndX=-6 EndY=0 EndZ=0
    g2: LineSegment StartX=-6 StartY=0 StartZ=0 EndX=-3 EndY=-5.19615 EndZ=0
    g3: LineSegment StartX=-3 StartY=-5.19615 StartZ=0 EndX=3 EndY=-5.19615 EndZ=0
    g4: LineSegment StartX=3 StartY=-5.19615 StartZ=0 EndX=6 EndY=0 EndZ=0
    g5: LineSegment StartX=6 StartY=0 StartZ=0 EndX=3 EndY=5.19615 EndZ=0
    g6: Circle CenterX=0 CenterY=0 CenterZ=0 NormalX=0 NormalY=0 NormalZ=1 AngleXU=0 Radius=6
    g7: LineSegment StartX=3 StartY=37.6572 StartZ=0 EndX=-3 EndY=37.6572 EndZ=0
    g8: LineSegment StartX=-3 StartY=37.6572 StartZ=0 EndX=-31.1121 EndY=21.4267 EndZ=0
    g9: LineSegment StartX=-31.1121 StartY=21.4267 StartZ=0 EndX=-34.1121 EndY=16.2305 EndZ=0
    g10: LineSegment StartX=-34.1121 StartY=16.2305 StartZ=0 EndX=-34.1121 EndY=-16.2305 EndZ=0
    g11: LineSegment StartX=-34.1121 StartY=-16.2305 StartZ=0 EndX=-31.1121 EndY=-21.4267 EndZ=0
    g12: LineSegment StartX=-31.1121 StartY=-21.4267 StartZ=0 EndX=-3 EndY=-37.6572 EndZ=0
    g13: LineSegment StartX=-3 StartY=-37.6572 StartZ=0 EndX=3 EndY=-37.6572 EndZ=0
    g14: LineSegment StartX=3 StartY=-37.6572 StartZ=0 EndX=31.1121 EndY=-21.4267 EndZ=0
    g15: LineSegment StartX=31.1121 StartY=-21.4267 StartZ=0 EndX=34.1121 EndY=-16.2305 EndZ=0
    g16: LineSegment StartX=34.1121 StartY=-16.2305 StartZ=0 EndX=34.1121 EndY=16.2305 EndZ=0
    g17: LineSegment StartX=34.1121 StartY=16.2305 StartZ=0 EndX=31.1121 EndY=21.4267 EndZ=0
    g18: LineSegment StartX=31.1121 StartY=21.4267 StartZ=0 EndX=3 EndY=37.6572 EndZ=0
    g19: Circle CenterX=0 CenterY=0 CenterZ=0 NormalX=0 NormalY=0 NormalZ=1 AngleXU=0 Radius=37.7765
    g20: LineSegment StartX=-31.1121 StartY=21.4267 StartZ=0 EndX=-3 EndY=5.19615 EndZ=0
    g21: LineSegment StartX=-3 StartY=5.19615 StartZ=0 EndX=-3 EndY=37.6572 EndZ=0
    g22: LineSegment StartX=3 StartY=5.19615 StartZ=0 EndX=3 EndY=37.6572 EndZ=0
    g23: LineSegment StartX=3 StartY=5.19615 StartZ=0 EndX=31.1121 EndY=21.4267 EndZ=0
    g24: LineSegment StartX=34.1121 StartY=16.2305 StartZ=0 EndX=6 EndY=0 EndZ=0
    g25: LineSegment StartX=34.1121 StartY=-16.2305 StartZ=0 EndX=6 EndY=0 EndZ=0
    g26: LineSegment StartX=31.1121 StartY=-21.4267 StartZ=0 EndX=3 EndY=-5.19615 EndZ=0
    g27: LineSegment StartX=3 StartY=-5.19615 StartZ=0 EndX=3 EndY=-37.6572 EndZ=0
    g28: LineSegment StartX=-3 StartY=-37.6572 StartZ=0 EndX=-3 EndY=-5.19615 EndZ=0
    g29: LineSegment StartX=-31.1121 StartY=-21.4267 StartZ=0 EndX=-3 EndY=-5.19615 EndZ=0
    g30: LineSegment StartX=-34.1121 StartY=-16.2305 StartZ=0 EndX=-6 EndY=0 EndZ=0
    g31: LineSegment StartX=-34.1121 StartY=16.2305 StartZ=0 EndX=-6 EndY=0 EndZ=0
    g32: LineSegment StartX=3 StartY=46.6572 StartZ=0 EndX=-3 EndY=46.6572 EndZ=0
    g33: LineSegment StartX=-3 StartY=46.6572 StartZ=0 EndX=-38.9063 EndY=25.9267 EndZ=0
    g34: LineSegment StartX=-38.9063 StartY=25.9267 StartZ=0 EndX=-41.9063 EndY=20.7305 EndZ=0
    g35: LineSegment StartX=-41.9063 StartY=20.7305 StartZ=0 EndX=-41.9063 EndY=-20.7305 EndZ=0
    g36: LineSegment StartX=-41.9063 StartY=-20.7305 StartZ=0 EndX=-38.9063 EndY=-25.9267 EndZ=0
    g37: LineSegment StartX=-38.9063 StartY=-25.9267 StartZ=0 EndX=-3 EndY=-46.6572 EndZ=0
    g38: LineSegment StartX=-3 StartY=-46.6572 StartZ=0 EndX=3 EndY=-46.6572 EndZ=0
    g39: LineSegment StartX=3 StartY=-46.6572 StartZ=0 EndX=38.9063 EndY=-25.9267 EndZ=0
    g40: LineSegment StartX=38.9063 StartY=-25.9267 StartZ=0 EndX=41.9063 EndY=-20.7305 EndZ=0
    g41: LineSegment StartX=41.9063 StartY=-20.7305 StartZ=0 EndX=41.9063 EndY=20.7305 EndZ=0
    g42: LineSegment StartX=41.9063 StartY=20.7305 StartZ=0 EndX=38.9063 EndY=25.9267 EndZ=0
    g43: LineSegment StartX=38.9063 StartY=25.9267 StartZ=0 EndX=3 EndY=46.6572 EndZ=0
    g44: Circle CenterX=0 CenterY=0 CenterZ=0 NormalX=0 NormalY=0 NormalZ=1 AngleXU=0 Radius=46.7535
    g45: LineSegment StartX=-3 StartY=46.6572 StartZ=0 EndX=-19.6541 EndY=37.0419 EndZ=0
    g46: LineSegment StartX=-38.9063 StartY=25.9267 StartZ=0 EndX=-22.2522 EndY=35.5419 EndZ=0
    g47: LineSegment StartX=-41.9063 StartY=20.7305 StartZ=0 EndX=-41.9063 EndY=1.5 EndZ=0
    g48: LineSegment StartX=-41.9063 StartY=-20.7305 StartZ=0 EndX=-41.9063 EndY=-1.5 EndZ=0
    g49: LineSegment StartX=-38.9063 StartY=-25.9267 StartZ=0 EndX=-22.2522 EndY=-35.5419 EndZ=0
    g50: LineSegment StartX=-3 StartY=-46.6572 StartZ=0 EndX=-19.6541 EndY=-37.0419 EndZ=0
    g51: LineSegment StartX=3 StartY=-46.6572 StartZ=0 EndX=19.6541 EndY=-37.0419 EndZ=0
    g52: LineSegment StartX=38.9063 StartY=-25.9267 StartZ=0 EndX=22.2522 EndY=-35.5419 EndZ=0
    g53: LineSegment StartX=41.9063 StartY=-20.7305 StartZ=0 EndX=41.9063 EndY=-1.5 EndZ=0
    g54: LineSegment StartX=41.9063 StartY=20.7305 StartZ=0 EndX=41.9063 EndY=1.5 EndZ=0
    g55: LineSegment StartX=38.9063 StartY=25.9267 StartZ=0 EndX=22.2522 EndY=35.5419 EndZ=0
    g56: LineSegment StartX=3 StartY=46.6572 StartZ=0 EndX=19.6541 EndY=37.0419 EndZ=0
    g57: LineSegment StartX=81.0843 StartY=140.442 StartZ=0 EndX=-81.0843 EndY=140.442 EndZ=0
    g58: LineSegment StartX=-81.0843 StartY=140.442 StartZ=0 EndX=-162.169 EndY=2.84e-14 EndZ=0
    g59: LineSegment StartX=-162.169 StartY=2.33e-14 StartZ=0 EndX=-81.0843 EndY=-140.442 EndZ=0
    g60: LineSegment StartX=-81.0843 StartY=-140.442 StartZ=0 EndX=81.0843 EndY=-140.442 EndZ=0
    g61: LineSegment StartX=81.0843 StartY=-140.442 StartZ=0 EndX=162.169 EndY=-2.84e-14 EndZ=0
    g62: LineSegment StartX=162.169 StartY=-1.79e-14 StartZ=0 EndX=81.0843 EndY=140.442 EndZ=0
    g63: Circle CenterX=0 CenterY=0 CenterZ=0 NormalX=0 NormalY=0 NormalZ=1 AngleXU=0 Radius=162.169
    g64: LineSegment StartX=79.3523 StartY=140.442 StartZ=0 EndX=81.9504 EndY=138.942 EndZ=0
    g65: LineSegment StartX=81.9504 StartY=138.942 StartZ=0 EndX=81.9504 EndY=141.942 EndZ=0
    g66: LineSegment StartX=81.9504 StartY=141.942 StartZ=0 EndX=79.3523 EndY=140.442 EndZ=0
    g67: Circle CenterX=81.0843 CenterY=140.442 CenterZ=0 NormalX=0 NormalY=0 NormalZ=1 AngleXU=0 Radius=1.73205
    g68: LineSegment StartX=-79.3523 StartY=140.442 StartZ=0 EndX=-81.9504 EndY=141.942 EndZ=0
    g69: LineSegment StartX=-81.9504 StartY=141.942 StartZ=0 EndX=-81.9504 EndY=138.942 EndZ=0
    g70: LineSegment StartX=-81.9504 StartY=138.942 StartZ=0 EndX=-79.3523 EndY=140.442 EndZ=0
    g71: Circle CenterX=-81.0843 CenterY=140.442 CenterZ=0 NormalX=0 NormalY=0 NormalZ=1 AngleXU=0 Radius=1.73205
    g72: LineSegment StartX=-161.303 StartY=1.5 StartZ=0 EndX=-163.901 EndY=3.93e-14 EndZ=0
    g73: LineSegment StartX=-163.901 StartY=3.93e-14 StartZ=0 EndX=-161.303 EndY=-1.5 EndZ=0
    g74: LineSegment StartX=-161.303 StartY=-1.5 StartZ=0 EndX=-161.303 EndY=1.5 EndZ=0
    g75: Circle CenterX=-162.169 CenterY=2.33e-14 CenterZ=0 NormalX=0 NormalY=0 NormalZ=1 AngleXU=0 Radius=1.73205
    g76: LineSegment StartX=-81.9504 StartY=-138.942 StartZ=0 EndX=-81.9504 EndY=-141.942 EndZ=0
    g77: LineSegment StartX=-81.9504 StartY=-141.942 StartZ=0 EndX=-79.3523 EndY=-140.442 EndZ=0
    g78: LineSegment StartX=-79.3523 StartY=-140.442 StartZ=0 EndX=-81.9504 EndY=-138.942 EndZ=0
    g79: Circle CenterX=-81.0843 CenterY=-140.442 CenterZ=0 NormalX=0 NormalY=0 NormalZ=1 AngleXU=0 Radius=1.73205
    g80: LineSegment StartX=79.3523 StartY=-140.442 StartZ=0 EndX=81.9504 EndY=-141.942 EndZ=0
    g81: LineSegment StartX=81.9504 StartY=-141.942 StartZ=0 EndX=81.9504 EndY=-138.942 EndZ=0
    g82: LineSegment StartX=81.9504 StartY=-138.942 StartZ=0 EndX=79.3523 EndY=-140.442 EndZ=0
    g83: Circle CenterX=81.0843 CenterY=-140.442 CenterZ=0 NormalX=0 NormalY=0 NormalZ=1 AngleXU=0 Radius=1.73205
    g84: LineSegment StartX=161.303 StartY=-1.5 StartZ=0 EndX=163.901 EndY=2.9e-15 EndZ=0
    g85: LineSegment StartX=163.901 StartY=2.9e-15 StartZ=0 EndX=161.303 EndY=1.5 EndZ=0
    g86: LineSegment StartX=161.303 StartY=1.5 StartZ=0 EndX=161.303 EndY=-1.5 EndZ=0
    g87: Circle CenterX=162.169 CenterY=-1.79e-14 CenterZ=0 NormalX=0 NormalY=0 NormalZ=1 AngleXU=0 Radius=1.73205
    g88: LineSegment StartX=-22.2522 StartY=35.5419 StartZ=0 EndX=-81.9504 EndY=138.942 EndZ=0
    g89: LineSegment StartX=-79.3523 StartY=140.442 StartZ=0 EndX=-19.6541 EndY=37.0419 EndZ=0
    g90: LineSegment StartX=-41.9063 StartY=1.5 StartZ=0 EndX=-161.303 EndY=1.5 EndZ=0
    g91: LineSegment StartX=-41.9063 StartY=-1.5 StartZ=0 EndX=-161.303 EndY=-1.5 EndZ=0
    g92: LineSegment StartX=-22.2522 StartY=-35.5419 StartZ=0 EndX=-81.9504 EndY=-138.942 EndZ=0
    g93: LineSegment StartX=-19.6541 StartY=-37.0419 StartZ=0 EndX=-79.3523 EndY=-140.442 EndZ=0
    g94: LineSegment StartX=19.6541 StartY=-37.0419 StartZ=0 EndX=79.3523 EndY=-140.442 EndZ=0
    g95: LineSegment StartX=22.2522 StartY=-35.5419 StartZ=0 EndX=81.9504 EndY=-138.942 EndZ=0
    g96: LineSegment StartX=41.9063 StartY=-1.5 StartZ=0 EndX=161.303 EndY=-1.5 EndZ=0
    g97: LineSegment StartX=41.9063 StartY=1.5 StartZ=0 EndX=161.303 EndY=1.5 EndZ=0
    g98: LineSegment StartX=22.2522 StartY=35.5419 StartZ=0 EndX=81.9504 EndY=138.942 EndZ=0
    g99: LineSegment StartX=19.6541 StartY=37.0419 StartZ=0 EndX=79.3523 EndY=140.442 EndZ=0
    g100: LineSegment StartX=0 StartY=286.132 StartZ=0 EndX=-247.798 EndY=143.066 EndZ=0
    g101: LineSegment StartX=-247.798 StartY=143.066 StartZ=0 EndX=-247.798 EndY=-143.066 EndZ=0
    g102: LineSegment StartX=-247.798 StartY=-143.066 StartZ=0 EndX=0 EndY=-286.132 EndZ=0
    g103: LineSegment StartX=7.6e-15 StartY=-286.132 StartZ=0 EndX=247.798 EndY=-143.066 EndZ=0
    g104: LineSegment StartX=247.798 StartY=-143.066 StartZ=0 EndX=247.798 EndY=143.066 EndZ=0
    g105: LineSegment StartX=247.798 StartY=143.066 StartZ=0 EndX=0 EndY=286.132 EndZ=0
    g106: Circle CenterX=0 CenterY=0 CenterZ=0 NormalX=0 NormalY=0 NormalZ=1 AngleXU=0 Radius=286.132
    g107: LineSegment StartX=3 StartY=291.328 StartZ=0 EndX=-3 EndY=291.328 EndZ=0
    g108: LineSegment StartX=-3 StartY=291.328 StartZ=0 EndX=-6 EndY=286.132 EndZ=0
    g109: LineSegment StartX=-6 StartY=286.132 StartZ=0 EndX=-3 EndY=280.936 EndZ=0
    g110: LineSegment StartX=-3 StartY=280.936 StartZ=0 EndX=3 EndY=280.936 EndZ=0
    g111: LineSegment StartX=3 StartY=280.936 StartZ=0 EndX=6 EndY=286.132 EndZ=0
    g112: LineSegment StartX=6 StartY=286.132 StartZ=0 EndX=3 EndY=291.328 EndZ=0
    g113: Circle CenterX=0 CenterY=286.132 CenterZ=0 NormalX=0 NormalY=0 NormalZ=1 AngleXU=0 Radius=6
    g114: LineSegment StartX=-244.798 StartY=148.262 StartZ=0 EndX=-250.798 EndY=148.262 EndZ=0
    g115: LineSegment StartX=-250.798 StartY=148.262 StartZ=0 EndX=-253.798 EndY=143.066 EndZ=0
    g116: LineSegment StartX=-253.798 StartY=143.066 StartZ=0 EndX=-250.798 EndY=137.87 EndZ=0
    g117: LineSegment StartX=-250.798 StartY=137.87 StartZ=0 EndX=-244.798 EndY=137.87 EndZ=0
    g118: LineSegment StartX=-244.798 StartY=137.87 StartZ=0 EndX=-241.798 EndY=143.066 EndZ=0
    g119: LineSegment StartX=-241.798 StartY=143.066 StartZ=0 EndX=-244.798 EndY=148.262 EndZ=0
    g120: Circle CenterX=-247.798 CenterY=143.066 CenterZ=0 NormalX=0 NormalY=0 NormalZ=1 AngleXU=0 Radius=6
    g121: LineSegment StartX=-244.798 StartY=-137.87 StartZ=0 EndX=-250.798 EndY=-137.87 EndZ=0
    g122: LineSegment StartX=-250.798 StartY=-137.87 StartZ=0 EndX=-253.798 EndY=-143.066 EndZ=0
    g123: LineSegment StartX=-253.798 StartY=-143.066 StartZ=0 EndX=-250.798 EndY=-148.262 EndZ=0
    g124: LineSegment StartX=-250.798 StartY=-148.262 StartZ=0 EndX=-244.798 EndY=-148.262 EndZ=0
    g125: LineSegment StartX=-244.798 StartY=-148.262 StartZ=0 EndX=-241.798 EndY=-143.066 EndZ=0
    g126: LineSegment StartX=-241.798 StartY=-143.066 StartZ=0 EndX=-244.798 EndY=-137.87 EndZ=0
    g127: Circle CenterX=-247.798 CenterY=-143.066 CenterZ=0 NormalX=0 NormalY=0 NormalZ=1 AngleXU=0 Radius=6
    g128: LineSegment StartX=3 StartY=-280.936 StartZ=0 EndX=-3 EndY=-280.936 EndZ=0
    g129: LineSegment StartX=-3 StartY=-280.936 StartZ=0 EndX=-6 EndY=-286.132 EndZ=0
    g130: LineSegment StartX=-6 StartY=-286.132 StartZ=0 EndX=-3 EndY=-291.328 EndZ=0
    g131: LineSegment StartX=-3 StartY=-291.328 StartZ=0 EndX=3 EndY=-291.328 EndZ=0
    g132: LineSegment StartX=3 StartY=-291.328 StartZ=0 EndX=6 EndY=-286.132 EndZ=0
    g133: LineSegment StartX=6 StartY=-286.132 StartZ=0 EndX=3 EndY=-280.936 EndZ=0
    g134: Circle CenterX=7.6e-15 CenterY=-286.132 CenterZ=0 NormalX=0 NormalY=0 NormalZ=1 AngleXU=0 Radius=6
    g135: LineSegment StartX=250.798 StartY=-137.87 StartZ=0 EndX=244.798 EndY=-137.87 EndZ=0
    g136: LineSegment StartX=244.798 StartY=-137.87 StartZ=0 EndX=241.798 EndY=-143.066 EndZ=0
    g137: LineSegment StartX=241.798 StartY=-143.066 StartZ=0 EndX=244.798 EndY=-148.262 EndZ=0
    g138: LineSegment StartX=244.798 StartY=-148.262 StartZ=0 EndX=250.798 EndY=-148.262 EndZ=0
    g139: LineSegment StartX=250.798 StartY=-148.262 StartZ=0 EndX=253.798 EndY=-143.066 EndZ=0
    g140: LineSegment StartX=253.798 StartY=-143.066 StartZ=0 EndX=250.798 EndY=-137.87 EndZ=0
    g141: Circle CenterX=247.798 CenterY=-143.066 CenterZ=0 NormalX=0 NormalY=0 NormalZ=1 AngleXU=0 Radius=6
    g142: LineSegment StartX=250.798 StartY=148.262 StartZ=0 EndX=244.798 EndY=148.262 EndZ=0
    g143: LineSegment StartX=244.798 StartY=148.262 StartZ=0 EndX=241.798 EndY=143.066 EndZ=0
    g144: LineSegment StartX=241.798 StartY=143.066 StartZ=0 EndX=244.798 EndY=137.87 EndZ=0
    g145: LineSegment StartX=244.798 StartY=137.87 StartZ=0 EndX=250.798 EndY=137.87 EndZ=0
    g146: LineSegment StartX=250.798 StartY=137.87 StartZ=0 EndX=253.798 EndY=143.066 EndZ=0
    g147: LineSegment StartX=253.798 StartY=143.066 StartZ=0 EndX=250.798 EndY=148.262 EndZ=0
    g148: Circle CenterX=247.798 CenterY=143.066 CenterZ=0 NormalX=0 NormalY=0 NormalZ=1 AngleXU=0 Radius=6
    g149: LineSegment StartX=3 StartY=327.55 StartZ=0 EndX=-3 EndY=327.55 EndZ=0
    g150: LineSegment StartX=-3 StartY=327.55 StartZ=0 EndX=-34.3687 EndY=309.439 EndZ=0
    g151: LineSegment StartX=-34.3687 StartY=309.439 StartZ=0 EndX=-37.3687 EndY=304.243 EndZ=0
    g152: LineSegment StartX=-37.3687 StartY=304.243 StartZ=0 EndX=-37.3687 EndY=268.021 EndZ=0
    g153: LineSegment StartX=-37.3687 StartY=268.021 StartZ=0 EndX=-34.3687 EndY=262.825 EndZ=0
    g154: LineSegment StartX=-34.3687 StartY=262.825 StartZ=0 EndX=-3 EndY=244.714 EndZ=0
    g155: LineSegment StartX=-3 StartY=244.714 StartZ=0 EndX=3 EndY=244.714 EndZ=0
    g156: LineSegment StartX=3 StartY=244.714 StartZ=0 EndX=34.3687 EndY=262.825 EndZ=0
    g157: LineSegment StartX=34.3687 StartY=262.825 StartZ=0 EndX=37.3687 EndY=268.021 EndZ=0
    g158: LineSegment StartX=37.3687 StartY=268.021 StartZ=0 EndX=37.3687 EndY=304.243 EndZ=0
    g159: LineSegment StartX=37.3687 StartY=304.243 StartZ=0 EndX=34.3687 EndY=309.439 EndZ=0
    g160: LineSegment StartX=34.3687 StartY=309.439 StartZ=0 EndX=3 EndY=327.55 EndZ=0
    g161: Circle CenterX=0 CenterY=286.132 CenterZ=0 NormalX=0 NormalY=0 NormalZ=1 AngleXU=0 Radius=41.5261
    g162: LineSegment StartX=3 StartY=345.082 StartZ=0 EndX=-3 EndY=345.082 EndZ=0
    g163: LineSegment StartX=-3 StartY=345.082 StartZ=0 EndX=-49.5522 EndY=318.205 EndZ=0
    g164: LineSegment StartX=-49.5522 StartY=318.205 StartZ=0 EndX=-52.5522 EndY=313.009 EndZ=0
    g165: LineSegment StartX=-52.5522 StartY=313.009 StartZ=0 EndX=-52.5522 EndY=259.255 EndZ=0
    g166: LineSegment StartX=-52.5522 StartY=259.255 StartZ=0 EndX=-49.5522 EndY=254.059 EndZ=0
    g167: LineSegment StartX=-49.5522 StartY=254.059 StartZ=0 EndX=-3 EndY=227.182 EndZ=0
    g168: LineSegment StartX=-3 StartY=227.182 StartZ=0 EndX=3 EndY=227.182 EndZ=0
    g169: LineSegment StartX=3 StartY=227.182 StartZ=0 EndX=49.5522 EndY=254.059 EndZ=0
    g170: LineSegment StartX=49.5522 StartY=254.059 StartZ=0 EndX=52.5522 EndY=259.255 EndZ=0
    g171: LineSegment StartX=52.5522 StartY=259.255 StartZ=0 EndX=52.5522 EndY=313.009 EndZ=0
    g172: LineSegment StartX=52.5522 StartY=313.009 StartZ=0 EndX=49.5522 EndY=318.205 EndZ=0
    g173: LineSegment StartX=49.5522 StartY=318.205 StartZ=0 EndX=3 EndY=345.082 EndZ=0
    g174: Circle CenterX=0 CenterY=286.132 CenterZ=0 NormalX=0 NormalY=0 NormalZ=1 AngleXU=0 Radius=59.0263
    g175: LineSegment StartX=-3 StartY=327.55 StartZ=0 EndX=-3 EndY=291.328 EndZ=0
    g176: LineSegment StartX=-3 StartY=291.328 StartZ=0 EndX=-34.3687 EndY=309.439 EndZ=0
    g177: LineSegment StartX=-37.3687 StartY=304.243 StartZ=0 EndX=-6 EndY=286.132 EndZ=0
    g178: LineSegment StartX=-37.3687 StartY=268.021 StartZ=0 EndX=-6 EndY=286.132 EndZ=0
    g179: LineSegment StartX=-3 StartY=244.714 StartZ=0 EndX=-3 EndY=280.936 EndZ=0
    g180: LineSegment StartX=-34.3687 StartY=262.825 StartZ=0 EndX=-3 EndY=280.936 EndZ=0
    g181: LineSegment StartX=3 StartY=244.714 StartZ=0 EndX=3 EndY=280.936 EndZ=0
    g182: LineSegment StartX=34.3687 StartY=262.825 StartZ=0 EndX=3 EndY=280.936 EndZ=0
    g183: LineSegment StartX=37.3687 StartY=268.021 StartZ=0 EndX=6 EndY=286.132 EndZ=0
    g184: LineSegment StartX=37.3687 StartY=304.243 StartZ=0 EndX=6 EndY=286.132 EndZ=0
    g185: LineSegment StartX=34.3687 StartY=309.439 StartZ=0 EndX=3 EndY=291.328 EndZ=0
    g186: LineSegment StartX=3 StartY=327.55 StartZ=0 EndX=3 EndY=291.328 EndZ=0
    g187: LineSegment StartX=-3 StartY=227.182 StartZ=0 EndX=-3 EndY=46.6572 EndZ=0
    g188: LineSegment StartX=3 StartY=227.182 StartZ=0 EndX=3 EndY=46.6572 EndZ=0
    g189: LineSegment StartX=-3 StartY=227.182 StartZ=0 EndX=-22.7048 EndY=238.559 EndZ=0
    g190: LineSegment StartX=-22.7048 StartY=238.559 StartZ=0 EndX=-79.3523 EndY=140.442 EndZ=0
    g191: LineSegment StartX=3 StartY=227.182 StartZ=0 EndX=22.7048 EndY=238.559 EndZ=0
    g192: LineSegment StartX=22.7048 StartY=238.559 StartZ=0 EndX=79.3523 EndY=140.442 EndZ=0
    g193: LineSegment StartX=-49.5522 StartY=254.059 StartZ=0 EndX=-25.3028 EndY=240.059 EndZ=0
    g194: LineSegment StartX=-25.3028 StartY=240.059 StartZ=0 EndX=-81.9504 EndY=141.942 EndZ=0
    g195: LineSegment StartX=49.5522 StartY=254.059 StartZ=0 EndX=25.3028 EndY=240.059 EndZ=0
    g196: LineSegment StartX=25.3028 StartY=240.059 StartZ=0 EndX=81.9504 EndY=141.942 EndZ=0
    g197: LineSegment StartX=-244.798 StartY=199.414 StartZ=0 EndX=-250.798 EndY=199.414 EndZ=0
    g198: LineSegment StartX=-250.798 StartY=199.414 StartZ=0 EndX=-295.097 EndY=173.838 EndZ=0
    g199: LineSegment StartX=-295.097 StartY=173.838 StartZ=0 EndX=-298.097 EndY=168.642 EndZ=0
    g200: LineSegment StartX=-298.097 StartY=168.642 StartZ=0 EndX=-298.097 EndY=117.49 EndZ=0
    g201: LineSegment StartX=-298.097 StartY=117.49 StartZ=0 EndX=-295.097 EndY=112.294 EndZ=0
    g202: LineSegment StartX=-295.097 StartY=112.294 StartZ=0 EndX=-250.798 EndY=86.7178 EndZ=0
    g203: LineSegment StartX=-250.798 StartY=86.7178 StartZ=0 EndX=-244.798 EndY=86.7178 EndZ=0
    g204: LineSegment StartX=-244.798 StartY=86.7178 StartZ=0 EndX=-200.499 EndY=112.294 EndZ=0
    g205: LineSegment StartX=-200.499 StartY=112.294 StartZ=0 EndX=-197.499 EndY=117.49 EndZ=0
    g206: LineSegment StartX=-197.499 StartY=117.49 StartZ=0 EndX=-197.499 EndY=168.642 EndZ=0
    g207: LineSegment StartX=-197.499 StartY=168.642 StartZ=0 EndX=-200.499 EndY=173.838 EndZ=0
    g208: LineSegment StartX=-200.499 StartY=173.838 StartZ=0 EndX=-244.798 EndY=199.414 EndZ=0
    g209: Circle CenterX=-247.798 CenterY=143.066 CenterZ=0 NormalX=0 NormalY=0 NormalZ=1 AngleXU=0 Radius=56.428
    g210: LineSegment StartX=-244.798 StartY=220.713 StartZ=0 EndX=-250.798 EndY=220.713 EndZ=0
    g211: LineSegment StartX=-250.798 StartY=220.713 StartZ=0 EndX=-313.542 EndY=184.487 EndZ=0
    g212: LineSegment StartX=-313.542 StartY=184.487 StartZ=0 EndX=-316.542 EndY=179.291 EndZ=0
    g213: LineSegment StartX=-316.542 StartY=179.291 StartZ=0 EndX=-316.542 EndY=106.841 EndZ=0
    g214: LineSegment StartX=-316.542 StartY=106.841 StartZ=0 EndX=-313.542 EndY=101.645 EndZ=0
    g215: LineSegment StartX=-313.542 StartY=101.645 StartZ=0 EndX=-250.798 EndY=65.4193 EndZ=0
    g216: LineSegment StartX=-250.798 StartY=65.4193 StartZ=0 EndX=-244.798 EndY=65.4193 EndZ=0
    g217: LineSegment StartX=-244.798 StartY=65.4193 StartZ=0 EndX=-182.054 EndY=101.645 EndZ=0
    g218: LineSegment StartX=-182.054 StartY=101.645 StartZ=0 EndX=-179.054 EndY=106.841 EndZ=0
    g219: LineSegment StartX=-179.054 StartY=106.841 StartZ=0 EndX=-179.054 EndY=179.291 EndZ=0
    g220: LineSegment StartX=-179.054 StartY=179.291 StartZ=0 EndX=-182.054 EndY=184.487 EndZ=0
    g221: LineSegment StartX=-182.054 StartY=184.487 StartZ=0 EndX=-244.798 EndY=220.713 EndZ=0
    g222: Circle CenterX=-247.798 CenterY=143.066 CenterZ=0 NormalX=0 NormalY=0 NormalZ=1 AngleXU=0 Radius=77.7046
    g223: LineSegment StartX=-179.054 StartY=106.841 StartZ=0 EndX=-179.054 EndY=138.942 EndZ=0
    g224: LineSegment StartX=-179.054 StartY=138.942 StartZ=0 EndX=-81.9504 EndY=138.942 EndZ=0
    g225: LineSegment StartX=-81.9504 StartY=141.942 StartZ=0 EndX=-179.054 EndY=141.942 EndZ=0
    g226: LineSegment StartX=-179.054 StartY=141.942 StartZ=0 EndX=-179.054 EndY=179.291 EndZ=0
    g227: LineSegment StartX=-179.054 StartY=179.291 StartZ=0 EndX=-49.5522 EndY=254.059 EndZ=0
    g228: LineSegment StartX=-182.054 StartY=184.487 StartZ=0 EndX=-52.5522 EndY=259.255 EndZ=0
    g229: LineSegment StartX=-38.9063 StartY=25.9267 StartZ=0 EndX=-179.054 EndY=106.841 EndZ=0
    g230: LineSegment StartX=-41.9063 StartY=20.7305 StartZ=0 EndX=-182.054 EndY=101.645 EndZ=0
    g231: LineSegment StartX=-161.303 StartY=1.5 StartZ=0 EndX=-209.854 EndY=85.5939 EndZ=0
    g232: LineSegment StartX=-209.854 StartY=85.5939 StartZ=0 EndX=-182.054 EndY=101.645 EndZ=0
    g233: LineSegment StartX=-163.901 StartY=3.93e-14 StartZ=0 EndX=-212.452 EndY=84.0939 EndZ=0
    g234: LineSegment StartX=-212.452 StartY=84.0939 StartZ=0 EndX=-244.798 EndY=65.4193 EndZ=0
    g235: LineSegment StartX=-244.798 StartY=-103.819 StartZ=0 EndX=-250.798 EndY=-103.819 EndZ=0
    g236: LineSegment StartX=-250.798 StartY=-103.819 StartZ=0 EndX=-280.286 EndY=-120.844 EndZ=0
    g237: LineSegment StartX=-280.286 StartY=-120.844 StartZ=0 EndX=-283.286 EndY=-126.041 EndZ=0
    g238: LineSegment StartX=-283.286 StartY=-126.041 StartZ=0 EndX=-283.286 EndY=-160.091 EndZ=0
    g239: LineSegment StartX=-283.286 StartY=-160.091 StartZ=0 EndX=-280.286 EndY=-165.288 EndZ=0
    g240: LineSegment StartX=-280.286 StartY=-165.288 StartZ=0 EndX=-250.798 EndY=-182.313 EndZ=0
    g241: LineSegment StartX=-250.798 StartY=-182.313 StartZ=0 EndX=-244.798 EndY=-182.313 EndZ=0
    g242: LineSegment StartX=-244.798 StartY=-182.313 StartZ=0 EndX=-215.309 EndY=-165.288 EndZ=0
    g243: LineSegment StartX=-215.309 StartY=-165.288 StartZ=0 EndX=-212.309 EndY=-160.091 EndZ=0
    g244: LineSegment StartX=-212.309 StartY=-160.091 StartZ=0 EndX=-212.309 EndY=-126.041 EndZ=0
    g245: LineSegment StartX=-212.309 StartY=-126.041 StartZ=0 EndX=-215.309 EndY=-120.844 EndZ=0
    g246: LineSegment StartX=-215.309 StartY=-120.844 StartZ=0 EndX=-244.798 EndY=-103.819 EndZ=0
    g247: Circle CenterX=-247.798 CenterY=-143.066 CenterZ=0 NormalX=0 NormalY=0 NormalZ=1 AngleXU=0 Radius=39.3615
    g248: LineSegment StartX=-244.798 StartY=-72.659 StartZ=0 EndX=-250.798 EndY=-72.659 EndZ=0
    g249: LineSegment StartX=-250.798 StartY=-72.659 StartZ=0 EndX=-307.272 EndY=-105.264 EndZ=0
    g250: LineSegment StartX=-307.272 StartY=-105.264 StartZ=0 EndX=-310.272 EndY=-110.461 EndZ=0
    g251: LineSegment StartX=-310.272 StartY=-110.461 StartZ=0 EndX=-310.272 EndY=-175.671 EndZ=0
    g252: LineSegment StartX=-310.272 StartY=-175.671 StartZ=0 EndX=-307.272 EndY=-180.868 EndZ=0
    g253: LineSegment StartX=-307.272 StartY=-180.868 StartZ=0 EndX=-250.798 EndY=-213.473 EndZ=0
    g254: LineSegment StartX=-250.798 StartY=-213.473 StartZ=0 EndX=-244.798 EndY=-213.473 EndZ=0
    g255: LineSegment StartX=-244.798 StartY=-213.473 StartZ=0 EndX=-188.323 EndY=-180.868 EndZ=0
    g256: LineSegment StartX=-188.323 StartY=-180.868 StartZ=0 EndX=-185.323 EndY=-175.671 EndZ=0
    g257: LineSegment StartX=-185.323 StartY=-175.671 StartZ=0 EndX=-185.323 EndY=-110.461 EndZ=0
    g258: LineSegment StartX=-185.323 StartY=-110.461 StartZ=0 EndX=-188.323 EndY=-105.264 EndZ=0
    g259: LineSegment StartX=-188.323 StartY=-105.264 StartZ=0 EndX=-244.798 EndY=-72.659 EndZ=0
    g260: Circle CenterX=-247.798 CenterY=-143.066 CenterZ=0 NormalX=0 NormalY=0 NormalZ=1 AngleXU=0 Radius=70.4708
    g261: LineSegment StartX=3 StartY=-236.318 StartZ=0 EndX=-3 EndY=-236.318 EndZ=0
    g262: LineSegment StartX=-3 StartY=-236.318 StartZ=0 EndX=-41.6398 EndY=-258.627 EndZ=0
    g263: LineSegment StartX=-41.6398 StartY=-258.627 StartZ=0 EndX=-44.6398 EndY=-263.823 EndZ=0
    g264: LineSegment StartX=-44.6398 StartY=-263.823 StartZ=0 EndX=-44.6398 EndY=-308.441 EndZ=0
    g265: LineSegment StartX=-44.6398 StartY=-308.441 StartZ=0 EndX=-41.6398 EndY=-313.637 EndZ=0
    g266: LineSegment StartX=-41.6398 StartY=-313.637 StartZ=0 EndX=-3 EndY=-335.946 EndZ=0
    g267: LineSegment StartX=-3 StartY=-335.946 StartZ=0 EndX=3 EndY=-335.946 EndZ=0
    g268: LineSegment StartX=3 StartY=-335.946 StartZ=0 EndX=41.6398 EndY=-313.637 EndZ=0
    g269: LineSegment StartX=41.6398 StartY=-313.637 StartZ=0 EndX=44.6398 EndY=-308.441 EndZ=0
    g270: LineSegment StartX=44.6398 StartY=-308.441 StartZ=0 EndX=44.6398 EndY=-263.823 EndZ=0
    g271: LineSegment StartX=44.6398 StartY=-263.823 StartZ=0 EndX=41.6398 EndY=-258.627 EndZ=0
    g272: LineSegment StartX=41.6398 StartY=-258.627 StartZ=0 EndX=3 EndY=-236.318 EndZ=0
    g273: Circle CenterX=7.6e-15 CenterY=-286.132 CenterZ=0 NormalX=0 NormalY=0 NormalZ=1 AngleXU=0 Radius=49.9038
    g274: LineSegment StartX=3 StartY=-201.604 StartZ=0 EndX=-3 EndY=-201.604 EndZ=0
    g275: LineSegment StartX=-3 StartY=-201.604 StartZ=0 EndX=-71.7033 EndY=-241.27 EndZ=0
    g276: LineSegment StartX=-71.7033 StartY=-241.27 StartZ=0 EndX=-74.7033 EndY=-246.466 EndZ=0
    g277: LineSegment StartX=-74.7033 StartY=-246.466 StartZ=0 EndX=-74.7033 EndY=-325.798 EndZ=0
    g278: LineSegment StartX=-74.7033 StartY=-325.798 StartZ=0 EndX=-71.7033 EndY=-330.994 EndZ=0
    g279: LineSegment StartX=-71.7033 StartY=-330.994 StartZ=0 EndX=-3 EndY=-370.66 EndZ=0
    g280: LineSegment StartX=-3 StartY=-370.66 StartZ=0 EndX=3 EndY=-370.66 EndZ=0
    g281: LineSegment StartX=3 StartY=-370.66 StartZ=0 EndX=71.7033 EndY=-330.994 EndZ=0
    g282: LineSegment StartX=71.7033 StartY=-330.994 StartZ=0 EndX=74.7033 EndY=-325.798 EndZ=0
    g283: LineSegment StartX=74.7033 StartY=-325.798 StartZ=0 EndX=74.7033 EndY=-246.466 EndZ=0
    g284: LineSegment StartX=74.7033 StartY=-246.466 StartZ=0 EndX=71.7033 EndY=-241.27 EndZ=0
    g285: LineSegment StartX=71.7033 StartY=-241.27 StartZ=0 EndX=3 EndY=-201.604 EndZ=0
    g286: Circle CenterX=7.6e-15 CenterY=-286.132 CenterZ=0 NormalX=0 NormalY=0 NormalZ=1 AngleXU=0 Radius=84.5811
    g287: LineSegment StartX=250.798 StartY=-92.0165 StartZ=0 EndX=244.798 EndY=-92.0165 EndZ=0
    g288: LineSegment StartX=244.798 StartY=-92.0165 StartZ=0 EndX=205.087 EndY=-114.943 EndZ=0
    g289: LineSegment StartX=205.087 StartY=-114.943 StartZ=0 EndX=202.087 EndY=-120.139 EndZ=0
    g290: LineSegment StartX=202.087 StartY=-120.139 StartZ=0 EndX=202.087 EndY=-165.993 EndZ=0
    g291: LineSegment StartX=202.087 StartY=-165.993 StartZ=0 EndX=205.087 EndY=-171.189 EndZ=0
    g292: LineSegment StartX=205.087 StartY=-171.189 StartZ=0 EndX=244.798 EndY=-194.116 EndZ=0
    g293: LineSegment StartX=244.798 StartY=-194.116 StartZ=0 EndX=250.798 EndY=-194.116 EndZ=0
    g294: LineSegment StartX=250.798 StartY=-194.116 StartZ=0 EndX=290.508 EndY=-171.189 EndZ=0
    g295: LineSegment StartX=290.508 StartY=-171.189 StartZ=0 EndX=293.508 EndY=-165.993 EndZ=0
    g296: LineSegment StartX=293.508 StartY=-165.993 StartZ=0 EndX=293.508 EndY=-120.139 EndZ=0
    g297: LineSegment StartX=293.508 StartY=-120.139 StartZ=0 EndX=290.508 EndY=-114.943 EndZ=0
    g298: LineSegment StartX=290.508 StartY=-114.943 StartZ=0 EndX=250.798 EndY=-92.0165 EndZ=0
    g299: Circle CenterX=247.798 CenterY=-143.066 CenterZ=0 NormalX=0 NormalY=0 NormalZ=1 AngleXU=0 Radius=51.1376
    g300: LineSegment StartX=250.798 StartY=-79.2031 StartZ=0 EndX=244.798 EndY=-79.2031 EndZ=0
    g301: LineSegment StartX=244.798 StartY=-79.2031 StartZ=0 EndX=193.991 EndY=-108.536 EndZ=0
    g302: LineSegment StartX=193.991 StartY=-108.536 StartZ=0 EndX=190.991 EndY=-113.733 EndZ=0
    g303: LineSegment StartX=190.991 StartY=-113.733 StartZ=0 EndX=190.991 EndY=-172.399 EndZ=0
    g304: LineSegment StartX=190.991 StartY=-172.399 StartZ=0 EndX=193.991 EndY=-177.596 EndZ=0
    g305: LineSegment StartX=193.991 StartY=-177.596 StartZ=0 EndX=244.798 EndY=-206.929 EndZ=0
    g306: LineSegment StartX=244.798 StartY=-206.929 StartZ=0 EndX=250.798 EndY=-206.929 EndZ=0
    g307: LineSegment StartX=250.798 StartY=-206.929 StartZ=0 EndX=301.604 EndY=-177.596 EndZ=0
    g308: LineSegment StartX=301.604 StartY=-177.596 StartZ=0 EndX=304.604 EndY=-172.399 EndZ=0
    g309: LineSegment StartX=304.604 StartY=-172.399 StartZ=0 EndX=304.604 EndY=-113.733 EndZ=0
    g310: LineSegment StartX=304.604 StartY=-113.733 StartZ=0 EndX=301.604 EndY=-108.536 EndZ=0
    g311: LineSegment StartX=301.604 StartY=-108.536 StartZ=0 EndX=250.798 EndY=-79.2031 EndZ=0
    g312: Circle CenterX=247.798 CenterY=-143.066 CenterZ=0 NormalX=0 NormalY=0 NormalZ=1 AngleXU=0 Radius=63.9333
    g313: LineSegment StartX=250.798 StartY=183.11 StartZ=0 EndX=244.798 EndY=183.11 EndZ=0
    g314: LineSegment StartX=244.798 StartY=183.11 StartZ=0 EndX=214.618 EndY=165.686 EndZ=0
    g315: LineSegment StartX=214.618 StartY=165.686 StartZ=0 EndX=211.618 EndY=160.49 EndZ=0
    g316: LineSegment StartX=211.618 StartY=160.49 StartZ=0 EndX=211.618 EndY=125.642 EndZ=0
    g317: LineSegment StartX=211.618 StartY=125.642 StartZ=0 EndX=214.618 EndY=120.446 EndZ=0
    g318: LineSegment StartX=214.618 StartY=120.446 StartZ=0 EndX=244.798 EndY=103.022 EndZ=0
    g319: LineSegment StartX=244.798 StartY=103.022 StartZ=0 EndX=250.798 EndY=103.022 EndZ=0
    g320: LineSegment StartX=250.798 StartY=103.022 StartZ=0 EndX=280.977 EndY=120.446 EndZ=0
    g321: LineSegment StartX=280.977 StartY=120.446 StartZ=0 EndX=283.977 EndY=125.642 EndZ=0
    g322: LineSegment StartX=283.977 StartY=125.642 StartZ=0 EndX=283.977 EndY=160.49 EndZ=0
    g323: LineSegment StartX=283.977 StartY=160.49 StartZ=0 EndX=280.977 EndY=165.686 EndZ=0
    g324: LineSegment StartX=280.977 StartY=165.686 StartZ=0 EndX=250.798 EndY=183.11 EndZ=0
    g325: Circle CenterX=247.798 CenterY=143.066 CenterZ=0 NormalX=0 NormalY=0 NormalZ=1 AngleXU=0 Radius=40.1567
    g326: LineSegment StartX=250.798 StartY=201.143 StartZ=0 EndX=244.798 EndY=201.143 EndZ=0
    g327: LineSegment StartX=244.798 StartY=201.143 StartZ=0 EndX=199.001 EndY=174.703 EndZ=0
    g328: LineSegment StartX=199.001 StartY=174.703 StartZ=0 EndX=196.001 EndY=169.507 EndZ=0
    g329: LineSegment StartX=196.001 StartY=169.507 StartZ=0 EndX=196.001 EndY=116.625 EndZ=0
    g330: LineSegment StartX=196.001 StartY=116.625 StartZ=0 EndX=199.001 EndY=111.429 EndZ=0
    g331: LineSegment StartX=199.001 StartY=111.429 StartZ=0 EndX=244.798 EndY=84.9886 EndZ=0
    g332: LineSegment StartX=244.798 StartY=84.9886 StartZ=0 EndX=250.798 EndY=84.9886 EndZ=0
    g333: LineSegment StartX=250.798 StartY=84.9886 StartZ=0 EndX=296.594 EndY=111.429 EndZ=0
    g334: LineSegment StartX=296.594 StartY=111.429 StartZ=0 EndX=299.594 EndY=116.625 EndZ=0
    g335: LineSegment StartX=299.594 StartY=116.625 StartZ=0 EndX=299.594 EndY=169.507 EndZ=0
    g336: LineSegment StartX=299.594 StartY=169.507 StartZ=0 EndX=296.594 EndY=174.703 EndZ=0
    g337: LineSegment StartX=296.594 StartY=174.703 StartZ=0 EndX=250.798 EndY=201.143 EndZ=0
    g338: Circle CenterX=247.798 CenterY=143.066 CenterZ=0 NormalX=0 NormalY=0 NormalZ=1 AngleXU=0 Radius=58.1548
    g339: LineSegment StartX=-244.798 StartY=65.4193 StartZ=0 EndX=-244.798 EndY=-72.659 EndZ=0
    g340: LineSegment StartX=-250.798 StartY=65.4193 StartZ=0 EndX=-250.798 EndY=-72.659 EndZ=0
    g341: LineSegment StartX=-185.323 StartY=-175.671 StartZ=0 EndX=-71.7033 EndY=-241.27 EndZ=0
    g342: LineSegment StartX=-188.323 StartY=-180.868 StartZ=0 EndX=-74.7033 EndY=-246.466 EndZ=0
    g343: LineSegment StartX=71.7033 StartY=-241.27 StartZ=0 EndX=190.991 EndY=-172.399 EndZ=0
    g344: LineSegment StartX=74.7033 StartY=-246.466 StartZ=0 EndX=193.991 EndY=-177.596 EndZ=0
    g345: LineSegment StartX=244.798 StartY=-79.2031 StartZ=0 EndX=244.798 EndY=84.9886 EndZ=0
    g346: LineSegment StartX=250.798 StartY=-79.2031 StartZ=0 EndX=250.798 EndY=84.9886 EndZ=0
    g347: LineSegment StartX=196.001 StartY=169.507 StartZ=0 EndX=49.5522 EndY=254.059 EndZ=0
    g348: LineSegment StartX=52.5522 StartY=259.255 StartZ=0 EndX=199.001 EndY=174.703 EndZ=0
    g349: LineSegment StartX=-41.9063 StartY=-20.7305 StartZ=0 EndX=-188.323 EndY=-105.264 EndZ=0
    g350: LineSegment StartX=-38.9063 StartY=-25.9267 StartZ=0 EndX=-185.323 EndY=-110.461 EndZ=0
    g351: LineSegment StartX=-3 StartY=-46.6572 StartZ=0 EndX=-3 EndY=-201.604 EndZ=0
    g352: LineSegment StartX=3 StartY=-46.6572 StartZ=0 EndX=3 EndY=-201.604 EndZ=0
    g353: LineSegment StartX=38.9063 StartY=-25.9267 StartZ=0 EndX=190.991 EndY=-113.733 EndZ=0
    g354: LineSegment StartX=41.9063 StartY=-20.7305 StartZ=0 EndX=193.991 EndY=-108.536 EndZ=0
    g355: LineSegment StartX=41.9063 StartY=20.7305 StartZ=0 EndX=199.001 EndY=111.429 EndZ=0
    g356: LineSegment StartX=38.9063 StartY=25.9267 StartZ=0 EndX=196.001 EndY=116.625 EndZ=0
    g357: LineSegment StartX=-163.901 StartY=3.93e-14 StartZ=0 EndX=-215.587 EndY=-89.5236 EndZ=0
    g358: LineSegment StartX=-215.587 StartY=-89.5236 StartZ=0 EndX=-244.798 EndY=-72.659 EndZ=0
    g359: LineSegment StartX=-161.303 StartY=-1.5 StartZ=0 EndX=-212.989 EndY=-91.0236 EndZ=0
    g360: LineSegment StartX=-212.989 StartY=-91.0236 StartZ=0 EndX=-188.323 EndY=-105.264 EndZ=0
    g361: LineSegment StartX=-81.9504 StartY=-138.942 StartZ=0 EndX=-185.323 EndY=-138.942 EndZ=0
    g362: LineSegment StartX=-185.323 StartY=-138.942 StartZ=0 EndX=-185.323 EndY=-110.461 EndZ=0
    g363: LineSegment StartX=-81.9504 StartY=-141.942 StartZ=0 EndX=-185.323 EndY=-141.942 EndZ=0
    g364: LineSegment StartX=-185.323 StartY=-141.942 StartZ=0 EndX=-177.599 EndY=-170.404 EndZ=0
    g365: LineSegment StartX=-81.9504 StartY=-141.942 StartZ=0 EndX=-36.3784 EndY=-220.875 EndZ=0
    g366: LineSegment StartX=-36.3784 StartY=-220.875 StartZ=0 EndX=-71.7033 EndY=-241.27 EndZ=0
    g367: LineSegment StartX=-79.3523 StartY=-140.442 StartZ=0 EndX=-33.7803 EndY=-219.375 EndZ=0
    g368: LineSegment StartX=-33.7803 StartY=-219.375 StartZ=0 EndX=-3 EndY=-201.604 EndZ=0
    g369: LineSegment StartX=79.3523 StartY=-140.442 StartZ=0 EndX=33.7803 EndY=-219.375 EndZ=0
    g370: LineSegment StartX=33.7803 StartY=-219.375 StartZ=0 EndX=3 EndY=-201.604 EndZ=0
    g371: LineSegment StartX=81.9504 StartY=-141.942 StartZ=0 EndX=36.3784 EndY=-220.875 EndZ=0
    g372: LineSegment StartX=36.3784 StartY=-220.875 StartZ=0 EndX=71.7033 EndY=-241.27 EndZ=0
    g373: LineSegment StartX=81.9504 StartY=-141.942 StartZ=0 EndX=190.991 EndY=-141.942 EndZ=0
    g374: LineSegment StartX=190.991 StartY=-141.942 StartZ=0 EndX=190.991 EndY=-172.399 EndZ=0
    g375: LineSegment StartX=81.9504 StartY=-138.942 StartZ=0 EndX=190.991 EndY=-138.942 EndZ=0
    g376: LineSegment StartX=190.991 StartY=-138.942 StartZ=0 EndX=190.991 EndY=-113.733 EndZ=0
    g377: LineSegment StartX=81.9504 StartY=138.942 StartZ=0 EndX=196.001 EndY=138.942 EndZ=0
    g378: LineSegment StartX=196.001 StartY=138.942 StartZ=0 EndX=196.001 EndY=116.625 EndZ=0
    g379: LineSegment StartX=81.9504 StartY=141.942 StartZ=0 EndX=196.001 EndY=141.942 EndZ=0
    g380: LineSegment StartX=196.001 StartY=141.942 StartZ=0 EndX=196.001 EndY=169.507 EndZ=0
    g381: LineSegment StartX=161.303 StartY=-1.5 StartZ=0 EndX=215.823 EndY=-95.9317 EndZ=0
    g382: LineSegment StartX=215.823 StartY=-95.9317 StartZ=0 EndX=193.991 EndY=-108.536 EndZ=0
    g383: LineSegment StartX=163.901 StartY=2.9e-15 StartZ=0 EndX=218.421 EndY=-94.4317 EndZ=0
    g384: LineSegment StartX=218.421 StartY=-94.4317 StartZ=0 EndX=244.798 EndY=-79.2031 EndZ=0
    g385: LineSegment StartX=163.901 StartY=2.9e-15 StartZ=0 EndX=220.926 EndY=98.7708 EndZ=0
    g386: LineSegment StartX=220.926 StartY=98.7708 StartZ=0 EndX=244.798 EndY=84.9886 EndZ=0
    g387: LineSegment StartX=161.303 StartY=1.5 StartZ=0 EndX=218.328 EndY=100.271 EndZ=0
    g388: LineSegment StartX=218.328 StartY=100.271 StartZ=0 EndX=199.001 EndY=111.429 EndZ=0
  constraints (1002):
    c: Coincident(g0,g1)
    c: Coincident(g1,g2)
    c: Coincident(g2,g3)
    c: Coincident(g3,g4)
    c: Coincident(g4,g5)
    c: Coincident(g5,g0)
    c: Equal(g0, g1-g5) x5
    c: PointOnObject(g0,g6)
    c: PointOnObject(g1,g6)
    c: PointOnObject(g2,g6)
    c: PointOnObject(g3,g6)
    c: PointOnObject(g4,g6)
    c: PointOnObject(g5,g6)
    c: Coincident(g6,g-1)
    c: Coincident(g7,g8)
    c: Coincident(g8,g9)
    c: Coincident(g9,g10)
    c: Coincident(g10,g11)
    c: Coincident(g11,g12)
    c: Coincident(g12,g13)
    c: Coincident(g13,g14)
    c: Coincident(g14,g15)
    c: Coincident(g15,g16)
    c: Coincident(g16,g17)
    c: Coincident(g17,g18)
    c: Coincident(g18,g7)
    c: Equal(g7,g9)
    c: Equal(g7,g11)
    c: Equal(g7,g13)
    c: Equal(g7,g15)
    c: Equal(g7,g17)
    c: PointOnObject(g7,g19)
    c: PointOnObject(g8,g19)
    c: PointOnObject(g9,g19)
    c: PointOnObject(g10,g19)
    c: PointOnObject(g11,g19)
    c: PointOnObject(g12,g19)
    c: PointOnObject(g13,g19)
    c: PointOnObject(g14,g19)
    c: PointOnObject(g15,g19)
    c: PointOnObject(g16,g19)
    c: PointOnObject(g17,g19)
    c: PointOnObject(g18,g19)
    c: Coincident(g19,g6)
    c: Horizontal(g7)
    c: Horizontal(g0)
    c: Coincident(g20,g8)
    c: Coincident(g20,g0)
    c: Coincident(g21,g20)
    c: Coincident(g21,g8)
    c: Coincident(g22,g0)
    c: Coincident(g22,g18)
    c: Coincident(g23,g22)
    c: Coincident(g23,g18)
    c: Coincident(g24,g16)
    c: Coincident(g24,g4)
    c: Coincident(g25,g16)
    c: Coincident(g25,g24)
    c: Coincident(g26,g14)
    c: Coincident(g26,g3)
    c: Coincident(g27,g26)
    c: Coincident(g27,g14)
    c: Coincident(g28,g12)
    c: Coincident(g28,g2)
    c: Coincident(g29,g12)
    c: Coincident(g29,g28)
    c: Coincident(g30,g10)
    c: Coincident(g30,g1)
    c: Coincident(g31,g10)
    c: Coincident(g31,g30)
    c: Equal(g8,g10)
    c: Equal(g10,g12)
    c: Equal(g12,g14)
    c: Equal(g14,g16)
    c: Equal(g16,g18)
    c: Vertical(g21)
    c: Coincident(g32,g33)
    c: Coincident(g33,g34)
    c: Coincident(g34,g35)
    c: Coincident(g35,g36)
    c: Coincident(g36,g37)
    c: Coincident(g37,g38)
    c: Coincident(g38,g39)
    c: Coincident(g39,g40)
    c: Coincident(g40,g41)
    c: Coincident(g41,g42)
    c: Coincident(g42,g43)
    c: Coincident(g43,g32)
    c: Equal(g32,g34)
    c: Equal(g32,g36)
    c: Equal(g32,g38)
    c: Equal(g32,g40)
    c: Equal(g32,g42)
    c: PointOnObject(g32,g44)
    c: PointOnObject(g33,g44)
    c: PointOnObject(g35,g44)
    c: PointOnObject(g36,g44)
    c: PointOnObject(g37,g44)
    c: PointOnObject(g38,g44)
    c: PointOnObject(g39,g44)
    c: PointOnObject(g40,g44)
    c: PointOnObject(g41,g44)
    c: PointOnObject(g42,g44)
    c: PointOnObject(g43,g44)
    c: Coincident(g44,g6)
    c: Horizontal(g32)
    c: Equal(g33,g35)
    c: Equal(g35,g37)
    c: Equal(g37,g39)
    c: Equal(g39,g41)
    c: Equal(g41,g43)
    c: PointOnObject(g32,g21)
    c: Coincident(g45,g32)
    c: PointOnObject(g45,g33)
    c: Coincident(g46,g33)
    c: PointOnObject(g46,g33)
    c: PointOnObject(g47,g35)
    c: Coincident(g48,g35)
    c: Coincident(g49,g36)
    c: PointOnObject(g49,g37)
    c: Coincident(g50,g37)
    c: PointOnObject(g50,g37)
    c: Coincident(g51,g38)
    c: PointOnObject(g51,g39)
    c: Coincident(g52,g39)
    c: PointOnObject(g52,g39)
    c: Coincident(g53,g40)
    c: Coincident(g54,g41)
    c: Coincident(g55,g42)
    c: PointOnObject(g55,g43)
    c: Coincident(g56,g32)
    c: PointOnObject(g56,g43)
    c: Coincident(g57,g58)
    c: Coincident(g58,g59)
    c: Coincident(g59,g60)
    c: Coincident(g60,g61)
    c: Coincident(g61,g62)
    c: Coincident(g62,g57)
    c: Equal(g57, g58-g62) x5
    c: PointOnObject(g57,g63)
    c: PointOnObject(g58,g63)
    c: PointOnObject(g59,g63)
    c: PointOnObject(g60,g63)
    c: PointOnObject(g61,g63)
    c: PointOnObject(g62,g63)
    c: Coincident(g63,g6)
    c: Horizontal(g57)
    c: Coincident(g64,g65)
    c: Coincident(g65,g66)
    c: Coincident(g66,g64)
    c: Equal(g64,g65)
    c: Equal(g64,g66)
    c: PointOnObject(g64,g67)
    c: PointOnObject(g65,g67)
    c: PointOnObject(g66,g67)
    c: Coincident(g67,g57)
    c: PointOnObject(g66,g57)
    c: Coincident(g68,g69)
    c: Coincident(g69,g70)
    c: Coincident(g70,g68)
    c: Equal(g68,g69)
    c: Equal(g68,g70)
    c: PointOnObject(g68,g71)
    c: PointOnObject(g69,g71)
    c: PointOnObject(g70,g71)
    c: Coincident(g71,g57)
    c: PointOnObject(g70,g57)
    c: Coincident(g72,g73)
    c: Coincident(g73,g74)
    c: Coincident(g74,g72)
    c: Equal(g72,g73)
    c: Equal(g72,g74)
    c: PointOnObject(g72,g75)
    c: PointOnObject(g73,g75)
    c: PointOnObject(g74,g75)
    c: Coincident(g75,g58)
    c: PointOnObject(g74,g58)
    c: Coincident(g76,g77)
    c: Coincident(g77,g78)
    c: Coincident(g78,g76)
    c: Equal(g76,g77)
    c: Equal(g76,g78)
    c: PointOnObject(g76,g79)
    c: PointOnObject(g77,g79)
    c: PointOnObject(g78,g79)
    c: Coincident(g79,g59)
    c: PointOnObject(g78,g59)
    c: Coincident(g80,g81)
    c: Coincident(g81,g82)
    c: Coincident(g82,g80)
    c: Equal(g80,g81)
    c: Equal(g80,g82)
    c: PointOnObject(g80,g83)
    c: PointOnObject(g81,g83)
    c: PointOnObject(g82,g83)
    c: Coincident(g83,g60)
    c: PointOnObject(g82,g60)
    c: Coincident(g84,g85)
    c: Coincident(g85,g86)
    c: Coincident(g86,g84)
    c: Equal(g84,g85)
    c: Equal(g84,g86)
    c: PointOnObject(g84,g87)
    c: PointOnObject(g85,g87)
    c: PointOnObject(g86,g87)
    c: Coincident(g87,g61)
    c: PointOnObject(g86,g61)
    c: Coincident(g88,g46)
    c: Coincident(g88,g69)
    c: Coincident(g89,g68)
    c: Coincident(g89,g45)
    c: Coincident(g90,g47)
    c: Coincident(g90,g72)
    c: Coincident(g91,g48)
    c: Coincident(g91,g73)
    c: Coincident(g92,g49)
    c: Coincident(g92,g76)
    c: Coincident(g93,g50)
    c: Coincident(g93,g77)
    c: Coincident(g94,g51)
    c: Coincident(g94,g80)
    c: Coincident(g95,g52)
    c: Coincident(g95,g81)
    c: Coincident(g96,g53)
    c: Coincident(g96,g84)
    c: Coincident(g97,g54)
    c: Coincident(g97,g85)
    c: Coincident(g98,g55)
    c: Coincident(g98,g64)
    c: Coincident(g99,g56)
    c: Coincident(g99,g64)
    c: PointOnObject(g48,g35)
    c: Perpendicular(g33,g89)
    c: Perpendicular(g33,g88)
    c: Perpendicular(g35,g90)
    c: Perpendicular(g35,g91)
    c: Perpendicular(g37,g92)
    c: Perpendicular(g37,g93)
    c: Perpendicular(g39,g94)
    c: Perpendicular(g39,g95)
    c: Perpendicular(g41,g96)
    c: Perpendicular(g41,g97)
    c: PointOnObject(g54,g41)
    c: Perpendicular(g43,g98)
    c: Perpendicular(g43,g99)
    c: PointOnObject(g53,g41)
    c: PointOnObject(g34,g44)
    c: Coincident(g47,g34)
    c: Equal(g70,g74)
    c: Equal(g74,g78)
    c: Equal(g78,g82)
    c: Equal(g82,g86)
    c: Equal(g86,g64)
    c: Coincident(g100,g101)
    c: Coincident(g101,g102)
    c: Coincident(g102,g103)
    c: Coincident(g103,g104)
    c: Coincident(g104,g105)
    c: Coincident(g105,g100)
    c: Equal(g100, g101-g105) x5
    c: PointOnObject(g100,g106)
    c: PointOnObject(g101,g106)
    c: PointOnObject(g102,g106)
    c: PointOnObject(g103,g106)
    c: PointOnObject(g104,g106)
    c: PointOnObject(g105,g106)
    c: Coincident(g106,g6)
    c: PointOnObject(g100,g-2)
    c: Coincident(g107,g108)
    c: Coincident(g108,g109)
    c: Coincident(g109,g110)
    c: Coincident(g110,g111)
    c: Coincident(g111,g112)
    c: Coincident(g112,g107)
    c: Equal(g107, g108-g112) x5
    c: PointOnObject(g107,g113)
    c: PointOnObject(g108,g113)
    c: PointOnObject(g109,g113)
    c: PointOnObject(g110,g113)
    c: PointOnObject(g111,g113)
    c: PointOnObject(g112,g113)
    c: Coincident(g113,g100)
    c: Coincident(g114,g115)
    c: Coincident(g115,g116)
    c: Coincident(g116,g117)
    c: Coincident(g117,g118)
    c: Coincident(g118,g119)
    c: Coincident(g119,g114)
    c: Equal(g114, g115-g119) x5
    c: PointOnObject(g114,g120)
    c: PointOnObject(g115,g120)
    c: PointOnObject(g116,g120)
    c: PointOnObject(g117,g120)
    c: PointOnObject(g118,g120)
    c: PointOnObject(g119,g120)
    c: Coincident(g120,g100)
    c: Coincident(g121,g122)
    c: Coincident(g122,g123)
    c: Coincident(g123,g124)
    c: Coincident(g124,g125)
    c: Coincident(g125,g126)
    c: Coincident(g126,g121)
    c: Equal(g121, g122-g126) x5
    c: PointOnObject(g121,g127)
    c: PointOnObject(g122,g127)
    c: PointOnObject(g123,g127)
    c: PointOnObject(g124,g127)
    c: PointOnObject(g125,g127)
    c: PointOnObject(g126,g127)
    c: Coincident(g127,g101)
    c: Coincident(g128,g129)
    c: Coincident(g129,g130)
    c: Coincident(g130,g131)
    c: Coincident(g131,g132)
    c: Coincident(g132,g133)
    c: Coincident(g133,g128)
    c: Equal(g128, g129-g133) x5
    c: PointOnObject(g128,g134)
    c: PointOnObject(g129,g134)
    c: PointOnObject(g130,g134)
    c: PointOnObject(g131,g134)
    c: PointOnObject(g132,g134)
    c: PointOnObject(g133,g134)
    c: Coincident(g134,g102)
    c: Coincident(g135,g136)
    c: Coincident(g136,g137)
    c: Coincident(g137,g138)
    c: Coincident(g138,g139)
    c: Coincident(g139,g140)
    c: Coincident(g140,g135)
    c: Equal(g135, g136-g140) x5
    c: PointOnObject(g135,g141)
    c: PointOnObject(g136,g141)
    c: PointOnObject(g137,g141)
    c: PointOnObject(g138,g141)
    c: PointOnObject(g139,g141)
    c: PointOnObject(g140,g141)
    c: Coincident(g141,g103)
    c: Coincident(g142,g143)
    c: Coincident(g143,g144)
    c: Coincident(g144,g145)
    c: Coincident(g145,g146)
    c: Coincident(g146,g147)
    c: Coincident(g147,g142)
    c: Equal(g142, g143-g147) x5
    c: PointOnObject(g142,g148)
    c: PointOnObject(g143,g148)
    c: PointOnObject(g144,g148)
    c: PointOnObject(g145,g148)
    c: PointOnObject(g146,g148)
    c: PointOnObject(g147,g148)
    c: Coincident(g148,g104)
    c: Horizontal(g107)
    c: Horizontal(g114)
    c: Horizontal(g121)
    c: Horizontal(g128)
    c: Horizontal(g135)
    c: Horizontal(g142)
    c: Coincident(g149,g150)
    c: Coincident(g150,g151)
    c: Coincident(g151,g152)
    c: Coincident(g152,g153)
    c: Coincident(g153,g154)
    c: Coincident(g154,g155)
    c: Coincident(g155,g156)
    c: Coincident(g156,g157)
    c: Coincident(g157,g158)
    c: Coincident(g158,g159)
    c: Coincident(g159,g160)
    c: Coincident(g160,g149)
    c: Equal(g149,g151)
    c: Equal(g149,g153)
    c: Equal(g149,g155)
    c: Equal(g149,g157)
    c: Equal(g149,g159)
    c: PointOnObject(g149,g161)
    c: PointOnObject(g150,g161)
    c: PointOnObject(g151,g161)
    c: PointOnObject(g152,g161)
    c: PointOnObject(g153,g161)
    c: PointOnObject(g154,g161)
    c: PointOnObject(g155,g161)
    c: PointOnObject(g156,g161)
    c: PointOnObject(g157,g161)
    c: PointOnObject(g158,g161)
    c: PointOnObject(g159,g161)
    c: PointOnObject(g160,g161)
    c: Coincident(g161,g100)
    c: Coincident(g162,g163)
    c: Coincident(g163,g164)
    c: Coincident(g164,g165)
    c: Coincident(g165,g166)
    c: Coincident(g166,g167)
    c: Coincident(g167,g168)
    c: Coincident(g168,g169)
    c: Coincident(g169,g170)
    c: Coincident(g170,g171)
    c: Coincident(g171,g172)
    c: Coincident(g172,g173)
    c: Coincident(g173,g162)
    c: Equal(g162,g164)
    c: Equal(g162,g166)
    c: Equal(g162,g168)
    c: Equal(g162,g170)
    c: Equal(g162,g172)
    c: PointOnObject(g162,g174)
    c: PointOnObject(g163,g174)
    c: PointOnObject(g164,g174)
    c: PointOnObject(g165,g174)
    c: PointOnObject(g166,g174)
    c: PointOnObject(g167,g174)
    c: PointOnObject(g168,g174)
    c: PointOnObject(g169,g174)
    c: PointOnObject(g170,g174)
    c: PointOnObject(g171,g174)
    c: PointOnObject(g172,g174)
    c: PointOnObject(g173,g174)
    c: Coincident(g174,g100)
    c: Horizontal(g162)
    c: Horizontal(g149)
    c: Equal(g150,g152)
    c: Equal(g152,g154)
    c: Equal(g154,g156)
    c: Equal(g156,g158)
    c: Equal(g158,g160)
    c: Equal(g163,g165)
    c: Equal(g165,g167)
    c: Equal(g167,g169)
    c: Equal(g169,g171)
    c: Equal(g171,g173)
    c: Vertical(g107,g149)
    c: Vertical(g149,g162)
    c: Coincident(g175,g150)
    c: Coincident(g176,g175)
    c: Coincident(g176,g150)
    c: Coincident(g177,g152)
    c: Coincident(g177,g108)
    c: Coincident(g178,g152)
    c: Coincident(g178,g177)
    c: Coincident(g179,g154)
    c: Coincident(g180,g154)
    c: Coincident(g180,g179)
    c: Coincident(g181,g156)
    c: Coincident(g182,g156)
    c: Coincident(g182,g181)
    c: Coincident(g183,g158)
    c: Coincident(g183,g111)
    c: Coincident(g184,g158)
    c: Coincident(g184,g183)
    c: Coincident(g185,g160)
    c: Coincident(g185,g107)
    c: Coincident(g186,g160)
    c: Coincident(g187,g167)
    c: Coincident(g187,g45)
    c: Coincident(g188,g168)
    c: Coincident(g189,g187)
    c: PointOnObject(g189,g167)
    c: Coincident(g190,g189)
    c: Coincident(g190,g89)
    c: Coincident(g191,g188)
    c: PointOnObject(g191,g169)
    c: Coincident(g192,g191)
    c: Coincident(g192,g99)
    c: Coincident(g185,g186)
    c: Coincident(g175,g107)
    c: Coincident(g179,g109)
    c: Coincident(g181,g110)
    c: Perpendicular(g167,g190)
    c: Coincident(g166,g193)
    c: PointOnObject(g193,g167)
    c: Coincident(g193,g194)
    c: Coincident(g194,g68)
    c: Perpendicular(g167,g194)
    c: Coincident(g169,g195)
    c: PointOnObject(g195,g169)
    c: Coincident(g195,g196)
    c: Coincident(g196,g65)
    c: Perpendicular(g169,g192)
    c: Perpendicular(g169,g196)
    c: Coincident(g188,g56)
    c: Coincident(g197,g198)
    c: Coincident(g198,g199)
    c: Coincident(g199,g200)
    c: Coincident(g200,g201)
    c: Coincident(g201,g202)
    c: Coincident(g202,g203)
    c: Coincident(g203,g204)
    c: Coincident(g204,g205)
    c: Coincident(g205,g206)
    c: Coincident(g206,g207)
    c: Coincident(g207,g208)
    c: Coincident(g208,g197)
    c: Equal(g197,g199)
    c: Equal(g197,g201)
    c: Equal(g197,g203)
    c: Equal(g197,g205)
    c: Equal(g197,g207)
    c: PointOnObject(g197,g209)
    c: PointOnObject(g198,g209)
    c: PointOnObject(g199,g209)
    c: PointOnObject(g200,g209)
    c: PointOnObject(g201,g209)
    c: PointOnObject(g202,g209)
    c: PointOnObject(g203,g209)
    c: PointOnObject(g204,g209)
    c: PointOnObject(g205,g209)
    c: PointOnObject(g206,g209)
    c: PointOnObject(g207,g209)
    c: PointOnObject(g208,g209)
    c: Coincident(g209,g100)
    c: Coincident(g210,g211)
    c: Coincident(g211,g212)
    c: Coincident(g212,g213)
    c: Coincident(g213,g214)
    c: Coincident(g214,g215)
    c: Coincident(g215,g216)
    c: Coincident(g216,g217)
    c: Coincident(g217,g218)
    c: Coincident(g218,g219)
    c: Coincident(g219,g220)
    c: Coincident(g220,g221)
    c: Coincident(g221,g210)
    c: Equal(g210,g212)
    c: Equal(g210,g214)
    c: Equal(g210,g216)
    c: Equal(g210,g218)
    c: Equal(g210,g220)
    c: PointOnObject(g210,g222)
    c: PointOnObject(g211,g222)
    c: PointOnObject(g212,g222)
    c: PointOnObject(g213,g222)
    c: PointOnObject(g214,g222)
    c: PointOnObject(g215,g222)
    c: PointOnObject(g216,g222)
    c: PointOnObject(g217,g222)
    c: PointOnObject(g218,g222)
    c: PointOnObject(g219,g222)
    c: PointOnObject(g220,g222)
    c: PointOnObject(g221,g222)
    c: Coincident(g222,g100)
    c: Horizontal(g197)
    c: Horizontal(g210)
    c: Equal(g198,g200)
    c: Equal(g200,g202)
    c: Equal(g202,g204)
    c: Equal(g204,g206)
    c: Equal(g206,g208)
    c: Equal(g211,g213)
    c: Equal(g213,g215)
    c: Equal(g215,g217)
    c: Equal(g217,g219)
    c: Equal(g219,g221)
    c: Vertical(g114,g197)
    c: Vertical(g210,g197)
    c: Coincident(g218,g223)
    c: PointOnObject(g223,g219)
    c: Coincident(g223,g224)
    c: Coincident(g224,g88)
    c: Coincident(g194,g225)
    c: PointOnObject(g225,g219)
    c: Coincident(g225,g226)
    c: Perpendicular(g219,g225)
    c: Perpendicular(g219,g224)
    c: Coincident(g227,g226)
    c: Coincident(g227,g193)
    c: Coincident(g228,g220)
    c: Coincident(g228,g165)
    c: Coincident(g229,g46)
    c: Coincident(g229,g223)
    c: Coincident(g230,g47)
    c: Coincident(g230,g217)
    c: Coincident(g90,g231)
    c: PointOnObject(g231,g217)
    c: Coincident(g231,g232)
    c: Coincident(g232,g230)
    c: Coincident(g72,g233)
    c: PointOnObject(g233,g217)
    c: Coincident(g233,g234)
    c: Coincident(g234,g216)
    c: Perpendicular(g217,g231)
    c: Perpendicular(g217,g233)
    c: Coincident(g226,g219)
    c: Coincident(g235,g236)
    c: Coincident(g236,g237)
    c: Coincident(g237,g238)
    c: Coincident(g238,g239)
    c: Coincident(g239,g240)
    c: Coincident(g240,g241)
    c: Coincident(g241,g242)
    c: Coincident(g242,g243)
    c: Coincident(g243,g244)
    c: Coincident(g244,g245)
    c: Coincident(g245,g246)
    c: Coincident(g246,g235)
    c: Equal(g235,g237)
    c: Equal(g235,g239)
    c: Equal(g235,g241)
    c: Equal(g235,g243)
    c: Equal(g235,g245)
    c: PointOnObject(g235,g247)
    c: PointOnObject(g236,g247)
    c: PointOnObject(g237,g247)
    c: PointOnObject(g238,g247)
    c: PointOnObject(g239,g247)
    c: PointOnObject(g240,g247)
    c: PointOnObject(g241,g247)
    c: PointOnObject(g242,g247)
    c: PointOnObject(g243,g247)
    c: PointOnObject(g244,g247)
    c: PointOnObject(g245,g247)
    c: PointOnObject(g246,g247)
    c: Coincident(g247,g101)
    c: Coincident(g248,g249)
    c: Coincident(g249,g250)
    c: Coincident(g250,g251)
    c: Coincident(g251,g252)
    c: Coincident(g252,g253)
    c: Coincident(g253,g254)
    c: Coincident(g254,g255)
    c: Coincident(g255,g256)
    c: Coincident(g256,g257)
    c: Coincident(g257,g258)
    c: Coincident(g258,g259)
    c: Coincident(g259,g248)
    c: Equal(g248,g250)
    c: Equal(g248,g252)
    c: Equal(g248,g254)
    c: Equal(g248,g256)
    c: Equal(g248,g258)
    c: PointOnObject(g248,g260)
    c: PointOnObject(g249,g260)
    c: PointOnObject(g250,g260)
    c: PointOnObject(g251,g260)
    c: PointOnObject(g252,g260)
    c: PointOnObject(g253,g260)
    c: PointOnObject(g254,g260)
    c: PointOnObject(g255,g260)
    c: PointOnObject(g256,g260)
    c: PointOnObject(g257,g260)
    c: PointOnObject(g258,g260)
    c: PointOnObject(g259,g260)
    c: Coincident(g260,g101)
    c: Coincident(g261,g262)
    c: Coincident(g262,g263)
    c: Coincident(g263,g264)
    c: Coincident(g264,g265)
    c: Coincident(g265,g266)
    c: Coincident(g266,g267)
    c: Coincident(g267,g268)
    c: Coincident(g268,g269)
    c: Coincident(g269,g270)
    c: Coincident(g270,g271)
    c: Coincident(g271,g272)
    c: Coincident(g272,g261)
    c: Equal(g261,g263)
    c: Equal(g261,g265)
    c: Equal(g261,g267)
    c: Equal(g261,g269)
    c: Equal(g261,g271)
    c: PointOnObject(g261,g273)
    c: PointOnObject(g262,g273)
    c: PointOnObject(g263,g273)
    c: PointOnObject(g264,g273)
    c: PointOnObject(g265,g273)
    c: PointOnObject(g266,g273)
    c: PointOnObject(g267,g273)
    c: PointOnObject(g268,g273)
    c: PointOnObject(g269,g273)
    c: PointOnObject(g270,g273)
    c: PointOnObject(g271,g273)
    c: PointOnObject(g272,g273)
    c: Coincident(g273,g102)
    c: Coincident(g274,g275)
    c: Coincident(g275,g276)
    c: Coincident(g276,g277)
    c: Coincident(g277,g278)
    c: Coincident(g278,g279)
    c: Coincident(g279,g280)
    c: Coincident(g280,g281)
    c: Coincident(g281,g282)
    c: Coincident(g282,g283)
    c: Coincident(g283,g284)
    c: Coincident(g284,g285)
    c: Coincident(g285,g274)
    c: Equal(g274,g276)
    c: Equal(g274,g278)
    c: Equal(g274,g280)
    c: Equal(g274,g282)
    c: Equal(g274,g284)
    c: PointOnObject(g274,g286)
    c: PointOnObject(g275,g286)
    c: PointOnObject(g276,g286)
    c: PointOnObject(g277,g286)
    c: PointOnObject(g278,g286)
    c: PointOnObject(g279,g286)
    c: PointOnObject(g280,g286)
    c: PointOnObject(g281,g286)
    c: PointOnObject(g282,g286)
    c: PointOnObject(g283,g286)
    c: PointOnObject(g284,g286)
    c: PointOnObject(g285,g286)
    c: Coincident(g286,g102)
    c: Coincident(g287,g288)
    c: Coincident(g288,g289)
    c: Coincident(g289,g290)
    c: Coincident(g290,g291)
    c: Coincident(g291,g292)
    c: Coincident(g292,g293)
    c: Coincident(g293,g294)
    c: Coincident(g294,g295)
    c: Coincident(g295,g296)
    c: Coincident(g296,g297)
    c: Coincident(g297,g298)
    c: Coincident(g298,g287)
    c: Equal(g287,g289)
    c: Equal(g287,g291)
    c: Equal(g287,g293)
    c: Equal(g287,g295)
    c: Equal(g287,g297)
    c: PointOnObject(g287,g299)
    c: PointOnObject(g288,g299)
    c: PointOnObject(g289,g299)
    c: PointOnObject(g290,g299)
    c: PointOnObject(g291,g299)
    c: PointOnObject(g292,g299)
    c: PointOnObject(g293,g299)
    c: PointOnObject(g294,g299)
    c: PointOnObject(g295,g299)
    c: PointOnObject(g296,g299)
    c: PointOnObject(g297,g299)
    c: PointOnObject(g298,g299)
    c: Coincident(g299,g103)
    c: Coincident(g300,g301)
    c: Coincident(g301,g302)
    c: Coincident(g302,g303)
    c: Coincident(g303,g304)
    c: Coincident(g304,g305)
    c: Coincident(g305,g306)
    c: Coincident(g306,g307)
    c: Coincident(g307,g308)
    c: Coincident(g308,g309)
    c: Coincident(g309,g310)
    c: Coincident(g310,g311)
    c: Coincident(g311,g300)
    c: Equal(g300,g302)
    c: Equal(g300,g304)
    c: Equal(g300,g306)
    c: Equal(g300,g308)
    c: Equal(g300,g310)
    c: PointOnObject(g300,g312)
    c: PointOnObject(g301,g312)
    c: PointOnObject(g302,g312)
    c: PointOnObject(g303,g312)
    c: PointOnObject(g304,g312)
    c: PointOnObject(g305,g312)
    c: PointOnObject(g306,g312)
    c: PointOnObject(g307,g312)
    c: PointOnObject(g308,g312)
    c: PointOnObject(g309,g312)
    c: PointOnObject(g310,g312)
    c: PointOnObject(g311,g312)
    c: Coincident(g312,g103)
    c: Coincident(g313,g314)
    c: Coincident(g314,g315)
    c: Coincident(g315,g316)
    c: Coincident(g316,g317)
    c: Coincident(g317,g318)
    c: Coincident(g318,g319)
    c: Coincident(g319,g320)
    c: Coincident(g320,g321)
    c: Coincident(g321,g322)
    c: Coincident(g322,g323)
    c: Coincident(g323,g324)
    c: Coincident(g324,g313)
    c: Equal(g313,g315)
    c: Equal(g313,g317)
    c: Equal(g313,g319)
    c: Equal(g313,g321)
    c: Equal(g313,g323)
    c: PointOnObject(g313,g325)
    c: PointOnObject(g314,g325)
    c: PointOnObject(g315,g325)
    c: PointOnObject(g316,g325)
    c: PointOnObject(g317,g325)
    c: PointOnObject(g318,g325)
    c: PointOnObject(g319,g325)
    c: PointOnObject(g320,g325)
    c: PointOnObject(g321,g325)
    c: PointOnObject(g322,g325)
    c: PointOnObject(g323,g325)
    c: PointOnObject(g324,g325)
    c: Coincident(g325,g104)
    c: Coincident(g326,g327)
    c: Coincident(g327,g328)
    c: Coincident(g328,g329)
    c: Coincident(g329,g330)
    c: Coincident(g330,g331)
    c: Coincident(g331,g332)
    c: Coincident(g332,g333)
    c: Coincident(g333,g334)
    c: Coincident(g334,g335)
    c: Coincident(g335,g336)
    c: Coincident(g336,g337)
    c: Coincident(g337,g326)
    c: Equal(g326,g328)
    c: Equal(g326,g330)
    c: Equal(g326,g332)
    c: Equal(g326,g334)
    c: Equal(g326,g336)
    c: PointOnObject(g326,g338)
    c: PointOnObject(g327,g338)
    c: PointOnObject(g328,g338)
    c: PointOnObject(g329,g338)
    c: PointOnObject(g330,g338)
    c: PointOnObject(g331,g338)
    c: PointOnObject(g332,g338)
    c: PointOnObject(g333,g338)
    c: PointOnObject(g334,g338)
    c: PointOnObject(g335,g338)
    c: PointOnObject(g336,g338)
    c: PointOnObject(g337,g338)
    c: Coincident(g338,g104)
    c: Horizontal(g248)
    c: Horizontal(g235)
    c: Horizontal(g261)
    c: Horizontal(g274)
    c: Horizontal(g287)
    c: Horizontal(g300)
    c: Horizontal(g313)
    c: Horizontal(g326)
    c: Equal(g236,g238)
    c: Equal(g238,g240)
    c: Equal(g240,g242)
    c: Equal(g242,g244)
    c: Equal(g244,g246)
    c: Equal(g249,g251)
    c: Equal(g251,g253)
    c: Equal(g253,g255)
    c: Equal(g255,g257)
    c: Equal(g257,g259)
    c: Vertical(g121,g235)
    c: Vertical(g235,g248)
    c: Equal(g262,g264)
    c: Equal(g264,g266)
    c: Equal(g266,g268)
    c: Equal(g268,g270)
    c: Equal(g270,g272)
    c: Equal(g275,g277)
    c: Equal(g277,g279)
    c: Equal(g279,g281)
    c: Equal(g281,g283)
    c: Equal(g283,g285)
    c: Vertical(g128,g261)
    c: Vertical(g261,g274)
    c: Equal(g288,g290)
    c: Equal(g290,g292)
    c: Equal(g292,g294)
    c: Equal(g294,g296)
    c: Equal(g296,g298)
    c: Equal(g301,g303)
    c: Equal(g303,g305)
    c: Equal(g305,g307)
    c: Equal(g307,g309)
    c: Equal(g309,g311)
    c: Vertical(g135,g287)
    c: Vertical(g287,g300)
    c: Equal(g314,g316)
    c: Equal(g316,g318)
    c: Equal(g318,g320)
    c: Equal(g320,g322)
    c: Equal(g322,g324)
    c: Equal(g327,g329)
    c: Equal(g329,g331)
    c: Equal(g331,g333)
    c: Equal(g333,g335)
    c: Equal(g335,g337)
    c: Vertical(g142,g313)
    c: Vertical(g313,g326)
    c: Coincident(g339,g234)
    c: Coincident(g339,g248)
    c: Coincident(g340,g215)
    c: Coincident(g340,g248)
    c: Coincident(g341,g256)
    c: Coincident(g341,g275)
    c: Coincident(g342,g255)
    c: Coincident(g342,g276)
    c: Coincident(g343,g284)
    c: Coincident(g343,g303)
    c: Coincident(g344,g283)
    c: Coincident(g344,g304)
    c: Coincident(g345,g300)
    c: Coincident(g345,g331)
    c: Coincident(g346,g300)
    c: Coincident(g347,g328)
    c: Coincident(g347,g195)
    c: Coincident(g348,g170)
    c: Coincident(g348,g327)
    c: Coincident(g349,g48)
    c: Coincident(g349,g258)
    c: Coincident(g350,g49)
    c: Coincident(g350,g257)
    c: Coincident(g351,g50)
    c: Coincident(g352,g51)
    c: Coincident(g352,g274)
    c: Coincident(g353,g52)
    c: Coincident(g353,g302)
    c: Coincident(g354,g53)
    c: Coincident(g354,g301)
    c: Coincident(g355,g54)
    c: Coincident(g355,g330)
    c: Coincident(g356,g55)
    c: Coincident(g356,g329)
    c: Coincident(g233,g357)
    c: PointOnObject(g357,g259)
    c: Coincident(g357,g358)
    c: Coincident(g358,g339)
    c: Coincident(g91,g359)
    c: PointOnObject(g359,g259)
    c: Coincident(g359,g360)
    c: Coincident(g360,g349)
    c: Coincident(g92,g361)
    c: PointOnObject(g361,g257)
    c: Coincident(g361,g362)
    c: Coincident(g76,g363)
    c: PointOnObject(g363,g257)
    c: Coincident(g363,g364)
    c: Perpendicular(g257,g361)
    c: Perpendicular(g257,g363)
    c: Coincident(g363,g365)
    c: Coincident(g365,g366)
    c: Coincident(g366,g341)
    c: PointOnObject(g365,g275)
    c: Coincident(g93,g367)
    c: PointOnObject(g367,g275)
    c: Coincident(g367,g368)
    c: Coincident(g368,g351)
    c: Perpendicular(g275,g365)
    c: Perpendicular(g275,g367)
    c: Coincident(g94,g369)
    c: PointOnObject(g369,g285)
    c: Coincident(g369,g370)
    c: Coincident(g370,g352)
    c: Coincident(g80,g371)
    c: PointOnObject(g371,g285)
    c: Coincident(g371,g372)
    c: Coincident(g372,g343)
    c: Coincident(g371,g373)
    c: PointOnObject(g373,g303)
    c: Coincident(g373,g374)
    c: Coincident(g95,g375)
    c: PointOnObject(g375,g303)
    c: Coincident(g375,g376)
    c: Coincident(g376,g353)
    c: Perpendicular(g285,g369)
    c: Perpendicular(g285,g371)
    c: Perpendicular(g303,g373)
    c: Coincident(g374,g343)
    c: Perpendicular(g303,g375)
    c: Coincident(g351,g274)
    c: Coincident(g362,g350)
    c: Perpendicular(g259,g357)
    c: Perpendicular(g259,g359)
    c: Parallel(g187,g188)
    c: Parallel(g229,g230)
    c: Parallel(g349,g350)
    c: Parallel(g351,g352)
    c: Parallel(g353,g354)
    c: Parallel(g355,g356)
    c: Coincident(g346,g332)
    c: Coincident(g377,g378)
    c: Coincident(g379,g380)
    c: Coincident(g381,g382)
    c: Coincident(g383,g384)
    c: Coincident(g385,g386)
    c: Coincident(g387,g388)
    c: Coincident(g381,g96)
    c: Coincident(g383,g84)
    c: Coincident(g385,g383)
    c: Coincident(g387,g97)
    c: Coincident(g382,g354)
    c: Coincident(g384,g345)
    c: PointOnObject(g381,g301)
    c: PointOnObject(g383,g301)
    c: Perpendicular(g301,g381)
    c: Perpendicular(g301,g383)
    c: Coincident(g388,g355)
    c: Coincident(g386,g345)
    c: PointOnObject(g387,g331)
    c: PointOnObject(g385,g331)
    c: Perpendicular(g331,g385)
    c: Perpendicular(g331,g387)
    c: Coincident(g377,g98)
    c: Coincident(g379,g196)
    c: Coincident(g378,g356)
    c: Coincident(g380,g347)
    c: PointOnObject(g377,g329)
    c: PointOnObject(g379,g329)
    c: Perpendicular(g329,g377)
    c: Perpendicular(g329,g379)
    c: Distance(g46,g45) = 3
    c: Distance(g45,g56) = 6
    c: Distance(g45,g8) = 9
FEATURE [Sketcher::SketchObject] Sketch075  label="Sketch KumikoSakura"
  FullyConstrained = true
  MapMode = 5
  Support = -> [XY_Plane034]
  sketch-geometry (130):
    g0: LineSegment StartX=3 StartY=5.19615 StartZ=0 EndX=-3 EndY=5.19615 EndZ=0
    g1: LineSegment StartX=-3 StartY=5.19615 StartZ=0 EndX=-6 EndY=0 EndZ=0
    g2: LineSegment StartX=-6 StartY=0 StartZ=0 EndX=-3 EndY=-5.19615 EndZ=0
    g3: LineSegment StartX=-3 StartY=-5.19615 StartZ=0 EndX=3 EndY=-5.19615 EndZ=0
    g4: LineSegment StartX=3 StartY=-5.19615 StartZ=0 EndX=6 EndY=0 EndZ=0
    g5: LineSegment StartX=6 StartY=-3e-16 StartZ=0 EndX=3 EndY=5.19615 EndZ=0
    g6: Circle CenterX=0 CenterY=0 CenterZ=0 NormalX=0 NormalY=0 NormalZ=1 AngleXU=0 Radius=6
    g7: LineSegment StartX=3 StartY=12.6491 StartZ=0 EndX=-3 EndY=12.6491 EndZ=0
    g8: LineSegment StartX=-3 StartY=12.6491 StartZ=0 EndX=-9.45445 EndY=8.92263 EndZ=0
    g9: LineSegment StartX=-9.45445 StartY=8.92263 StartZ=0 EndX=-12.4545 EndY=3.72648 EndZ=0
    g10: LineSegment StartX=-12.4545 StartY=3.72648 StartZ=0 EndX=-12.4545 EndY=-3.72648 EndZ=0
    g11: LineSegment StartX=-12.4545 StartY=-3.72648 StartZ=0 EndX=-9.45445 EndY=-8.92263 EndZ=0
    g12: LineSegment StartX=-9.45445 StartY=-8.92263 StartZ=0 EndX=-3 EndY=-12.6491 EndZ=0
    g13: LineSegment StartX=-3 StartY=-12.6491 StartZ=0 EndX=3 EndY=-12.6491 EndZ=0
    g14: LineSegment StartX=3 StartY=-12.6491 StartZ=0 EndX=9.45445 EndY=-8.92263 EndZ=0
    g15: LineSegment StartX=9.45445 StartY=-8.92263 StartZ=0 EndX=12.4545 EndY=-3.72648 EndZ=0
    g16: LineSegment StartX=12.4545 StartY=-3.72648 StartZ=0 EndX=12.4545 EndY=3.72648 EndZ=0
    g17: LineSegment StartX=12.4545 StartY=3.72648 StartZ=0 EndX=9.45445 EndY=8.92263 EndZ=0
    g18: LineSegment StartX=9.45445 StartY=8.92263 StartZ=0 EndX=3 EndY=12.6491 EndZ=0
    g19: Circle CenterX=0 CenterY=0 CenterZ=0 NormalX=0 NormalY=0 NormalZ=1 AngleXU=0 Radius=13
    g20: LineSegment StartX=-9.45445 StartY=8.92263 StartZ=0 EndX=-3 EndY=5.19615 EndZ=0
    g21: LineSegment StartX=-3 StartY=12.6491 StartZ=0 EndX=-3 EndY=5.19615 EndZ=0
    g22: LineSegment StartX=-12.4545 StartY=3.72648 StartZ=0 EndX=-6 EndY=0 EndZ=0
    g23: LineSegment StartX=-12.4545 StartY=-3.72648 StartZ=0 EndX=-6 EndY=0 EndZ=0
    g24: LineSegment StartX=-9.45445 StartY=-8.92263 StartZ=0 EndX=-3 EndY=-5.19615 EndZ=0
    g25: LineSegment StartX=-3 StartY=-5.19615 StartZ=0 EndX=-3 EndY=-12.6491 EndZ=0
    g26: LineSegment StartX=3 StartY=-5.19615 StartZ=0 EndX=3 EndY=-12.6491 EndZ=0
    g27: LineSegment StartX=3 StartY=-5.19615 StartZ=0 EndX=9.45445 EndY=-8.92263 EndZ=0
    g28: LineSegment StartX=6 StartY=-3e-16 StartZ=0 EndX=12.4545 EndY=-3.72648 EndZ=0
    g29: LineSegment StartX=6 StartY=-3e-16 StartZ=0 EndX=12.4545 EndY=3.72648 EndZ=0
    g30: LineSegment StartX=3 StartY=5.19615 StartZ=0 EndX=9.45445 EndY=8.92263 EndZ=0
    g31: LineSegment StartX=3 StartY=12.6491 StartZ=0 EndX=3 EndY=5.19615 EndZ=0
    g32: LineSegment StartX=25 StartY=43.3013 StartZ=0 EndX=-25 EndY=43.3013 EndZ=0
    g33: LineSegment StartX=-25 StartY=43.3013 StartZ=0 EndX=-50 EndY=0 EndZ=0
    g34: LineSegment StartX=-50 StartY=-3e-16 StartZ=0 EndX=-25 EndY=-43.3013 EndZ=0
    g35: LineSegment StartX=-25 StartY=-43.3013 StartZ=0 EndX=25 EndY=-43.3013 EndZ=0
    g36: LineSegment StartX=25 StartY=-43.3013 StartZ=0 EndX=50 EndY=7.1e-15 EndZ=0
    g37: LineSegment StartX=50 StartY=9.3e-15 StartZ=0 EndX=25 EndY=43.3013 EndZ=0
    g38: Circle CenterX=0 CenterY=0 CenterZ=0 NormalX=0 NormalY=0 NormalZ=1 AngleXU=0 Radius=50
    g39: LineSegment StartX=-22.6906 StartY=43.3013 StartZ=0 EndX=-26.1547 EndY=45.3013 EndZ=0
    g40: LineSegment StartX=-26.1547 StartY=45.3013 StartZ=0 EndX=-26.1547 EndY=41.3013 EndZ=0
    g41: LineSegment StartX=-26.1547 StartY=41.3013 StartZ=0 EndX=-22.6906 EndY=43.3013 EndZ=0
    g42: Circle CenterX=-25 CenterY=43.3013 CenterZ=0 NormalX=0 NormalY=0 NormalZ=1 AngleXU=0 Radius=2.3094
    g43: LineSegment StartX=-48.8453 StartY=2 StartZ=0 EndX=-52.3094 EndY=2.4e-15 EndZ=0
    g44: LineSegment StartX=-52.3094 StartY=2.4e-15 StartZ=0 EndX=-48.8453 EndY=-2 EndZ=0
    g45: LineSegment StartX=-48.8453 StartY=-2 StartZ=0 EndX=-48.8453 EndY=2 EndZ=0
    g46: Circle CenterX=-50 CenterY=-3e-16 CenterZ=0 NormalX=0 NormalY=0 NormalZ=1 AngleXU=0 Radius=2.3094
    g47: LineSegment StartX=-26.1547 StartY=-41.3013 StartZ=0 EndX=-26.1547 EndY=-45.3013 EndZ=0
    g48: LineSegment StartX=-26.1547 StartY=-45.3013 StartZ=0 EndX=-22.6906 EndY=-43.3013 EndZ=0
    g49: LineSegment StartX=-22.6906 StartY=-43.3013 StartZ=0 EndX=-26.1547 EndY=-41.3013 EndZ=0
    g50: Circle CenterX=-25 CenterY=-43.3013 CenterZ=0 NormalX=0 NormalY=0 NormalZ=1 AngleXU=0 Radius=2.3094
    g51: LineSegment StartX=22.6906 StartY=-43.3013 StartZ=0 EndX=26.1547 EndY=-45.3013 EndZ=0
    g52: LineSegment StartX=26.1547 StartY=-45.3013 StartZ=0 EndX=26.1547 EndY=-41.3013 EndZ=0
    g53: LineSegment StartX=26.1547 StartY=-41.3013 StartZ=0 EndX=22.6906 EndY=-43.3013 EndZ=0
    g54: Circle CenterX=25 CenterY=-43.3013 CenterZ=0 NormalX=0 NormalY=0 NormalZ=1 AngleXU=0 Radius=2.3094
    g55: LineSegment StartX=48.8453 StartY=-2 StartZ=0 EndX=52.3094 EndY=1.51e-14 EndZ=0
    g56: LineSegment StartX=52.3094 StartY=1.53e-14 StartZ=0 EndX=48.8453 EndY=2 EndZ=0
    g57: LineSegment StartX=48.8453 StartY=2 StartZ=0 EndX=48.8453 EndY=-2 EndZ=0
    g58: Circle CenterX=50 CenterY=9.3e-15 CenterZ=0 NormalX=0 NormalY=0 NormalZ=1 AngleXU=0 Radius=2.3094
    g59: LineSegment StartX=26.1547 StartY=41.3013 StartZ=0 EndX=26.1547 EndY=45.3013 EndZ=0
    g60: LineSegment StartX=26.1547 StartY=45.3013 StartZ=0 EndX=22.6906 EndY=43.3013 EndZ=0
    g61: LineSegment StartX=22.6906 StartY=43.3013 StartZ=0 EndX=26.1547 EndY=41.3013 EndZ=0
    g62: Circle CenterX=25 CenterY=43.3013 CenterZ=0 NormalX=0 NormalY=0 NormalZ=1 AngleXU=0 Radius=2.3094
    g63: LineSegment StartX=3 StartY=20.7846 StartZ=0 EndX=-3 EndY=20.7846 EndZ=0
    g64: LineSegment StartX=-3 StartY=20.7846 StartZ=0 EndX=-16.5 EndY=12.9904 EndZ=0
    g65: LineSegment StartX=-16.5 StartY=12.9904 StartZ=0 EndX=-19.5 EndY=7.79423 EndZ=0
    g66: LineSegment StartX=-19.5 StartY=7.79423 StartZ=0 EndX=-19.5 EndY=-7.79423 EndZ=0
    g67: LineSegment StartX=-19.5 StartY=-7.79423 StartZ=0 EndX=-16.5 EndY=-12.9904 EndZ=0
    g68: LineSegment StartX=-16.5 StartY=-12.9904 StartZ=0 EndX=-3 EndY=-20.7846 EndZ=0
    g69: LineSegment StartX=-3 StartY=-20.7846 StartZ=0 EndX=3 EndY=-20.7846 EndZ=0
    g70: LineSegment StartX=3 StartY=-20.7846 StartZ=0 EndX=16.5 EndY=-12.9904 EndZ=0
    g71: LineSegment StartX=16.5 StartY=-12.9904 StartZ=0 EndX=19.5 EndY=-7.79423 EndZ=0
    g72: LineSegment StartX=19.5 StartY=-7.79423 StartZ=0 EndX=19.5 EndY=7.79423 EndZ=0
    g73: LineSegment StartX=19.5 StartY=7.79423 StartZ=0 EndX=16.5 EndY=12.9904 EndZ=0
    g74: LineSegment StartX=16.5 StartY=12.9904 StartZ=0 EndX=3 EndY=20.7846 EndZ=0
    g75: Circle CenterX=0 CenterY=0 CenterZ=0 NormalX=0 NormalY=0 NormalZ=1 AngleXU=0 Radius=21
    g76: LineSegment StartX=-3 StartY=43.3013 StartZ=0 EndX=-3 EndY=20.7846 EndZ=0
    g77: LineSegment StartX=3 StartY=43.3013 StartZ=0 EndX=3 EndY=20.7846 EndZ=0
    g78: LineSegment StartX=-39 StartY=19.0526 StartZ=0 EndX=-19.5 EndY=7.79423 EndZ=0
    g79: LineSegment StartX=-36 StartY=24.2487 StartZ=0 EndX=-16.5 EndY=12.9904 EndZ=0
    g80: LineSegment StartX=-36 StartY=-24.2487 StartZ=0 EndX=-16.5 EndY=-12.9904 EndZ=0
    g81: LineSegment StartX=-39 StartY=-19.0526 StartZ=0 EndX=-19.5 EndY=-7.79423 EndZ=0
    g82: LineSegment StartX=3 StartY=-43.3013 StartZ=0 EndX=3 EndY=-20.7846 EndZ=0
    g83: LineSegment StartX=-3 StartY=-43.3013 StartZ=0 EndX=-3 EndY=-20.7846 EndZ=0
    g84: LineSegment StartX=39 StartY=-19.0526 StartZ=0 EndX=19.5 EndY=-7.79423 EndZ=0
    g85: LineSegment StartX=36 StartY=-24.2487 StartZ=0 EndX=16.5 EndY=-12.9904 EndZ=0
    g86: LineSegment StartX=39 StartY=19.0526 StartZ=0 EndX=19.5 EndY=7.79423 EndZ=0
    g87: LineSegment StartX=16.5 StartY=12.9904 StartZ=0 EndX=36 EndY=24.2487 EndZ=0
    g88: LineSegment StartX=-26.1547 StartY=41.3013 StartZ=0 EndX=-11.4821 EndY=15.8875 EndZ=0
    g89: LineSegment StartX=-11.4821 StartY=15.8875 StartZ=0 EndX=-16.5 EndY=12.9904 EndZ=0
    g90: LineSegment StartX=-22.6906 StartY=43.3013 StartZ=0 EndX=-8.01795 EndY=17.8875 EndZ=0
    g91: LineSegment StartX=-8.01795 StartY=17.8875 StartZ=0 EndX=-3 EndY=20.7846 EndZ=0
    g92: LineSegment StartX=-48.8453 StartY=-2 StartZ=0 EndX=-19.5 EndY=-2 EndZ=0
    g93: LineSegment StartX=-19.5 StartY=-2 StartZ=0 EndX=-19.5 EndY=-7.79423 EndZ=0
    g94: LineSegment StartX=-48.8453 StartY=2 StartZ=0 EndX=-19.5 EndY=2 EndZ=0
    g95: LineSegment StartX=-19.5 StartY=2 StartZ=0 EndX=-19.5 EndY=7.79423 EndZ=0
    g96: LineSegment StartX=-22.6906 StartY=-43.3013 StartZ=0 EndX=-8.01795 EndY=-17.8875 EndZ=0
    g97: LineSegment StartX=-8.01795 StartY=-17.8875 StartZ=0 EndX=-3 EndY=-20.7846 EndZ=0
    g98: LineSegment StartX=-26.1547 StartY=-41.3013 StartZ=0 EndX=-11.4821 EndY=-15.8875 EndZ=0
    g99: LineSegment StartX=-11.4821 StartY=-15.8875 StartZ=0 EndX=-16.5 EndY=-12.9904 EndZ=0
    g100: LineSegment StartX=26.1547 StartY=-41.3013 StartZ=0 EndX=11.4821 EndY=-15.8875 EndZ=0
    g101: LineSegment StartX=11.4821 StartY=-15.8875 StartZ=0 EndX=16.5 EndY=-12.9904 EndZ=0
    g102: LineSegment StartX=22.6906 StartY=-43.3013 StartZ=0 EndX=8.01795 EndY=-17.8875 EndZ=0
    g103: LineSegment StartX=8.01795 StartY=-17.8875 StartZ=0 EndX=3 EndY=-20.7846 EndZ=0
    g104: LineSegment StartX=48.8453 StartY=2 StartZ=0 EndX=19.5 EndY=2 EndZ=0
    g105: LineSegment StartX=19.5 StartY=2 StartZ=0 EndX=19.5 EndY=7.79423 EndZ=0
    g106: LineSegment StartX=48.8453 StartY=-2 StartZ=0 EndX=19.5 EndY=-2 EndZ=0
    g107: LineSegment StartX=19.5 StartY=-2 StartZ=0 EndX=19.5 EndY=-7.79423 EndZ=0
    g108: LineSegment StartX=22.6906 StartY=43.3013 StartZ=0 EndX=8.01795 EndY=17.8875 EndZ=0
    g109: LineSegment StartX=8.01795 StartY=17.8875 StartZ=0 EndX=3 EndY=20.7846 EndZ=0
    g110: LineSegment StartX=26.1547 StartY=41.3013 StartZ=0 EndX=11.4821 EndY=15.8875 EndZ=0
    g111: LineSegment StartX=11.4821 StartY=15.8875 StartZ=0 EndX=16.5 EndY=12.9904 EndZ=0
    g112: LineSegment StartX=-25 StartY=43.3013 StartZ=0 EndX=-26.1547 EndY=41.3013 EndZ=0
    g113: LineSegment StartX=-25 StartY=43.3013 StartZ=0 EndX=-22.6906 EndY=43.3013 EndZ=0
    g114: LineSegment StartX=-50 StartY=-3e-16 StartZ=0 EndX=-48.8453 EndY=2 EndZ=0
    g115: LineSegment StartX=-50 StartY=-3e-16 StartZ=0 EndX=-48.8453 EndY=-2 EndZ=0
    g116: LineSegment StartX=-25 StartY=-43.3013 StartZ=0 EndX=-26.1547 EndY=-41.3013 EndZ=0
    g117: LineSegment StartX=-25 StartY=-43.3013 StartZ=0 EndX=-22.6906 EndY=-43.3013 EndZ=0
    g118: LineSegment StartX=25 StartY=-43.3013 StartZ=0 EndX=22.6906 EndY=-43.3013 EndZ=0
    g119: LineSegment StartX=25 StartY=-43.3013 StartZ=0 EndX=26.1547 EndY=-41.3013 EndZ=0
    g120: LineSegment StartX=50 StartY=9.3e-15 StartZ=0 EndX=48.8453 EndY=-2 EndZ=0
    g121: LineSegment StartX=50 StartY=9.3e-15 StartZ=0 EndX=48.8453 EndY=2 EndZ=0
    g122: LineSegment StartX=25 StartY=43.3013 StartZ=0 EndX=26.1547 EndY=41.3013 EndZ=0
    g123: LineSegment StartX=25 StartY=43.3013 StartZ=0 EndX=22.6906 EndY=43.3013 EndZ=0
    g124: LineSegment StartX=-3 StartY=43.3013 StartZ=0 EndX=3 EndY=43.3013 EndZ=0
    g125: LineSegment StartX=-36 StartY=24.2487 StartZ=0 EndX=-39 EndY=19.0526 EndZ=0
    g126: LineSegment StartX=-39 StartY=-19.0526 StartZ=0 EndX=-36 EndY=-24.2487 EndZ=0
    g127: LineSegment StartX=-3 StartY=-43.3013 StartZ=0 EndX=3 EndY=-43.3013 EndZ=0
    g128: LineSegment StartX=36 StartY=-24.2487 StartZ=0 EndX=39 EndY=-19.0526 EndZ=0
    g129: LineSegment StartX=39 StartY=19.0526 StartZ=0 EndX=36 EndY=24.2487 EndZ=0
  constraints (331):
    c: Coincident(g0,g1)
    c: Coincident(g1,g2)
    c: Coincident(g2,g3)
    c: Coincident(g3,g4)
    c: Coincident(g4,g5)
    c: Coincident(g5,g0)
    c: Equal(g0, g1-g5) x5
    c: PointOnObject(g0,g6)
    c: PointOnObject(g1,g6)
    c: PointOnObject(g2,g6)
    c: PointOnObject(g3,g6)
    c: PointOnObject(g4,g6)
    c: PointOnObject(g5,g6)
    c: Coincident(g7,g8)
    c: Coincident(g8,g9)
    c: Coincident(g9,g10)
    c: Coincident(g10,g11)
    c: Coincident(g11,g12)
    c: Coincident(g12,g13)
    c: Coincident(g13,g14)
    c: Coincident(g14,g15)
    c: Coincident(g15,g16)
    c: Coincident(g16,g17)
    c: Coincident(g17,g18)
    c: Coincident(g18,g7)
    c: Equal(g7,g9)
    c: Equal(g7,g11)
    c: Equal(g7,g13)
    c: Equal(g7,g15)
    c: Equal(g7,g17)
    c: PointOnObject(g7,g19)
    c: PointOnObject(g8,g19)
    c: PointOnObject(g9,g19)
    c: PointOnObject(g10,g19)
    c: PointOnObject(g11,g19)
    c: PointOnObject(g12,g19)
    c: PointOnObject(g13,g19)
    c: PointOnObject(g14,g19)
    c: PointOnObject(g15,g19)
    c: PointOnObject(g16,g19)
    c: PointOnObject(g17,g19)
    c: PointOnObject(g18,g19)
    c: Coincident(g21,g0)
    c: Coincident(g20,g21)
    c: Coincident(g21,g8)
    c: Coincident(g20,g8)
    c: Coincident(g22,g1)
    c: Coincident(g23,g22)
    c: Coincident(g22,g10)
    c: Coincident(g23,g10)
    c: Coincident(g24,g2)
    c: Coincident(g25,g24)
    c: Coincident(g24,g12)
    c: Coincident(g25,g12)
    c: Coincident(g26,g3)
    c: Coincident(g27,g26)
    c: Coincident(g26,g14)
    c: Coincident(g27,g14)
    c: Coincident(g28,g4)
    c: Coincident(g29,g28)
    c: Coincident(g28,g16)
    c: Coincident(g29,g16)
    c: Coincident(g30,g0)
    c: Coincident(g31,g30)
    c: Coincident(g30,g18)
    c: Coincident(g31,g18)
    c: Coincident(g32,g33)
    c: Coincident(g33,g34)
    c: Coincident(g34,g35)
    c: Coincident(g35,g36)
    c: Coincident(g36,g37)
    c: Coincident(g37,g32)
    c: Equal(g32, g33-g37) x5
    c: PointOnObject(g32,g38)
    c: PointOnObject(g33,g38)
    c: PointOnObject(g34,g38)
    c: PointOnObject(g35,g38)
    c: PointOnObject(g36,g38)
    c: PointOnObject(g37,g38)
    c: Coincident(g39,g40)
    c: Coincident(g40,g41)
    c: Coincident(g41,g39)
    c: Equal(g39,g40)
    c: Equal(g39,g41)
    c: PointOnObject(g39,g42)
    c: PointOnObject(g40,g42)
    c: PointOnObject(g41,g42)
    c: Coincident(g42,g32)
    c: PointOnObject(g41,g32)
    c: Coincident(g43,g44)
    c: Coincident(g44,g45)
    c: Coincident(g45,g43)
    c: Equal(g43,g44)
    c: Equal(g43,g45)
    c: PointOnObject(g43,g46)
    c: PointOnObject(g44,g46)
    c: PointOnObject(g45,g46)
    c: Coincident(g46,g33)
    c: PointOnObject(g45,g33)
    c: Coincident(g47,g48)
    c: Coincident(g48,g49)
    c: Coincident(g49,g47)
    c: Equal(g47,g48)
    c: Equal(g47,g49)
    c: PointOnObject(g47,g50)
    c: PointOnObject(g48,g50)
    c: PointOnObject(g49,g50)
    c: Coincident(g50,g34)
    c: PointOnObject(g49,g34)
    c: Coincident(g51,g52)
    c: Coincident(g52,g53)
    c: Coincident(g53,g51)
    c: Equal(g51,g52)
    c: Equal(g51,g53)
    c: PointOnObject(g51,g54)
    c: PointOnObject(g52,g54)
    c: PointOnObject(g53,g54)
    c: Coincident(g54,g35)
    c: PointOnObject(g53,g35)
    c: Coincident(g55,g56)
    c: Coincident(g56,g57)
    c: Coincident(g57,g55)
    c: Equal(g55,g56)
    c: Equal(g55,g57)
    c: PointOnObject(g55,g58)
    c: PointOnObject(g56,g58)
    c: PointOnObject(g57,g58)
    c: Coincident(g58,g36)
    c: PointOnObject(g57,g36)
    c: Coincident(g59,g60)
    c: Coincident(g60,g61)
    c: Coincident(g61,g59)
    c: Equal(g59,g60)
    c: Equal(g59,g61)
    c: PointOnObject(g59,g62)
    c: PointOnObject(g60,g62)
    c: PointOnObject(g61,g62)
    c: Coincident(g62,g32)
    c: PointOnObject(g61,g37)
    c: Equal(g8,g21)
    c: Equal(g21,g20)
    c: Coincident(g63,g64)
    c: Coincident(g64,g65)
    c: Coincident(g65,g66)
    c: Coincident(g66,g67)
    c: Coincident(g67,g68)
    c: Coincident(g68,g69)
    c: Coincident(g69,g70)
    c: Coincident(g70,g71)
    c: Coincident(g71,g72)
    c: Coincident(g72,g73)
    c: Coincident(g73,g74)
    c: Coincident(g74,g63)
    c: Equal(g63,g65)
    c: Equal(g63,g67)
    c: Equal(g63,g69)
    c: Equal(g63,g71)
    c: Equal(g63,g73)
    c: PointOnObject(g63,g75)
    c: PointOnObject(g64,g75)
    c: PointOnObject(g65,g75)
    c: PointOnObject(g66,g75)
    c: PointOnObject(g67,g75)
    c: PointOnObject(g68,g75)
    c: PointOnObject(g69,g75)
    c: PointOnObject(g70,g75)
    c: PointOnObject(g71,g75)
    c: PointOnObject(g72,g75)
    c: PointOnObject(g73,g75)
    c: PointOnObject(g74,g75)
    c: Coincident(g75,g6)
    c: Equal(g8,g10)
    c: Equal(g10,g12)
    c: Equal(g12,g14)
    c: Equal(g14,g16)
    c: Equal(g16,g18)
    c: Equal(g64,g66)
    c: Equal(g66,g68)
    c: Equal(g68,g70)
    c: Equal(g70,g72)
    c: Equal(g72,g74)
    c: PointOnObject(g63,g21)
    c: PointOnObject(g63,g31)
    c: PointOnObject(g76,g32)
    c: PointOnObject(g77,g32)
    c: Coincident(g76,g63)
    c: Coincident(g77,g63)
    c: PointOnObject(g79,g33)
    c: PointOnObject(g78,g33)
    c: Coincident(g78,g65)
    c: Coincident(g79,g64)
    c: PointOnObject(g81,g34)
    c: PointOnObject(g80,g34)
    c: Coincident(g81,g66)
    c: Coincident(g80,g67)
    c: PointOnObject(g83,g35)
    c: Coincident(g83,g68)
    c: PointOnObject(g82,g35)
    c: Coincident(g82,g69)
    c: PointOnObject(g85,g36)
    c: Coincident(g85,g70)
    c: PointOnObject(g84,g36)
    c: Coincident(g84,g71)
    c: PointOnObject(g86,g37)
    c: Coincident(g86,g72)
    c: PointOnObject(g87,g37)
    c: Coincident(g87,g73)
    c: PointOnObject(g76,g21)
    c: Perpendicular(g76,g32)
    c: Perpendicular(g32,g77)
    c: Perpendicular(g33,g79)
    c: Perpendicular(g33,g78)
    c: Perpendicular(g34,g81)
    c: Perpendicular(g34,g80)
    c: Perpendicular(g35,g83)
    c: Perpendicular(g35,g82)
    c: Perpendicular(g36,g85)
    c: Perpendicular(g36,g84)
    c: Perpendicular(g37,g86)
    c: Perpendicular(g37,g87)
    c: Coincident(g88,g89)
    c: Coincident(g90,g91)
    c: Coincident(g92,g93)
    c: Coincident(g94,g95)
    c: Coincident(g96,g97)
    c: Coincident(g98,g99)
    c: Coincident(g100,g101)
    c: Coincident(g102,g103)
    c: Coincident(g104,g105)
    c: Coincident(g106,g107)
    c: Coincident(g108,g109)
    c: Coincident(g110,g111)
    c: Coincident(g90,g39)
    c: Coincident(g88,g40)
    c: Coincident(g94,g43)
    c: Coincident(g92,g44)
    c: Coincident(g98,g47)
    c: Coincident(g96,g48)
    c: Coincident(g102,g51)
    c: Coincident(g100,g52)
    c: Coincident(g106,g55)
    c: Coincident(g104,g56)
    c: Coincident(g110,g59)
    c: Coincident(g108,g60)
    c: Coincident(g89,g79)
    c: Coincident(g91,g76)
    c: Coincident(g95,g78)
    c: Coincident(g93,g81)
    c: Coincident(g99,g80)
    c: Coincident(g97,g83)
    c: Coincident(g103,g82)
    c: Coincident(g101,g85)
    c: Coincident(g107,g84)
    c: Coincident(g105,g86)
    c: Coincident(g111,g87)
    c: Coincident(g109,g77)
    c: PointOnObject(g90,g64)
    c: PointOnObject(g88,g64)
    c: PointOnObject(g94,g66)
    c: PointOnObject(g92,g66)
    c: PointOnObject(g98,g68)
    c: PointOnObject(g96,g68)
    c: PointOnObject(g102,g70)
    c: PointOnObject(g100,g70)
    c: PointOnObject(g106,g72)
    c: PointOnObject(g104,g72)
    c: PointOnObject(g110,g74)
    c: PointOnObject(g108,g74)
    c: Perpendicular(g64,g88)
    c: Perpendicular(g64,g90)
    c: Perpendicular(g66,g94)
    c: Perpendicular(g66,g92)
    c: Perpendicular(g68,g98)
    c: Perpendicular(g68,g96)
    c: Perpendicular(g70,g102)
    c: Perpendicular(g70,g100)
    c: Perpendicular(g72,g106)
    c: Perpendicular(g72,g104)
    c: Perpendicular(g74,g110)
    c: Perpendicular(g74,g108)
    c: Equal(g42,g46)
    c: Equal(g46,g50)
    c: Equal(g50,g54)
    c: Equal(g54,g58)
    c: Equal(g58,g62)
    c: Coincident(g113,g90)
    c: Coincident(g112,g88)
    c: Coincident(g113,g32)
    c: Coincident(g112,g113)
    c: Coincident(g115,g92)
    c: Coincident(g115,g33)
    c: Coincident(g114,g94)
    c: Coincident(g114,g115)
    c: Coincident(g116,g98)
    c: Coincident(g116,g34)
    c: Coincident(g117,g96)
    c: Coincident(g117,g116)
    c: Coincident(g119,g100)
    c: Coincident(g119,g35)
    c: Coincident(g118,g102)
    c: Coincident(g118,g119)
    c: Coincident(g120,g106)
    c: Coincident(g120,g36)
    c: Coincident(g121,g104)
    c: Coincident(g121,g120)
    c: Coincident(g122,g110)
    c: Coincident(g122,g32)
    c: Coincident(g123,g108)
    c: Coincident(g123,g122)
    c: Coincident(g124,g76)
    c: Coincident(g124,g77)
    c: Coincident(g125,g78)
    c: Coincident(g125,g79)
    c: Coincident(g126,g80)
    c: Coincident(g126,g81)
    c: Coincident(g127,g82)
    c: Coincident(g127,g83)
    c: Coincident(g128,g84)
    c: Coincident(g128,g85)
    c: Coincident(g129,g87)
    c: Coincident(g129,g86)
    c: Horizontal(g0)
    c: Diameter(g6) = 12
    c: Diameter(g19) = 26
    c: Diameter(g75) = 42
    c: Diameter(g38) = 100
    c: Distance(g88,g90) = 4
    c: Coincident(g38,g6)
    c: Coincident(g19,g6)
    c: DistanceX(g6) = 0
    c: DistanceY(g6) = 0
FEATURE [PartDesign::Pad] Pad020  label="Pad KumikoSakura Center"
  Direction = (0,0,1)
  Length = 20
  Length2 = 10
  Profile = -> Sketch075
  ReferenceAxis = -> Sketch075 [N_Axis]
  Type = 0
FEATURE [PartDesign::Line] DatumLine003  label="DatumLine X1"
  AttacherType = Attacher::AttachEngineLine
  AttachmentOffset = pos=(50,0,0) rot=(0,0,1;0rad)
  Length = 20
  MapMode = 18
  Placement = pos=(50,0,0) rot=(0,0,1;0rad)
  ResizeMode = 0
  Support = -> [XY_Plane034]
FEATURE [Sketcher::SketchObject] Sketch076
  FullyConstrained = true
  MapMode = 5
  Support = -> [XY_Plane035]
  expr: Constraints[9] = <<Variables>>.GantorySpacing - 10
  sketch-geometry (4):
    g0: LineSegment StartX=15 StartY=95 StartZ=0 EndX=165 EndY=95 EndZ=0
    g1: LineSegment StartX=165 StartY=95 StartZ=0 EndX=165 EndY=-95 EndZ=0
    g2: LineSegment StartX=165 StartY=-95 StartZ=0 EndX=15 EndY=-95 EndZ=0
    g3: LineSegment StartX=15 StartY=-95 StartZ=0 EndX=15 EndY=95 EndZ=0
  constraints (10):
    c: Coincident(g0,g1)
    c: Coincident(g1,g2)
    c: Coincident(g2,g3)
    c: Coincident(g3,g0)
    c: Symmetric(g0,g2,g-1)
    c: Symmetric(g0,g1,g-1)
    c: DistanceX(g0) = 15
    c: Horizontal(g0)
    c: DistanceX(g0) = 165
    c: DistanceY(g1,g1) = 190
FEATURE [PartDesign::Pad] Pad021
  Direction = (0,0,1)
  Length = 7
  Length2 = 10
  Profile = -> Sketch076
  ReferenceAxis = -> Sketch076 [N_Axis]
  Reversed = true
  Type = 0
  expr: Length = <<Variables>>.WallThickness
FEATURE [Sketcher::SketchObject] Sketch077
  FullyConstrained = true
  MapMode = 5
  Support = -> [XY_Plane015]
  expr: Constraints[21] = <<Variables>>.GantorySpacing + Variables.WallThickness * 2 + 16 - 40 - 20
  sketch-geometry (12):
    g0: LineSegment StartX=26 StartY=85 StartZ=0 EndX=154 EndY=85 EndZ=0
    g1: LineSegment StartX=160 StartY=79 StartZ=0 EndX=160 EndY=-79 EndZ=0
    g2: LineSegment StartX=154 StartY=-85 StartZ=0 EndX=26 EndY=-85 EndZ=0
    g3: LineSegment StartX=20 StartY=-79 StartZ=0 EndX=20 EndY=79 EndZ=0
    g4: ArcOfCircle CenterX=26 CenterY=79 CenterZ=0 NormalX=0 NormalY=0 NormalZ=1 AngleXU=0 Radius=6 StartAngle=1.5708 EndAngle=3.14159
    g5: GeomPoint X=20 Y=85 Z=0
    g6: ArcOfCircle CenterX=26 CenterY=-79 CenterZ=0 NormalX=0 NormalY=0 NormalZ=1 AngleXU=0 Radius=6 StartAngle=3.14159 EndAngle=4.71239
    g7: GeomPoint X=20 Y=-85 Z=0
    g8: ArcOfCircle CenterX=154 CenterY=-79 CenterZ=0 NormalX=0 NormalY=0 NormalZ=1 AngleXU=0 Radius=6 StartAngle=4.71239 EndAngle=6.28319
    g9: GeomPoint X=160 Y=-85 Z=0
    g10: ArcOfCircle CenterX=154 CenterY=79 CenterZ=0 NormalX=0 NormalY=0 NormalZ=1 AngleXU=0 Radius=6 StartAngle=-9e-16 EndAngle=1.5708
    g11: GeomPoint X=160 Y=85 Z=0
  constraints (26):
    c: DistanceX(g7,g9) = 140
    c: PointOnObject(g5,g0)
    c: PointOnObject(g5,g3)
    c: Tangent(g0,g4) = 1.5708
    c: Tangent(g3,g4) = 1.5708
    c: PointOnObject(g7,g3)
    c: PointOnObject(g7,g2)
    c: Tangent(g3,g6) = 1.5708
    c: Tangent(g2,g6) = 1.5708
    c: PointOnObject(g9,g1)
    c: PointOnObject(g9,g2)
    c: Tangent(g1,g8) = 1.5708
    c: Tangent(g2,g8) = 1.5708
    c: PointOnObject(g11,g0)
    c: PointOnObject(g11,g1)
    c: Tangent(g0,g10) = 1.5708
    c: Tangent(g1,g10) = 1.5708
    c: Equal(g4,g6)
    c: Equal(g4,g8)
    c: Equal(g4,g10)
    c: Radius(g4) = 6
    c: DistanceY(g7,g5) = 170
    c: Symmetric(g7,g5,g-1)
    c: Symmetric(g11,g9,g-1)
    c: Horizontal(g0)
    c: DistanceX(g7) = 20
FEATURE [PartDesign::Line] DatumLine  label="DatumLine X2"
  AttacherType = Attacher::AttachEngineLine
  AttachmentOffset = pos=(100,0,0) rot=(0,0,1;0rad)
  Length = 20
  MapMode = 18
  Placement = pos=(100,0,0) rot=(0,0,1;0rad)
  ResizeMode = 0
  Support = -> [XY_Plane034]
FEATURE [PartDesign::Line] DatumLine006  label="DatumLine X3"
  AttacherType = Attacher::AttachEngineLine
  AttachmentOffset = pos=(200,0,0) rot=(0,0,1;0rad)
  Length = 20
  MapMode = 18
  Placement = pos=(200,0,0) rot=(0,0,1;0rad)
  ResizeMode = 0
  Support = -> [XY_Plane034]
FEATURE [PartDesign::Line] DatumLine008  label="DatumLine X4"
  AttacherType = Attacher::AttachEngineLine
  AttachmentOffset = pos=(-50,0,0) rot=(0,0,1;0rad)
  Length = 20
  MapMode = 18
  Placement = pos=(-50,0,0) rot=(0,0,1;0rad)
  ResizeMode = 0
  Support = -> [XY_Plane034]
FEATURE [PartDesign::PolarPattern] PolarPattern004
  Angle = 360
  Axis = -> DatumLine003
  Occurrences = 3
FEATURE [PartDesign::PolarPattern] PolarPattern005
  Angle = 360
  Axis = -> DatumLine
  Occurrences = 3
FEATURE [PartDesign::PolarPattern] PolarPattern007
  Angle = 360
  Axis = -> Sketch075 [N_Axis]
  Occurrences = 6
FEATURE [PartDesign::MultiTransform] MultiTransform
  BaseFeature = -> Pad020
  Originals = -> [Pad020]
  Refine = true
  Transformations = -> [PolarPattern004,PolarPattern005,PolarPattern007]
FEATURE [PartDesign::Body] Body018  label="KumikoSakura"
  Group = -> [Sketch075,Pad020,DatumLine003,DatumLine,DatumLine006,DatumLine008,MultiTransform,PolarPattern004,PolarPattern005,PolarPattern007]
  Origin = -> Origin034
  Tip = -> MultiTransform
FEATURE [App::Part] Part014  label="Kumiko"
  Group = -> [Body018,Sketch073,Sketch074]
  Origin = -> Origin033
FEATURE [Part::FeaturePython] Clone045  label="KumikoSakura001"  # Draft clone (typed FeaturePython)
  AttacherType = Attacher::AttachEngine3D
  Fuse = false
  Objects = -> [Body018]
  Placement = pos=(90,0,-7) rot=(0,0,1;1.5708rad)
  Scale = (0.66,0.66,1)
  expr: .Placement.Base.z = -<<Variables>>.WallThickness
FEATURE [PartDesign::Boolean] Boolean001
  BaseFeature = -> Pad021
  Group = -> [Clone045]
  Type = 2
FEATURE [PartDesign::Body] Body019  label="RightPanelKumikoSakura"
  Group = -> [Sketch076,Pad021,Boolean001]
  Origin = -> Origin035
  Tip = -> Boolean001
FEATURE [PartDesign::AdditivePrism] Prism019
  AttacherType = Attacher::AttachEngine3D
  Circumradius = 3.35
  FirstAngle = 0
  Height = 20
  MapMode = 5
  Polygon = 6
  SecondAngle = 0
  Support = -> [XY_Plane036]
FEATURE [PartDesign::Body] Body020  label="M3 inserted Nut L20"
  Group = -> [Prism019]
  Origin = -> Origin036
  Tip = -> Prism019
FEATURE [Sketcher::SketchObject] Sketch078
  FullyConstrained = true
  MapMode = 5
  Support = -> [XY_Plane006]
  sketch-geometry (24):
    g0: LineSegment StartX=-3 StartY=16 StartZ=0 EndX=3 EndY=16 EndZ=0
    g1: LineSegment StartX=5 StartY=14 StartZ=0 EndX=5 EndY=12 EndZ=0
    g2: LineSegment StartX=3 StartY=10 StartZ=0 EndX=-3 EndY=10 EndZ=0
    g3: LineSegment StartX=-5 StartY=12 StartZ=0 EndX=-5 EndY=14 EndZ=0
    g4: LineSegment StartX=-3 StartY=-10 StartZ=0 EndX=3 EndY=-10 EndZ=0
    g5: LineSegment StartX=5 StartY=-12 StartZ=0 EndX=5 EndY=-14 EndZ=0
    g6: LineSegment StartX=3 StartY=-16 StartZ=0 EndX=-3 EndY=-16 EndZ=0
    g7: LineSegment StartX=-5 StartY=-14 StartZ=0 EndX=-5 EndY=-12 EndZ=0
    g8: ArcOfCircle CenterX=-3 CenterY=14 CenterZ=0 NormalX=0 NormalY=0 NormalZ=1 AngleXU=0 Radius=2 StartAngle=1.5708 EndAngle=3.14159
    g9: GeomPoint X=-5 Y=16 Z=0
    g10: ArcOfCircle CenterX=-3 CenterY=12 CenterZ=0 NormalX=0 NormalY=0 NormalZ=1 AngleXU=0 Radius=2 StartAngle=3.14159 EndAngle=4.71239
    g11: GeomPoint X=-5 Y=10 Z=0
    g12: ArcOfCircle CenterX=3 CenterY=12 CenterZ=0 NormalX=0 NormalY=0 NormalZ=1 AngleXU=0 Radius=2 StartAngle=4.71239 EndAngle=6.28319
    g13: GeomPoint X=5 Y=10 Z=0
    g14: ArcOfCircle CenterX=3 CenterY=14 CenterZ=0 NormalX=0 NormalY=0 NormalZ=1 AngleXU=0 Radius=2 StartAngle=0 EndAngle=1.5708
    g15: GeomPoint X=5 Y=16 Z=0
    g16: ArcOfCircle CenterX=-3 CenterY=-12 CenterZ=0 NormalX=0 NormalY=0 NormalZ=1 AngleXU=0 Radius=2 StartAngle=1.5708 EndAngle=3.14159
    g17: GeomPoint X=-5 Y=-10 Z=0
    g18: ArcOfCircle CenterX=-3 CenterY=-14 CenterZ=0 NormalX=0 NormalY=0 NormalZ=1 AngleXU=0 Radius=2 StartAngle=3.14159 EndAngle=4.71239
    g19: GeomPoint X=-5 Y=-16 Z=0
    g20: ArcOfCircle CenterX=3 CenterY=-14 CenterZ=0 NormalX=0 NormalY=0 NormalZ=1 AngleXU=0 Radius=2 StartAngle=4.71239 EndAngle=6.28319
    g21: GeomPoint X=5 Y=-16 Z=0
    g22: ArcOfCircle CenterX=3 CenterY=-12 CenterZ=0 NormalX=0 NormalY=0 NormalZ=1 AngleXU=0 Radius=2 StartAngle=0 EndAngle=1.5708
    g23: GeomPoint X=5 Y=-10 Z=0
  constraints (50):
    c: Vertical(g3)
    c: Symmetric(g9,g15,g-2)
    c: Symmetric(g11,g13,g-2)
    c: Symmetric(g17,g11,g-1)
    c: Symmetric(g9,g19,g-1)
    c: Symmetric(g13,g23,g-1)
    c: Symmetric(g15,g21,g-1)
    c: DistanceY(g19,g9) = 32
    c: DistanceX(g9,g15) = 10
    c: DistanceY(g11,g9) = 6
    c: PointOnObject(g9,g0)
    c: PointOnObject(g9,g3)
    c: Tangent(g0,g8) = 1.5708
    c: Tangent(g3,g8) = 1.5708
    c: PointOnObject(g11,g3)
    c: PointOnObject(g11,g2)
    c: Tangent(g3,g10) = 1.5708
    c: Tangent(g2,g10) = 1.5708
    c: PointOnObject(g13,g2)
    c: PointOnObject(g13,g1)
    c: Tangent(g2,g12) = 1.5708
    c: Tangent(g1,g12) = 1.5708
    c: PointOnObject(g15,g1)
    c: PointOnObject(g15,g0)
    c: Tangent(g1,g14) = 1.5708
    c: Tangent(g0,g14) = 1.5708
    c: PointOnObject(g17,g4)
    c: PointOnObject(g17,g7)
    c: Tangent(g4,g16) = 1.5708
    c: Tangent(g7,g16) = 1.5708
    c: PointOnObject(g19,g7)
    c: PointOnObject(g19,g6)
    c: Tangent(g7,g18) = 1.5708
    c: Tangent(g6,g18) = 1.5708
    c: PointOnObject(g21,g6)
    c: PointOnObject(g21,g5)
    c: Tangent(g6,g20) = 1.5708
    c: Tangent(g5,g20) = 1.5708
    c: PointOnObject(g23,g5)
    c: PointOnObject(g23,g4)
    c: Tangent(g5,g22) = 1.5708
    c: Tangent(g4,g22) = 1.5708
    c: Equal(g8,g10)
    c: Equal(g8,g12)
    c: Equal(g8,g14)
    c: Equal(g8,g16)
    c: Equal(g8,g18)
    c: Equal(g8,g20)
    c: Equal(g8,g22)
    c: Radius(g8) = 2
FEATURE [Sketcher::SketchObject] Sketch079
  FullyConstrained = true
  MapMode = 5
  Support = -> [XY_Plane006]
  sketch-geometry (12):
    g0: LineSegment StartX=11.5 StartY=5 StartZ=0 EndX=14 EndY=5 EndZ=0
    g1: LineSegment StartX=16 StartY=3 StartZ=0 EndX=16 EndY=-3 EndZ=0
    g2: LineSegment StartX=14 StartY=-5 StartZ=0 EndX=11.5 EndY=-5 EndZ=0
    g3: LineSegment StartX=9.5 StartY=-3 StartZ=0 EndX=9.5 EndY=3 EndZ=0
    g4: ArcOfCircle CenterX=11.5 CenterY=3 CenterZ=0 NormalX=0 NormalY=0 NormalZ=1 AngleXU=0 Radius=2 StartAngle=1.5708 EndAngle=3.14159
    g5: GeomPoint X=9.5 Y=5 Z=0
    g6: ArcOfCircle CenterX=11.5 CenterY=-3 CenterZ=0 NormalX=0 NormalY=0 NormalZ=1 AngleXU=0 Radius=2 StartAngle=3.14159 EndAngle=4.71239
    g7: GeomPoint X=9.5 Y=-5 Z=0
    g8: ArcOfCircle CenterX=14 CenterY=-3 CenterZ=0 NormalX=0 NormalY=0 NormalZ=1 AngleXU=0 Radius=2 StartAngle=4.71239 EndAngle=6.28319
    g9: GeomPoint X=16 Y=-5 Z=0
    g10: ArcOfCircle CenterX=14 CenterY=3 CenterZ=0 NormalX=0 NormalY=0 NormalZ=1 AngleXU=0 Radius=2 StartAngle=0 EndAngle=1.5708
    g11: GeomPoint X=16 Y=5 Z=0
  constraints (26):
    c: Horizontal(g0)
    c: Symmetric(g5,g7,g-1)
    c: Symmetric(g11,g9,g-1)
    c: DistanceY(g7,g5) = 10
    c: DistanceX(g5,g11) = 6.5
    c: PointOnObject(g5,g0)
    c: PointOnObject(g5,g3)
    c: Tangent(g0,g4) = 1.5708
    c: Tangent(g3,g4) = 1.5708
    c: PointOnObject(g7,g3)
    c: PointOnObject(g7,g2)
    c: Tangent(g3,g6) = 1.5708
    c: Tangent(g2,g6) = 1.5708
    c: PointOnObject(g9,g2)
    c: PointOnObject(g9,g1)
    c: Tangent(g2,g8) = 1.5708
    c: Tangent(g1,g8) = 1.5708
    c: PointOnObject(g11,g1)
    c: PointOnObject(g11,g0)
    c: Tangent(g1,g10) = 1.5708
    c: Tangent(g0,g10) = 1.5708
    c: DistanceX(g-1,g5) = 9.5
    c: Equal(g4,g10)
    c: Equal(g4,g6)
    c: Equal(g4,g8)
    c: Radius(g4) = 2
FEATURE [PartDesign::Pad] Pad023
  BaseFeature = -> Chamfer
  Direction = (0,0,1)
  Length = 16.5
  Length2 = 10
  Profile = -> Sketch079
  ReferenceAxis = -> Sketch079 [N_Axis]
  Type = 0
FEATURE [Sketcher::SketchObject] Sketch080
  FullyConstrained = true
  MapMode = 5
  Placement = pos=(0,0,0) rot=(0.57735,0.57735,0.57735;2.0944rad)
  Support = -> [YZ_Plane006]
  sketch-geometry (15):
    g0: LineSegment StartX=-17 StartY=26 StartZ=0 EndX=-15 EndY=28 EndZ=0
    g1: LineSegment StartX=-11 StartY=28 StartZ=0 EndX=-9 EndY=26 EndZ=0
    g2: LineSegment StartX=-9 StartY=26 StartZ=0 EndX=-7 EndY=26 EndZ=0
    g3: LineSegment StartX=-7 StartY=26 StartZ=0 EndX=-5 EndY=28 EndZ=0
    g4: LineSegment StartX=-5 StartY=28 StartZ=0 EndX=5 EndY=28 EndZ=0
    g5: LineSegment StartX=5 StartY=28 StartZ=0 EndX=7 EndY=26 EndZ=0
    g6: LineSegment StartX=7 StartY=26 StartZ=0 EndX=9 EndY=26 EndZ=0
    g7: LineSegment StartX=9 StartY=26 StartZ=0 EndX=11 EndY=28 EndZ=0
    g8: LineSegment StartX=11 StartY=28 StartZ=0 EndX=15 EndY=28 EndZ=0
    g9: LineSegment StartX=15 StartY=28 StartZ=0 EndX=17 EndY=26 EndZ=0
    g10: LineSegment StartX=17 StartY=26 StartZ=0 EndX=17 EndY=32 EndZ=0
    g11: LineSegment StartX=17 StartY=32 StartZ=0 EndX=-17 EndY=32 EndZ=0
    g12: LineSegment StartX=-17 StartY=32 StartZ=0 EndX=-17 EndY=26 EndZ=0
    g13: LineSegment StartX=-15 StartY=28 StartZ=0 EndX=-13 EndY=28 EndZ=0
    g14: LineSegment StartX=-13 StartY=28 StartZ=0 EndX=-11 EndY=28 EndZ=0
  constraints (37):
    c: Coincident(g0,g13)
    c: Coincident(g14,g1)
    c: Coincident(g1,g2)
    c: Coincident(g2,g3)
    c: Coincident(g3,g4)
    c: Coincident(g4,g5)
    c: Coincident(g5,g6)
    c: Coincident(g6,g7)
    c: Coincident(g7,g8)
    c: Coincident(g8,g9)
    c: Coincident(g9,g10)
    c: Coincident(g10,g11)
    c: Coincident(g11,g12)
    c: Coincident(g12,g0)
    c: Vertical(g12)
    c: Symmetric(g11,g10,g-2)
    c: Symmetric(g0,g9,g-2)
    c: Symmetric(g0,g8,g-2)
    c: Angle(g0) = 0.785398
    c: Symmetric(g14,g7,g-2)
    c: Angle(g1) = -0.785398
    c: Symmetric(g1,g6,g-2)
    c: Horizontal(g2)
    c: Horizontal(g0,g1)
    c: Symmetric(g2,g5,g-2)
    c: Angle(g3) = 0.785398
    c: Symmetric(g3,g4,g-2)
    c: Coincident(g13,g14)
    c: Horizontal(g13)
    c: Symmetric(g0,g1,g13)
    c: DistanceX(g13,g-1) = 13
    c: Horizontal(g1,g3)
    c: DistanceY(g13) = 28
    c: DistanceX(g8,g8) = 4
    c: DistanceY(g0,g0) = 2
    c: DistanceX(g4,g4) = 10
    c: DistanceY(g12,g12) = 6
FEATURE [PartDesign::Pocket] Pocket026
  BaseFeature = -> Pad023
  Direction = (-1,2e-16,-3e-16)
  Length = 5
  Length2 = 5
  Midplane = true
  Profile = -> Sketch080
  ReferenceAxis = -> Sketch080 [N_Axis]
  Type = 1
FEATURE [PartDesign::Hole] Hole001
  BaseFeature = -> Pocket026
  CustomThreadClearance = 0
  Depth = 148.549
  DepthType = 1
  Diameter = 2.5
  DrillForDepth = false
  DrillPoint = 1
  DrillPointAngle = 118
  HoleCutCountersinkAngle = 90
  HoleCutCustomValues = false
  HoleCutDepth = 0
  HoleCutDiameter = 6.1
  HoleCutType = 0
  ModelThread = false
  Profile = -> Sketch006
  Reversed = true
  Tapered = false
  TaperedAngle = 90
  ThreadClass = 0
  ThreadDepth = 148.549
  ThreadDepthType = 0
  ThreadDirection = 0
  ThreadFit = 0
  ThreadSize = 9
  ThreadType = 1
  Threaded = true
  UseCustomThreadClearance = false
FEATURE [PartDesign::Hole] Hole003
  BaseFeature = -> Hole001
  CustomThreadClearance = 0
  Depth = 148.549
  DepthType = 1
  Diameter = 2.5
  DrillForDepth = false
  DrillPoint = 1
  DrillPointAngle = 118
  HoleCutCountersinkAngle = 90
  HoleCutCustomValues = false
  HoleCutDepth = 2.8
  HoleCutDiameter = 6
  HoleCutType = 0
  ModelThread = false
  Profile = -> Sketch010
  Reversed = true
  Tapered = false
  TaperedAngle = 90
  ThreadClass = 0
  ThreadDepth = 148.549
  ThreadDepthType = 0
  ThreadDirection = 0
  ThreadFit = 0
  ThreadSize = 9
  ThreadType = 1
  Threaded = true
  UseCustomThreadClearance = false
FEATURE [PartDesign::ShapeBinder] ShapeBinder002
  Support = -> [Sketch]
  TraceSupport = false
FEATURE [PartDesign::Pad] Pad024
  Direction = (0,0,1)
  Length = 7
  Length2 = 10
  Profile = -> ShapeBinder002
  Type = 0
FEATURE [PartDesign::Chamfer] Chamfer008
  Angle = 45
  Base = -> Pad024 [Face16]
  BaseFeature = -> Pad024
  ChamferType = 0
  FlipDirection = false
  Size = 1
  Size2 = 1
  SupportTransform = false
  UseAllEdges = false
FEATURE [Sketcher::SketchObject] Sketch081
  FullyConstrained = true
  MapMode = 5
  Support = -> [XY_Plane007]
  sketch-geometry (12):
    g0: LineSegment StartX=-1.25 StartY=5 StartZ=0 EndX=1.25 EndY=5 EndZ=0
    g1: LineSegment StartX=3.25 StartY=3 StartZ=0 EndX=3.25 EndY=-3 EndZ=0
    g2: LineSegment StartX=1.25 StartY=-5 StartZ=0 EndX=-1.25 EndY=-5 EndZ=0
    g3: LineSegment StartX=-3.25 StartY=-3 StartZ=0 EndX=-3.25 EndY=3 EndZ=0
    g4: ArcOfCircle CenterX=-1.25 CenterY=3 CenterZ=0 NormalX=0 NormalY=0 NormalZ=1 AngleXU=0 Radius=2 StartAngle=1.5708 EndAngle=3.14159
    g5: GeomPoint X=-3.25 Y=5 Z=0
    g6: ArcOfCircle CenterX=-1.25 CenterY=-3 CenterZ=0 NormalX=0 NormalY=0 NormalZ=1 AngleXU=0 Radius=2 StartAngle=3.14159 EndAngle=4.71239
    g7: GeomPoint X=-3.25 Y=-5 Z=0
    g8: ArcOfCircle CenterX=1.25 CenterY=-3 CenterZ=0 NormalX=0 NormalY=0 NormalZ=1 AngleXU=0 Radius=2 StartAngle=4.71239 EndAngle=6.28319
    g9: GeomPoint X=3.25 Y=-5 Z=0
    g10: ArcOfCircle CenterX=1.25 CenterY=3 CenterZ=0 NormalX=0 NormalY=0 NormalZ=1 AngleXU=0 Radius=2 StartAngle=0 EndAngle=1.5708
    g11: GeomPoint X=3.25 Y=5 Z=0
  constraints (25):
    c: Symmetric(g5,g11,g-2)
    c: Symmetric(g5,g7,g-1)
    c: Symmetric(g11,g9,g-1)
    c: DistanceX(g5,g11) = 6.5
    c: DistanceY(g7,g5) = 10
    c: PointOnObject(g5,g0)
    c: PointOnObject(g5,g3)
    c: Tangent(g0,g4) = 1.5708
    c: Tangent(g3,g4) = 1.5708
    c: PointOnObject(g7,g3)
    c: PointOnObject(g7,g2)
    c: Tangent(g3,g6) = 1.5708
    c: Tangent(g2,g6) = 1.5708
    c: PointOnObject(g9,g2)
    c: PointOnObject(g9,g1)
    c: Tangent(g2,g8) = 1.5708
    c: Tangent(g1,g8) = 1.5708
    c: PointOnObject(g11,g1)
    c: PointOnObject(g11,g0)
    c: Tangent(g1,g10) = 1.5708
    c: Tangent(g0,g10) = 1.5708
    c: Equal(g4,g6)
    c: Equal(g4,g8)
    c: Equal(g4,g10)
    c: Radius(g4) = 2
FEATURE [PartDesign::Pad] Pad025
  BaseFeature = -> Chamfer008
  Direction = (0,0,1)
  Length = 16.5
  Length2 = 10
  Profile = -> Sketch081
  ReferenceAxis = -> Sketch081 [N_Axis]
  Type = 0
FEATURE [PartDesign::ShapeBinder] ShapeBinder003
  Placement = pos=(0,0,0) rot=(0.57735,0.57735,0.57735;2.0944rad)
  Support = -> [Sketch080]
  TraceSupport = false
FEATURE [PartDesign::Pocket] Pocket027
  BaseFeature = -> Pad025
  Direction = (-1,0,0)
  Length = 5
  Length2 = 5
  Midplane = true
  Profile = -> ShapeBinder003
  Type = 1
FEATURE [PartDesign::ShapeBinder] ShapeBinder004
  Support = -> [Sketch006]
  TraceSupport = false
FEATURE [PartDesign::Hole] Hole027
  BaseFeature = -> Pocket027
  CustomThreadClearance = 0
  Depth = 141.346
  DepthType = 1
  Diameter = 2.5
  DrillForDepth = false
  DrillPoint = 1
  DrillPointAngle = 118
  HoleCutCountersinkAngle = 90
  HoleCutCustomValues = false
  HoleCutDepth = 0
  HoleCutDiameter = 6.1
  HoleCutType = 0
  ModelThread = false
  Profile = -> ShapeBinder004
  Reversed = true
  Tapered = false
  TaperedAngle = 90
  ThreadClass = 0
  ThreadDepth = 141.346
  ThreadDepthType = 0
  ThreadDirection = 0
  ThreadFit = 0
  ThreadSize = 9
  ThreadType = 1
  Threaded = true
  UseCustomThreadClearance = false
FEATURE [PartDesign::ShapeBinder] ShapeBinder005
  Support = -> [Sketch010]
  TraceSupport = false
FEATURE [PartDesign::Hole] Hole028
  BaseFeature = -> Hole027
  CustomThreadClearance = 0
  Depth = 25
  DepthType = 0
  Diameter = 2.5
  DrillForDepth = false
  DrillPoint = 1
  DrillPointAngle = 118
  HoleCutCountersinkAngle = 90
  HoleCutCustomValues = false
  HoleCutDepth = 0
  HoleCutDiameter = 6.1
  HoleCutType = 0
  ModelThread = false
  Profile = -> ShapeBinder005
  Reversed = true
  Tapered = false
  TaperedAngle = 90
  ThreadClass = 0
  ThreadDepth = 25
  ThreadDepthType = 0
  ThreadDirection = 0
  ThreadFit = 0
  ThreadSize = 9
  ThreadType = 1
  Threaded = true
  UseCustomThreadClearance = false
FEATURE [PartDesign::ShapeBinder] ShapeBinder006
  Placement = pos=(0,0,10) rot=(0,0,1;0rad)
  Support = -> [Sketch005]
  TraceSupport = false
FEATURE [PartDesign::ShapeBinder] ShapeBinder007
  Support = -> [Sketch007]
  TraceSupport = false
FEATURE [PartDesign::ShapeBinder] ShapeBinder008
  Placement = pos=(0,-13,-3) rot=(0,0,1;0rad)
  TraceSupport = false
FEATURE [PartDesign::ShapeBinder] ShapeBinder009
  Placement = pos=(0,13,-3) rot=(0,0,1;0rad)
  TraceSupport = false
FEATURE [PartDesign::ShapeBinder] ShapeBinder010
  Placement = pos=(40,0,4) rot=(0,0,1;0rad)
  TraceSupport = false
FEATURE [PartDesign::ShapeBinder] ShapeBinder011
  Placement = pos=(20,0,3) rot=(0,0,1;0rad)
  TraceSupport = false
FEATURE [PartDesign::ShapeBinder] ShapeBinder012
  Placement = pos=(13,0,-3) rot=(0,0,1;0rad)
  TraceSupport = false
FEATURE [PartDesign::ShapeBinder] ShapeBinder013
  Placement = pos=(0,0,-3) rot=(0,0,1;0rad)
  TraceSupport = false
FEATURE [PartDesign::ShapeBinder] ShapeBinder014
  Support = -> [Sketch078]
  TraceSupport = false
FEATURE [PartDesign::SubShapeBinder] Binder003
  BindCopyOnChange = 0
  BindMode = 0
  ClaimChildren = false
  Context = -> Part002 [Body001.Binder003.]
  Fuse = false
  MakeFace = true
  OffsetFill = false
  OffsetIntersection = false
  OffsetJoinType = 0
  OffsetOpenResult = false
  PartialLoad = false
  Placement = pos=(0,0,3) rot=(0,0,1;0rad)
  Relative = true
  Support = -> [Pad[Sketch.]]
  _Version = 2
FEATURE [PartDesign::Pad] Pad027
  BaseFeature = -> Hole003
  Direction = (0,0,1)
  Length = 0.2
  Length2 = 10
  Profile = -> Binder003
  Type = 0
FEATURE [PartDesign::Hole] Hole
  BaseFeature = -> Pad027
  CustomThreadClearance = 0
  Depth = 148.549
  DepthType = 1
  Diameter = 3.4
  DrillForDepth = false
  DrillPoint = 1
  DrillPointAngle = 118
  HoleCutCountersinkAngle = 90
  HoleCutCustomValues = false
  HoleCutDepth = 6
  HoleCutDiameter = 5.7
  HoleCutType = 1
  ModelThread = false
  Profile = -> Sketch005
  Tapered = false
  TaperedAngle = 90
  ThreadClass = 0
  ThreadDepth = 148.549
  ThreadDepthType = 0
  ThreadDirection = 0
  ThreadFit = 0
  ThreadSize = 9
  ThreadType = 1
  Threaded = false
  UseCustomThreadClearance = false
FEATURE [PartDesign::Hole] Hole002
  BaseFeature = -> Hole
  CustomThreadClearance = 0
  Depth = 148.549
  DepthType = 1
  Diameter = 3.4
  DrillForDepth = false
  DrillPoint = 1
  DrillPointAngle = 118
  HoleCutCountersinkAngle = 90
  HoleCutCustomValues = false
  HoleCutDepth = 0
  HoleCutDiameter = 6.1
  HoleCutType = 0
  ModelThread = false
  Profile = -> Sketch007
  Reversed = true
  Tapered = false
  TaperedAngle = 90
  ThreadClass = 0
  ThreadDepth = 148.549
  ThreadDepthType = 0
  ThreadDirection = 0
  ThreadFit = 0
  ThreadSize = 9
  ThreadType = 1
  Threaded = false
  UseCustomThreadClearance = false
FEATURE [PartDesign::Boolean] Boolean002
  BaseFeature = -> Hole002
  Refine = true
  Type = 1
FEATURE [PartDesign::Pad] Pad022
  BaseFeature = -> Boolean002
  Direction = (0,0,1)
  Length = 28
  Length2 = 10
  Profile = -> Sketch078
  ReferenceAxis = -> Sketch078 [N_Axis]
  Type = 0
FEATURE [PartDesign::Body] Body001  label="CarriageLeftMain"
  Group = -> [Sketch,Pad,Chamfer,Pad023,Pocket026,Hole001,Hole003,Binder003,Pad027,Hole,Hole002,Boolean002,Pad022,Sketch005,Sketch006,Sketch007,Sketch008,Sketch009,Sketch010,Sketch078,Sketch079,Sketch080]
  Origin = -> Origin006
  Tip = -> Boolean002
FEATURE [PartDesign::AdditiveBox] Box009
  AttacherType = Attacher::AttachEngine3D
  AttachmentOffset = pos=(-3,10,28) rot=(0,0,1;0rad)
  BaseFeature = -> Hole005
  Height = 0.2
  Length = 6
  MapMode = 2
  Placement = pos=(-3,10,28) rot=(0,0,1;0rad)
  Support = -> [Body001]
  Width = 6
FEATURE [PartDesign::AdditiveBox] Box010
  AttacherType = Attacher::AttachEngine3D
  AttachmentOffset = pos=(-3,-16,28) rot=(0,0,1;0rad)
  BaseFeature = -> Box009
  Height = 0.2
  Length = 6
  MapMode = 5
  Placement = pos=(-3,-16,28) rot=(0,0,1;0rad)
  Support = -> [XY_Plane008]
  Width = 6
FEATURE [PartDesign::AdditiveBox] Box011
  AttacherType = Attacher::AttachEngine3D
  AttachmentOffset = pos=(25,-3,28) rot=(0,0,1;0rad)
  BaseFeature = -> Box010
  Height = 0.2
  Length = 6
  MapMode = 5
  Placement = pos=(25,-3,28) rot=(0,0,1;0rad)
  Support = -> [XY_Plane008]
  Width = 6
FEATURE [PartDesign::Body] Body003  label="CarriageLeftBrace"
  Group = -> [Sketch011,Pad003,Box003,Box004,Box005,Fillet002,Fillet003,Chamfer001,Chamfer002,Sketch012,Hole004,Sketch013,Hole005,Box009,Box010,Box011]
  Origin = -> Origin008
  Tip = -> Box011
FEATURE [App::Part] Part002  label="CarriageLeft"
  Group = -> [Body001,Body003,GarriageLeftPartOrigin]
  Origin = -> Origin004
FEATURE [PartDesign::SubShapeBinder] Binder004
  BindCopyOnChange = 0
  BindMode = 0
  ClaimChildren = false
  Context = -> Part003 [Body002.Binder004.]
  Fuse = false
  MakeFace = true
  OffsetFill = false
  OffsetIntersection = false
  OffsetJoinType = 0
  OffsetOpenResult = false
  PartialLoad = false
  Placement = pos=(0,0,3) rot=(0,0,1;0rad)
  Relative = true
  Support = -> [ShapeBinder002]
  _Version = 2
FEATURE [PartDesign::Pad] Pad028
  BaseFeature = -> Hole028
  Direction = (0,0,1)
  Length = 0.2
  Length2 = 10
  Profile = -> Binder004
  Type = 0
FEATURE [PartDesign::Hole] Hole029
  BaseFeature = -> Pad028
  CustomThreadClearance = 0
  Depth = 141.346
  DepthType = 1
  Diameter = 3.4
  DrillForDepth = false
  DrillPoint = 1
  DrillPointAngle = 118
  HoleCutCountersinkAngle = 90
  HoleCutCustomValues = false
  HoleCutDepth = 6
  HoleCutDiameter = 5.7
  HoleCutType = 1
  ModelThread = false
  Profile = -> ShapeBinder006
  Tapered = false
  TaperedAngle = 90
  ThreadClass = 0
  ThreadDepth = 141.346
  ThreadDepthType = 0
  ThreadDirection = 0
  ThreadFit = 0
  ThreadSize = 9
  ThreadType = 1
  Threaded = false
  UseCustomThreadClearance = false
FEATURE [PartDesign::Hole] Hole030
  BaseFeature = -> Hole029
  CustomThreadClearance = 0
  Depth = 141.346
  DepthType = 1
  Diameter = 3.4
  DrillForDepth = false
  DrillPoint = 1
  DrillPointAngle = 118
  HoleCutCountersinkAngle = 90
  HoleCutCustomValues = false
  HoleCutDepth = 0
  HoleCutDiameter = 6.1
  HoleCutType = 0
  ModelThread = false
  Profile = -> ShapeBinder007
  Reversed = true
  Tapered = false
  TaperedAngle = 90
  ThreadClass = 0
  ThreadDepth = 141.346
  ThreadDepthType = 0
  ThreadDirection = 0
  ThreadFit = 0
  ThreadSize = 9
  ThreadType = 1
  Threaded = false
  UseCustomThreadClearance = false
FEATURE [PartDesign::Boolean] Boolean003
  BaseFeature = -> Hole030
  Group = -> [ShapeBinder008,ShapeBinder009,ShapeBinder010,ShapeBinder011,ShapeBinder012,ShapeBinder013]
  Refine = true
  Type = 1
FEATURE [PartDesign::Pad] Pad026
  BaseFeature = -> Boolean003
  Direction = (0,0,1)
  Length = 28
  Length2 = 10
  Profile = -> ShapeBinder014
  Type = 0
FEATURE [PartDesign::Body] Body002  label="CarriageRightMain"
  Group = -> [ShapeBinder002,Pad024,Chamfer008,Sketch081,Pad025,ShapeBinder003,Pocket027,ShapeBinder004,Hole027,ShapeBinder005,Hole028,Binder004,Pad028,ShapeBinder006,Hole029,ShapeBinder007,Hole030,Boolean003,ShapeBinder014,Pad026]
  Origin = -> Origin007
  Tip = -> Boolean003
FEATURE [Sketcher::SketchObject] Sketch082
  AttachmentOffset = pos=(0,0,115) rot=(0,0,1;0rad)
  FullyConstrained = true
  MapMode = 5
  Placement = pos=(0,-115,-2.55e-14) rot=(1,0,0;1.5708rad)
  Support = -> [XZ_Plane010]
  expr: .AttachmentOffset.Base.z = <<Variables>>.GantorySpacing / 2 + <<Variables>>.CavitySpacingY + <<Variables>>.WallThickness - 2
  sketch-geometry (4):
    g0: LineSegment StartX=-95 StartY=60 StartZ=0 EndX=95 EndY=60 EndZ=0
    g1: LineSegment StartX=95 StartY=60 StartZ=0 EndX=95 EndY=25 EndZ=0
    g2: LineSegment StartX=95 StartY=25 StartZ=0 EndX=-95 EndY=25 EndZ=0
    g3: LineSegment StartX=-95 StartY=25 StartZ=0 EndX=-95 EndY=60 EndZ=0
  constraints (10):
    c: Coincident(g0,g1)
    c: Coincident(g1,g2)
    c: Coincident(g2,g3)
    c: Coincident(g3,g0)
    c: Symmetric(g0,g0,g-2)
    c: Symmetric(g2,g1,g-2)
    c: Vertical(g3)
    c: DistanceY(g0) = 60
    c: DistanceY(g2) = 25
    c: DistanceX(g0,g0) = 190
FEATURE [Sketcher::SketchObject] Sketch083
  AttachmentOffset = pos=(0,0,117) rot=(0,0,1;0rad)
  FullyConstrained = true
  MapMode = 5
  Placement = pos=(0,-117,-2.6e-14) rot=(1,0,0;1.5708rad)
  Support = -> [XZ_Plane010]
  expr: .AttachmentOffset.Base.z = <<Variables>>.GantorySpacing / 2 + <<Variables>>.CavitySpacingY + <<Variables>>.WallThickness
  expr: Constraints[8] = 25 - 2
  expr: Constraints[9] = <<Variables>>.GantorySpacing - 10 + 4
  sketch-geometry (4):
    g0: LineSegment StartX=-97 StartY=60 StartZ=0 EndX=97 EndY=60 EndZ=0
    g1: LineSegment StartX=97 StartY=60 StartZ=0 EndX=97 EndY=23 EndZ=0
    g2: LineSegment StartX=97 StartY=23 StartZ=0 EndX=-97 EndY=23 EndZ=0
    g3: LineSegment StartX=-97 StartY=23 StartZ=0 EndX=-97 EndY=60 EndZ=0
  constraints (10):
    c: Coincident(g0,g1)
    c: Coincident(g1,g2)
    c: Coincident(g2,g3)
    c: Coincident(g3,g0)
    c: Symmetric(g0,g0,g-2)
    c: Symmetric(g2,g1,g-2)
    c: Vertical(g3)
    c: DistanceY(g0) = 60
    c: DistanceY(g2) = 23
    c: DistanceX(g0,g0) = 194
FEATURE [Sketcher::SketchObject] Sketch084
  FullyConstrained = true
  MapMode = 5
  Support = -> [XY_Plane010]
  expr: Constraints[5] = Sketch038.Constraints[5] + 4mm
  expr: Constraints[7] = Sketch038.Constraints[7] - 2mm
  expr: Constraints[8] = Sketch038.Constraints[8] + 2mm
  sketch-geometry (4):
    g0: LineSegment StartX=-97 StartY=91 StartZ=0 EndX=97 EndY=91 EndZ=0
    g1: LineSegment StartX=97 StartY=91 StartZ=0 EndX=97 EndY=-91 EndZ=0
    g2: LineSegment StartX=97 StartY=-91 StartZ=0 EndX=-97 EndY=-91 EndZ=0
    g3: LineSegment StartX=-97 StartY=-91 StartZ=0 EndX=-97 EndY=91 EndZ=0
  constraints (10):
    c: Coincident(g0,g1)
    c: Coincident(g1,g2)
    c: Coincident(g2,g3)
    c: Coincident(g3,g0)
    c: Symmetric(g0,g0,g-2)
    c: DistanceX(g0,g0) = 194
    c: Symmetric(g2,g1,g-2)
    c: DistanceY(g2) = -91
    c: DistanceY(g0) = 91
    c: Vertical(g3)
FEATURE [Part::FeaturePython] Clone056  label="M3 inserted Nut TopPanel E1"  # Draft clone (typed FeaturePython)
  AttacherType = Attacher::AttachEngine3D
  Fuse = false
  Objects = -> [Body013]
  Placement = pos=(15.9,113,30) rot=(0.57735,-0.57735,0.57735;2.0944rad)
  Scale = (1,1,1)
  expr: .Placement.Base.y = <<Variables>>.GantorySpacing / 2 + <<Variables>>.CavitySpacingY + 3
FEATURE [Part::FeaturePython] Clone057  label="M3 inserted Nut TopPanel E2"  # Draft clone (typed FeaturePython)
  AttacherType = Attacher::AttachEngine3D
  Fuse = false
  Objects = -> [Body013]
  Placement = pos=(-15.9,113,30) rot=(0.57735,-0.57735,0.57735;2.0944rad)
  Scale = (1,1,1)
  expr: .Placement.Base.y = <<Variables>>.GantorySpacing / 2 + <<Variables>>.CavitySpacingY + 3
FEATURE [Sketcher::SketchObject] Sketch085
  AttachmentOffset = pos=(0,0,7) rot=(0,0,1;0rad)
  FullyConstrained = true
  MapMode = 5
  Placement = pos=(0,0,7) rot=(0,0,1;0rad)
  Support = -> [XY_Plane010]
  expr: .AttachmentOffset.Base.z = <<Variables>>.TopThickness - 3
  expr: Constraints[5] = Sketch038.Constraints[5]
  expr: Constraints[7] = Sketch038.Constraints[7]
  expr: Constraints[8] = Sketch038.Constraints[8]
  sketch-geometry (4):
    g0: LineSegment StartX=-95 StartY=89 StartZ=0 EndX=95 EndY=89 EndZ=0
    g1: LineSegment StartX=95 StartY=89 StartZ=0 EndX=95 EndY=-89 EndZ=0
    g2: LineSegment StartX=95 StartY=-89 StartZ=0 EndX=-95 EndY=-89 EndZ=0
    g3: LineSegment StartX=-95 StartY=-89 StartZ=0 EndX=-95 EndY=89 EndZ=0
  constraints (10):
    c: Coincident(g0,g1)
    c: Coincident(g1,g2)
    c: Coincident(g2,g3)
    c: Coincident(g3,g0)
    c: Symmetric(g0,g0,g-2)
    c: DistanceX(g0,g0) = 190
    c: Symmetric(g2,g1,g-2)
    c: DistanceY(g2) = -89
    c: DistanceY(g0) = 89
    c: Vertical(g3)
FEATURE [Sketcher::SketchObject] Sketch086
  AttachmentOffset = pos=(0,0,10) rot=(0,0,1;0rad)
  FullyConstrained = true
  MapMode = 5
  Placement = pos=(0,0,10) rot=(0,0,1;0rad)
  Support = -> [XY_Plane010]
  expr: .AttachmentOffset.Base.z = <<Variables>>.TopThickness
  expr: Constraints[5] = Sketch038.Constraints[5]
  expr: Constraints[7] = Sketch038.Constraints[7] - 3mm
  expr: Constraints[8] = Sketch038.Constraints[8] + 3mm
  sketch-geometry (4):
    g0: LineSegment StartX=-95 StartY=92 StartZ=0 EndX=95 EndY=92 EndZ=0
    g1: LineSegment StartX=95 StartY=92 StartZ=0 EndX=95 EndY=-92 EndZ=0
    g2: LineSegment StartX=95 StartY=-92 StartZ=0 EndX=-95 EndY=-92 EndZ=0
    g3: LineSegment StartX=-95 StartY=-92 StartZ=0 EndX=-95 EndY=92 EndZ=0
  constraints (10):
    c: Coincident(g0,g1)
    c: Coincident(g1,g2)
    c: Coincident(g2,g3)
    c: Coincident(g3,g0)
    c: Symmetric(g0,g0,g-2)
    c: DistanceX(g0,g0) = 190
    c: Symmetric(g2,g1,g-2)
    c: DistanceY(g2) = -92
    c: DistanceY(g0) = 92
    c: Vertical(g3)
FEATURE [Sketcher::SketchObject] Sketch087  label="Sketch for TopPanel Chamfer"
  FullyConstrained = true
  MapMode = 5
  Placement = pos=(0,0,0) rot=(1,0,0;1.5708rad)
  Support = -> [XZ_Plane010]
  expr: Constraints[12] = <<Variables>>.GantorySpacing + (<<Variables>>.CavitySpacingX + <<Variables>>.WallThickness) * 2
  sketch-geometry (6):
    g0: LineSegment StartX=117 StartY=5 StartZ=0 EndX=117 EndY=-60 EndZ=0
    g1: LineSegment StartX=117 StartY=-60 StartZ=0 EndX=-117 EndY=-60 EndZ=0
    g2: LineSegment StartX=-117 StartY=-60 StartZ=0 EndX=-117 EndY=5 EndZ=0
    g3: LineSegment StartX=112 StartY=0 StartZ=0 EndX=-112 EndY=0 EndZ=0
    g4: LineSegment StartX=-117 StartY=5 StartZ=0 EndX=-112 EndY=0 EndZ=0
    g5: LineSegment StartX=112 StartY=0 StartZ=0 EndX=117 EndY=5 EndZ=0
  constraints (15):
    c: Coincident(g0,g1)
    c: Coincident(g1,g2)
    c: Coincident(g3,g4)
    c: Coincident(g3,g5)
    c: Angle(g4) = -0.785398
    c: Symmetric(g3,g3,g-2)
    c: Symmetric(g2,g0,g-2)
    c: Symmetric(g1,g0,g-2)
    c: PointOnObject(g3,g-1)
    c: Coincident(g2,g4)
    c: Coincident(g0,g5)
    c: DistanceX(g2,g3) = 5
    c: DistanceX(g1,g1) = 234
    c: DistanceY(g1) = -60
    c: Vertical(g2)
FEATURE [PartDesign::SubShapeBinder] Binder005  label="Binder for TopPanel FrontChamfer"
  BindCopyOnChange = 0
  BindMode = 0
  ClaimChildren = false
  Context = -> Part004 [Body004.Binder005.]
  Fuse = false
  MakeFace = true
  OffsetFill = false
  OffsetIntersection = false
  OffsetJoinType = 0
  OffsetOpenResult = false
  PartialLoad = false
  Placement = pos=(0,-95,0) rot=(-1,0,0;0.785398rad)
  Relative = true
  Support = -> [Sketch087]
  _Version = 2
  expr: .Placement.Base.y = -(Variables.GantorySpacing - 10) / 2
FEATURE [PartDesign::SubShapeBinder] Binder006  label="Binder for TopPanel RearChamfer"
  BindCopyOnChange = 0
  BindMode = 0
  ClaimChildren = false
  Context = -> Part004 [Body004.Binder006.]
  Fuse = false
  MakeFace = true
  OffsetFill = false
  OffsetIntersection = false
  OffsetJoinType = 0
  OffsetOpenResult = false
  PartialLoad = false
  Placement = pos=(0,95,0) rot=(1,0,0;0.785398rad)
  Relative = true
  Support = -> [Sketch087]
  _Version = 2
  expr: .Placement.Base.y = (Variables.GantorySpacing - 10) / 2
FEATURE [PartDesign::SubShapeBinder] Binder007  label="Binder for TopPanel Y Rail Hole Support"
  BindCopyOnChange = 0
  BindMode = 0
  ClaimChildren = false
  Context = -> Part004 [Body004.Binder007.]
  Fuse = false
  MakeFace = true
  OffsetFill = false
  OffsetIntersection = false
  OffsetJoinType = 0
  OffsetOpenResult = false
  PartialLoad = false
  Placement = pos=(0,0,3) rot=(0,0,1;0rad)
  Relative = true
  Support = -> [Hole006[Sketch014.]]
  _Version = 2
FEATURE [PartDesign::SubShapeBinder] Binder008  label="Binder for TopPanel BottomFaceFitting Support"
  BindCopyOnChange = 0
  BindMode = 0
  ClaimChildren = false
  Context = -> Part004 [Body004.Binder008.]
  Fuse = false
  MakeFace = true
  OffsetFill = false
  OffsetIntersection = false
  OffsetJoinType = 0
  OffsetOpenResult = false
  PartialLoad = false
  Placement = pos=(0,0,9) rot=(0,0,1;0rad)
  Relative = true
  Support = -> [Hole009[Sketch032.]]
  _Version = 2
FEATURE [Sketcher::SketchObject] Sketch088
  AttachmentOffset = pos=(0,0,21) rot=(0,0,1;0rad)
  FullyConstrained = true
  MapMode = 5
  Placement = pos=(0,0,21) rot=(0,0,1;0rad)
  Support = -> [XY_Plane010]
  expr: Constraints[1] = Sketch037.Constraints[4]
  expr: Constraints[5] = Sketch037.Constraints[6]
  expr: Constraints[6] = Sketch037.Constraints[7]
  expr: Constraints[7] = Sketch037.Constraints[3]
  sketch-geometry (6):
    g0: Circle CenterX=-100 CenterY=-100 CenterZ=0 NormalX=0 NormalY=0 NormalZ=1 AngleXU=0 Radius=3
    g1: Circle CenterX=100 CenterY=-100 CenterZ=0 NormalX=0 NormalY=0 NormalZ=1 AngleXU=0 Radius=3
    g2: Circle CenterX=-87.27 CenterY=112.73 CenterZ=0 NormalX=0 NormalY=0 NormalZ=1 AngleXU=0 Radius=3
    g3: Circle CenterX=-100 CenterY=100 CenterZ=0 NormalX=0 NormalY=0 NormalZ=1 AngleXU=0 Radius=3
    g4: Circle CenterX=87.27 CenterY=112.73 CenterZ=0 NormalX=0 NormalY=0 NormalZ=1 AngleXU=0 Radius=3
    g5: Circle CenterX=100 CenterY=100 CenterZ=0 NormalX=0 NormalY=0 NormalZ=1 AngleXU=0 Radius=3
  constraints (10):
    c: Symmetric(g0,g1,g-2)
    c: DistanceX(g0,g1) = 200
    c: Symmetric(g3,g0,g-1)
    c: Symmetric(g3,g5,g-2)
    c: Symmetric(g2,g4,g-2)
    c: DistanceX(g2,g4) = 174.54
    c: DistanceY(g-1,g2) = 112.73
    c: DistanceY(g0,g3) = 200
    c: Equal(g0, g1-g5) x5
    c: Diameter(g0) = 6
FEATURE [Part::FeaturePython] Clone058  label="M3 inserted Nut TopPanel E3"  # Draft clone (typed FeaturePython)
  AttacherType = Attacher::AttachEngine3D
  Fuse = false
  Objects = -> [Body013]
  Placement = pos=(15.9,113,39.5) rot=(0.57735,-0.57735,0.57735;2.0944rad)
  Scale = (1,1,1)
  expr: .Placement.Base.y = <<Variables>>.GantorySpacing / 2 + <<Variables>>.CavitySpacingY + 3
FEATURE [Part::FeaturePython] Clone059  label="M3 inserted Nut TopPanel E4"  # Draft clone (typed FeaturePython)
  AttacherType = Attacher::AttachEngine3D
  Fuse = false
  Objects = -> [Body013]
  Placement = pos=(-15.9,113,39.5) rot=(0.57735,-0.57735,0.57735;2.0944rad)
  Scale = (1,1,1)
  expr: .Placement.Base.y = <<Variables>>.GantorySpacing / 2 + <<Variables>>.CavitySpacingY + 3
FEATURE [Part::FeaturePython] Clone060  label="M3 inserted Nut TopPanel Z Pully 1"  # Draft clone (typed FeaturePython)
  AttacherType = Attacher::AttachEngine3D
  Fuse = false
  Objects = -> [Body013]
  Placement = pos=(12.73,114,50) rot=(0.57735,-0.57735,-0.57735;4.18879rad)
  Scale = (1,1,1)
  expr: .Placement.Base.x = (<<Variables>>.PullyDiameterDrive + <<Variables>>.PullyDiameterIdler) / 2
  expr: .Placement.Base.y = <<Variables>>.GantorySpacing / 2 + <<Variables>>.CavitySpacingY + <<Variables>>.WallThickness - 3
FEATURE [Part::FeaturePython] Clone061  label="M3 inserted Nut TopPanel Z Pully 2"  # Draft clone (typed FeaturePython)
  AttacherType = Attacher::AttachEngine3D
  Fuse = false
  Objects = -> [Body013]
  Placement = pos=(-12.73,114,50) rot=(0.57735,-0.57735,-0.57735;4.18879rad)
  Scale = (1,1,1)
  expr: .Placement.Base.x = -(<<Variables>>.PullyDiameterDrive + <<Variables>>.PullyDiameterIdler) / 2
  expr: .Placement.Base.y = <<Variables>>.GantorySpacing / 2 + <<Variables>>.CavitySpacingY + <<Variables>>.WallThickness - 3
FEATURE [PartDesign::AdditiveBox] Box
  AttacherType = Attacher::AttachEngine3D
  AttachmentOffset = pos=(-110,-100,-1) rot=(0,0,1;0rad)
  Height = 1
  Length = 220
  MapMode = 5
  Placement = pos=(-110,-100,-1) rot=(0,0,1;0rad)
  Support = -> [XY_Plane037]
  Width = 200
  expr: .AttachmentOffset.Base.x = -(<<Variables>>.GantorySpacing + 20) / 2
  expr: .AttachmentOffset.Base.y = -<<Variables>>.GantorySpacing / 2
  expr: Length = <<Variables>>.GantorySpacing + 20
  expr: Width = <<Variables>>.GantorySpacing
FEATURE [PartDesign::AdditivePrism] Prism
  AttacherType = Attacher::AttachEngine3D
  AttachmentOffset = pos=(100,80,-1) rot=(0,0,1;0rad)
  BaseFeature = -> Box
  Circumradius = 3.35
  FirstAngle = 0
  Height = 4
  MapMode = 5
  Placement = pos=(100,80,-1) rot=(0,0,1;0rad)
  Polygon = 6
  SecondAngle = 0
  Support = -> [XY_Plane037]
  expr: .AttachmentOffset.Base.x = <<Variables>>.GantorySpacing / 2
  expr: .AttachmentOffset.Base.y = trunc((<<Variables>>.GantorySpacing - 20) / 20 / 2) * 20
FEATURE [PartDesign::AdditivePrism] Prism020
  AttacherType = Attacher::AttachEngine3D
  AttachmentOffset = pos=(-100,80,-1) rot=(0,0,1;0rad)
  BaseFeature = -> Prism
  Circumradius = 3.35
  FirstAngle = 0
  Height = 4
  MapMode = 5
  Placement = pos=(-100,80,-1) rot=(0,0,1;0rad)
  Polygon = 6
  SecondAngle = 0
  Support = -> [XY_Plane037]
  expr: .AttachmentOffset.Base.x = -<<Variables>>.GantorySpacing / 2
  expr: .AttachmentOffset.Base.y = trunc((<<Variables>>.GantorySpacing - 20) / 20 / 2) * 20
FEATURE [PartDesign::LinearPattern] LinearPattern
  BaseFeature = -> Prism020
  Direction = -> Y_Axis037
  Length = 160
  Occurrences = 9
  Originals = -> [Prism,Prism020]
  Placement = pos=(-100,80,-1) rot=(0,0,1;0rad)
  Reversed = true
  expr: Length = trunc((<<Variables>>.GantorySpacing - 1) / 20 - 1) * 20
  expr: Occurrences = trunc((<<Variables>>.GantorySpacing - 1) / 20)
FEATURE [PartDesign::Body] Body021  label="TopPanelInsertedNuts"
  Group = -> [Box,Prism,Prism020,LinearPattern]
  Origin = -> Origin037
  Tip = -> LinearPattern
FEATURE [Part::FeaturePython] Clone062  label="M3 inserted Nut TopPanel SideFitting 1"  # Draft clone (typed FeaturePython)
  AttacherType = Attacher::AttachEngine3D
  Fuse = false
  Objects = -> [Body013]
  Placement = pos=(105,-15,55) rot=(0,-1,0;1.5708rad)
  Scale = (1,1,1)
  expr: .Placement.Base.x = <<Variables>>.GantorySpacing / 2 + <<Variables>>.CavitySpacingX - 5
FEATURE [Part::FeaturePython] Clone063  label="M3 inserted Nut TopPanel SideFitting 2"  # Draft clone (typed FeaturePython)
  AttacherType = Attacher::AttachEngine3D
  Fuse = false
  Objects = -> [Body013]
  Placement = pos=(-105,-15,55) rot=(0,1,0;1.5708rad)
  Scale = (1,1,1)
  expr: .Placement.Base.x = -(<<Variables>>.GantorySpacing / 2 + <<Variables>>.CavitySpacingX - 5)
FEATURE [Part::FeaturePython] Clone064  label="M3 inserted Nut TopPanel SideFitting 3"  # Draft clone (typed FeaturePython)
  AttacherType = Attacher::AttachEngine3D
  Fuse = false
  Objects = -> [Body013]
  Placement = pos=(110,-55,55) rot=(0,-1,0;1.5708rad)
  Scale = (1,1,1)
  expr: .Placement.Base.x = <<Variables>>.GantorySpacing / 2 + <<Variables>>.CavitySpacingX
FEATURE [Part::FeaturePython] Clone065  label="M3 inserted Nut TopPanel SideFitting 4"  # Draft clone (typed FeaturePython)
  AttacherType = Attacher::AttachEngine3D
  Fuse = false
  Objects = -> [Body013]
  Placement = pos=(-110,-55,55) rot=(0,1,0;1.5708rad)
  Scale = (1,1,1)
  expr: .Placement.Base.x = -(<<Variables>>.GantorySpacing / 2 + <<Variables>>.CavitySpacingX)
FEATURE [Part::FeaturePython] Clone066  label="M3 inserted Nut TopPanel SideFitting 5"  # Draft clone (typed FeaturePython)
  AttacherType = Attacher::AttachEngine3D
  Fuse = false
  Objects = -> [Body013]
  Placement = pos=(110,55,55) rot=(0,-1,0;1.5708rad)
  Scale = (1,1,1)
  expr: .Placement.Base.x = <<Variables>>.GantorySpacing / 2 + <<Variables>>.CavitySpacingX
FEATURE [Part::FeaturePython] Clone067  label="M3 inserted Nut TopPanel SideFitting 6"  # Draft clone (typed FeaturePython)
  AttacherType = Attacher::AttachEngine3D
  Fuse = false
  Objects = -> [Body013]
  Placement = pos=(-110,55,55) rot=(0,1,0;1.5708rad)
  Scale = (1,1,1)
  expr: .Placement.Base.x = -(<<Variables>>.GantorySpacing / 2 + <<Variables>>.CavitySpacingX)
FEATURE [Part::FeaturePython] Clone070  label="M3 inserted Nut TopPanel Z Rail 2"  # Draft clone (typed FeaturePython)
  AttacherType = Attacher::AttachEngine3D
  Fuse = false
  Objects = -> [Body013]
  Placement = pos=(65,114,55) rot=(0.57735,-0.57735,-0.57735;4.18879rad)
  Scale = (1,1,1)
  expr: .Placement.Base.y = <<Variables>>.GantorySpacing / 2 + <<Variables>>.CavitySpacingY + <<Variables>>.WallThickness - 3
FEATURE [Part::FeaturePython] Clone071  label="M3 inserted Nut TopPanel Z Rail 3"  # Draft clone (typed FeaturePython)
  AttacherType = Attacher::AttachEngine3D
  Fuse = false
  Objects = -> [Clone070]
  Placement = pos=(-65,114,55) rot=(0.57735,-0.57735,-0.57735;4.18879rad)
  Scale = (1,1,1)
  expr: .Placement.Base.y = <<Variables>>.GantorySpacing / 2 + <<Variables>>.CavitySpacingY + <<Variables>>.WallThickness - 3
FEATURE [Part::FeaturePython] Clone072  label="M3 inserted Nut TopPanel RearFitting 1"  # Draft clone (typed FeaturePython)
  AttacherType = Attacher::AttachEngine3D
  Fuse = false
  Objects = -> [Body013]
  Placement = pos=(40,106,55) rot=(0.57735,-0.57735,0.57735;2.0944rad)
  Scale = (1,1,1)
  expr: .Placement.Base.y = <<Variables>>.GantorySpacing / 2 + <<Variables>>.CavitySpacingY - 4
FEATURE [Part::FeaturePython] Clone073  label="M3 inserted Nut TopPanel RearFitting 2"  # Draft clone (typed FeaturePython)
  AttacherType = Attacher::AttachEngine3D
  Fuse = false
  Objects = -> [Body013]
  Placement = pos=(-40,106,55) rot=(0.57735,-0.57735,0.57735;2.0944rad)
  Scale = (1,1,1)
  expr: .Placement.Base.y = <<Variables>>.GantorySpacing / 2 + <<Variables>>.CavitySpacingY - 4
FEATURE [Sketcher::SketchObject] Sketch089
  FullyConstrained = true
  MapMode = 5
  Support = -> [XY_Plane012]
  expr: Constraints[100] = <<Variables>>.FittingGap / 2
  expr: Constraints[101] = <<Variables>>.FittingGap / 2
  expr: Constraints[130] = -<<Variables>>.GantorySpacing / 2
  expr: Constraints[131] = 10 - <<Variables>>.FittingGap
  expr: Constraints[56] = 10 - <<Variables>>.FittingGap
  expr: Constraints[62] = <<Variables>>.FittingGap / 2
  expr: Constraints[63] = <<Variables>>.FittingGap / 2
  expr: Constraints[96] = <<Variables>>.FittingGap / 2
  expr: Constraints[97] = <<Variables>>.FittingGap / 2
  expr: Constraints[98] = <<Variables>>.FittingGap / 2
  expr: Constraints[99] = <<Variables>>.FittingGap / 2
  sketch-geometry (64):
    g0: LineSegment StartX=-109.8 StartY=0 StartZ=0 EndX=-109.8 EndY=-26.242 EndZ=0
    g1: LineSegment StartX=-109.8 StartY=-26.242 StartZ=0 EndX=-100 EndY=-31.9 EndZ=0
    g2: LineSegment StartX=-100 StartY=-52.1 StartZ=0 EndX=-109.8 EndY=-57.758 EndZ=0
    g3: LineSegment StartX=-109.8 StartY=-57.758 StartZ=0 EndX=-109.8 EndY=-78.242 EndZ=0
    g4: LineSegment StartX=-109.8 StartY=-78.242 StartZ=0 EndX=-100 EndY=-83.9 EndZ=0
    g5: LineSegment StartX=-100 StartY=-104.1 StartZ=0 EndX=-109.8 EndY=-109.758 EndZ=0
    g6: LineSegment StartX=-109.8 StartY=-109.758 StartZ=0 EndX=-109.8 EndY=-130.242 EndZ=0
    g7: LineSegment StartX=-109.8 StartY=-130.242 StartZ=0 EndX=-100 EndY=-135.9 EndZ=0
    g8: LineSegment StartX=-100 StartY=-156.1 StartZ=0 EndX=-109.8 EndY=-161.758 EndZ=0
    g9: LineSegment StartX=-109.8 StartY=-161.758 StartZ=0 EndX=-109.8 EndY=-175 EndZ=0
    g10: LineSegment StartX=-49.9 StartY=-175 StartZ=0 EndX=-44.242 EndY=-184.8 EndZ=0
    g11: LineSegment StartX=-44.242 StartY=-184.8 StartZ=0 EndX=-35.758 EndY=-184.8 EndZ=0
    g12: LineSegment StartX=-35.758 StartY=-184.8 StartZ=0 EndX=-30.1 EndY=-175 EndZ=0
    g13: LineSegment StartX=30.1 StartY=-175 StartZ=0 EndX=35.758 EndY=-184.8 EndZ=0
    g14: LineSegment StartX=35.758 StartY=-184.8 StartZ=0 EndX=44.242 EndY=-184.8 EndZ=0
    g15: LineSegment StartX=44.242 StartY=-184.8 StartZ=0 EndX=49.9 EndY=-175 EndZ=0
    g16: LineSegment StartX=49.9 StartY=-175 StartZ=0 EndX=109.8 EndY=-175 EndZ=0
    g17: LineSegment StartX=109.8 StartY=-175 StartZ=0 EndX=109.8 EndY=-161.758 EndZ=0
    g18: LineSegment StartX=109.8 StartY=-161.758 StartZ=0 EndX=100 EndY=-156.1 EndZ=0
    g19: LineSegment StartX=100 StartY=-156.1 StartZ=0 EndX=100 EndY=-135.9 EndZ=0
    g20: LineSegment StartX=100 StartY=-135.9 StartZ=0 EndX=109.8 EndY=-130.242 EndZ=0
    g21: LineSegment StartX=109.8 StartY=-130.242 StartZ=0 EndX=109.8 EndY=-109.758 EndZ=0
    g22: LineSegment StartX=109.8 StartY=-109.758 StartZ=0 EndX=100 EndY=-104.1 EndZ=0
    g23: LineSegment StartX=100 StartY=-104.1 StartZ=0 EndX=100 EndY=-83.9 EndZ=0
    g24: LineSegment StartX=100 StartY=-83.9 StartZ=0 EndX=109.8 EndY=-78.242 EndZ=0
    g25: LineSegment StartX=109.8 StartY=-78.242 StartZ=0 EndX=109.8 EndY=-57.758 EndZ=0
    g26: LineSegment StartX=109.8 StartY=-57.758 StartZ=0 EndX=100 EndY=-52.1 EndZ=0
    g27: LineSegment StartX=100 StartY=-52.1 StartZ=0 EndX=100 EndY=-31.9 EndZ=0
    g28: LineSegment StartX=100 StartY=-31.9 StartZ=0 EndX=109.8 EndY=-26.242 EndZ=0
    g29: LineSegment StartX=109.8 StartY=-26.242 StartZ=0 EndX=109.8 EndY=0 EndZ=0
    g30: LineSegment StartX=109.8 StartY=0 StartZ=0 EndX=-109.8 EndY=0 EndZ=0
    g31: LineSegment StartX=-30.1 StartY=-175 StartZ=0 EndX=30.1 EndY=-175 EndZ=0
    g32: LineSegment StartX=-109.8 StartY=-175 StartZ=0 EndX=-49.9 EndY=-175 EndZ=0
    g33: LineSegment StartX=-100 StartY=-31.9 StartZ=0 EndX=-100 EndY=-52.1 EndZ=0
    g34: LineSegment StartX=-100 StartY=-83.9 StartZ=0 EndX=-100 EndY=-104.1 EndZ=0
    g35: LineSegment StartX=-100 StartY=-135.9 StartZ=0 EndX=-100 EndY=-156.1 EndZ=0
    g36: LineSegment StartX=-100 StartY=0 StartZ=0 EndX=-100 EndY=-235 EndZ=0
    g37: LineSegment StartX=-109.8 StartY=0 StartZ=0 EndX=-109.8 EndY=-235 EndZ=0
    g38: LineSegment StartX=-117.5 StartY=-175 StartZ=0 EndX=117.5 EndY=-175 EndZ=0
    g39: LineSegment StartX=-117.5 StartY=-184.8 StartZ=0 EndX=117.5 EndY=-184.8 EndZ=0
    g40: GeomPoint X=-30 Y=-175 Z=0
    g41: GeomPoint X=-50 Y=-175 Z=0
    g42: GeomPoint X=-100 Y=-32 Z=0
    g43: GeomPoint X=-100 Y=-52 Z=0
    g44: GeomPoint X=-100 Y=-84 Z=0
    g45: GeomPoint X=-100 Y=-104 Z=0
    g46: GeomPoint X=-100 Y=-136 Z=0
    g47: GeomPoint X=-100 Y=-156 Z=0
    g48: Circle CenterX=-40 CenterY=-180 CenterZ=0 NormalX=0 NormalY=0 NormalZ=1 AngleXU=0 Radius=1.5
    g49: Circle CenterX=40 CenterY=-180 CenterZ=0 NormalX=0 NormalY=0 NormalZ=1 AngleXU=0 Radius=1.5
    g50: LineSegment StartX=-117.5 StartY=-170 StartZ=0 EndX=117.5 EndY=-170 EndZ=0
    g51: Circle CenterX=-24 CenterY=-170 CenterZ=0 NormalX=0 NormalY=0 NormalZ=1 AngleXU=0 Radius=1.5
    g52: Circle CenterX=24 CenterY=-170 CenterZ=0 NormalX=0 NormalY=0 NormalZ=1 AngleXU=0 Radius=1.5
    g53: Circle CenterX=-82 CenterY=-170 CenterZ=0 NormalX=0 NormalY=0 NormalZ=1 AngleXU=0 Radius=1.5
    g54: Circle CenterX=82 CenterY=-170 CenterZ=0 NormalX=0 NormalY=0 NormalZ=1 AngleXU=0 Radius=1.5
    g55: LineSegment StartX=-105 StartY=0 StartZ=0 EndX=-105 EndY=-235 EndZ=0
    g56: Circle CenterX=-105 CenterY=-16 CenterZ=0 NormalX=0 NormalY=0 NormalZ=1 AngleXU=0 Radius=1.5
    g57: Circle CenterX=105 CenterY=-16 CenterZ=0 NormalX=0 NormalY=0 NormalZ=1 AngleXU=0 Radius=1.5
    g58: Circle CenterX=-105 CenterY=-68 CenterZ=0 NormalX=0 NormalY=0 NormalZ=1 AngleXU=0 Radius=1.5
    g59: Circle CenterX=105 CenterY=-68 CenterZ=0 NormalX=0 NormalY=0 NormalZ=1 AngleXU=0 Radius=1.5
    g60: Circle CenterX=-105 CenterY=-120 CenterZ=0 NormalX=0 NormalY=0 NormalZ=1 AngleXU=0 Radius=1.5
    g61: Circle CenterX=105 CenterY=-120 CenterZ=0 NormalX=0 NormalY=0 NormalZ=1 AngleXU=0 Radius=1.5
    g62: Circle CenterX=-105 CenterY=-170 CenterZ=0 NormalX=0 NormalY=0 NormalZ=1 AngleXU=0 Radius=1.5
    g63: Circle CenterX=105 CenterY=-170 CenterZ=0 NormalX=0 NormalY=0 NormalZ=1 AngleXU=0 Radius=1.5
  constraints (156):
    c: Coincident(g0,g1)
    c: Coincident(g2,g3)
    c: Coincident(g3,g4)
    c: Coincident(g5,g6)
    c: Coincident(g6,g7)
    c: Coincident(g8,g9)
    c: Coincident(g9,g32)
    c: Coincident(g10,g11)
    c: Coincident(g11,g12)
    c: Coincident(g31,g13)
    c: Coincident(g13,g14)
    c: Coincident(g14,g15)
    c: Coincident(g16,g17)
    c: Coincident(g17,g18)
    c: Coincident(g18,g19)
    c: Coincident(g19,g20)
    c: Coincident(g20,g21)
    c: Coincident(g21,g22)
    c: Coincident(g22,g23)
    c: Coincident(g23,g24)
    c: Coincident(g24,g25)
    c: Coincident(g25,g26)
    c: Coincident(g26,g27)
    c: Coincident(g27,g28)
    c: Coincident(g28,g29)
    c: Coincident(g29,g30)
    c: Coincident(g30,g0)
    c: Parallel(g1,g4)
    c: Parallel(g1,g7)
    c: Parallel(g2,g5)
    c: Parallel(g2,g8)
    c: Symmetric(g0,g29,g-2)
    c: Symmetric(g0,g28,g-2)
    c: Symmetric(g1,g27,g-2)
    c: Symmetric(g2,g26,g-2)
    c: Symmetric(g2,g25,g-2)
    c: Symmetric(g3,g24,g-2)
    c: Symmetric(g4,g23,g-2)
    c: Symmetric(g5,g22,g-2)
    c: Symmetric(g5,g21,g-2)
    c: Symmetric(g6,g20,g-2)
    c: Symmetric(g7,g19,g-2)
    c: Symmetric(g8,g18,g-2)
    c: Symmetric(g8,g17,g-2)
    c: Symmetric(g9,g16,g-2)
    c: Symmetric(g10,g15,g-2)
    c: Symmetric(g10,g14,g-2)
    c: Symmetric(g11,g13,g-2)
    c: Symmetric(g12,g31,g-2)
    c: Angle(g1) = -0.523599
    c: Angle(g2) = -2.61799
    c: Symmetric(g38,g38,g-2)
    c: Symmetric(g39,g39,g-2)
    c: DistanceX(g39,g39) = 235
    c: Equal(g39,g38)
    c: DistanceY(g38) = -175
    c: DistanceY(g39,g38) = 9.8
    c: Coincident(g31,g12)
    c: PointOnObject(g40,g38)
    c: PointOnObject(g41,g38)
    c: DistanceX(g40) = -30
    c: DistanceX(g41,g40) = 20
    c: DistanceX(g41,g10) = 0.1
    c: DistanceX(g12,g40) = 0.1
    c: PointOnObject(g12,g38)
    c: PointOnObject(g11,g39)
    c: PointOnObject(g10,g39)
    c: PointOnObject(g10,g38)
    c: PointOnObject(g9,g38)
    c: PointOnObject(g42,g36)
    c: PointOnObject(g43,g36)
    c: PointOnObject(g44,g36)
    c: PointOnObject(g45,g36)
    c: PointOnObject(g46,g36)
    c: PointOnObject(g47,g36)
    c: Coincident(g1,g33)
    c: Coincident(g33,g2)
    c: Coincident(g4,g34)
    c: Coincident(g5,g34)
    c: Coincident(g7,g35)
    c: Coincident(g8,g35)
    c: PointOnObject(g9,g37)
    c: PointOnObject(g8,g37)
    c: PointOnObject(g6,g37)
    c: PointOnObject(g5,g37)
    c: PointOnObject(g3,g37)
    c: PointOnObject(g2,g37)
    c: PointOnObject(g0,g37)
    c: PointOnObject(g0,g37)
    c: PointOnObject(g0,g-1)
    c: DistanceY(g42) = -32
    c: DistanceY(g43,g42) = 20
    c: DistanceY(g44,g43) = 32
    c: DistanceY(g45,g44) = 20
    c: DistanceY(g46,g45) = 32
    c: DistanceY(g47,g46) = 20
    c: DistanceY(g42,g1) = 0.1
    c: DistanceY(g2,g43) = 0.1
    c: DistanceY(g44,g4) = 0.1
    c: DistanceY(g5,g45) = 0.1
    c: DistanceY(g46,g7) = 0.1
    c: DistanceY(g8,g47) = 0.1
    c: PointOnObject(g1,g36)
    c: PointOnObject(g2,g36)
    c: PointOnObject(g4,g36)
    c: PointOnObject(g5,g36)
    c: PointOnObject(g7,g36)
    c: PointOnObject(g8,g36)
    c: Coincident(g16,g15)
    c: Coincident(g32,g10)
    c: Angle(g12) = 1.0472
    c: Angle(g10) = -1.0472
    c: Symmetric(g48,g49,g-2)
    c: DistanceX(g48) = -40
    c: DistanceY(g48) = -180
    c: Equal(g48,g49)
    c: Diameter(g48) = 3
    c: Symmetric(g50,g50,g-2)
    c: Equal(g39,g50)
    c: DistanceY(g38,g50) = 5
    c: PointOnObject(g51,g50)
    c: PointOnObject(g53,g50)
    c: Symmetric(g51,g52,g-2)
    c: Symmetric(g53,g54,g-2)
    c: DistanceX(g51) = -24
    c: DistanceX(g53) = -82
    c: Equal(g51,g48)
    c: Equal(g52,g48)
    c: Equal(g53,g48)
    c: Equal(g54,g48)
    c: DistanceX(g36) = -100
    c: DistanceX(g37,g36) = 9.8
    c: Vertical(g36)
    c: Vertical(g37)
    c: PointOnObject(g36,g-1)
    c: PointOnObject(g37,g-1)
    c: DistanceY(g37,g37) = 235
    c: Equal(g37,g36)
    c: PointOnObject(g55,g-1)
    c: Vertical(g55)
    c: Equal(g55,g37)
    c: DistanceX(g55,g36) = 5
    c: PointOnObject(g56,g55)
    c: PointOnObject(g58,g55)
    c: PointOnObject(g60,g55)
    c: PointOnObject(g62,g55)
    c: Symmetric(g56,g57,g-2)
    c: Symmetric(g58,g59,g-2)
    c: Symmetric(g60,g61,g-2)
    c: Symmetric(g62,g63,g-2)
    c: DistanceY(g56) = -16
    c: DistanceY(g58,g56) = 52
    c: DistanceY(g60,g58) = 52
    c: PointOnObject(g62,g50)
    c: Equal(g56, g57-g63) x7
    c: Diameter(g56) = 3
FEATURE [PartDesign::Pad] Pad033
  Direction = (0,0,1)
  Length = 7
  Length2 = 10
  Profile = -> Sketch089
  ReferenceAxis = -> Sketch089 [N_Axis]
  Type = 0
  expr: Length = <<Variables>>.WallThickness
FEATURE [App::Link] StepperRight
  AssemblyType = Part::Link
  AttachedBy = #LCS_Nema17_Origin
  AttachedTo = StepperMountRight#LCS_StepperRightOrigin
  LinkPlacement = pos=(100,143.5,-51) rot=(0,0,1;0rad)
  LinkedObject = -> <external Drive.FCStd>#Part
  Placement = pos=(100,143.5,-51) rot=(0,0,1;0rad)
  SolverId = Asm4EE
  expr: Placement = StepperMountRight.Placement * LCS_StepperRightOrigin.Placement * AttachmentOffset * Drive#LCS_Nema17_Origin.Placement ^ -1
FEATURE [PartDesign::CoordinateSystem] LCS_0
  AttacherType = Attacher::AttachEngine3D
  MapMode = 2
  Support = -> [X_Axis039]
FEATURE [Sketcher::SketchObject] Sketch090
  FullyConstrained = true
  MapMode = 5
  Support = -> [XY_Plane039]
  expr: Constraints[62] = -(<<Variables>>.PullyDiameterDrive + <<Variables>>.PullyDiameterIdler) / 2
  expr: Constraints[63] = <<Variables>>.PullyDiameterIdler
  expr: Constraints[84] = <<Variables>>.CavitySpacingX + <<Variables>>.WallThickness
  expr: Constraints[85] = -(<<Variables>>.CavitySpacingY + <<Variables>>.WallThickness)
  expr: Constraints[87] = <<Variables>>.CavitySpacingY + <<Variables>>.WallThickness
  sketch-geometry (33):
    g0: LineSegment StartX=7.34847 StartY=2e-16 StartZ=0 EndX=17 EndY=2e-16 EndZ=0
    g1: LineSegment StartX=17 StartY=2e-16 StartZ=0 EndX=17 EndY=-17 EndZ=0
    g2: LineSegment StartX=18 StartY=-64.5 StartZ=0 EndX=-23.5 EndY=-64.5 EndZ=0
    g3: LineSegment StartX=17 StartY=-17 StartZ=0 EndX=21 EndY=-21 EndZ=0
    g4: LineSegment StartX=21 StartY=-21 StartZ=0 EndX=21 EndY=-61.5 EndZ=0
    g5: Circle CenterX=0 CenterY=-43.5 CenterZ=0 NormalX=0 NormalY=0 NormalZ=1 AngleXU=0 Radius=12.5
    g6: LineSegment StartX=18 StartY=-64.5 StartZ=0 EndX=21 EndY=-61.5 EndZ=0
    g7: LineSegment StartX=-15.5 StartY=-28 StartZ=0 EndX=15.5 EndY=-28 EndZ=0
    g8: LineSegment StartX=15.5 StartY=-28 StartZ=0 EndX=15.5 EndY=-59 EndZ=0
    g9: LineSegment StartX=15.5 StartY=-59 StartZ=0 EndX=-15.5 EndY=-59 EndZ=0
    g10: LineSegment StartX=-15.5 StartY=-59 StartZ=0 EndX=-15.5 EndY=-28 EndZ=0
    g11: Circle CenterX=-15.5 CenterY=-28 CenterZ=0 NormalX=0 NormalY=0 NormalZ=1 AngleXU=0 Radius=1.5
    g12: Circle CenterX=15.5 CenterY=-28 CenterZ=0 NormalX=0 NormalY=0 NormalZ=1 AngleXU=0 Radius=1.5
    g13: Circle CenterX=15.5 CenterY=-59 CenterZ=0 NormalX=0 NormalY=0 NormalZ=1 AngleXU=0 Radius=1.5
    g14: Circle CenterX=-15.5 CenterY=-59 CenterZ=0 NormalX=0 NormalY=0 NormalZ=1 AngleXU=0 Radius=1.5
    g15: LineSegment StartX=-21 StartY=-22.5 StartZ=0 EndX=21 EndY=-22.5 EndZ=0
    g16: LineSegment StartX=21 StartY=-22.5 StartZ=0 EndX=21 EndY=-64.5 EndZ=0
    g17: LineSegment StartX=21 StartY=-64.5 StartZ=0 EndX=-21 EndY=-64.5 EndZ=0
    g18: LineSegment StartX=-21 StartY=-64.5 StartZ=0 EndX=-21 EndY=-22.5 EndZ=0
    g19: LineSegment StartX=-26.5 StartY=64.5 StartZ=0 EndX=-26.5 EndY=-64.5 EndZ=0
    g20: LineSegment StartX=-23 StartY=-17 StartZ=0 EndX=-23 EndY=0 EndZ=0
    g21: LineSegment StartX=-23.5 StartY=-64.5 StartZ=0 EndX=-26.5 EndY=-61.5 EndZ=0
    g22: LineSegment StartX=-26.5 StartY=-61.5 StartZ=0 EndX=-26.5 EndY=-20 EndZ=0
    g23: Circle CenterX=0 CenterY=0 CenterZ=0 NormalX=0 NormalY=0 NormalZ=1 AngleXU=0 Radius=9
    g24: Circle CenterX=-12.73 CenterY=-12.73 CenterZ=0 NormalX=0 NormalY=0 NormalZ=1 AngleXU=0 Radius=9
    g25: Circle CenterX=-12.73 CenterY=-12.73 CenterZ=0 NormalX=0 NormalY=0 NormalZ=1 AngleXU=0 Radius=1.25
    g26: Circle CenterX=0 CenterY=0 CenterZ=0 NormalX=0 NormalY=0 NormalZ=1 AngleXU=0 Radius=1.25
    g27: ArcOfCircle CenterX=0 CenterY=0 CenterZ=0 NormalX=0 NormalY=0 NormalZ=1 AngleXU=0 Radius=6 StartAngle=0.201358 EndAngle=2.94023
    g28: LineSegment StartX=-23 StartY=-9e-16 StartZ=0 EndX=-7.34847 EndY=-9e-16 EndZ=0
    g29: ArcOfCircle CenterX=-7.34847 CenterY=1.5 CenterZ=0 NormalX=0 NormalY=0 NormalZ=1 AngleXU=0 Radius=1.5 StartAngle=4.71239 EndAngle=6.08183
    g30: ArcOfCircle CenterX=7.34847 CenterY=1.5 CenterZ=0 NormalX=0 NormalY=0 NormalZ=1 AngleXU=0 Radius=1.5 StartAngle=3.34295 EndAngle=4.71239
    g31: LineSegment StartX=-26.5 StartY=-20 StartZ=0 EndX=-23.5 EndY=-17 EndZ=0
    g32: LineSegment StartX=-23.5 StartY=-17 StartZ=0 EndX=-23 EndY=-17 EndZ=0
  constraints (89):
    c: Coincident(g0,g1)
    c: Coincident(g2,g21)
    c: Horizontal(g0)
    c: Vertical(g1)
    c: Coincident(g3,g1)
    c: Coincident(g3,g4)
    c: Angle(g3) = -0.785398
    c: PointOnObject(g5,g-2)
    c: Coincident(g4,g6)
    c: Coincident(g2,g6)
    c: Angle(g6) = 0.785398
    c: DistanceX(g2,g4) = 3
    c: Coincident(g7,g8)
    c: Coincident(g8,g9)
    c: Coincident(g9,g10)
    c: Coincident(g10,g7)
    c: Horizontal(g7)
    c: Horizontal(g9)
    c: Vertical(g8)
    c: Vertical(g10)
    c: Symmetric(g7,g8,g5)
    c: Equal(g7,g10)
    c: DistanceY(g10,g10) = 31
    c: Coincident(g11,g7)
    c: Coincident(g12,g7)
    c: Coincident(g13,g8)
    c: Coincident(g14,g9)
    c: Equal(g11,g12)
    c: Equal(g11,g13)
    c: Equal(g11,g14)
    c: Diameter(g11) = 3
    c: Coincident(g15,g16)
    c: Coincident(g16,g17)
    c: Coincident(g17,g18)
    c: Coincident(g18,g15)
    c: Horizontal(g15)
    c: Horizontal(g17)
    c: Vertical(g16)
    c: Vertical(g18)
    c: Symmetric(g15,g16,g5)
    c: Equal(g15,g18)
    c: DistanceY(g18,g18) = 42
    c: PointOnObject(g3,g16)
    c: PointOnObject(g4,g16)
    c: PointOnObject(g2,g17)
    c: PointOnObject(g2,g17)
    c: Symmetric(g19,g19,g-1)
    c: PointOnObject(g19,g17)
    c: DistanceX(g19,g17) = 5.5
    c: Coincident(g32,g20)
    c: Vertical(g20)
    c: Coincident(g22,g31)
    c: Coincident(g21,g22)
    c: Equal(g6,g21)
    c: PointOnObject(g21,g19)
    c: PointOnObject(g31,g19)
    c: Parallel(g3,g21)
    c: Horizontal(g20,g1)
    c: Diameter(g5) = 25
    c: PointOnObject(g23,g-2)
    c: Diameter(g23) = 18
    c: Equal(g23,g24)
    c: DistanceX(g24) = -12.73
    c: DistanceY(g24,g23) = 12.73
    c: Coincident(g25,g24)
    c: Coincident(g26,g23)
    c: Equal(g25,g26)
    c: Diameter(g25) = 2.5
    c: Coincident(g27,g26)
    c: Diameter(g27) = 12
    c: Coincident(g28,g20)
    c: Horizontal(g28)
    c: Diameter(g29) = 3
    c: Tangent(g29,g28) = -1.5708
    c: Tangent(g29,g27) = 1.5708
    c: Diameter(g30) = 3
    c: Tangent(g30,g0) = -1.5708
    c: Tangent(g27,g30) = 1.5708
    c: Coincident(g31,g32)
    c: Horizontal(g32)
    c: Parallel(g6,g31)
    c: Equal(g31,g6)
    c: PointOnObject(g26,g-1)
    c: DistanceX(g20) = -23
    c: DistanceX(g0) = 17
    c: DistanceY(g1) = -17
    c: DistanceY(g15,g1) = 5.5
    c: DistanceY(g1,g1) = 17
    c: Equal(g20,g1)
FEATURE [PartDesign::Pad] Pad034
  Direction = (0,0,1)
  Length = 35
  Length2 = 10
  Profile = -> Sketch090
  ReferenceAxis = -> Sketch090 [N_Axis]
  Type = 0
FEATURE [App::Link] StepperMountRight  label="StepperMountRight001"
  AssemblyType = Part::Link
  AttachedBy = #LCS_StepperMountRightOrigin
  AttachedTo = Parent Assembly#LCS_Origin
  LinkPlacement = pos=(100,100,-46) rot=(-1,0,0;3.14159rad)
  LinkedObject = -> Part015
  Placement = pos=(100,100,-46) rot=(-1,0,0;3.14159rad)
  SolverId = Asm4EE
  expr: Placement = LCS_Origin.Placement * AttachmentOffset * LCS_StepperMountRightOrigin.Placement ^ -1
FEATURE [PartDesign::CoordinateSystem] LCS_StepperMountRightOrigin
  AttacherType = Attacher::AttachEngine3D
  AttachmentOffset = pos=(-100,100,-46) rot=(1,0,0;3.14159rad)
  MapMode = 2
  Placement = pos=(-100,100,-46) rot=(1,0,0;3.14159rad)
  Support = -> [X_Axis038]
  expr: .AttachmentOffset.Base.x = -<<Variables>>.GantorySpacing / 2
  expr: .AttachmentOffset.Base.y = <<Variables>>.GantorySpacing / 2
FEATURE [PartDesign::CoordinateSystem] LCS_StepperRightOrigin
  AttacherType = Attacher::AttachEngine3D
  AttachmentOffset = pos=(0,-43.5,5) rot=(1,0,0;3.14159rad)
  MapMode = 2
  Placement = pos=(0,-43.5,5) rot=(1,0,0;3.14159rad)
  Support = -> [X_Axis038]
  expr: .AttachmentOffset.Base.y = -(Variables.CavitySpacingY + <<Variables>>.WallThickness + 5.5 + 42 / 2)
FEATURE [Sketcher::SketchObject] Sketch091
  AttachmentOffset = pos=(0,0,5) rot=(0,0,1;0rad)
  FullyConstrained = true
  MapMode = 5
  Placement = pos=(0,0,5) rot=(0,0,1;0rad)
  Support = -> [XY_Plane039]
  expr: Constraints[12] = -(Variables.CavitySpacingY + <<Variables>>.WallThickness + 5)
  sketch-geometry (5):
    g0: LineSegment StartX=-21.5 StartY=-22 StartZ=0 EndX=21.5 EndY=-22 EndZ=0
    g1: LineSegment StartX=21.5 StartY=-22 StartZ=0 EndX=21.5 EndY=-65 EndZ=0
    g2: LineSegment StartX=21.5 StartY=-65 StartZ=0 EndX=-21.5 EndY=-65 EndZ=0
    g3: LineSegment StartX=-21.5 StartY=-65 StartZ=0 EndX=-21.5 EndY=-22 EndZ=0
    g4: GeomPoint X=0 Y=-43.5 Z=0
  constraints (13):
    c: Coincident(g0,g1)
    c: Coincident(g1,g2)
    c: Coincident(g2,g3)
    c: Coincident(g3,g0)
    c: Horizontal(g0)
    c: Horizontal(g2)
    c: Vertical(g1)
    c: Vertical(g3)
    c: PointOnObject(g4,g-2)
    c: Symmetric(g0,g1,g4)
    c: Equal(g0,g3)
    c: DistanceY(g3,g3) = 43
    c: DistanceY(g0) = -22
FEATURE [PartDesign::Pocket] Pocket036
  BaseFeature = -> Pad034
  Direction = (0,0,-1)
  Length = 5
  Length2 = 5
  Profile = -> Sketch091
  ReferenceAxis = -> Sketch091 [N_Axis]
  Reversed = true
  Type = 1
FEATURE [Sketcher::SketchObject] Sketch092
  AttachmentOffset = pos=(0,0,14) rot=(0,0,1;0rad)
  FullyConstrained = true
  MapMode = 5
  Placement = pos=(0,0,14) rot=(0,0,1;0rad)
  Support = -> [XY_Plane039]
  expr: Constraints[7] = -(<<Variables>>.CavitySpacingY + <<Variables>>.WallThickness)
  sketch-geometry (4):
    g0: LineSegment StartX=-40 StartY=20 StartZ=0 EndX=40 EndY=20 EndZ=0
    g1: LineSegment StartX=40 StartY=20 StartZ=0 EndX=40 EndY=-17 EndZ=0
    g2: LineSegment StartX=40 StartY=-17 StartZ=0 EndX=-40 EndY=-17 EndZ=0
    g3: LineSegment StartX=-40 StartY=-17 StartZ=0 EndX=-40 EndY=20 EndZ=0
  constraints (10):
    c: Coincident(g0,g1)
    c: Coincident(g1,g2)
    c: Coincident(g2,g3)
    c: Coincident(g3,g0)
    c: Vertical(g3)
    c: Symmetric(g2,g1,g-2)
    c: Symmetric(g0,g0,g-2)
    c: DistanceY(g2) = -17
    c: DistanceY(g0) = 20
    c: DistanceX(g2,g2) = 80
FEATURE [PartDesign::Pocket] Pocket037
  BaseFeature = -> Pocket036
  Direction = (0,0,-1)
  Length = 5
  Length2 = 5
  Profile = -> Sketch092
  ReferenceAxis = -> Sketch092 [N_Axis]
  Reversed = true
  Type = 1
FEATURE [Part::FeaturePython] Clone076  label="M3 inserted Nut001"  # Draft clone (typed FeaturePython)
  AttacherType = Attacher::AttachEngine3D
  Fuse = false
  Objects = -> [Body013]
  Placement = pos=(0,0,5) rot=(0,0,1;0rad)
  Scale = (1,1,1)
FEATURE [Part::FeaturePython] Clone077  label="M3 inserted Nut002"  # Draft clone (typed FeaturePython)
  AttacherType = Attacher::AttachEngine3D
  Fuse = false
  Objects = -> [Body013]
  Placement = pos=(-12.73,-12.73,5) rot=(0,0,1;0rad)
  Scale = (1,1,1)
  expr: .Placement.Base.x = -(<<Variables>>.PullyDiameterDrive + <<Variables>>.PullyDiameterIdler) / 2
  expr: .Placement.Base.y = -<<Variables>>.PullyDiameterIdler
FEATURE [Sketcher::SketchObject] Sketch093
  FullyConstrained = true
  MapMode = 5
  Support = -> [XY_Plane039]
  expr: Constraints[2] = -(Variables.CavitySpacingY - 4)
  sketch-geometry (1):
    g0: Circle CenterX=-10 CenterY=-6 CenterZ=0 NormalX=0 NormalY=0 NormalZ=1 AngleXU=0 Radius=3.5
  constraints (3):
    c: DistanceX(g0) = -10
    c: Diameter(g0) = 7
    c: DistanceY(g0) = -6
FEATURE [PartDesign::Hole] Hole032
  BaseFeature = -> Pocket037
  CustomThreadClearance = 0
  Depth = 25
  DepthType = 0
  Diameter = 3.4
  DrillForDepth = false
  DrillPoint = 1
  DrillPointAngle = 118
  HoleCutCountersinkAngle = 90
  HoleCutCustomValues = false
  HoleCutDepth = 9
  HoleCutDiameter = 6.1
  HoleCutType = 1
  ModelThread = false
  Profile = -> Sketch093
  Reversed = true
  Tapered = false
  TaperedAngle = 90
  ThreadClass = 0
  ThreadDepth = 25
  ThreadDepthType = 0
  ThreadDirection = 0
  ThreadFit = 0
  ThreadSize = 9
  ThreadType = 1
  Threaded = false
  UseCustomThreadClearance = false
FEATURE [PartDesign::SubShapeBinder] Binder
  BindCopyOnChange = 0
  BindMode = 0
  ClaimChildren = false
  Context = -> Part015 [StepperBracketRight.Binder.]
  Fuse = false
  MakeFace = true
  OffsetFill = false
  OffsetIntersection = false
  OffsetJoinType = 0
  OffsetOpenResult = false
  PartialLoad = false
  Placement = pos=(0,0,9) rot=(0,0,1;0rad)
  Relative = true
  Support = -> [Hole032[Sketch093.]]
  _Version = 2
FEATURE [PartDesign::Pad] Pad035
  BaseFeature = -> Hole032
  Direction = (0,0,1)
  Length = 0.1
  Length2 = 10
  Profile = -> Binder
  Type = 0
FEATURE [PartDesign::CoordinateSystem] LCS_UpperBracketRightOrigin  label="LCS_UpperBracketOrigin"
  AttacherType = Attacher::AttachEngine3D
  AttachmentOffset = pos=(0,110,-59) rot=(1,0,0;3.14159rad)
  MapMode = 3
  Placement = pos=(0,59,110) rot=(1,0,0;4.71239rad)
  Support = -> [X_Axis040]
  expr: .AttachmentOffset.Base.y = <<Variables>>.GantorySpacing / 2 + <<Variables>>.CavitySpacingY
FEATURE [Sketcher::SketchObject] Sketch094
  FullyConstrained = true
  MapMode = 5
  Support = -> [XY_Plane041]
  expr: Constraints[100] = <<Variables>>.FittingGap / 2
  expr: Constraints[101] = <<Variables>>.FittingGap / 2
  expr: Constraints[102] = <<Variables>>.FittingGap / 2
  expr: Constraints[34] = <<Variables>>.PullyDiameterIdler
  expr: Constraints[4] = <<Variables>>.GantorySpacing / 2
  sketch-geometry (40):
    g0: LineSegment StartX=100 StartY=-8.5 StartZ=0 EndX=100 EndY=-1.5 EndZ=0
    g1: LineSegment StartX=26.9 StartY=0 StartZ=0 EndX=26.9 EndY=9 EndZ=0
    g2: LineSegment StartX=20.9 StartY=15 StartZ=0 EndX=9.23 EndY=15 EndZ=0
    g3: LineSegment StartX=7.73 StartY=13.5 StartZ=0 EndX=7.73 EndY=6.5 EndZ=0
    g4: LineSegment StartX=9.23 StartY=5 StartZ=0 EndX=15 EndY=5 EndZ=0
    g5: LineSegment StartX=18 StartY=2 StartZ=0 EndX=18 EndY=-4 EndZ=0
    g6: LineSegment StartX=24 StartY=-10 StartZ=0 EndX=98.5 EndY=-10 EndZ=0
    g7: ArcOfCircle CenterX=15 CenterY=2 CenterZ=0 NormalX=0 NormalY=0 NormalZ=1 AngleXU=0 Radius=3 StartAngle=1e-16 EndAngle=1.5708
    g8: ArcOfCircle CenterX=24 CenterY=-4 CenterZ=0 NormalX=0 NormalY=0 NormalZ=1 AngleXU=0 Radius=6 StartAngle=3.14159 EndAngle=4.71239
    g9: GeomPoint X=18 Y=-10 Z=0
    g10: ArcOfCircle CenterX=9.23 CenterY=13.5 CenterZ=0 NormalX=0 NormalY=0 NormalZ=1 AngleXU=0 Radius=1.5 StartAngle=1.5708 EndAngle=3.14159
    g11: GeomPoint X=7.73 Y=15 Z=0
    g12: ArcOfCircle CenterX=9.23 CenterY=6.5 CenterZ=0 NormalX=0 NormalY=0 NormalZ=1 AngleXU=0 Radius=1.5 StartAngle=3.14159 EndAngle=4.71239
    g13: GeomPoint X=7.73 Y=5 Z=0
    g14: Circle CenterX=12.73 CenterY=10 CenterZ=0 NormalX=0 NormalY=0 NormalZ=1 AngleXU=0 Radius=1.25
    g15: Circle CenterX=24 CenterY=-5 CenterZ=0 NormalX=0 NormalY=0 NormalZ=1 AngleXU=0 Radius=1.25
    g16: Circle CenterX=56 CenterY=-5 CenterZ=0 NormalX=0 NormalY=0 NormalZ=1 AngleXU=0 Radius=1.25
    g17: Circle CenterX=82 CenterY=-5 CenterZ=0 NormalX=0 NormalY=0 NormalZ=1 AngleXU=0 Radius=1.25
    g18: LineSegment StartX=0 StartY=-5 StartZ=0 EndX=100 EndY=-5 EndZ=0
    g19: ArcOfCircle CenterX=20.9 CenterY=9 CenterZ=0 NormalX=0 NormalY=0 NormalZ=1 AngleXU=0 Radius=6 StartAngle=0 EndAngle=1.5708
    g20: GeomPoint X=26.9 Y=15 Z=0
    g21: LineSegment StartX=0 StartY=15 StartZ=0 EndX=100 EndY=15 EndZ=0
    g22: LineSegment StartX=53.1 StartY=0 StartZ=0 EndX=26.9 EndY=0 EndZ=0
    g23: LineSegment StartX=53.1 StartY=7 StartZ=0 EndX=53.1 EndY=0 EndZ=0
    g24: LineSegment StartX=73.9 StartY=10 StartZ=0 EndX=56.1 EndY=10 EndZ=0
    g25: LineSegment StartX=98.5 StartY=0 StartZ=0 EndX=76.9 EndY=0 EndZ=0
    g26: LineSegment StartX=76.9 StartY=0 StartZ=0 EndX=76.9 EndY=7 EndZ=0
    g27: Circle CenterX=65 CenterY=5 CenterZ=0 NormalX=0 NormalY=0 NormalZ=1 AngleXU=0 Radius=1.25
    g28: ArcOfCircle CenterX=56.1 CenterY=7 CenterZ=0 NormalX=0 NormalY=0 NormalZ=1 AngleXU=0 Radius=3 StartAngle=1.5708 EndAngle=3.14159
    g29: GeomPoint X=53.1 Y=10 Z=0
    g30: ArcOfCircle CenterX=73.9 CenterY=7 CenterZ=0 NormalX=0 NormalY=0 NormalZ=1 AngleXU=0 Radius=3 StartAngle=0 EndAngle=1.5708
    g31: GeomPoint X=76.9 Y=10 Z=0
    g32: LineSegment StartX=0 StartY=10 StartZ=0 EndX=100 EndY=10 EndZ=0
    g33: ArcOfCircle CenterX=98.5 CenterY=-1.5 CenterZ=0 NormalX=0 NormalY=0 NormalZ=1 AngleXU=0 Radius=1.5 StartAngle=0 EndAngle=1.5708
    g34: GeomPoint X=100 Y=0 Z=0
    g35: ArcOfCircle CenterX=98.5 CenterY=-8.5 CenterZ=0 NormalX=0 NormalY=0 NormalZ=1 AngleXU=0 Radius=1.5 StartAngle=4.71239 EndAngle=6.28319
    g36: GeomPoint X=100 Y=-10 Z=0
    g37: GeomPoint X=27 Y=15 Z=0
    g38: GeomPoint X=53 Y=15 Z=0
    g39: GeomPoint X=77 Y=15 Z=0
  constraints (103):
    c: Coincident(g22,g1)
    c: Vertical(g1)
    c: PointOnObject(g22,g-1)
    c: Vertical(g0)
    c: DistanceX(g36) = 100
    c: Vertical(g3)
    c: Horizontal(g6)
    c: Horizontal(g4)
    c: Vertical(g5)
    c: Tangent(g4,g7) = 1.5708
    c: Tangent(g7,g5) = 1.5708
    c: Diameter(g7) = 6
    c: DistanceY(g13,g11) = 10
    c: DistanceX(g9) = 18
    c: PointOnObject(g9,g5)
    c: PointOnObject(g9,g6)
    c: Tangent(g5,g8) = -1.5708
    c: Tangent(g6,g8) = -1.5708
    c: PointOnObject(g11,g2)
    c: PointOnObject(g11,g3)
    c: Tangent(g2,g10) = -1.5708
    c: Tangent(g3,g10) = -1.5708
    c: PointOnObject(g13,g3)
    c: PointOnObject(g13,g4)
    c: Tangent(g3,g12) = -1.5708
    c: Tangent(g4,g12) = -1.5708
    c: Diameter(g8) = 12
    c: Equal(g12,g10)
    c: Diameter(g12) = 3
    c: Equal(g14,g15)
    c: Equal(g14,g16)
    c: Equal(g14,g17)
    c: Diameter(g14) = 2.5
    c: DistanceY(g14) = 10
    c: DistanceX(g14) = 12.73
    c: DistanceX(g15) = 24
    c: Horizontal(g18)
    c: PointOnObject(g18,g-2)
    c: PointOnObject(g18,g0)
    c: DistanceY(g18) = -5
    c: PointOnObject(g16,g18)
    c: PointOnObject(g17,g18)
    c: DistanceX(g16) = 56
    c: DistanceX(g17,g34) = 18
    c: DistanceX(g11,g14) = 5
    c: PointOnObject(g20,g2)
    c: PointOnObject(g20,g1)
    c: Tangent(g2,g19) = -1.5708
    c: Tangent(g1,g19) = -1.5708
    c: Equal(g19,g8)
    c: PointOnObject(g21,g-2)
    c: Horizontal(g21)
    c: Equal(g21,g18)
    c: DistanceY(g21) = 15
    c: PointOnObject(g11,g21)
    c: Coincident(g23,g22)
    c: Horizontal(g22)
    c: Coincident(g25,g26)
    c: PointOnObject(g2,g21)
    c: Vertical(g23)
    c: Vertical(g26)
    c: PointOnObject(g25,g-1)
    c: PointOnObject(g34,g-1)
    c: DistanceX(g27) = 65
    c: DistanceY(g27) = 5
    c: Equal(g27,g14)
    c: PointOnObject(g29,g23)
    c: PointOnObject(g29,g24)
    c: Tangent(g23,g28) = -1.5708
    c: Tangent(g24,g28) = -1.5708
    c: PointOnObject(g31,g24)
    c: PointOnObject(g31,g26)
    c: Tangent(g24,g30) = -1.5708
    c: Tangent(g26,g30) = -1.5708
    c: PointOnObject(g32,g-2)
    c: Horizontal(g32)
    c: Equal(g32,g18)
    c: DistanceY(g32) = 10
    c: PointOnObject(g29,g32)
    c: PointOnObject(g31,g32)
    c: Equal(g28,g7)
    c: Equal(g7,g30)
    c: PointOnObject(g34,g25)
    c: PointOnObject(g34,g0)
    c: Tangent(g25,g33) = -1.5708
    c: Tangent(g0,g33) = -1.5708
    c: PointOnObject(g36,g0)
    c: PointOnObject(g36,g6)
    c: Tangent(g0,g35) = -1.5708
    c: Tangent(g6,g35) = -1.5708
    c: Equal(g33,g12)
    c: Equal(g35,g12)
    c: PointOnObject(g15,g18)
    c: PointOnObject(g37,g21)
    c: PointOnObject(g38,g21)
    c: PointOnObject(g39,g21)
    c: DistanceX(g37) = 27
    c: DistanceX(g37,g38) = 26
    c: DistanceX(g39) = 77
    c: DistanceY(g36) = -10
    c: DistanceX(g20,g37) = 0.1
    c: DistanceX(g38,g29) = 0.1
    c: DistanceX(g31,g39) = 0.1
FEATURE [PartDesign::Pad] Pad036
  Direction = (0,0,1)
  Length = 10
  Length2 = 10
  Profile = -> Sketch094
  ReferenceAxis = -> Sketch094 [N_Axis]
  Type = 0
FEATURE [App::Link] UpperBracket  label="UpperBracket001"
  AssemblyType = Part::Link
  AttachedBy = #LCS_UpperBracketRightOrigin
  AttachedTo = Parent Assembly#LCS_Origin
  LinkPlacement = pos=(0,110,-59) rot=(1,0,0;1.5708rad)
  LinkedObject = -> Part016
  Placement = pos=(0,110,-59) rot=(1,0,0;1.5708rad)
  SolverId = Asm4EE
  expr: Placement = LCS_Origin.Placement * AttachmentOffset * LCS_UpperBracketRightOrigin.Placement ^ -1
FEATURE [Sketcher::SketchObject] Sketch095
  FullyConstrained = true
  MapMode = 5
  Placement = pos=(0,0,0) rot=(1,0,0;1.5708rad)
  Support = -> [XZ_Plane041]
  expr: Constraints[4] = <<Variables>>.GantorySpacing
  sketch-geometry (9):
    g0: LineSegment StartX=-100 StartY=4 StartZ=0 EndX=100 EndY=4 EndZ=0
    g1: Circle CenterX=32 CenterY=4 CenterZ=0 NormalX=0 NormalY=0 NormalZ=1 AngleXU=0 Radius=1.25
    g2: Circle CenterX=48 CenterY=4 CenterZ=0 NormalX=0 NormalY=0 NormalZ=1 AngleXU=0 Radius=1.25
    g3: Circle CenterX=90 CenterY=4 CenterZ=0 NormalX=0 NormalY=0 NormalZ=1 AngleXU=0 Radius=1.25
    g4: Circle CenterX=-32 CenterY=4 CenterZ=0 NormalX=0 NormalY=0 NormalZ=1 AngleXU=0 Radius=1.25
    g5: Circle CenterX=-48 CenterY=4 CenterZ=0 NormalX=0 NormalY=0 NormalZ=1 AngleXU=0 Radius=1.25
    g6: Circle CenterX=-90 CenterY=4 CenterZ=0 NormalX=0 NormalY=0 NormalZ=1 AngleXU=0 Radius=1.25
    g7: GeomPoint X=-40 Y=4 Z=0
    g8: GeomPoint X=40 Y=4 Z=0
  constraints (16):
    c: PointOnObject(g1,g0)
    c: PointOnObject(g3,g0)
    c: DistanceY(g0) = 4
    c: Symmetric(g0,g0,g-2)
    c: DistanceX(g0,g0) = 200
    c: Symmetric(g4,g1,g-2)
    c: Symmetric(g5,g2,g-2)
    c: Symmetric(g6,g3,g-2)
    c: Equal(g1, g2-g6) x5
    c: Diameter(g1) = 2.5
    c: DistanceX(g1,g2) = 16
    c: PointOnObject(g7,g0)
    c: Symmetric(g7,g8,g-2)
    c: DistanceX(g7,g8) = 80
    c: Symmetric(g1,g2,g8)
    c: DistanceX(g3) = 90
FEATURE [PartDesign::Hole] Hole033
  BaseFeature = -> Pad036
  CustomThreadClearance = 0
  Depth = 25
  DepthType = 0
  Diameter = 2.5
  DrillForDepth = false
  DrillPoint = 1
  DrillPointAngle = 118
  HoleCutCountersinkAngle = 90
  HoleCutCustomValues = false
  HoleCutDepth = 0
  HoleCutDiameter = 6.1
  HoleCutType = 0
  ModelThread = false
  Profile = -> Sketch095
  Reversed = true
  Tapered = false
  TaperedAngle = 90
  ThreadClass = 0
  ThreadDepth = 25
  ThreadDepthType = 0
  ThreadDirection = 0
  ThreadFit = 0
  ThreadSize = 9
  ThreadType = 1
  Threaded = true
  UseCustomThreadClearance = false
FEATURE [Part::FeaturePython] Clone078  label="M3 inserted Nut UpperBracketRight 1"  # Draft clone (typed FeaturePython)
  AttacherType = Attacher::AttachEngine3D
  Fuse = false
  Objects = -> [Body013]
  Placement = pos=(82,-5,5) rot=(0,0,1;1.5708rad)
  Scale = (1,1,1)
  expr: .Placement.Base.x = <<Variables>>.GantorySpacing / 2 - 18
FEATURE [Part::FeaturePython] Clone079  label="M3 inserted Nut UpperBracketRight 2"  # Draft clone (typed FeaturePython)
  AttacherType = Attacher::AttachEngine3D
  Fuse = false
  Objects = -> [Body013]
  Placement = pos=(56,-5,5) rot=(0,0,1;1.5708rad)
  Scale = (1,1,1)
FEATURE [Part::FeaturePython] Clone080  label="M3 inserted Nut UpperBracketRight 3"  # Draft clone (typed FeaturePython)
  AttacherType = Attacher::AttachEngine3D
  Fuse = false
  Objects = -> [Body013]
  Placement = pos=(24,-5,5) rot=(0,0,1;1.5708rad)
  Scale = (1,1,1)
FEATURE [Part::FeaturePython] Clone081  label="M3 inserted Nut UpperBracketRight 4"  # Draft clone (typed FeaturePython)
  AttacherType = Attacher::AttachEngine3D
  Fuse = false
  Objects = -> [Body013]
  Placement = pos=(65,5,5) rot=(0,0,1;1.5708rad)
  Scale = (1,1,1)
FEATURE [Part::FeaturePython] Clone082  label="M3 inserted Nut UpperBracketRight 5"  # Draft clone (typed FeaturePython)
  AttacherType = Attacher::AttachEngine3D
  Fuse = false
  Objects = -> [Body013]
  Placement = pos=(90,-5,4) rot=(0.57735,-0.57735,0.57735;2.0944rad)
  Scale = (1,1,1)
FEATURE [Part::FeaturePython] Clone083  label="M3 inserted Nut UpperBracketRight 6"  # Draft clone (typed FeaturePython)
  AttacherType = Attacher::AttachEngine3D
  Fuse = false
  Objects = -> [Body013]
  Placement = pos=(48,-5,4) rot=(0.57735,-0.57735,0.57735;2.0944rad)
  Scale = (1,1,1)
FEATURE [Part::FeaturePython] Clone084  label="M3 inserted Nut UpperBracketRight 7"  # Draft clone (typed FeaturePython)
  AttacherType = Attacher::AttachEngine3D
  Fuse = false
  Objects = -> [Body013]
  Placement = pos=(32,-5,4) rot=(0.57735,-0.57735,0.57735;2.0944rad)
  Scale = (1,1,1)
FEATURE [Sketcher::SketchObject] Sketch096
  FullyConstrained = true
  MapMode = 5
  Support = -> [XY_Plane041]
  expr: Constraints[29] = <<Variables>>.PullyDiameterDrive + <<Variables>>.PullyDiameterIdler
  sketch-geometry (15):
    g0: LineSegment StartX=9.23 StartY=15 StartZ=0 EndX=16.23 EndY=15 EndZ=0
    g1: LineSegment StartX=17.73 StartY=13.5 StartZ=0 EndX=17.73 EndY=6.5 EndZ=0
    g2: LineSegment StartX=16.23 StartY=5 StartZ=0 EndX=9.23 EndY=5 EndZ=0
    g3: LineSegment StartX=7.73 StartY=6.5 StartZ=0 EndX=7.73 EndY=13.5 EndZ=0
    g4: ArcOfCircle CenterX=9.23 CenterY=13.5 CenterZ=0 NormalX=0 NormalY=0 NormalZ=1 AngleXU=0 Radius=1.5 StartAngle=1.5708 EndAngle=3.14159
    g5: GeomPoint X=7.73 Y=15 Z=0
    g6: ArcOfCircle CenterX=9.23 CenterY=6.5 CenterZ=0 NormalX=0 NormalY=0 NormalZ=1 AngleXU=0 Radius=1.5 StartAngle=3.14159 EndAngle=4.71239
    g7: GeomPoint X=7.73 Y=5 Z=0
    g8: ArcOfCircle CenterX=16.23 CenterY=6.5 CenterZ=0 NormalX=0 NormalY=0 NormalZ=1 AngleXU=0 Radius=1.5 StartAngle=4.71239 EndAngle=6.28319
    g9: GeomPoint X=17.73 Y=5 Z=0
    g10: ArcOfCircle CenterX=16.23 CenterY=13.5 CenterZ=0 NormalX=0 NormalY=0 NormalZ=1 AngleXU=0 Radius=1.5 StartAngle=2e-16 EndAngle=1.5708
    g11: GeomPoint X=17.73 Y=15 Z=0
    g12: GeomPoint X=12.73 Y=10 Z=0
    g13: GeomPoint X=-12.73 Y=10 Z=0
    g14: Circle CenterX=12.73 CenterY=10 CenterZ=0 NormalX=0 NormalY=0 NormalZ=1 AngleXU=0 Radius=1.5
  constraints (32):
    c: Horizontal(g0)
    c: Horizontal(g2)
    c: Vertical(g1)
    c: Vertical(g3)
    c: PointOnObject(g5,g0)
    c: PointOnObject(g5,g3)
    c: Tangent(g0,g4) = 1.5708
    c: Tangent(g3,g4) = 1.5708
    c: PointOnObject(g7,g3)
    c: PointOnObject(g7,g2)
    c: Tangent(g3,g6) = 1.5708
    c: Tangent(g2,g6) = 1.5708
    c: PointOnObject(g9,g2)
    c: PointOnObject(g9,g1)
    c: Tangent(g2,g8) = 1.5708
    c: Tangent(g1,g8) = 1.5708
    c: PointOnObject(g11,g1)
    c: PointOnObject(g11,g0)
    c: Tangent(g1,g10) = 1.5708
    c: Tangent(g0,g10) = 1.5708
    c: Equal(g4,g6)
    c: Equal(g4,g8)
    c: Equal(g4,g10)
    c: Diameter(g4) = 3
    c: Symmetric(g5,g9,g12)
    c: DistanceX(g5,g11) = 10
    c: DistanceY(g7,g5) = 10
    c: DistanceY(g12) = 10
    c: Symmetric(g13,g12,g-2)
    c: DistanceX(g13,g12) = 25.46
    c: Coincident(g14,g12)
    c: Diameter(g14) = 3
FEATURE [PartDesign::Pad] Pad037
  BaseFeature = -> Hole033
  Direction = (0,0,1)
  Length = 17
  Length2 = 10
  Profile = -> Sketch096
  ReferenceAxis = -> Sketch096 [N_Axis]
  Type = 0
FEATURE [PartDesign::Boolean] Boolean007
  BaseFeature = -> Pad037
  Group = -> [Clone078,Clone079,Clone080,Clone081,Clone082,Clone083,Clone084]
  Refine = true
  Type = 1
FEATURE [PartDesign::Body] Body022  label="UpperBracketRightBody"
  Group = -> [Sketch094,Pad036,Sketch095,Hole033,Pad037,Boolean007,Sketch096]
  Origin = -> Origin041
  Tip = -> Boolean007
FEATURE [PartDesign::SubShapeBinder] Binder009
  BindCopyOnChange = 0
  BindMode = 0
  ClaimChildren = false
  Context = -> Part005 [Body005.Hole034.Binder009.]
  Fuse = false
  MakeFace = true
  OffsetFill = false
  OffsetIntersection = false
  OffsetJoinType = 0
  OffsetOpenResult = false
  PartialLoad = false
  Placement = pos=(0,0,7) rot=(0,0,1;0rad)
  Relative = true
  Support = -> [Pad033[Sketch089.]]
  _Version = 2
  expr: .Placement.Base.z = <<Variables>>.WallThickness
FEATURE [PartDesign::Hole] Hole034
  BaseFeature = -> Pad033
  CustomThreadClearance = 0
  Depth = 25
  DepthType = 0
  Diameter = 3.4
  DrillForDepth = false
  DrillPoint = 1
  DrillPointAngle = 118
  HoleCutCountersinkAngle = 90
  HoleCutCustomValues = false
  HoleCutDepth = 3
  HoleCutDiameter = 6.1
  HoleCutType = 1
  ModelThread = false
  Profile = -> Binder009
  Tapered = false
  TaperedAngle = 90
  ThreadClass = 0
  ThreadDepth = 25
  ThreadDepthType = 0
  ThreadDirection = 0
  ThreadFit = 0
  ThreadSize = 9
  ThreadType = 1
  Threaded = false
  UseCustomThreadClearance = false
FEATURE [Sketcher::SketchObject] Sketch097
  FullyConstrained = true
  MapMode = 5
  Support = -> [XY_Plane012]
  expr: Constraints[153] = <<Variables>>.GantorySpacing - 70
  sketch-geometry (94):
    g0: Circle CenterX=-65 CenterY=-170 CenterZ=0 NormalX=0 NormalY=0 NormalZ=1 AngleXU=0 Radius=1.5
    g1: Circle CenterX=-65 CenterY=-160 CenterZ=0 NormalX=0 NormalY=0 NormalZ=1 AngleXU=0 Radius=1.5
    g2: LineSegment StartX=-65 StartY=-170 StartZ=0 EndX=-65 EndY=-160 EndZ=0
    g3: Circle CenterX=-65 CenterY=-150 CenterZ=0 NormalX=0 NormalY=0 NormalZ=1 AngleXU=0 Radius=1.5
    g4: LineSegment StartX=-65 StartY=-160 StartZ=0 EndX=-65 EndY=-150 EndZ=0
    g5: Circle CenterX=-65 CenterY=-140 CenterZ=0 NormalX=0 NormalY=0 NormalZ=1 AngleXU=0 Radius=1.5
    g6: LineSegment StartX=-65 StartY=-150 StartZ=0 EndX=-65 EndY=-140 EndZ=0
    g7: Circle CenterX=-65 CenterY=-130 CenterZ=0 NormalX=0 NormalY=0 NormalZ=1 AngleXU=0 Radius=1.5
    g8: LineSegment StartX=-65 StartY=-140 StartZ=0 EndX=-65 EndY=-130 EndZ=0
    g9: Circle CenterX=-65 CenterY=-120 CenterZ=0 NormalX=0 NormalY=0 NormalZ=1 AngleXU=0 Radius=1.5
    g10: LineSegment StartX=-65 StartY=-130 StartZ=0 EndX=-65 EndY=-120 EndZ=0
    g11: Circle CenterX=-65 CenterY=-110 CenterZ=0 NormalX=0 NormalY=0 NormalZ=1 AngleXU=0 Radius=1.5
    g12: LineSegment StartX=-65 StartY=-120 StartZ=0 EndX=-65 EndY=-110 EndZ=0
    g13: Circle CenterX=-65 CenterY=-100 CenterZ=0 NormalX=0 NormalY=0 NormalZ=1 AngleXU=0 Radius=1.5
    g14: LineSegment StartX=-65 StartY=-110 StartZ=0 EndX=-65 EndY=-100 EndZ=0
    g15: Circle CenterX=-65 CenterY=-90 CenterZ=0 NormalX=0 NormalY=0 NormalZ=1 AngleXU=0 Radius=1.5
    g16: LineSegment StartX=-65 StartY=-100 StartZ=0 EndX=-65 EndY=-90 EndZ=0
    g17: Circle CenterX=-65 CenterY=-80 CenterZ=0 NormalX=0 NormalY=0 NormalZ=1 AngleXU=0 Radius=1.5
    g18: LineSegment StartX=-65 StartY=-90 StartZ=0 EndX=-65 EndY=-80 EndZ=0
    g19: Circle CenterX=-65 CenterY=-70 CenterZ=0 NormalX=0 NormalY=0 NormalZ=1 AngleXU=0 Radius=1.5
    g20: LineSegment StartX=-65 StartY=-80 StartZ=0 EndX=-65 EndY=-70 EndZ=0
    g21: Circle CenterX=-65 CenterY=-60 CenterZ=0 NormalX=0 NormalY=0 NormalZ=1 AngleXU=0 Radius=1.5
    g22: LineSegment StartX=-65 StartY=-70 StartZ=0 EndX=-65 EndY=-60 EndZ=0
    g23: Circle CenterX=-65 CenterY=-50 CenterZ=0 NormalX=0 NormalY=0 NormalZ=1 AngleXU=0 Radius=1.5
    g24: LineSegment StartX=-65 StartY=-60 StartZ=0 EndX=-65 EndY=-50 EndZ=0
    g25: Circle CenterX=-65 CenterY=-40 CenterZ=0 NormalX=0 NormalY=0 NormalZ=1 AngleXU=0 Radius=1.5
    g26: LineSegment StartX=-65 StartY=-50 StartZ=0 EndX=-65 EndY=-40 EndZ=0
    g27: Circle CenterX=-65 CenterY=-30 CenterZ=0 NormalX=0 NormalY=0 NormalZ=1 AngleXU=0 Radius=1.5
    g28: LineSegment StartX=-65 StartY=-40 StartZ=0 EndX=-65 EndY=-30 EndZ=0
    g29: Circle CenterX=-65 CenterY=-20 CenterZ=0 NormalX=0 NormalY=0 NormalZ=1 AngleXU=0 Radius=1.5
    g30: LineSegment StartX=-65 StartY=-30 StartZ=0 EndX=-65 EndY=-20 EndZ=0
    g31: Circle CenterX=65 CenterY=-170 CenterZ=0 NormalX=0 NormalY=0 NormalZ=1 AngleXU=0 Radius=1.5
    g32: Circle CenterX=65 CenterY=-160 CenterZ=0 NormalX=0 NormalY=0 NormalZ=1 AngleXU=0 Radius=1.5
    g33: LineSegment StartX=65 StartY=-170 StartZ=0 EndX=65 EndY=-160 EndZ=0
    g34: Circle CenterX=65 CenterY=-150 CenterZ=0 NormalX=0 NormalY=0 NormalZ=1 AngleXU=0 Radius=1.5
    g35: LineSegment StartX=65 StartY=-160 StartZ=0 EndX=65 EndY=-150 EndZ=0
    g36: Circle CenterX=65 CenterY=-140 CenterZ=0 NormalX=0 NormalY=0 NormalZ=1 AngleXU=0 Radius=1.5
    g37: LineSegment StartX=65 StartY=-150 StartZ=0 EndX=65 EndY=-140 EndZ=0
    g38: Circle CenterX=65 CenterY=-130 CenterZ=0 NormalX=0 NormalY=0 NormalZ=1 AngleXU=0 Radius=1.5
    g39: LineSegment StartX=65 StartY=-140 StartZ=0 EndX=65 EndY=-130 EndZ=0
    g40: Circle CenterX=65 CenterY=-120 CenterZ=0 NormalX=0 NormalY=0 NormalZ=1 AngleXU=0 Radius=1.5
    g41: LineSegment StartX=65 StartY=-130 StartZ=0 EndX=65 EndY=-120 EndZ=0
    g42: Circle CenterX=65 CenterY=-110 CenterZ=0 NormalX=0 NormalY=0 NormalZ=1 AngleXU=0 Radius=1.5
    g43: LineSegment StartX=65 StartY=-120 StartZ=0 EndX=65 EndY=-110 EndZ=0
    g44: Circle CenterX=65 CenterY=-100 CenterZ=0 NormalX=0 NormalY=0 NormalZ=1 AngleXU=0 Radius=1.5
    g45: LineSegment StartX=65 StartY=-110 StartZ=0 EndX=65 EndY=-100 EndZ=0
    g46: Circle CenterX=65 CenterY=-90 CenterZ=0 NormalX=0 NormalY=0 NormalZ=1 AngleXU=0 Radius=1.5
    g47: LineSegment StartX=65 StartY=-100 StartZ=0 EndX=65 EndY=-90 EndZ=0
    g48: Circle CenterX=65 CenterY=-80 CenterZ=0 NormalX=0 NormalY=0 NormalZ=1 AngleXU=0 Radius=1.5
    g49: LineSegment StartX=65 StartY=-90 StartZ=0 EndX=65 EndY=-80 EndZ=0
    g50: Circle CenterX=65 CenterY=-70 CenterZ=0 NormalX=0 NormalY=0 NormalZ=1 AngleXU=0 Radius=1.5
    g51: LineSegment StartX=65 StartY=-80 StartZ=0 EndX=65 EndY=-70 EndZ=0
    g52: Circle CenterX=65 CenterY=-60 CenterZ=0 NormalX=0 NormalY=0 NormalZ=1 AngleXU=0 Radius=1.5
    g53: LineSegment StartX=65 StartY=-70 StartZ=0 EndX=65 EndY=-60 EndZ=0
    g54: Circle CenterX=65 CenterY=-50 CenterZ=0 NormalX=0 NormalY=0 NormalZ=1 AngleXU=0 Radius=1.5
    g55: LineSegment StartX=65 StartY=-60 StartZ=0 EndX=65 EndY=-50 EndZ=0
    g56: Circle CenterX=65 CenterY=-40 CenterZ=0 NormalX=0 NormalY=0 NormalZ=1 AngleXU=0 Radius=1.5
    g57: LineSegment StartX=65 StartY=-50 StartZ=0 EndX=65 EndY=-40 EndZ=0
    g58: Circle CenterX=65 CenterY=-30 CenterZ=0 NormalX=0 NormalY=0 NormalZ=1 AngleXU=0 Radius=1.5
    g59: LineSegment StartX=65 StartY=-40 StartZ=0 EndX=65 EndY=-30 EndZ=0
    g60: Circle CenterX=65 CenterY=-20 CenterZ=0 NormalX=0 NormalY=0 NormalZ=1 AngleXU=0 Radius=1.5
    g61: LineSegment StartX=65 StartY=-30 StartZ=0 EndX=65 EndY=-20 EndZ=0
    g62: Circle CenterX=0 CenterY=-170 CenterZ=0 NormalX=0 NormalY=0 NormalZ=1 AngleXU=0 Radius=1.5
    g63: Circle CenterX=6e-16 CenterY=-160 CenterZ=0 NormalX=0 NormalY=0 NormalZ=1 AngleXU=0 Radius=1.5
    g64: LineSegment StartX=0 StartY=-170 StartZ=0 EndX=6e-16 EndY=-160 EndZ=0
    g65: Circle CenterX=1.2e-15 CenterY=-150 CenterZ=0 NormalX=0 NormalY=0 NormalZ=1 AngleXU=0 Radius=1.5
    g66: LineSegment StartX=6e-16 StartY=-160 StartZ=0 EndX=1.2e-15 EndY=-150 EndZ=0
    g67: Circle CenterX=1.8e-15 CenterY=-140 CenterZ=0 NormalX=0 NormalY=0 NormalZ=1 AngleXU=0 Radius=1.5
    g68: LineSegment StartX=1.2e-15 StartY=-150 StartZ=0 EndX=1.8e-15 EndY=-140 EndZ=0
    g69: Circle CenterX=2.4e-15 CenterY=-130 CenterZ=0 NormalX=0 NormalY=0 NormalZ=1 AngleXU=0 Radius=1.5
    g70: LineSegment StartX=1.8e-15 StartY=-140 StartZ=0 EndX=2.4e-15 EndY=-130 EndZ=0
    g71: Circle CenterX=3.1e-15 CenterY=-120 CenterZ=0 NormalX=0 NormalY=0 NormalZ=1 AngleXU=0 Radius=1.5
    g72: LineSegment StartX=2.4e-15 StartY=-130 StartZ=0 EndX=3.1e-15 EndY=-120 EndZ=0
    g73: Circle CenterX=3.7e-15 CenterY=-110 CenterZ=0 NormalX=0 NormalY=0 NormalZ=1 AngleXU=0 Radius=1.5
    g74: LineSegment StartX=3.1e-15 StartY=-120 StartZ=0 EndX=3.7e-15 EndY=-110 EndZ=0
    g75: Circle CenterX=4.3e-15 CenterY=-100 CenterZ=0 NormalX=0 NormalY=0 NormalZ=1 AngleXU=0 Radius=1.5
    g76: LineSegment StartX=3.7e-15 StartY=-110 StartZ=0 EndX=4.3e-15 EndY=-100 EndZ=0
    g77: Circle CenterX=4.9e-15 CenterY=-90 CenterZ=0 NormalX=0 NormalY=0 NormalZ=1 AngleXU=0 Radius=1.5
    g78: LineSegment StartX=4.3e-15 StartY=-100 StartZ=0 EndX=4.9e-15 EndY=-90 EndZ=0
    g79: Circle CenterX=5.5e-15 CenterY=-80 CenterZ=0 NormalX=0 NormalY=0 NormalZ=1 AngleXU=0 Radius=1.5
    g80: LineSegment StartX=4.9e-15 StartY=-90 StartZ=0 EndX=5.5e-15 EndY=-80 EndZ=0
    g81: Circle CenterX=6.1e-15 CenterY=-70 CenterZ=0 NormalX=0 NormalY=0 NormalZ=1 AngleXU=0 Radius=1.5
    g82: LineSegment StartX=5.5e-15 StartY=-80 StartZ=0 EndX=6.1e-15 EndY=-70 EndZ=0
    g83: Circle CenterX=6.7e-15 CenterY=-60 CenterZ=0 NormalX=0 NormalY=0 NormalZ=1 AngleXU=0 Radius=1.5
    g84: LineSegment StartX=6.1e-15 StartY=-70 StartZ=0 EndX=6.7e-15 EndY=-60 EndZ=0
    g85: Circle CenterX=7.3e-15 CenterY=-50 CenterZ=0 NormalX=0 NormalY=0 NormalZ=1 AngleXU=0 Radius=1.5
    g86: LineSegment StartX=6.7e-15 StartY=-60 StartZ=0 EndX=7.3e-15 EndY=-50 EndZ=0
    g87: Circle CenterX=8e-15 CenterY=-40 CenterZ=0 NormalX=0 NormalY=0 NormalZ=1 AngleXU=0 Radius=1.5
    g88: LineSegment StartX=7.3e-15 StartY=-50 StartZ=0 EndX=8e-15 EndY=-40 EndZ=0
    g89: Circle CenterX=8.6e-15 CenterY=-30 CenterZ=0 NormalX=0 NormalY=0 NormalZ=1 AngleXU=0 Radius=1.5
    g90: LineSegment StartX=8e-15 StartY=-40 StartZ=0 EndX=8.6e-15 EndY=-30 EndZ=0
    g91: Circle CenterX=9.2e-15 CenterY=-20 CenterZ=0 NormalX=0 NormalY=0 NormalZ=1 AngleXU=0 Radius=1.5
    g92: LineSegment StartX=8.6e-15 StartY=-30 StartZ=0 EndX=9.2e-15 EndY=-20 EndZ=0
    g93: LineSegment StartX=-117.5 StartY=-170 StartZ=0 EndX=117.5 EndY=-170 EndZ=0
  constraints (236):
    c: Diameter(g0) = 3
    c: Diameter(g1) = 3
    c: Coincident(g0,g2)
    c: Coincident(g1,g2)
    c: Distance(g2) = 10
    c: Angle(g2) = 1.5708
    c: Diameter(g3) = 3
    c: Coincident(g1,g4)
    c: Coincident(g3,g4)
    c: Equal(g2,g4)
    c: Parallel(g4,g2)
    c: Diameter(g5) = 3
    c: Coincident(g3,g6)
    c: Coincident(g5,g6)
    c: Equal(g2,g6)
    c: Parallel(g6,g2)
    c: Diameter(g7) = 3
    c: Coincident(g5,g8)
    c: Coincident(g7,g8)
    c: Equal(g2,g8)
    c: Parallel(g8,g2)
    c: Diameter(g9) = 3
    c: Coincident(g7,g10)
    c: Coincident(g9,g10)
    c: Equal(g2,g10)
    c: Parallel(g10,g2)
    c: Diameter(g11) = 3
    c: Coincident(g9,g12)
    c: Coincident(g11,g12)
    c: Equal(g2,g12)
    c: Parallel(g12,g2)
    c: Diameter(g13) = 3
    c: Coincident(g11,g14)
    c: Coincident(g13,g14)
    c: Equal(g2,g14)
    c: Parallel(g14,g2)
    c: Diameter(g15) = 3
    c: Coincident(g13,g16)
    c: Coincident(g15,g16)
    c: Equal(g2,g16)
    c: Parallel(g16,g2)
    c: Diameter(g17) = 3
    c: Coincident(g15,g18)
    c: Coincident(g17,g18)
    c: Equal(g2,g18)
    c: Parallel(g18,g2)
    c: Diameter(g19) = 3
    c: Coincident(g17,g20)
    c: Coincident(g19,g20)
    c: Equal(g2,g20)
    c: Parallel(g20,g2)
    c: Diameter(g21) = 3
    c: Coincident(g19,g22)
    c: Coincident(g21,g22)
    c: Equal(g2,g22)
    c: Parallel(g22,g2)
    c: Diameter(g23) = 3
    c: Coincident(g21,g24)
    c: Coincident(g23,g24)
    c: Equal(g2,g24)
    c: Parallel(g24,g2)
    c: Diameter(g25) = 3
    c: Coincident(g23,g26)
    c: Coincident(g25,g26)
    c: Equal(g2,g26)
    c: Parallel(g26,g2)
    c: Diameter(g27) = 3
    c: Coincident(g25,g28)
    c: Coincident(g27,g28)
    c: Equal(g2,g28)
    c: Parallel(g28,g2)
    c: Diameter(g29) = 3
    c: Coincident(g27,g30)
    c: Coincident(g29,g30)
    c: Equal(g2,g30)
    c: Parallel(g30,g2)
    c: Diameter(g31) = 3
    c: Diameter(g32) = 3
    c: Coincident(g31,g33)
    c: Coincident(g32,g33)
    c: Distance(g33) = 10
    c: Angle(g33) = 1.5708
    c: Diameter(g34) = 3
    c: Coincident(g32,g35)
    c: Coincident(g34,g35)
    c: Equal(g33,g35)
    c: Parallel(g35,g33)
    c: Diameter(g36) = 3
    c: Coincident(g34,g37)
    c: Coincident(g36,g37)
    c: Equal(g33,g37)
    c: Parallel(g37,g33)
    c: Diameter(g38) = 3
    c: Coincident(g36,g39)
    c: Coincident(g38,g39)
    c: Equal(g33,g39)
    c: Parallel(g39,g33)
    c: Diameter(g40) = 3
    c: Coincident(g38,g41)
    c: Coincident(g40,g41)
    c: Equal(g33,g41)
    c: Parallel(g41,g33)
    c: Diameter(g42) = 3
    c: Coincident(g40,g43)
    c: Coincident(g42,g43)
    c: Equal(g33,g43)
    c: Parallel(g43,g33)
    c: Diameter(g44) = 3
    c: Coincident(g42,g45)
    c: Coincident(g44,g45)
    c: Equal(g33,g45)
    c: Parallel(g45,g33)
    c: Diameter(g46) = 3
    c: Coincident(g44,g47)
    c: Coincident(g46,g47)
    c: Equal(g33,g47)
    c: Parallel(g47,g33)
    c: Diameter(g48) = 3
    c: Coincident(g46,g49)
    c: Coincident(g48,g49)
    c: Equal(g33,g49)
    c: Parallel(g49,g33)
    c: Diameter(g50) = 3
    c: Coincident(g48,g51)
    c: Coincident(g50,g51)
    c: Equal(g33,g51)
    c: Parallel(g51,g33)
    c: Diameter(g52) = 3
    c: Coincident(g50,g53)
    c: Coincident(g52,g53)
    c: Equal(g33,g53)
    c: Parallel(g53,g33)
    c: Diameter(g54) = 3
    c: Coincident(g52,g55)
    c: Coincident(g54,g55)
    c: Equal(g33,g55)
    c: Parallel(g55,g33)
    c: Diameter(g56) = 3
    c: Coincident(g54,g57)
    c: Coincident(g56,g57)
    c: Equal(g33,g57)
    c: Parallel(g57,g33)
    c: Diameter(g58) = 3
    c: Coincident(g56,g59)
    c: Coincident(g58,g59)
    c: Equal(g33,g59)
    c: Parallel(g59,g33)
    c: Diameter(g60) = 3
    c: Coincident(g58,g61)
    c: Coincident(g60,g61)
    c: Equal(g33,g61)
    c: Parallel(g61,g33)
    c: Symmetric(g0,g31,g-2)
    c: DistanceX(g0,g31) = 130
    c: Diameter(g62) = 3
    c: Diameter(g63) = 3
    c: Coincident(g62,g64)
    c: Coincident(g63,g64)
    c: Distance(g64) = 10
    c: Angle(g64) = 1.5708
    c: Diameter(g65) = 3
    c: Coincident(g63,g66)
    c: Coincident(g65,g66)
    c: Equal(g64,g66)
    c: Parallel(g66,g64)
    c: Diameter(g67) = 3
    c: Coincident(g65,g68)
    c: Coincident(g67,g68)
    c: Equal(g64,g68)
    c: Parallel(g68,g64)
    c: Diameter(g69) = 3
    c: Coincident(g67,g70)
    c: Coincident(g69,g70)
    c: Equal(g64,g70)
    c: Parallel(g70,g64)
    c: Diameter(g71) = 3
    c: Coincident(g69,g72)
    c: Coincident(g71,g72)
    c: Equal(g64,g72)
    c: Parallel(g72,g64)
    c: Diameter(g73) = 3
    c: Coincident(g71,g74)
    c: Coincident(g73,g74)
    c: Equal(g64,g74)
    c: Parallel(g74,g64)
    c: Diameter(g75) = 3
    c: Coincident(g73,g76)
    c: Coincident(g75,g76)
    c: Equal(g64,g76)
    c: Parallel(g76,g64)
    c: Diameter(g77) = 3
    c: Coincident(g75,g78)
    c: Coincident(g77,g78)
    c: Equal(g64,g78)
    c: Parallel(g78,g64)
    c: Diameter(g79) = 3
    c: Coincident(g77,g80)
    c: Coincident(g79,g80)
    c: Equal(g64,g80)
    c: Parallel(g80,g64)
    c: Diameter(g81) = 3
    c: Coincident(g79,g82)
    c: Coincident(g81,g82)
    c: Equal(g64,g82)
    c: Parallel(g82,g64)
    c: Diameter(g83) = 3
    c: Coincident(g81,g84)
    c: Coincident(g83,g84)
    c: Equal(g64,g84)
    c: Parallel(g84,g64)
    c: Diameter(g85) = 3
    c: Coincident(g83,g86)
    c: Coincident(g85,g86)
    c: Equal(g64,g86)
    c: Parallel(g86,g64)
    c: Diameter(g87) = 3
    c: Coincident(g85,g88)
    c: Coincident(g87,g88)
    c: Equal(g64,g88)
    c: Parallel(g88,g64)
    c: Diameter(g89) = 3
    c: Coincident(g87,g90)
    c: Coincident(g89,g90)
    c: Equal(g64,g90)
    c: Parallel(g90,g64)
    c: Diameter(g91) = 3
    c: Coincident(g89,g92)
    c: Coincident(g91,g92)
    c: Equal(g64,g92)
    c: Parallel(g92,g64)
    c: PointOnObject(g62,g-2)
    c: Symmetric(g93,g93,g-2)
    c: DistanceX(g93,g93) = 235
    c: DistanceY(g93) = -170
    c: PointOnObject(g0,g93)
    c: PointOnObject(g62,g93)
FEATURE [PartDesign::Hole] Hole035
  BaseFeature = -> Hole034
  CustomThreadClearance = 0
  Depth = 25
  DepthType = 0
  Diameter = 2.5
  DrillForDepth = false
  DrillPoint = 1
  DrillPointAngle = 118
  HoleCutCountersinkAngle = 90
  HoleCutCustomValues = false
  HoleCutDepth = 0
  HoleCutDiameter = 6.1
  HoleCutType = 0
  ModelThread = false
  Profile = -> Sketch097
  Reversed = true
  Tapered = false
  TaperedAngle = 90
  ThreadClass = 0
  ThreadDepth = 25
  ThreadDepthType = 0
  ThreadDirection = 0
  ThreadFit = 0
  ThreadSize = 9
  ThreadType = 1
  Threaded = true
  UseCustomThreadClearance = false
FEATURE [Sketcher::SketchObject] Sketch098
  AttachmentOffset = pos=(0,0,12) rot=(0,0,1;0rad)
  FullyConstrained = true
  MapMode = 5
  Placement = pos=(0,-12,-2.7e-15) rot=(1,0,0;1.5708rad)
  Support = -> [XZ_Plane039]
  expr: .AttachmentOffset.Base.z = <<Variables>>.WallThickness + 5
  sketch-geometry (3):
    g0: Circle CenterX=5 CenterY=19 CenterZ=0 NormalX=0 NormalY=0 NormalZ=1 AngleXU=0 Radius=3
    g1: Circle CenterX=-18 CenterY=19 CenterZ=0 NormalX=0 NormalY=0 NormalZ=1 AngleXU=0 Radius=3
    g2: LineSegment StartX=-40 StartY=19 StartZ=0 EndX=40 EndY=19 EndZ=0
  constraints (9):
    c: Symmetric(g2,g2,g-2)
    c: DistanceX(g2,g2) = 80
    c: DistanceY(g2) = 19
    c: PointOnObject(g0,g2)
    c: PointOnObject(g1,g2)
    c: Equal(g1,g0)
    c: Diameter(g1) = 6
    c: DistanceX(g0) = 5
    c: DistanceX(g1) = -18
FEATURE [Part::FeaturePython] Clone055  label="M3 inserted Nut TopPanel Z Rail 1"  # Draft clone (typed FeaturePython)
  AttacherType = Attacher::AttachEngine3D
  Fuse = false
  Objects = -> [Body013]
  Placement = pos=(0,114,55) rot=(0.57735,-0.57735,-0.57735;4.18879rad)
  Scale = (1,1,1)
  expr: .Placement.Base.y = <<Variables>>.GantorySpacing / 2 + <<Variables>>.CavitySpacingY + <<Variables>>.WallThickness - 3
FEATURE [Part::Mirroring] Part__Mirroring  label="UpperBracketLeft"
  Base = (9.53674e-07,2.5,8.5)
  Normal = (1,0,-1.19209e-07)
  Source = -> Body022
FEATURE [App::Part] Part016  label="UpperBracket"
  Group = -> [Body022,LCS_UpperBracketRightOrigin,Part__Mirroring]
  Origin = -> Origin040
FEATURE [PartDesign::AdditiveCone] Cone
  Angle = 360
  AttacherType = Attacher::AttachEngine3D
  AttachmentOffset = pos=(5,19,17) rot=(1,0,0;3.14159rad)
  BaseFeature = -> Pad035
  Height = 3
  MapMode = 5
  Placement = pos=(5,-17,19) rot=(1,0,0;4.71239rad)
  Radius1 = 3
  Radius2 = 2
  Support = -> [XZ_Plane039]
  expr: .AttachmentOffset.Base.z = <<Variables>>.CavitySpacingY + <<Variables>>.WallThickness
FEATURE [PartDesign::AdditiveCone] Cone001
  Angle = 360
  AttacherType = Attacher::AttachEngine3D
  AttachmentOffset = pos=(-18,19,17) rot=(1,0,0;3.14159rad)
  BaseFeature = -> Cone
  Height = 3
  MapMode = 5
  Placement = pos=(-18,-17,19) rot=(1,0,0;4.71239rad)
  Radius1 = 3
  Radius2 = 2
  Support = -> [XZ_Plane039]
  expr: .AttachmentOffset.Base.z = <<Variables>>.CavitySpacingY + <<Variables>>.WallThickness
FEATURE [PartDesign::Hole] Hole036
  BaseFeature = -> Cone001
  CustomThreadClearance = 0
  Depth = 25
  DepthType = 0
  Diameter = 3.4
  DrillForDepth = false
  DrillPoint = 1
  DrillPointAngle = 118
  HoleCutCountersinkAngle = 90
  HoleCutCustomValues = false
  HoleCutDepth = 3
  HoleCutDiameter = 6.1
  HoleCutType = 1
  ModelThread = false
  Placement = pos=(-18,-17,19) rot=(-1,0,0;1.5708rad)
  Profile = -> Sketch098
  Tapered = false
  TaperedAngle = 90
  ThreadClass = 0
  ThreadDepth = 25
  ThreadDepthType = 0
  ThreadDirection = 0
  ThreadFit = 0
  ThreadSize = 9
  ThreadType = 1
  Threaded = false
  UseCustomThreadClearance = false
FEATURE [PartDesign::Boolean] Boolean006
  BaseFeature = -> Hole036
  Group = -> [Clone076,Clone077]
  Type = 1
FEATURE [PartDesign::Body] StepperBracketRight
  Group = -> [LCS_0,Sketch090,Pad034,Sketch091,Pocket036,Sketch092,Pocket037,Sketch093,Hole032,Binder,Pad035,Cone,Cone001,Sketch098,Hole036,Boolean006]
  Origin = -> Origin039
  Tip = -> Boolean006
FEATURE [PartDesign::CoordinateSystem] LCS_StepperMountLeft  label="LCS_StepperMountLeftOrigin"
  AttacherType = Attacher::AttachEngine3D
  AttachmentOffset = pos=(100,100,-46) rot=(1,0,0;3.14159rad)
  MapMode = 2
  Placement = pos=(100,100,-46) rot=(1,0,0;3.14159rad)
  Support = -> [X_Axis042]
  expr: .AttachmentOffset.Base.x = <<Variables>>.GantorySpacing / 2
  expr: .AttachmentOffset.Base.y = <<Variables>>.GantorySpacing / 2
FEATURE [App::Link] StepperBracketRight_link
  LinkedObject = -> StepperBracketRight
FEATURE [Part::Mirroring] StepperBracketRight_mirrored
  Base = (0,0,0)
  Normal = (1,0,0)
  Source = -> StepperBracketRight_link
FEATURE [PartDesign::CoordinateSystem] LCS_StepperLeftOrigin
  AttacherType = Attacher::AttachEngine3D
  AttachmentOffset = pos=(0,-43.5,5) rot=(1,0,0;3.14159rad)
  MapMode = 2
  Placement = pos=(0,-43.5,5) rot=(1,0,0;3.14159rad)
  Support = -> [X_Axis042]
  expr: .AttachmentOffset.Base.y = -(<<Variables>>.CavitySpacingY + <<Variables>>.WallThickness + 5.5 + 42 / 2)
FEATURE [App::Link] StepperMountLeft001
  AssemblyType = Part::Link
  AttachedBy = #LCS_StepperMountLeft
  AttachedTo = Parent Assembly#LCS_Origin
  LinkPlacement = pos=(-100,100,-46) rot=(-1,0,0;3.14159rad)
  LinkedObject = -> StepperMountLeft
  Placement = pos=(-100,100,-46) rot=(-1,0,0;3.14159rad)
  SolverId = Asm4EE
  expr: Placement = LCS_Origin.Placement * AttachmentOffset * LCS_StepperMountLeft.Placement ^ -1
FEATURE [PartDesign::CoordinateSystem] LCS_RightCarriagePosition
  AttacherType = Attacher::AttachEngine3D
  AttachmentOffset = pos=(0,100,0) rot=(0,0,1;0rad)
  MapMode = 3
  Placement = pos=(100,-2.22e-14,1.11e-14) rot=(0.707107,0.707107,0;3.14159rad)
  Support = -> [Y_Axis001]
  expr: .AttachmentOffset.Base.y = <<Variables>>.GantorySpacing / 2
FEATURE [App::Part] Part  label="Gantory"
  Group = -> [LCS_GantoryOrigin,LCS_LeftRailOrigin,LCS_RightRailOrigin,LCS_GantoryPosition,LCS_LeftCarriagePosition,LCS_RightCarriagePosition]
  Origin = -> Origin001
FEATURE [PartDesign::CoordinateSystem] LCS_CarriageRightPartOrigin
  AttacherType = Attacher::AttachEngine3D
  AttachmentOffset = pos=(0,0,0) rot=(0,0,1;1.5708rad)
  MapMode = 2
  Placement = pos=(0,0,0) rot=(0,0,1;1.5708rad)
  Support = -> [X_Axis005]
FEATURE [App::Part] Part003  label="CarriageRight"
  Group = -> [Body002,LCS_CarriageRightPartOrigin]
  Origin = -> Origin005
FEATURE [Sketcher::SketchObject] Sketch099
  AttachmentOffset = pos=(0,0,4) rot=(0,0,1;0rad)
  FullyConstrained = true
  MapMode = 5
  Placement = pos=(0,0,4) rot=(0,0,1;0rad)
  Support = -> [XY_Plane012]
  expr: .AttachmentOffset.Base.z = <<Variables>>.WallThickness - 3
  sketch-geometry (185):
    g0: LineSegment StartX=-150 StartY=-160 StartZ=0 EndX=150 EndY=-160 EndZ=0
    g1: LineSegment StartX=-65 StartY=0 StartZ=0 EndX=-65 EndY=-160 EndZ=0
    g2: LineSegment StartX=65 StartY=0 StartZ=0 EndX=65 EndY=-160 EndZ=0
    g3: LineSegment StartX=-150 StartY=-140 StartZ=0 EndX=150 EndY=-140 EndZ=0
    g4: LineSegment StartX=-150 StartY=-160 StartZ=0 EndX=-150 EndY=-140 EndZ=0
    g5: LineSegment StartX=-150 StartY=-120 StartZ=0 EndX=150 EndY=-120 EndZ=0
    g6: LineSegment StartX=-150 StartY=-140 StartZ=0 EndX=-150 EndY=-120 EndZ=0
    g7: LineSegment StartX=-150 StartY=-100 StartZ=0 EndX=150 EndY=-100 EndZ=0
    g8: LineSegment StartX=-150 StartY=-120 StartZ=0 EndX=-150 EndY=-100 EndZ=0
    g9: LineSegment StartX=-150 StartY=-80 StartZ=0 EndX=150 EndY=-80 EndZ=0
    g10: LineSegment StartX=-150 StartY=-100 StartZ=0 EndX=-150 EndY=-80 EndZ=0
    g11: LineSegment StartX=-150 StartY=-60 StartZ=0 EndX=150 EndY=-60 EndZ=0
    g12: LineSegment StartX=-150 StartY=-80 StartZ=0 EndX=-150 EndY=-60 EndZ=0
    g13: LineSegment StartX=-150 StartY=-40 StartZ=0 EndX=150 EndY=-40 EndZ=0
    g14: LineSegment StartX=-150 StartY=-60 StartZ=0 EndX=-150 EndY=-40 EndZ=0
    g15: LineSegment StartX=-150 StartY=-20 StartZ=0 EndX=150 EndY=-20 EndZ=0
    g16: LineSegment StartX=-150 StartY=-40 StartZ=0 EndX=-150 EndY=-20 EndZ=0
    g17: LineSegment StartX=-65 StartY=-156.65 StartZ=0 EndX=-67.9012 EndY=-158.325 EndZ=0
    g18: LineSegment StartX=-67.9012 StartY=-158.325 StartZ=0 EndX=-67.9012 EndY=-161.675 EndZ=0
    g19: LineSegment StartX=-67.9012 StartY=-161.675 StartZ=0 EndX=-65 EndY=-163.35 EndZ=0
    g20: LineSegment StartX=-65 StartY=-163.35 StartZ=0 EndX=-62.0988 EndY=-161.675 EndZ=0
    g21: LineSegment StartX=-62.0988 StartY=-161.675 StartZ=0 EndX=-62.0988 EndY=-158.325 EndZ=0
    g22: LineSegment StartX=-62.0988 StartY=-158.325 StartZ=0 EndX=-65 EndY=-156.65 EndZ=0
    g23: Circle CenterX=-65 CenterY=-160 CenterZ=0 NormalX=0 NormalY=0 NormalZ=1 AngleXU=0 Radius=3.35
    g24: LineSegment StartX=-65 StartY=-136.65 StartZ=0 EndX=-67.9012 EndY=-138.325 EndZ=0
    g25: LineSegment StartX=-67.9012 StartY=-138.325 StartZ=0 EndX=-67.9012 EndY=-141.675 EndZ=0
    g26: LineSegment StartX=-67.9012 StartY=-141.675 StartZ=0 EndX=-65 EndY=-143.35 EndZ=0
    g27: LineSegment StartX=-65 StartY=-143.35 StartZ=0 EndX=-62.0988 EndY=-141.675 EndZ=0
    g28: LineSegment StartX=-62.0988 StartY=-141.675 StartZ=0 EndX=-62.0988 EndY=-138.325 EndZ=0
    g29: LineSegment StartX=-62.0988 StartY=-138.325 StartZ=0 EndX=-65 EndY=-136.65 EndZ=0
    g30: Circle CenterX=-65 CenterY=-140 CenterZ=0 NormalX=0 NormalY=0 NormalZ=1 AngleXU=0 Radius=3.35
    g31: LineSegment StartX=-65 StartY=-116.65 StartZ=0 EndX=-67.9012 EndY=-118.325 EndZ=0
    g32: LineSegment StartX=-67.9012 StartY=-118.325 StartZ=0 EndX=-67.9012 EndY=-121.675 EndZ=0
    g33: LineSegment StartX=-67.9012 StartY=-121.675 StartZ=0 EndX=-65 EndY=-123.35 EndZ=0
    g34: LineSegment StartX=-65 StartY=-123.35 StartZ=0 EndX=-62.0988 EndY=-121.675 EndZ=0
    g35: LineSegment StartX=-62.0988 StartY=-121.675 StartZ=0 EndX=-62.0988 EndY=-118.325 EndZ=0
    g36: LineSegment StartX=-62.0988 StartY=-118.325 StartZ=0 EndX=-65 EndY=-116.65 EndZ=0
    g37: Circle CenterX=-65 CenterY=-120 CenterZ=0 NormalX=0 NormalY=0 NormalZ=1 AngleXU=0 Radius=3.35
    g38: LineSegment StartX=-65 StartY=-96.65 StartZ=0 EndX=-67.9012 EndY=-98.325 EndZ=0
    g39: LineSegment StartX=-67.9012 StartY=-98.325 StartZ=0 EndX=-67.9012 EndY=-101.675 EndZ=0
    g40: LineSegment StartX=-67.9012 StartY=-101.675 StartZ=0 EndX=-65 EndY=-103.35 EndZ=0
    g41: LineSegment StartX=-65 StartY=-103.35 StartZ=0 EndX=-62.0988 EndY=-101.675 EndZ=0
    g42: LineSegment StartX=-62.0988 StartY=-101.675 StartZ=0 EndX=-62.0988 EndY=-98.325 EndZ=0
    g43: LineSegment StartX=-62.0988 StartY=-98.325 StartZ=0 EndX=-65 EndY=-96.65 EndZ=0
    g44: Circle CenterX=-65 CenterY=-100 CenterZ=0 NormalX=0 NormalY=0 NormalZ=1 AngleXU=0 Radius=3.35
    g45: LineSegment StartX=-65 StartY=-76.65 StartZ=0 EndX=-67.9012 EndY=-78.325 EndZ=0
    g46: LineSegment StartX=-67.9012 StartY=-78.325 StartZ=0 EndX=-67.9012 EndY=-81.675 EndZ=0
    g47: LineSegment StartX=-67.9012 StartY=-81.675 StartZ=0 EndX=-65 EndY=-83.35 EndZ=0
    g48: LineSegment StartX=-65 StartY=-83.35 StartZ=0 EndX=-62.0988 EndY=-81.675 EndZ=0
    g49: LineSegment StartX=-62.0988 StartY=-81.675 StartZ=0 EndX=-62.0988 EndY=-78.325 EndZ=0
    g50: LineSegment StartX=-62.0988 StartY=-78.325 StartZ=0 EndX=-65 EndY=-76.65 EndZ=0
    g51: Circle CenterX=-65 CenterY=-80 CenterZ=0 NormalX=0 NormalY=0 NormalZ=1 AngleXU=0 Radius=3.35
    g52: LineSegment StartX=-65 StartY=-56.65 StartZ=0 EndX=-67.9012 EndY=-58.325 EndZ=0
    g53: LineSegment StartX=-67.9012 StartY=-58.325 StartZ=0 EndX=-67.9012 EndY=-61.675 EndZ=0
    g54: LineSegment StartX=-67.9012 StartY=-61.675 StartZ=0 EndX=-65 EndY=-63.35 EndZ=0
    g55: LineSegment StartX=-65 StartY=-63.35 StartZ=0 EndX=-62.0988 EndY=-61.675 EndZ=0
    g56: LineSegment StartX=-62.0988 StartY=-61.675 StartZ=0 EndX=-62.0988 EndY=-58.325 EndZ=0
    g57: LineSegment StartX=-62.0988 StartY=-58.325 StartZ=0 EndX=-65 EndY=-56.65 EndZ=0
    g58: Circle CenterX=-65 CenterY=-60 CenterZ=0 NormalX=0 NormalY=0 NormalZ=1 AngleXU=0 Radius=3.35
    g59: LineSegment StartX=-65 StartY=-36.65 StartZ=0 EndX=-67.9012 EndY=-38.325 EndZ=0
    g60: LineSegment StartX=-67.9012 StartY=-38.325 StartZ=0 EndX=-67.9012 EndY=-41.675 EndZ=0
    g61: LineSegment StartX=-67.9012 StartY=-41.675 StartZ=0 EndX=-65 EndY=-43.35 EndZ=0
    g62: LineSegment StartX=-65 StartY=-43.35 StartZ=0 EndX=-62.0988 EndY=-41.675 EndZ=0
    g63: LineSegment StartX=-62.0988 StartY=-41.675 StartZ=0 EndX=-62.0988 EndY=-38.325 EndZ=0
    g64: LineSegment StartX=-62.0988 StartY=-38.325 StartZ=0 EndX=-65 EndY=-36.65 EndZ=0
    g65: Circle CenterX=-65 CenterY=-40 CenterZ=0 NormalX=0 NormalY=0 NormalZ=1 AngleXU=0 Radius=3.35
    g66: LineSegment StartX=-65 StartY=-16.65 StartZ=0 EndX=-67.9012 EndY=-18.325 EndZ=0
    g67: LineSegment StartX=-67.9012 StartY=-18.325 StartZ=0 EndX=-67.9012 EndY=-21.675 EndZ=0
    g68: LineSegment StartX=-67.9012 StartY=-21.675 StartZ=0 EndX=-65 EndY=-23.35 EndZ=0
    g69: LineSegment StartX=-65 StartY=-23.35 StartZ=0 EndX=-62.0988 EndY=-21.675 EndZ=0
    g70: LineSegment StartX=-62.0988 StartY=-21.675 StartZ=0 EndX=-62.0988 EndY=-18.325 EndZ=0
    g71: LineSegment StartX=-62.0988 StartY=-18.325 StartZ=0 EndX=-65 EndY=-16.65 EndZ=0
    g72: Circle CenterX=-65 CenterY=-20 CenterZ=0 NormalX=0 NormalY=0 NormalZ=1 AngleXU=0 Radius=3.35
    g73: LineSegment StartX=0 StartY=-156.65 StartZ=0 EndX=-2.90119 EndY=-158.325 EndZ=0
    g74: LineSegment StartX=-2.90119 StartY=-158.325 StartZ=0 EndX=-2.90119 EndY=-161.675 EndZ=0
    g75: LineSegment StartX=-2.90119 StartY=-161.675 StartZ=0 EndX=0 EndY=-163.35 EndZ=0
    g76: LineSegment StartX=0 StartY=-163.35 StartZ=0 EndX=2.90119 EndY=-161.675 EndZ=0
    g77: LineSegment StartX=2.90119 StartY=-161.675 StartZ=0 EndX=2.90119 EndY=-158.325 EndZ=0
    g78: LineSegment StartX=2.90119 StartY=-158.325 StartZ=0 EndX=0 EndY=-156.65 EndZ=0
    g79: Circle CenterX=0 CenterY=-160 CenterZ=0 NormalX=0 NormalY=0 NormalZ=1 AngleXU=0 Radius=3.35
    g80: LineSegment StartX=0 StartY=-136.65 StartZ=0 EndX=-2.90119 EndY=-138.325 EndZ=0
    g81: LineSegment StartX=-2.90119 StartY=-138.325 StartZ=0 EndX=-2.90119 EndY=-141.675 EndZ=0
    g82: LineSegment StartX=-2.90119 StartY=-141.675 StartZ=0 EndX=0 EndY=-143.35 EndZ=0
    g83: LineSegment StartX=0 StartY=-143.35 StartZ=0 EndX=2.90119 EndY=-141.675 EndZ=0
    g84: LineSegment StartX=2.90119 StartY=-141.675 StartZ=0 EndX=2.90119 EndY=-138.325 EndZ=0
    g85: LineSegment StartX=2.90119 StartY=-138.325 StartZ=0 EndX=0 EndY=-136.65 EndZ=0
    g86: Circle CenterX=0 CenterY=-140 CenterZ=0 NormalX=0 NormalY=0 NormalZ=1 AngleXU=0 Radius=3.35
    g87: LineSegment StartX=0 StartY=-116.65 StartZ=0 EndX=-2.90119 EndY=-118.325 EndZ=0
    g88: LineSegment StartX=-2.90119 StartY=-118.325 StartZ=0 EndX=-2.90119 EndY=-121.675 EndZ=0
    g89: LineSegment StartX=-2.90119 StartY=-121.675 StartZ=0 EndX=0 EndY=-123.35 EndZ=0
    g90: LineSegment StartX=0 StartY=-123.35 StartZ=0 EndX=2.90119 EndY=-121.675 EndZ=0
    g91: LineSegment StartX=2.90119 StartY=-121.675 StartZ=0 EndX=2.90119 EndY=-118.325 EndZ=0
    g92: LineSegment StartX=2.90119 StartY=-118.325 StartZ=0 EndX=0 EndY=-116.65 EndZ=0
    g93: Circle CenterX=0 CenterY=-120 CenterZ=0 NormalX=0 NormalY=0 NormalZ=1 AngleXU=0 Radius=3.35
    g94: LineSegment StartX=0 StartY=-96.65 StartZ=0 EndX=-2.90119 EndY=-98.325 EndZ=0
    g95: LineSegment StartX=-2.90119 StartY=-98.325 StartZ=0 EndX=-2.90119 EndY=-101.675 EndZ=0
    g96: LineSegment StartX=-2.90119 StartY=-101.675 StartZ=0 EndX=4e-16 EndY=-103.35 EndZ=0
    g97: LineSegment StartX=4e-16 StartY=-103.35 StartZ=0 EndX=2.90119 EndY=-101.675 EndZ=0
    g98: LineSegment StartX=2.90119 StartY=-101.675 StartZ=0 EndX=2.90119 EndY=-98.325 EndZ=0
    g99: LineSegment StartX=2.90119 StartY=-98.325 StartZ=0 EndX=0 EndY=-96.65 EndZ=0
    g100: Circle CenterX=0 CenterY=-100 CenterZ=0 NormalX=0 NormalY=0 NormalZ=1 AngleXU=0 Radius=3.35
    g101: LineSegment StartX=0 StartY=-76.65 StartZ=0 EndX=-2.90119 EndY=-78.325 EndZ=0
    g102: LineSegment StartX=-2.90119 StartY=-78.325 StartZ=0 EndX=-2.90119 EndY=-81.675 EndZ=0
    g103: LineSegment StartX=-2.90119 StartY=-81.675 StartZ=0 EndX=0 EndY=-83.35 EndZ=0
    g104: LineSegment StartX=0 StartY=-83.35 StartZ=0 EndX=2.90119 EndY=-81.675 EndZ=0
    g105: LineSegment StartX=2.90119 StartY=-81.675 StartZ=0 EndX=2.90119 EndY=-78.325 EndZ=0
    g106: LineSegment StartX=2.90119 StartY=-78.325 StartZ=0 EndX=0 EndY=-76.65 EndZ=0
    g107: Circle CenterX=0 CenterY=-80 CenterZ=0 NormalX=0 NormalY=0 NormalZ=1 AngleXU=0 Radius=3.35
    g108: LineSegment StartX=0 StartY=-56.65 StartZ=0 EndX=-2.90119 EndY=-58.325 EndZ=0
    g109: LineSegment StartX=-2.90119 StartY=-58.325 StartZ=0 EndX=-2.90119 EndY=-61.675 EndZ=0
    g110: LineSegment StartX=-2.90119 StartY=-61.675 StartZ=0 EndX=4e-16 EndY=-63.35 EndZ=0
    g111: LineSegment StartX=4e-16 StartY=-63.35 StartZ=0 EndX=2.90119 EndY=-61.675 EndZ=0
    g112: LineSegment StartX=2.90119 StartY=-61.675 StartZ=0 EndX=2.90119 EndY=-58.325 EndZ=0
    g113: LineSegment StartX=2.90119 StartY=-58.325 StartZ=0 EndX=0 EndY=-56.65 EndZ=0
    g114: Circle CenterX=0 CenterY=-60 CenterZ=0 NormalX=0 NormalY=0 NormalZ=1 AngleXU=0 Radius=3.35
    g115: LineSegment StartX=0 StartY=-36.65 StartZ=0 EndX=-2.90119 EndY=-38.325 EndZ=0
    g116: LineSegment StartX=-2.90119 StartY=-38.325 StartZ=0 EndX=-2.90119 EndY=-41.675 EndZ=0
    g117: LineSegment StartX=-2.90119 StartY=-41.675 StartZ=0 EndX=4e-16 EndY=-43.35 EndZ=0
    g118: LineSegment StartX=4e-16 StartY=-43.35 StartZ=0 EndX=2.90119 EndY=-41.675 EndZ=0
    g119: LineSegment StartX=2.90119 StartY=-41.675 StartZ=0 EndX=2.90119 EndY=-38.325 EndZ=0
    g120: LineSegment StartX=2.90119 StartY=-38.325 StartZ=0 EndX=0 EndY=-36.65 EndZ=0
    g121: Circle CenterX=0 CenterY=-40 CenterZ=0 NormalX=0 NormalY=0 NormalZ=1 AngleXU=0 Radius=3.35
    g122: LineSegment StartX=0 StartY=-16.65 StartZ=0 EndX=-2.90119 EndY=-18.325 EndZ=0
    g123: LineSegment StartX=-2.90119 StartY=-18.325 StartZ=0 EndX=-2.90119 EndY=-21.675 EndZ=0
    g124: LineSegment StartX=-2.90119 StartY=-21.675 StartZ=0 EndX=-4e-16 EndY=-23.35 EndZ=0
    g125: LineSegment StartX=-4e-16 StartY=-23.35 StartZ=0 EndX=2.90119 EndY=-21.675 EndZ=0
    g126: LineSegment StartX=2.90119 StartY=-21.675 StartZ=0 EndX=2.90119 EndY=-18.325 EndZ=0
    g127: LineSegment StartX=2.90119 StartY=-18.325 StartZ=0 EndX=0 EndY=-16.65 EndZ=0
    g128: Circle CenterX=0 CenterY=-20 CenterZ=0 NormalX=0 NormalY=0 NormalZ=1 AngleXU=0 Radius=3.35
    g129: LineSegment StartX=65 StartY=-156.65 StartZ=0 EndX=62.0988 EndY=-158.325 EndZ=0
    g130: LineSegment StartX=62.0988 StartY=-158.325 StartZ=0 EndX=62.0988 EndY=-161.675 EndZ=0
    g131: LineSegment StartX=62.0988 StartY=-161.675 StartZ=0 EndX=65 EndY=-163.35 EndZ=0
    g132: LineSegment StartX=65 StartY=-163.35 StartZ=0 EndX=67.9012 EndY=-161.675 EndZ=0
    g133: LineSegment StartX=67.9012 StartY=-161.675 StartZ=0 EndX=67.9012 EndY=-158.325 EndZ=0
    g134: LineSegment StartX=67.9012 StartY=-158.325 StartZ=0 EndX=65 EndY=-156.65 EndZ=0
    g135: Circle CenterX=65 CenterY=-160 CenterZ=0 NormalX=0 NormalY=0 NormalZ=1 AngleXU=0 Radius=3.35
    g136: LineSegment StartX=65 StartY=-136.65 StartZ=0 EndX=62.0988 EndY=-138.325 EndZ=0
    g137: LineSegment StartX=62.0988 StartY=-138.325 StartZ=0 EndX=62.0988 EndY=-141.675 EndZ=0
    g138: LineSegment StartX=62.0988 StartY=-141.675 StartZ=0 EndX=65 EndY=-143.35 EndZ=0
    g139: LineSegment StartX=65 StartY=-143.35 StartZ=0 EndX=67.9012 EndY=-141.675 EndZ=0
    g140: LineSegment StartX=67.9012 StartY=-141.675 StartZ=0 EndX=67.9012 EndY=-138.325 EndZ=0
    g141: LineSegment StartX=67.9012 StartY=-138.325 StartZ=0 EndX=65 EndY=-136.65 EndZ=0
    g142: Circle CenterX=65 CenterY=-140 CenterZ=0 NormalX=0 NormalY=0 NormalZ=1 AngleXU=0 Radius=3.35
    g143: LineSegment StartX=65 StartY=-116.65 StartZ=0 EndX=62.0988 EndY=-118.325 EndZ=0
    g144: LineSegment StartX=62.0988 StartY=-118.325 StartZ=0 EndX=62.0988 EndY=-121.675 EndZ=0
    g145: LineSegment StartX=62.0988 StartY=-121.675 StartZ=0 EndX=65 EndY=-123.35 EndZ=0
    g146: LineSegment StartX=65 StartY=-123.35 StartZ=0 EndX=67.9012 EndY=-121.675 EndZ=0
    g147: LineSegment StartX=67.9012 StartY=-121.675 StartZ=0 EndX=67.9012 EndY=-118.325 EndZ=0
    g148: LineSegment StartX=67.9012 StartY=-118.325 StartZ=0 EndX=65 EndY=-116.65 EndZ=0
    g149: Circle CenterX=65 CenterY=-120 CenterZ=0 NormalX=0 NormalY=0 NormalZ=1 AngleXU=0 Radius=3.35
    g150: LineSegment StartX=65 StartY=-96.65 StartZ=0 EndX=62.0988 EndY=-98.325 EndZ=0
    g151: LineSegment StartX=62.0988 StartY=-98.325 StartZ=0 EndX=62.0988 EndY=-101.675 EndZ=0
    g152: LineSegment StartX=62.0988 StartY=-101.675 StartZ=0 EndX=65 EndY=-103.35 EndZ=0
    g153: LineSegment StartX=65 StartY=-103.35 StartZ=0 EndX=67.9012 EndY=-101.675 EndZ=0
    g154: LineSegment StartX=67.9012 StartY=-101.675 StartZ=0 EndX=67.9012 EndY=-98.325 EndZ=0
    g155: LineSegment StartX=67.9012 StartY=-98.325 StartZ=0 EndX=65 EndY=-96.65 EndZ=0
    g156: Circle CenterX=65 CenterY=-100 CenterZ=0 NormalX=0 NormalY=0 NormalZ=1 AngleXU=0 Radius=3.35
    g157: LineSegment StartX=65 StartY=-76.65 StartZ=0 EndX=62.0988 EndY=-78.325 EndZ=0
    g158: LineSegment StartX=62.0988 StartY=-78.325 StartZ=0 EndX=62.0988 EndY=-81.675 EndZ=0
    g159: LineSegment StartX=62.0988 StartY=-81.675 StartZ=0 EndX=65 EndY=-83.35 EndZ=0
    g160: LineSegment StartX=65 StartY=-83.35 StartZ=0 EndX=67.9012 EndY=-81.675 EndZ=0
    g161: LineSegment StartX=67.9012 StartY=-81.675 StartZ=0 EndX=67.9012 EndY=-78.325 EndZ=0
    g162: LineSegment StartX=67.9012 StartY=-78.325 StartZ=0 EndX=65 EndY=-76.65 EndZ=0
    g163: Circle CenterX=65 CenterY=-80 CenterZ=0 NormalX=0 NormalY=0 NormalZ=1 AngleXU=0 Radius=3.35
    g164: LineSegment StartX=65 StartY=-56.65 StartZ=0 EndX=62.0988 EndY=-58.325 EndZ=0
    g165: LineSegment StartX=62.0988 StartY=-58.325 StartZ=0 EndX=62.0988 EndY=-61.675 EndZ=0
    g166: LineSegment StartX=62.0988 StartY=-61.675 StartZ=0 EndX=65 EndY=-63.35 EndZ=0
    g167: LineSegment StartX=65 StartY=-63.35 StartZ=0 EndX=67.9012 EndY=-61.675 EndZ=0
    g168: LineSegment StartX=67.9012 StartY=-61.675 StartZ=0 EndX=67.9012 EndY=-58.325 EndZ=0
    g169: LineSegment StartX=67.9012 StartY=-58.325 StartZ=0 EndX=65 EndY=-56.65 EndZ=0
    g170: Circle CenterX=65 CenterY=-60 CenterZ=0 NormalX=0 NormalY=0 NormalZ=1 AngleXU=0 Radius=3.35
    g171: LineSegment StartX=65 StartY=-36.65 StartZ=0 EndX=62.0988 EndY=-38.325 EndZ=0
    g172: LineSegment StartX=62.0988 StartY=-38.325 StartZ=0 EndX=62.0988 EndY=-41.675 EndZ=0
    g173: LineSegment StartX=62.0988 StartY=-41.675 StartZ=0 EndX=65 EndY=-43.35 EndZ=0
    g174: LineSegment StartX=65 StartY=-43.35 StartZ=0 EndX=67.9012 EndY=-41.675 EndZ=0
    g175: LineSegment StartX=67.9012 StartY=-41.675 StartZ=0 EndX=67.9012 EndY=-38.325 EndZ=0
    g176: LineSegment StartX=67.9012 StartY=-38.325 StartZ=0 EndX=65 EndY=-36.65 EndZ=0
    g177: Circle CenterX=65 CenterY=-40 CenterZ=0 NormalX=0 NormalY=0 NormalZ=1 AngleXU=0 Radius=3.35
    g178: LineSegment StartX=65 StartY=-16.65 StartZ=0 EndX=62.0988 EndY=-18.325 EndZ=0
    g179: LineSegment StartX=62.0988 StartY=-18.325 StartZ=0 EndX=62.0988 EndY=-21.675 EndZ=0
    g180: LineSegment StartX=62.0988 StartY=-21.675 StartZ=0 EndX=65 EndY=-23.35 EndZ=0
    g181: LineSegment StartX=65 StartY=-23.35 StartZ=0 EndX=67.9012 EndY=-21.675 EndZ=0
    g182: LineSegment StartX=67.9012 StartY=-21.675 StartZ=0 EndX=67.9012 EndY=-18.325 EndZ=0
    g183: LineSegment StartX=67.9012 StartY=-18.325 StartZ=0 EndX=65 EndY=-16.65 EndZ=0
    g184: Circle CenterX=65 CenterY=-20 CenterZ=0 NormalX=0 NormalY=0 NormalZ=1 AngleXU=0 Radius=3.35
  constraints (453):
    c: Symmetric(g0,g0,g-2)
    c: DistanceY(g0) = -160
    c: PointOnObject(g1,g-1)
    c: PointOnObject(g1,g0)
    c: Vertical(g1)
    c: PointOnObject(g2,g-1)
    c: Vertical(g2)
    c: Symmetric(g1,g2,g-2)
    c: DistanceX(g1,g2) = 130
    c: Coincident(g0,g4)
    c: Coincident(g3,g4)
    c: Distance(g4) = 20
    c: Angle(g4) = 1.5708
    c: Coincident(g3,g6)
    c: Coincident(g5,g6)
    c: Equal(g4,g6)
    c: Parallel(g6,g4)
    c: Coincident(g5,g8)
    c: Coincident(g7,g8)
    c: Equal(g4,g8)
    c: Parallel(g8,g4)
    c: Coincident(g7,g10)
    c: Coincident(g9,g10)
    c: Equal(g4,g10)
    c: Parallel(g10,g4)
    c: Coincident(g9,g12)
    c: Coincident(g11,g12)
    c: Equal(g4,g12)
    c: Parallel(g12,g4)
    c: Coincident(g11,g14)
    c: Coincident(g13,g14)
    c: Equal(g4,g14)
    c: Parallel(g14,g4)
    c: Coincident(g13,g16)
    c: Coincident(g15,g16)
    c: Equal(g4,g16)
    c: Parallel(g16,g4)
    c: Symmetric(g3,g3,g-2)
    c: Symmetric(g5,g5,g-2)
    c: Symmetric(g7,g7,g-2)
    c: Symmetric(g9,g9,g-2)
    c: Symmetric(g11,g11,g-2)
    c: Symmetric(g13,g13,g-2)
    c: Symmetric(g15,g15,g-2)
    c: DistanceX(g0) = -150
    c: Coincident(g17,g18)
    c: Coincident(g18,g19)
    c: Coincident(g19,g20)
    c: Coincident(g20,g21)
    c: Coincident(g21,g22)
    c: Coincident(g22,g17)
    c: Equal(g17, g18-g22) x5
    c: PointOnObject(g17,g23)
    c: PointOnObject(g18,g23)
    c: PointOnObject(g19,g23)
    c: PointOnObject(g20,g23)
    c: PointOnObject(g21,g23)
    c: PointOnObject(g22,g23)
    c: PointOnObject(g23,g1)
    c: PointOnObject(g22,g1)
    c: Coincident(g24,g25)
    c: Coincident(g25,g26)
    c: Coincident(g26,g27)
    c: Coincident(g27,g28)
    c: Coincident(g28,g29)
    c: Coincident(g29,g24)
    c: Equal(g24, g25-g29) x5
    c: PointOnObject(g24,g30)
    c: PointOnObject(g25,g30)
    c: PointOnObject(g26,g30)
    c: PointOnObject(g27,g30)
    c: PointOnObject(g28,g30)
    c: PointOnObject(g29,g30)
    c: PointOnObject(g30,g1)
    c: PointOnObject(g29,g1)
    c: Coincident(g31,g32)
    c: Coincident(g32,g33)
    c: Coincident(g33,g34)
    c: Coincident(g34,g35)
    c: Coincident(g35,g36)
    c: Coincident(g36,g31)
    c: Equal(g31, g32-g36) x5
    c: PointOnObject(g31,g37)
    c: PointOnObject(g32,g37)
    c: PointOnObject(g33,g37)
    c: PointOnObject(g34,g37)
    c: PointOnObject(g35,g37)
    c: PointOnObject(g36,g37)
    c: PointOnObject(g37,g1)
    c: PointOnObject(g36,g1)
    c: Coincident(g38,g39)
    c: Coincident(g39,g40)
    c: Coincident(g40,g41)
    c: Coincident(g41,g42)
    c: Coincident(g42,g43)
    c: Coincident(g43,g38)
    c: Equal(g38, g39-g43) x5
    c: PointOnObject(g38,g44)
    c: PointOnObject(g39,g44)
    c: PointOnObject(g40,g44)
    c: PointOnObject(g41,g44)
    c: PointOnObject(g42,g44)
    c: PointOnObject(g43,g44)
    c: PointOnObject(g44,g1)
    c: PointOnObject(g43,g1)
    c: Coincident(g45,g46)
    c: Coincident(g46,g47)
    c: Coincident(g47,g48)
    c: Coincident(g48,g49)
    c: Coincident(g49,g50)
    c: Coincident(g50,g45)
    c: Equal(g45, g46-g50) x5
    c: PointOnObject(g45,g51)
    c: PointOnObject(g46,g51)
    c: PointOnObject(g47,g51)
    c: PointOnObject(g48,g51)
    c: PointOnObject(g49,g51)
    c: PointOnObject(g50,g51)
    c: PointOnObject(g51,g1)
    c: PointOnObject(g50,g1)
    c: Coincident(g52,g53)
    c: Coincident(g53,g54)
    c: Coincident(g54,g55)
    c: Coincident(g55,g56)
    c: Coincident(g56,g57)
    c: Coincident(g57,g52)
    c: Equal(g52, g53-g57) x5
    c: PointOnObject(g52,g58)
    c: PointOnObject(g53,g58)
    c: PointOnObject(g54,g58)
    c: PointOnObject(g55,g58)
    c: PointOnObject(g56,g58)
    c: PointOnObject(g57,g58)
    c: PointOnObject(g58,g1)
    c: PointOnObject(g57,g1)
    c: Coincident(g59,g60)
    c: Coincident(g60,g61)
    c: Coincident(g61,g62)
    c: Coincident(g62,g63)
    c: Coincident(g63,g64)
    c: Coincident(g64,g59)
    c: Equal(g59, g60-g64) x5
    c: PointOnObject(g59,g65)
    c: PointOnObject(g60,g65)
    c: PointOnObject(g61,g65)
    c: PointOnObject(g62,g65)
    c: PointOnObject(g63,g65)
    c: PointOnObject(g64,g65)
    c: PointOnObject(g65,g1)
    c: PointOnObject(g64,g1)
    c: Coincident(g66,g67)
    c: Coincident(g67,g68)
    c: Coincident(g68,g69)
    c: Coincident(g69,g70)
    c: Coincident(g70,g71)
    c: Coincident(g71,g66)
    c: Equal(g66, g67-g71) x5
    c: PointOnObject(g66,g72)
    c: PointOnObject(g67,g72)
    c: PointOnObject(g68,g72)
    c: PointOnObject(g69,g72)
    c: PointOnObject(g70,g72)
    c: PointOnObject(g71,g72)
    c: PointOnObject(g72,g1)
    c: PointOnObject(g71,g1)
    c: Coincident(g73,g74)
    c: Coincident(g74,g75)
    c: Coincident(g75,g76)
    c: Coincident(g76,g77)
    c: Coincident(g77,g78)
    c: Coincident(g78,g73)
    c: Equal(g73, g74-g78) x5
    c: PointOnObject(g73,g79)
    c: PointOnObject(g74,g79)
    c: PointOnObject(g75,g79)
    c: PointOnObject(g76,g79)
    c: PointOnObject(g77,g79)
    c: PointOnObject(g78,g79)
    c: PointOnObject(g79,g-2)
    c: PointOnObject(g78,g-2)
    c: Coincident(g80,g81)
    c: Coincident(g81,g82)
    c: Coincident(g82,g83)
    c: Coincident(g83,g84)
    c: Coincident(g84,g85)
    c: Coincident(g85,g80)
    c: Equal(g80, g81-g85) x5
    c: PointOnObject(g80,g86)
    c: PointOnObject(g81,g86)
    c: PointOnObject(g82,g86)
    c: PointOnObject(g83,g86)
    c: PointOnObject(g84,g86)
    c: PointOnObject(g85,g86)
    c: PointOnObject(g86,g-2)
    c: PointOnObject(g85,g-2)
    c: Coincident(g87,g88)
    c: Coincident(g88,g89)
    c: Coincident(g89,g90)
    c: Coincident(g90,g91)
    c: Coincident(g91,g92)
    c: Coincident(g92,g87)
    c: Equal(g87, g88-g92) x5
    c: PointOnObject(g87,g93)
    c: PointOnObject(g88,g93)
    c: PointOnObject(g89,g93)
    c: PointOnObject(g90,g93)
    c: PointOnObject(g91,g93)
    c: PointOnObject(g92,g93)
    c: PointOnObject(g93,g-2)
    c: PointOnObject(g92,g-2)
    c: Coincident(g94,g95)
    c: Coincident(g95,g96)
    c: Coincident(g96,g97)
    c: Coincident(g97,g98)
    c: Coincident(g98,g99)
    c: Coincident(g99,g94)
    c: Equal(g94, g95-g99) x5
    c: PointOnObject(g94,g100)
    c: PointOnObject(g95,g100)
    c: PointOnObject(g96,g100)
    c: PointOnObject(g97,g100)
    c: PointOnObject(g98,g100)
    c: PointOnObject(g99,g100)
    c: PointOnObject(g100,g-2)
    c: PointOnObject(g99,g-2)
    c: Coincident(g101,g102)
    c: Coincident(g102,g103)
    c: Coincident(g103,g104)
    c: Coincident(g104,g105)
    c: Coincident(g105,g106)
    c: Coincident(g106,g101)
    c: Equal(g101, g102-g106) x5
    c: PointOnObject(g101,g107)
    c: PointOnObject(g102,g107)
    c: PointOnObject(g103,g107)
    c: PointOnObject(g104,g107)
    c: PointOnObject(g105,g107)
    c: PointOnObject(g106,g107)
    c: PointOnObject(g107,g-2)
    c: PointOnObject(g106,g-2)
    c: Coincident(g108,g109)
    c: Coincident(g109,g110)
    c: Coincident(g110,g111)
    c: Coincident(g111,g112)
    c: Coincident(g112,g113)
    c: Coincident(g113,g108)
    c: Equal(g108, g109-g113) x5
    c: PointOnObject(g108,g114)
    c: PointOnObject(g109,g114)
    c: PointOnObject(g110,g114)
    c: PointOnObject(g111,g114)
    c: PointOnObject(g112,g114)
    c: PointOnObject(g113,g114)
    c: PointOnObject(g114,g-2)
    c: PointOnObject(g113,g-2)
    c: Coincident(g115,g116)
    c: Coincident(g116,g117)
    c: Coincident(g117,g118)
    c: Coincident(g118,g119)
    c: Coincident(g119,g120)
    c: Coincident(g120,g115)
    c: Equal(g115, g116-g120) x5
    c: PointOnObject(g115,g121)
    c: PointOnObject(g116,g121)
    c: PointOnObject(g117,g121)
    c: PointOnObject(g118,g121)
    c: PointOnObject(g119,g121)
    c: PointOnObject(g120,g121)
    c: PointOnObject(g121,g-2)
    c: PointOnObject(g120,g-2)
    c: Coincident(g122,g123)
    c: Coincident(g123,g124)
    c: Coincident(g124,g125)
    c: Coincident(g125,g126)
    c: Coincident(g126,g127)
    c: Coincident(g127,g122)
    c: Equal(g122, g123-g127) x5
    c: PointOnObject(g122,g128)
    c: PointOnObject(g123,g128)
    c: PointOnObject(g124,g128)
    c: PointOnObject(g125,g128)
    c: PointOnObject(g126,g128)
    c: PointOnObject(g127,g128)
    c: PointOnObject(g128,g-2)
    c: PointOnObject(g127,g-2)
    c: Coincident(g129,g130)
    c: Coincident(g130,g131)
    c: Coincident(g131,g132)
    c: Coincident(g132,g133)
    c: Coincident(g133,g134)
    c: Coincident(g134,g129)
    c: Equal(g129, g130-g134) x5
    c: PointOnObject(g129,g135)
    c: PointOnObject(g130,g135)
    c: PointOnObject(g131,g135)
    c: PointOnObject(g132,g135)
    c: PointOnObject(g133,g135)
    c: PointOnObject(g134,g135)
    c: PointOnObject(g135,g2)
    c: PointOnObject(g134,g2)
    c: Coincident(g136,g137)
    c: Coincident(g137,g138)
    c: Coincident(g138,g139)
    c: Coincident(g139,g140)
    c: Coincident(g140,g141)
    c: Coincident(g141,g136)
    c: Equal(g136, g137-g141) x5
    c: PointOnObject(g136,g142)
    c: PointOnObject(g137,g142)
    c: PointOnObject(g138,g142)
    c: PointOnObject(g139,g142)
    c: PointOnObject(g140,g142)
    c: PointOnObject(g141,g142)
    c: PointOnObject(g142,g2)
    c: PointOnObject(g141,g2)
    c: Coincident(g143,g144)
    c: Coincident(g144,g145)
    c: Coincident(g145,g146)
    c: Coincident(g146,g147)
    c: Coincident(g147,g148)
    c: Coincident(g148,g143)
    c: Equal(g143, g144-g148) x5
    c: PointOnObject(g143,g149)
    c: PointOnObject(g144,g149)
    c: PointOnObject(g145,g149)
    c: PointOnObject(g146,g149)
    c: PointOnObject(g147,g149)
    c: PointOnObject(g148,g149)
    c: PointOnObject(g149,g2)
    c: PointOnObject(g148,g2)
    c: Coincident(g150,g151)
    c: Coincident(g151,g152)
    c: Coincident(g152,g153)
    c: Coincident(g153,g154)
    c: Coincident(g154,g155)
    c: Coincident(g155,g150)
    c: Equal(g150, g151-g155) x5
    c: PointOnObject(g150,g156)
    c: PointOnObject(g151,g156)
    c: PointOnObject(g152,g156)
    c: PointOnObject(g153,g156)
    c: PointOnObject(g154,g156)
    c: PointOnObject(g155,g156)
    c: PointOnObject(g156,g2)
    c: PointOnObject(g155,g2)
    c: Coincident(g157,g158)
    c: Coincident(g158,g159)
    c: Coincident(g159,g160)
    c: Coincident(g160,g161)
    c: Coincident(g161,g162)
    c: Coincident(g162,g157)
    c: Equal(g157, g158-g162) x5
    c: PointOnObject(g157,g163)
    c: PointOnObject(g158,g163)
    c: PointOnObject(g159,g163)
    c: PointOnObject(g160,g163)
    c: PointOnObject(g161,g163)
    c: PointOnObject(g162,g163)
    c: PointOnObject(g163,g2)
    c: PointOnObject(g162,g2)
    c: Coincident(g164,g165)
    c: Coincident(g165,g166)
    c: Coincident(g166,g167)
    c: Coincident(g167,g168)
    c: Coincident(g168,g169)
    c: Coincident(g169,g164)
    c: Equal(g164, g165-g169) x5
    c: PointOnObject(g164,g170)
    c: PointOnObject(g165,g170)
    c: PointOnObject(g166,g170)
    c: PointOnObject(g167,g170)
    c: PointOnObject(g168,g170)
    c: PointOnObject(g169,g170)
    c: PointOnObject(g170,g2)
    c: PointOnObject(g169,g2)
    c: Coincident(g171,g172)
    c: Coincident(g172,g173)
    c: Coincident(g173,g174)
    c: Coincident(g174,g175)
    c: Coincident(g175,g176)
    c: Coincident(g176,g171)
    c: Equal(g171, g172-g176) x5
    c: PointOnObject(g171,g177)
    c: PointOnObject(g172,g177)
    c: PointOnObject(g173,g177)
    c: PointOnObject(g174,g177)
    c: PointOnObject(g175,g177)
    c: PointOnObject(g176,g177)
    c: PointOnObject(g177,g2)
    c: PointOnObject(g176,g2)
    c: Coincident(g178,g179)
    c: Coincident(g179,g180)
    c: Coincident(g180,g181)
    c: Coincident(g181,g182)
    c: Coincident(g182,g183)
    c: Coincident(g183,g178)
    c: Equal(g178, g179-g183) x5
    c: PointOnObject(g178,g184)
    c: PointOnObject(g179,g184)
    c: PointOnObject(g180,g184)
    c: PointOnObject(g181,g184)
    c: PointOnObject(g182,g184)
    c: PointOnObject(g183,g184)
    c: PointOnObject(g184,g2)
    c: PointOnObject(g183,g2)
    c: Radius(g23) = 3.35
    c: PointOnObject(g23,g0)
    c: PointOnObject(g30,g3)
    c: PointOnObject(g37,g5)
    c: PointOnObject(g44,g7)
    c: PointOnObject(g51,g9)
    c: PointOnObject(g58,g11)
    c: PointOnObject(g65,g13)
    c: PointOnObject(g72,g15)
    c: PointOnObject(g79,g0)
    c: PointOnObject(g86,g3)
    c: PointOnObject(g93,g5)
    c: PointOnObject(g100,g7)
    c: PointOnObject(g107,g9)
    c: PointOnObject(g114,g11)
    c: PointOnObject(g121,g13)
    c: PointOnObject(g128,g15)
    c: PointOnObject(g135,g0)
    c: PointOnObject(g142,g3)
    c: PointOnObject(g149,g5)
    c: PointOnObject(g156,g7)
    c: PointOnObject(g163,g9)
    c: PointOnObject(g170,g11)
    c: PointOnObject(g177,g13)
    c: PointOnObject(g184,g15)
    c: Radius(g30) = 3.35
    c: Radius(g37) = 3.35
    c: Radius(g44) = 3.35
    c: Radius(g51) = 3.35
    c: Radius(g58) = 3.35
    c: Radius(g65) = 3.35
    c: Radius(g72) = 3.35
    c: Radius(g79) = 3.35
    c: Radius(g86) = 3.35
    c: Radius(g93) = 3.35
    c: Radius(g100) = 3.35
    c: Radius(g107) = 3.35
    c: Radius(g114) = 3.35
    c: Radius(g121) = 3.35
    c: Radius(g128) = 3.35
    c: Radius(g135) = 3.35
    c: Radius(g142) = 3.35
    c: Radius(g149) = 3.35
    c: Radius(g156) = 3.35
    c: Radius(g163) = 3.35
    c: Radius(g170) = 3.35
    c: Radius(g177) = 3.35
    c: Radius(g184) = 3.35
FEATURE [PartDesign::Pocket] Pocket038
  BaseFeature = -> Hole035
  Direction = (0,0,-1)
  Length = 6
  Length2 = 5
  Profile = -> Sketch099
  ReferenceAxis = -> Sketch099 [N_Axis]
  Reversed = true
  Type = 0
FEATURE [PartDesign::Body] Body005  label="RearPanelPlate"
  Group = -> [Sketch089,Pad033,Binder009,Hole034,Sketch097,Hole035,Sketch099,Pocket038]
  Origin = -> Origin012
  Tip = -> Pocket038
FEATURE [App::Part] Part005  label="RearPanel"
  Group = -> [Body005,LCS_RearPanelOrigin,Sketch016]
  Origin = -> Origin011
FEATURE [Part::FeaturePython] MGN9_Z_Left  # link proxy (typed FeaturePython)
  AttachedBy = #LCS_Origin
  AttachedTo = Parent Assembly#LCS_Origin
  Length = 175
  LinkedObject = -> <external ../../AppData/Local/Temp/FreeCAD/Cache/FreeCAD_Doc_b771bde3-d604-4bf0-b2c0-fa68c06b88b6_da39a3_1616>#Assembly
  Position = 0
  SolverId = Asm4EE
  SourceObject = -> <external MGN9.FCStd>#Assembly
  expr: Placement = LCS_Origin.Placement * AttachmentOffset * varTmpDoc_10#LCS_Origin.Placement ^ -1
  expr: Position = <<Variables>>.PositionZ
FEATURE [Part::FeaturePython] MGN9_Z_Right  # link proxy (typed FeaturePython)
  AttachedBy = #LCS_Origin
  AttachedTo = RightPanel#LCS_RightPanelZRailOrigin
  Length = 175
  LinkedObject = -> <external ../../AppData/Local/Temp/FreeCAD/Cache/FreeCAD_Doc_0e739f10-988f-47ea-a0ae-2bb79bd32ce8_da39a3_1616>#Assembly
  Placement = pos=(110,2.22e-14,-160) rot=(0,-1,0;1.5708rad)
  Position = 70
  SolverId = Asm4EE
  SourceObject = -> <external MGN9.FCStd>#Assembly
  expr: Placement = RightPanel.Placement * LCS_RightPanelZRailOrigin.Placement * AttachmentOffset * varTmpDoc_11#LCS_Origin.Placement ^ -1
FEATURE [Sketcher::SketchObject] Sketch100
  FullyConstrained = true
  MapMode = 5
  Support = -> [XY_Plane044]
  expr: Constraints[28] = -(<<Variables>>.CavitySpacingX + <<Variables>>.WallThickness)
  expr: Constraints[29] = -(<<Variables>>.CavitySpacingY + <<Variables>>.WallThickness)
  expr: Constraints[30] = <<Variables>>.WallThickness
  expr: Constraints[31] = <<Variables>>.WallThickness + 10
  sketch-geometry (12):
    g0: ArcOfCircle CenterX=0 CenterY=0 CenterZ=0 NormalX=0 NormalY=0 NormalZ=1 AngleXU=0 Radius=6 StartAngle=1e-16 EndAngle=2.94023
    g1: LineSegment StartX=5 StartY=-10 StartZ=0 EndX=5 EndY=-15 EndZ=0
    g2: LineSegment StartX=-12 StartY=-17 StartZ=0 EndX=3 EndY=-17 EndZ=0
    g3: LineSegment StartX=-17 StartY=-12 StartZ=0 EndX=-12 EndY=-17 EndZ=0
    g4: LineSegment StartX=-17 StartY=-12 StartZ=0 EndX=-17 EndY=0 EndZ=0
    g5: LineSegment StartX=6 StartY=7e-16 StartZ=0 EndX=6 EndY=-9 EndZ=0
    g6: ArcOfCircle CenterX=5 CenterY=-9 CenterZ=0 NormalX=0 NormalY=0 NormalZ=1 AngleXU=0 Radius=1 StartAngle=4.71239 EndAngle=6.28319
    g7: ArcOfCircle CenterX=-7.34847 CenterY=1.5 CenterZ=0 NormalX=0 NormalY=0 NormalZ=1 AngleXU=0 Radius=1.5 StartAngle=4.71239 EndAngle=6.08183
    g8: LineSegment StartX=-7.34847 StartY=4e-16 StartZ=0 EndX=-17 EndY=4e-16 EndZ=0
    g9: GeomPoint X=-17 Y=-17 Z=0
    g10: LineSegment StartX=3 StartY=-17 StartZ=0 EndX=5 EndY=-15 EndZ=0
    g11: GeomPoint X=5 Y=-17 Z=0
  constraints (32):
    c: Coincident(g0,g-1)
    c: Diameter(g0) = 12
    c: Angle(g3) = -0.785398
    c: Horizontal(g2)
    c: Vertical(g1)
    c: Vertical(g5)
    c: Horizontal(g8)
    c: Vertical(g4)
    c: Coincident(g2,g3)
    c: Coincident(g6,g1)
    c: PointOnObject(g6,g1)
    c: Tangent(g6,g5) = 1.5708
    c: Tangent(g0,g5) = 1.5708
    c: Tangent(g7,g0) = 1.5708
    c: Tangent(g7,g8) = 1.5708
    c: Coincident(g8,g4)
    c: Coincident(g4,g3)
    c: DistanceX(g3,g2) = 5
    c: PointOnObject(g9,g4)
    c: PointOnObject(g9,g2)
    c: Diameter(g7) = 3
    c: Coincident(g10,g2)
    c: Angle(g10) = 0.785398
    c: Coincident(g10,g1)
    c: PointOnObject(g11,g1)
    c: PointOnObject(g11,g2)
    c: DistanceX(g2,g1) = 2
    c: DistanceX(g11) = 5
    c: DistanceX(g9) = -17
    c: DistanceY(g9) = -17
    c: DistanceY(g11,g1) = 7
    c: DistanceY(g9,g4) = 17
FEATURE [PartDesign::Pad] Pad038
  Direction = (0,0,1)
  Length = 14
  Length2 = 10
  Profile = -> Sketch100
  ReferenceAxis = -> Sketch100 [N_Axis]
  Reversed = true
  Type = 0
FEATURE [Sketcher::SketchObject] Sketch101
  FullyConstrained = true
  MapMode = 5
  Support = -> [XY_Plane043]
  expr: Constraints[12] = -<<Variables>>.CavitySpacingY
  sketch-geometry (8):
    g0: ArcOfCircle CenterX=0 CenterY=0 CenterZ=0 NormalX=0 NormalY=0 NormalZ=1 AngleXU=0 Radius=6 StartAngle=1e-16 EndAngle=1.47976
    g1: ArcOfCircle CenterX=0.5 CenterY=5.47723 CenterZ=0 NormalX=0 NormalY=0 NormalZ=1 AngleXU=0 Radius=0.5 StartAngle=1.47976 EndAngle=3.14159
    g2: ArcOfCircle CenterX=5 CenterY=-9 CenterZ=0 NormalX=0 NormalY=0 NormalZ=1 AngleXU=0 Radius=1 StartAngle=4.71239 EndAngle=6.28319
    g3: LineSegment StartX=0 StartY=-9 StartZ=0 EndX=0 EndY=5.47723 EndZ=0
    g4: LineSegment StartX=6 StartY=7e-16 StartZ=0 EndX=6 EndY=-9 EndZ=0
    g5: LineSegment StartX=1 StartY=-10 StartZ=0 EndX=5 EndY=-10 EndZ=0
    g6: ArcOfCircle CenterX=1 CenterY=-9 CenterZ=0 NormalX=0 NormalY=0 NormalZ=1 AngleXU=0 Radius=1 StartAngle=3.14159 EndAngle=4.71239
    g7: GeomPoint X=0 Y=-10 Z=0
  constraints (20):
    c: Coincident(g0,g-1)
    c: Diameter(g0) = 12
    c: Tangent(g0,g1) = -1.5708
    c: PointOnObject(g7,g-2)
    c: Vertical(g3)
    c: Vertical(g4)
    c: Tangent(g0,g4) = 1.5708
    c: Tangent(g4,g2) = 1.5708
    c: DistanceX(g2) = 5
    c: Tangent(g1,g3) = 1.5708
    c: Diameter(g1) = 1
    c: Coincident(g5,g2)
    c: DistanceY(g2) = -10
    c: Horizontal(g5)
    c: PointOnObject(g7,g5)
    c: PointOnObject(g7,g3)
    c: Tangent(g5,g6) = -1.5708
    c: Tangent(g3,g6) = 1.5708
    c: Diameter(g6) = 2
    c: Vertical(g2,g2)
FEATURE [PartDesign::Pad] Pad039
  BaseFeature = -> Pad038
  Direction = (0,0,1)
  Length = 10
  Length2 = 10
  Profile = -> Sketch101
  ReferenceAxis = -> Sketch101 [N_Axis]
  Type = 0
FEATURE [Sketcher::SketchObject] Sketch102
  FullyConstrained = true
  MapMode = 5
  Placement = pos=(0,0,0) rot=(1,0,0;1.5708rad)
  Support = -> [XZ_Plane044]
  sketch-geometry (5):
    g0: LineSegment StartX=3 StartY=12 StartZ=0 EndX=3 EndY=10 EndZ=0
    g1: LineSegment StartX=3 StartY=10 StartZ=0 EndX=6 EndY=7 EndZ=0
    g2: LineSegment StartX=6 StartY=7 StartZ=0 EndX=8 EndY=7 EndZ=0
    g3: LineSegment StartX=8 StartY=7 StartZ=0 EndX=8 EndY=12 EndZ=0
    g4: LineSegment StartX=8 StartY=12 StartZ=0 EndX=3 EndY=12 EndZ=0
  constraints (15):
    c: Vertical(g0)
    c: Coincident(g0,g1)
    c: Coincident(g1,g2)
    c: Horizontal(g2)
    c: Coincident(g2,g3)
    c: Vertical(g3)
    c: Coincident(g3,g4)
    c: Coincident(g4,g0)
    c: Horizontal(g4)
    c: Angle(g1) = -0.785398
    c: DistanceX(g4,g4) = 5
    c: DistanceY(g3,g3) = 5
    c: DistanceY(g0) = 10
    c: DistanceX(g0,g1) = 3
    c: DistanceX(g1) = 6
FEATURE [PartDesign::Pocket] Pocket039
  BaseFeature = -> Pad039
  Direction = (0,1,2e-16)
  Length = 5
  Length2 = 5
  Midplane = true
  Profile = -> Sketch102
  ReferenceAxis = -> Sketch102 [N_Axis]
  Type = 1
FEATURE [Sketcher::SketchObject] Sketch103
  AttachmentOffset = pos=(0,0,6) rot=(0,0,1;0rad)
  FullyConstrained = true
  MapMode = 5
  Placement = pos=(6,-1.3e-15,1.3e-15) rot=(0.57735,0.57735,0.57735;2.0944rad)
  Support = -> [YZ_Plane044]
  sketch-geometry (1):
    g0: Circle CenterX=0 CenterY=5 CenterZ=0 NormalX=0 NormalY=0 NormalZ=1 AngleXU=0 Radius=1.5
  constraints (3):
    c: PointOnObject(g0,g-2)
    c: DistanceY(g0) = 5
    c: Diameter(g0) = 3
FEATURE [PartDesign::Hole] Hole037
  BaseFeature = -> Pocket039
  CustomThreadClearance = 0
  Depth = 25
  DepthType = 0
  Diameter = 3.4
  DrillForDepth = false
  DrillPoint = 1
  DrillPointAngle = 118
  HoleCutCountersinkAngle = 90
  HoleCutCustomValues = false
  HoleCutDepth = 1
  HoleCutDiameter = 6.1
  HoleCutType = 1
  ModelThread = false
  Profile = -> Sketch103
  Tapered = false
  TaperedAngle = 90
  ThreadClass = 0
  ThreadDepth = 25
  ThreadDepthType = 0
  ThreadDirection = 0
  ThreadFit = 0
  ThreadSize = 9
  ThreadType = 1
  Threaded = false
  UseCustomThreadClearance = false
FEATURE [Sketcher::SketchObject] Sketch104
  AttachmentOffset = pos=(0,0,-5) rot=(0,0,1;0rad)
  FullyConstrained = true
  MapMode = 5
  Placement = pos=(0,0,-5) rot=(0,0,1;0rad)
  Support = -> [XY_Plane044]
  expr: Constraints[0] = -(<<Variables>>.CavitySpacingX - 5)
  expr: Constraints[1] = -<<Variables>>.CavitySpacingY
  sketch-geometry (1):
    g0: Circle CenterX=-5 CenterY=-10 CenterZ=0 NormalX=0 NormalY=0 NormalZ=1 AngleXU=0 Radius=3.05
  constraints (3):
    c: DistanceX(g0) = -5
    c: DistanceY(g0) = -10
    c: Diameter(g0) = 6.1
FEATURE [PartDesign::Hole] Hole038
  BaseFeature = -> Hole037
  CustomThreadClearance = 0
  Depth = 25
  DepthType = 0
  Diameter = 3.4
  DrillForDepth = false
  DrillPoint = 1
  DrillPointAngle = 118
  HoleCutCountersinkAngle = 90
  HoleCutCustomValues = false
  HoleCutDepth = 3.4
  HoleCutDiameter = 6.3
  HoleCutType = 0
  ModelThread = false
  Profile = -> Sketch104
  Reversed = true
  Tapered = false
  TaperedAngle = 90
  ThreadClass = 0
  ThreadDepth = 25
  ThreadDepthType = 0
  ThreadDirection = 0
  ThreadFit = 0
  ThreadSize = 9
  ThreadType = 1
  Threaded = false
  UseCustomThreadClearance = false
FEATURE [Sketcher::SketchObject] Sketch105
  FullyConstrained = true
  MapMode = 5
  Support = -> [XY_Plane044]
  sketch-geometry (1):
    g0: Circle CenterX=0 CenterY=0 CenterZ=0 NormalX=0 NormalY=0 NormalZ=1 AngleXU=0 Radius=1.5
  constraints (2):
    c: Coincident(g0,g-1)
    c: Diameter(g0) = 3
FEATURE [PartDesign::Hole] Hole039
  BaseFeature = -> Hole038
  CustomThreadClearance = 0
  Depth = 25
  DepthType = 0
  Diameter = 2.5
  DrillForDepth = false
  DrillPoint = 1
  DrillPointAngle = 118
  HoleCutCountersinkAngle = 90
  HoleCutCustomValues = false
  HoleCutDepth = 0
  HoleCutDiameter = 6.1
  HoleCutType = 0
  ModelThread = false
  Profile = -> Sketch105
  Tapered = false
  TaperedAngle = 90
  ThreadClass = 0
  ThreadDepth = 25
  ThreadDepthType = 0
  ThreadDirection = 0
  ThreadFit = 0
  ThreadSize = 9
  ThreadType = 1
  Threaded = true
  UseCustomThreadClearance = false
FEATURE [Part::FeaturePython] Clone085  label="M3 inserted Nut RightPullyMount 1"  # Draft clone (typed FeaturePython)
  AttacherType = Attacher::AttachEngine3D
  Fuse = false
  Objects = -> [Body013]
  Placement = pos=(0,0,-8) rot=(0,0,1;0rad)
  Scale = (1,1,1)
FEATURE [PartDesign::Pocket] Pocket040
  BaseFeature = -> Hole039
  Direction = (0,0,-1)
  Length = 10
  Length2 = 5
  Profile = -> Sketch104
  ReferenceAxis = -> Sketch104 [N_Axis]
  Type = 0
FEATURE [PartDesign::Pad] Pad040
  BaseFeature = -> Pocket040
  Direction = (0,0,1)
  Length = 0.1
  Length2 = 10
  Profile = -> Sketch104
  ReferenceAxis = -> Sketch104 [N_Axis]
  Reversed = true
  Type = 0
FEATURE [PartDesign::Boolean] Boolean008
  BaseFeature = -> Pad040
  Group = -> [Clone085]
  Refine = true
  Type = 1
FEATURE [PartDesign::Body] Body023  label="RightPullyMountBody"
  Group = -> [Sketch100,Pad038,Sketch101,Pad039,Sketch102,Pocket039,Sketch103,Hole037,Sketch104,Hole038,Sketch105,Hole039,Pocket040,Pad040,Boolean008]
  Origin = -> Origin044
  Tip = -> Boolean008
FEATURE [PartDesign::CoordinateSystem] LCS_RightPullyMountOrigin
  AttacherType = Attacher::AttachEngine3D
  AttachmentOffset = pos=(100,100,60) rot=(0,0,-1;1.5708rad)
  MapMode = 3
  Placement = pos=(100,100,-60) rot=(0,1,0;3.14159rad)
  Support = -> [Y_Axis044]
  expr: .AttachmentOffset.Base.x = <<Variables>>.GantorySpacing / 2
  expr: .AttachmentOffset.Base.y = <<Variables>>.GantorySpacing / 2
FEATURE [App::Link] RightPullyMount  label="RightPullyMount001"
  AssemblyType = Part::Link
  AttachedBy = #LCS_RightPullyMountOrigin
  AttachedTo = Parent Assembly#LCS_Origin
  LinkPlacement = pos=(100,-100,-60) rot=(0,-1,0;3.14159rad)
  LinkedObject = -> Part017
  Placement = pos=(100,-100,-60) rot=(0,-1,0;3.14159rad)
  SolverId = Asm4EE
  expr: Placement = LCS_Origin.Placement * AttachmentOffset * LCS_RightPullyMountOrigin.Placement ^ -1
FEATURE [Sketcher::SketchObject] Sketch106
  FullyConstrained = true
  MapMode = 5
  Support = -> [XY_Plane046]
  sketch-geometry (8):
    g0: LineSegment StartX=-6.1 StartY=6.5 StartZ=0 EndX=6.1 EndY=6.5 EndZ=0
    g1: LineSegment StartX=6.35 StartY=6.25 StartZ=0 EndX=6.35 EndY=0 EndZ=0
    g2: LineSegment StartX=6.35 StartY=0 StartZ=0 EndX=-6.35 EndY=0 EndZ=0
    g3: LineSegment StartX=-6.35 StartY=0 StartZ=0 EndX=-6.35 EndY=6.25 EndZ=0
    g4: ArcOfCircle CenterX=-6.1 CenterY=6.25 CenterZ=0 NormalX=0 NormalY=0 NormalZ=1 AngleXU=0 Radius=0.25 StartAngle=1.5708 EndAngle=3.14159
    g5: GeomPoint X=-6.35 Y=6.5 Z=0
    g6: ArcOfCircle CenterX=6.1 CenterY=6.25 CenterZ=0 NormalX=0 NormalY=0 NormalZ=1 AngleXU=0 Radius=0.25 StartAngle=7.504e-13 EndAngle=1.5708
    g7: GeomPoint X=6.35 Y=6.5 Z=0
  constraints (18):
    c: Coincident(g1,g2)
    c: Coincident(g2,g3)
    c: Vertical(g3)
    c: PointOnObject(g5,g0)
    c: PointOnObject(g5,g3)
    c: Tangent(g0,g4) = 1.5708
    c: Tangent(g3,g4) = 1.5708
    c: PointOnObject(g7,g0)
    c: PointOnObject(g7,g1)
    c: Tangent(g0,g6) = 1.5708
    c: Tangent(g1,g6) = 1.5708
    c: Symmetric(g7,g5,g-2)
    c: DistanceX(g5,g7) = 12.7
    c: Symmetric(g2,g1,g-2)
    c: PointOnObject(g2,g-1)
    c: Equal(g4,g6)
    c: Diameter(g4) = 0.5
    c: DistanceY(g5) = 6.5
FEATURE [PartDesign::Pad] Pad041
  Direction = (0,0,1)
  Length = 5.7
  Length2 = 10
  Midplane = true
  Profile = -> Sketch106
  ReferenceAxis = -> Sketch106 [N_Axis]
  Type = 0
FEATURE [Sketcher::SketchObject] Sketch107
  FullyConstrained = true
  MapMode = 5
  Support = -> [XY_Plane046]
  sketch-geometry (12):
    g0: LineSegment StartX=-6.4 StartY=0 StartZ=0 EndX=-6.4 EndY=3 EndZ=0
    g1: LineSegment StartX=-6.4 StartY=3 StartZ=0 EndX=-2.75 EndY=3 EndZ=0
    g2: LineSegment StartX=-1.75 StartY=2 StartZ=0 EndX=-1.75 EndY=1 EndZ=0
    g3: LineSegment StartX=-1.75 StartY=1 StartZ=0 EndX=1.75 EndY=1 EndZ=0
    g4: LineSegment StartX=1.75 StartY=1 StartZ=0 EndX=1.75 EndY=2 EndZ=0
    g5: LineSegment StartX=2.75 StartY=3 StartZ=0 EndX=6.4 EndY=3 EndZ=0
    g6: LineSegment StartX=6.4 StartY=3 StartZ=0 EndX=6.4 EndY=0 EndZ=0
    g7: LineSegment StartX=6.4 StartY=0 StartZ=0 EndX=-6.4 EndY=0 EndZ=0
    g8: ArcOfCircle CenterX=-2.75 CenterY=2 CenterZ=0 NormalX=0 NormalY=0 NormalZ=1 AngleXU=0 Radius=1 StartAngle=0 EndAngle=1.5708
    g9: GeomPoint X=-1.75 Y=3 Z=0
    g10: ArcOfCircle CenterX=2.75 CenterY=2 CenterZ=0 NormalX=0 NormalY=0 NormalZ=1 AngleXU=0 Radius=1 StartAngle=1.5708 EndAngle=3.14159
    g11: GeomPoint X=1.75 Y=3 Z=0
  constraints (28):
    c: PointOnObject(g0,g-1)
    c: Vertical(g0)
    c: Coincident(g0,g1)
    c: Horizontal(g1)
    c: Vertical(g2)
    c: Coincident(g2,g3)
    c: Coincident(g3,g4)
    c: Coincident(g5,g6)
    c: Coincident(g6,g7)
    c: Coincident(g7,g0)
    c: Symmetric(g2,g3,g-2)
    c: Symmetric(g0,g6,g-2)
    c: Symmetric(g0,g5,g-2)
    c: PointOnObject(g9,g1)
    c: PointOnObject(g9,g2)
    c: Tangent(g1,g8) = 1.5708
    c: Tangent(g2,g8) = 1.5708
    c: PointOnObject(g11,g5)
    c: PointOnObject(g11,g4)
    c: Tangent(g5,g10) = 1.5708
    c: Tangent(g4,g10) = 1.5708
    c: Symmetric(g9,g11,g-2)
    c: Equal(g8,g10)
    c: Diameter(g8) = 2
    c: DistanceX(g7,g7) = 12.8
    c: DistanceY(g0) = 3
    c: DistanceX(g3,g3) = 3.5
    c: DistanceY(g2) = 1
FEATURE [PartDesign::Pad] Pad042
  BaseFeature = -> Pad041
  Direction = (0,0,1)
  Length = 5.8
  Length2 = 10
  Midplane = true
  Profile = -> Sketch107
  ReferenceAxis = -> Sketch107 [N_Axis]
  Type = 0
FEATURE [Sketcher::SketchObject] Sketch108
  FullyConstrained = true
  MapMode = 5
  Support = -> [XY_Plane047]
  sketch-geometry (1):
    g0: Circle CenterX=-1.95 CenterY=6.4 CenterZ=0 NormalX=0 NormalY=0 NormalZ=1 AngleXU=0 Radius=0.6
  constraints (3):
    c: Diameter(g0) = 1.2
    c: DistanceY(g0) = 6.4
    c: DistanceX(g0) = -1.95
FEATURE [PartDesign::Pad] Pad043
  Direction = (0,0,1)
  Length = 2.9
  Length2 = 10
  Midplane = true
  Profile = -> Sketch108
  ReferenceAxis = -> Sketch108 [N_Axis]
  Type = 0
FEATURE [PartDesign::Body] Body025  label="MicroSwitchButton"
  Group = -> [Sketch108,Pad043]
  Origin = -> Origin047
  Tip = -> Pad043
FEATURE [Sketcher::SketchObject] Sketch109
  FullyConstrained = true
  MapMode = 5
  Support = -> [XY_Plane046]
  sketch-geometry (2):
    g0: Circle CenterX=-3.25 CenterY=1.5 CenterZ=0 NormalX=0 NormalY=0 NormalZ=1 AngleXU=0 Radius=1
    g1: Circle CenterX=3.25 CenterY=1.5 CenterZ=0 NormalX=0 NormalY=0 NormalZ=1 AngleXU=0 Radius=1
  constraints (5):
    c: Symmetric(g0,g1,g-2)
    c: DistanceX(g0,g1) = 6.5
    c: DistanceY(g0) = 1.5
    c: Equal(g0,g1)
    c: Diameter(g0) = 2
FEATURE [PartDesign::Pocket] Pocket041
  BaseFeature = -> Pad042
  Direction = (0,0,-1)
  Length = 5
  Length2 = 5
  Midplane = true
  Profile = -> Sketch109
  ReferenceAxis = -> Sketch109 [N_Axis]
  Type = 1
FEATURE [PartDesign::Body] Body024  label="MicroSwitchBody"
  Group = -> [Sketch106,Pad041,Sketch107,Pad042,Sketch109,Pocket041]
  Origin = -> Origin046
  Tip = -> Pocket041
FEATURE [App::Part] Part018  label="MicroSwitch"
  Group = -> [Body024,Body025]
  Origin = -> Origin045
FEATURE [App::Link] LimitSwitch_Y
  AssemblyType = Part::Link
  LinkPlacement = pos=(-102,-92,-20) rot=(0,1,0;3.14159rad)
  LinkedObject = -> Part018
  Placement = pos=(-102,-92,-20) rot=(0,1,0;3.14159rad)
FEATURE [PartDesign::CoordinateSystem] LCS_RightPanelZRailOrigin
  AttacherType = Attacher::AttachEngine3D
  AttachmentOffset = pos=(0,0,-100) rot=(-0.57735,-0.57735,-0.57735;2.0944rad)
  MapMode = 2
  Placement = pos=(-100,2.22e-14,-2.22e-14) rot=(0,0,1;0rad)
  Support = -> [Y_Axis014]
  expr: .AttachmentOffset.Base.z = -200 / 2
FEATURE [Sketcher::SketchObject] Sketch110
  FullyConstrained = true
  MapMode = 5
  Placement = pos=(0,0,0) rot=(1,0,0;1.5708rad)
  Support = -> [XZ_Plane010]
  expr: Constraints[9] = <<Variables>>.GantorySpacing + <<Variables>>.CavitySpacingX * 2
  sketch-geometry (4):
    g0: LineSegment StartX=-110 StartY=100 StartZ=0 EndX=110 EndY=100 EndZ=0
    g1: LineSegment StartX=110 StartY=100 StartZ=0 EndX=110 EndY=60 EndZ=0
    g2: LineSegment StartX=110 StartY=60 StartZ=0 EndX=-110 EndY=60 EndZ=0
    g3: LineSegment StartX=-110 StartY=60 StartZ=0 EndX=-110 EndY=100 EndZ=0
  constraints (10):
    c: Coincident(g0,g1)
    c: Coincident(g1,g2)
    c: Coincident(g2,g3)
    c: Coincident(g3,g0)
    c: Vertical(g3)
    c: Symmetric(g2,g1,g-2)
    c: Symmetric(g0,g0,g-2)
    c: DistanceY(g2) = 60
    c: DistanceY(g0) = 100
    c: DistanceX(g0,g0) = 220
FEATURE [PartDesign::Pocket] Pocket042  label="Pocket TopPanel BaseHeight"
  BaseFeature = -> Pad011
  Direction = (0,1,2e-16)
  Length = 220
  Length2 = 5
  Midplane = true
  Profile = -> Sketch110
  ReferenceAxis = -> Sketch110 [N_Axis]
  Type = 0
  expr: Length = <<Variables>>.GantorySpacing + <<Variables>>.CavitySpacingY * 2
FEATURE [Sketcher::SketchObject] Sketch111
  AttachmentOffset = pos=(0,0,8) rot=(0,0,1;0rad)
  FullyConstrained = true
  MapMode = 5
  Placement = pos=(0,0,8) rot=(0,0,1;0rad)
  Support = -> [XY_Plane010]
  expr: Constraints[2] = Sketch042.Constraints[9]
  expr: Constraints[3] = Sketch042.Constraints[10]
  expr: Constraints[6] = Sketch042.Constraints[13]
  expr: Constraints[9] = Sketch042.Constraints[19]
  sketch-geometry (11):
    g0: Circle CenterX=98.7 CenterY=-90.5 CenterZ=0 NormalX=0 NormalY=0 NormalZ=1 AngleXU=0 Radius=2
    g1: Circle CenterX=105.2 CenterY=-90.5 CenterZ=0 NormalX=0 NormalY=0 NormalZ=1 AngleXU=0 Radius=2
    g2: LineSegment StartX=-100 StartY=-90.5 StartZ=0 EndX=100 EndY=-90.5 EndZ=0
    g3: LineSegment StartX=100 StartY=90.5 StartZ=0 EndX=100 EndY=-90.5 EndZ=0
    g4: Circle CenterX=-98.7 CenterY=-90.5 CenterZ=0 NormalX=0 NormalY=0 NormalZ=1 AngleXU=0 Radius=2
    g5: Circle CenterX=-105.2 CenterY=-90.5 CenterZ=0 NormalX=0 NormalY=0 NormalZ=1 AngleXU=0 Radius=2
    g6: LineSegment StartX=-100 StartY=90.5 StartZ=0 EndX=-100 EndY=-90.5 EndZ=0
    g7: Circle CenterX=-98.7 CenterY=90.5 CenterZ=0 NormalX=0 NormalY=0 NormalZ=1 AngleXU=0 Radius=2
    g8: Circle CenterX=-105.2 CenterY=90.5 CenterZ=0 NormalX=0 NormalY=0 NormalZ=1 AngleXU=0 Radius=2
    g9: Circle CenterX=98.7 CenterY=90.5 CenterZ=0 NormalX=0 NormalY=0 NormalZ=1 AngleXU=0 Radius=2
    g10: Circle CenterX=105.2 CenterY=90.5 CenterZ=0 NormalX=0 NormalY=0 NormalZ=1 AngleXU=0 Radius=2
  constraints (26):
    c: Equal(g0,g1)
    c: Diameter(g0) = 4
    c: DistanceX(g0,g1) = 6.5
    c: DistanceY(g2) = -90.5
    c: PointOnObject(g0,g2)
    c: PointOnObject(g1,g2)
    c: DistanceX(g0,g3) = 1.3
    c: Symmetric(g2,g2,g-2)
    c: Symmetric(g6,g3,g-2)
    c: DistanceX(g6,g3) = 200
    c: Equal(g5,g0)
    c: Equal(g0,g4)
    c: Symmetric(g4,g0,g-2)
    c: Symmetric(g1,g5,g-2)
    c: Symmetric(g6,g6,g-1)
    c: Symmetric(g3,g3,g-1)
    c: PointOnObject(g2,g3)
    c: PointOnObject(g3,g2)
    c: Symmetric(g9,g0,g-1)
    c: Symmetric(g10,g1,g-1)
    c: Symmetric(g7,g4,g-1)
    c: Symmetric(g8,g5,g-1)
    c: Equal(g9,g0)
    c: Equal(g0,g10)
    c: Equal(g0,g7)
    c: Equal(g0,g8)
FEATURE [PartDesign::Pocket] Pocket044  label="Pocket TopPanel CutFront"
  BaseFeature = -> Pocket042
  Direction = (0,1,2e-16)
  Length = 5
  Length2 = 5
  Profile = -> Sketch110
  ReferenceAxis = -> Sketch110 [N_Axis]
  Reversed = true
  Type = 1
FEATURE [PartDesign::Pocket] Pocket005  label="Pocket TopPanel BottomFace Left"
  BaseFeature = -> Pocket044
  Direction = (-1,2e-16,-3e-16)
  Length = 7
  Length2 = 5
  Profile = -> Sketch025
  ReferenceAxis = -> Sketch025 [N_Axis]
  Type = 0
  expr: Length = <<Variables>>.WallThickness
FEATURE [PartDesign::Mirrored] Mirrored  label="Mirrored TopPanel BottomFace Right"
  BaseFeature = -> Pocket005
  MirrorPlane = -> YZ_Plane010
  Originals = -> [Pocket005]
FEATURE [PartDesign::Hole] Hole031  label="Hole TopPanel BottomFace LR"
  BaseFeature = -> Mirrored
  CustomThreadClearance = 0
  Depth = 676.187
  DepthType = 1
  Diameter = 2.5
  DrillForDepth = false
  DrillPoint = 1
  DrillPointAngle = 118
  HoleCutCountersinkAngle = 90
  HoleCutCustomValues = false
  HoleCutDepth = 0
  HoleCutDiameter = 6.1
  HoleCutType = 0
  ModelThread = false
  Profile = -> Sketch025
  Tapered = false
  TaperedAngle = 90
  ThreadClass = 0
  ThreadDepth = 676.187
  ThreadDepthType = 0
  ThreadDirection = 0
  ThreadFit = 0
  ThreadSize = 9
  ThreadType = 1
  Threaded = true
  UseCustomThreadClearance = false
FEATURE [PartDesign::Pocket] Pocket010  label="Pocket TopPanel RearFitting"
  BaseFeature = -> Hole031
  Direction = (0,1,2e-16)
  Length = 7
  Length2 = 5
  Profile = -> Sketch031
  ReferenceAxis = -> Sketch031 [N_Axis]
  Reversed = true
  Type = 0
  expr: Length = <<Variables>>.WallThickness
FEATURE [PartDesign::Hole] Hole011  label="Hole TopPanel RearFitting"
  BaseFeature = -> Pocket010
  CustomThreadClearance = 0
  Depth = 25
  DepthType = 0
  Diameter = 2.5
  DrillForDepth = false
  DrillPoint = 1
  DrillPointAngle = 118
  HoleCutCountersinkAngle = 90
  HoleCutCustomValues = false
  HoleCutDepth = 3.4
  HoleCutDiameter = 6.1
  HoleCutType = 0
  ModelThread = false
  Profile = -> Sketch031
  Reversed = true
  Tapered = false
  TaperedAngle = 90
  ThreadClass = 0
  ThreadDepth = 25
  ThreadDepthType = 0
  ThreadDirection = 0
  ThreadFit = 0
  ThreadSize = 9
  ThreadType = 1
  Threaded = true
  UseCustomThreadClearance = false
FEATURE [PartDesign::Pocket] Pocket003  label="Pocket TopPanel Cavity 1"
  BaseFeature = -> Hole011
  Direction = (0,1,2e-16)
  Length = 180
  Length2 = 5
  Midplane = true
  Profile = -> Sketch022
  ReferenceAxis = -> Sketch022 [N_Axis]
  Type = 0
  expr: Length = <<Variables>>.GantorySpacing - 20
FEATURE [PartDesign::Pocket] Pocket004  label="Pocket TopPanel Cavity 2"
  BaseFeature = -> Pocket003
  Direction = (-1,2e-16,-3e-16)
  Length = 220
  Length2 = 5
  Midplane = true
  Profile = -> Sketch023
  ReferenceAxis = -> Sketch023 [N_Axis]
  Type = 0
  expr: Length = <<Variables>>.GantorySpacing + <<Variables>>.CavitySpacingX * 2
FEATURE [PartDesign::Hole] Hole009  label="Hole TopPanel BottomFaceFitting"
  BaseFeature = -> Pocket004
  CustomThreadClearance = 0
  Depth = 25
  DepthType = 0
  Diameter = 3.4
  DrillForDepth = false
  DrillPoint = 1
  DrillPointAngle = 118
  HoleCutCountersinkAngle = 90
  HoleCutCustomValues = false
  HoleCutDepth = 9
  HoleCutDiameter = 6
  HoleCutType = 1
  ModelThread = false
  Profile = -> Sketch032
  Reversed = true
  Tapered = false
  TaperedAngle = 90
  ThreadClass = 0
  ThreadDepth = 25
  ThreadDepthType = 0
  ThreadDirection = 0
  ThreadFit = 0
  ThreadSize = 9
  ThreadType = 1
  Threaded = false
  UseCustomThreadClearance = false
FEATURE [PartDesign::Pad] Pad030  label="Pad TopPanel BottomFaceFitting Support"
  BaseFeature = -> Hole009
  Direction = (0,0,1)
  Length = 0.2
  Length2 = 10
  Profile = -> Binder008
  Reversed = true
  Type = 0
FEATURE [PartDesign::Pad] Pad009  label="Pad TopPanel PullyMount"
  BaseFeature = -> Pad030
  Direction = (0,0,1)
  Length = 60
  Length2 = 10
  Profile = -> Sketch028
  ReferenceAxis = -> Sketch028 [N_Axis]
  Type = 0
  expr: Length = 60
FEATURE [PartDesign::Pad] Pad044  label="Pad TopPanel LimitSwitchMount"
  BaseFeature = -> Pad009
  Direction = (0,0,1)
  Length = 17
  Length2 = 10
  Profile = -> Sketch042
  ReferenceAxis = -> Sketch042 [N_Axis]
  Type = 0
  expr: Length = <<Variables>>.TopThickness + 7
FEATURE [PartDesign::Pocket] Pocket009  label="Pocket TopPanel MotorCut"
  BaseFeature = -> Pad044
  Direction = (0,0,-1)
  Length = 32
  Length2 = 5
  Profile = -> Sketch030
  ReferenceAxis = -> Sketch030 [N_Axis]
  Type = 0
  expr: Length = 60 - <<Variables>>.TopThickness - 17 - 1
FEATURE [PartDesign::Pocket] Pocket011  label="Pocket TopPanel PullyMountFitting"
  BaseFeature = -> Pocket009
  Direction = (0,0,-1)
  Length = 14
  Length2 = 5
  Profile = -> Sketch033
  ReferenceAxis = -> Sketch033 [N_Axis]
  Type = 0
  expr: Length = 60 - <<Variables>>.TopThickness - 17 - 19
FEATURE [PartDesign::Pocket] Pocket012  label="Pocket TopPanel PullyFitting"
  BaseFeature = -> Pocket011
  Direction = (0,0,-1)
  Length = 33
  Length2 = 5
  Profile = -> Sketch037
  ReferenceAxis = -> Sketch037 [N_Axis]
  Type = 0
  expr: Length = 60 - <<Variables>>.TopThickness - 17
FEATURE [PartDesign::Hole] Hole007  label="Hole TopPanel PullyFitting"
  BaseFeature = -> Pocket012
  CustomThreadClearance = 0
  Depth = 688.477
  DepthType = 1
  Diameter = 3.4
  DrillForDepth = false
  DrillPoint = 1
  DrillPointAngle = 118
  HoleCutCountersinkAngle = 90
  HoleCutCustomValues = false
  HoleCutDepth = 21
  HoleCutDiameter = 6
  HoleCutType = 1
  ModelThread = false
  Profile = -> Binder002
  Reversed = true
  Tapered = false
  TaperedAngle = 90
  ThreadClass = 0
  ThreadDepth = 688.477
  ThreadDepthType = 0
  ThreadDirection = 0
  ThreadFit = 0
  ThreadSize = 9
  ThreadType = 1
  Threaded = false
  UseCustomThreadClearance = false
FEATURE [PartDesign::Pad] Pad031  label="Pad TopPanel PullyFitting Support"
  BaseFeature = -> Hole007
  Direction = (0,0,1)
  Length = 0.2
  Length2 = 10
  Profile = -> Sketch088
  ReferenceAxis = -> Sketch088 [N_Axis]
  Type = 0
FEATURE [Sketcher::SketchObject] Sketch112
  FullyConstrained = true
  MapMode = 5
  Placement = pos=(0,0,0) rot=(1,0,0;1.5708rad)
  Support = -> [XZ_Plane015]
  expr: Constraints[8] = -<<Variables>>.WallThickness
  sketch-geometry (3):
    g0: LineSegment StartX=-210 StartY=13 StartZ=0 EndX=-190 EndY=-7 EndZ=0
    g1: LineSegment StartX=-190 StartY=-7 StartZ=0 EndX=-210 EndY=-7 EndZ=0
    g2: LineSegment StartX=-210 StartY=-7 StartZ=0 EndX=-210 EndY=13 EndZ=0
  constraints (9):
    c: Horizontal(g1)
    c: Coincident(g1,g2)
    c: Coincident(g2,g0)
    c: Angle(g0) = -0.785398
    c: DistanceX(g0) = -190
    c: Vertical(g2)
    c: DistanceX(g1,g1) = 20
    c: Coincident(g1,g0)
    c: DistanceY(g0) = -7
FEATURE [Sketcher::SketchObject] Sketch113
  FullyConstrained = true
  MapMode = 5
  Placement = pos=(0,0,0) rot=(1,0,0;1.5708rad)
  Support = -> [XZ_Plane018]
  sketch-geometry (4):
    g0: LineSegment StartX=-95 StartY=10 StartZ=0 EndX=95 EndY=10 EndZ=0
    g1: LineSegment StartX=95 StartY=10 StartZ=0 EndX=95 EndY=0 EndZ=0
    g2: LineSegment StartX=95 StartY=0 StartZ=0 EndX=-95 EndY=0 EndZ=0
    g3: LineSegment StartX=-95 StartY=0 StartZ=0 EndX=-95 EndY=10 EndZ=0
  constraints (10):
    c: Coincident(g0,g1)
    c: Coincident(g1,g2)
    c: Coincident(g2,g3)
    c: Coincident(g3,g0)
    c: Symmetric(g0,g0,g-2)
    c: Symmetric(g2,g1,g-2)
    c: Vertical(g3)
    c: PointOnObject(g2,g-1)
    c: DistanceY(g3,g3) = 10
    c: DistanceX(g2,g2) = 190
FEATURE [PartDesign::Pad] Pad047
  Direction = (0,-1,-2e-16)
  Length = 234
  Length2 = 10
  Midplane = true
  Placement = pos=(0,0,0) rot=(1,0,0;1.5708rad)
  Profile = -> Sketch113
  ReferenceAxis = -> Sketch113 [N_Axis]
  Type = 0
  expr: Length = <<Variables>>.GantorySpacing + (<<Variables>>.CavitySpacingY + <<Variables>>.WallThickness) * 2
FEATURE [PartDesign::Body] Body008  label="BottomPanelPlate"
  Group = -> [Sketch113,Pad047]
  Origin = -> Origin018
  Tip = -> Pad047
FEATURE [App::Part] Part008  label="BottomPanel"
  Group = -> [Body008,LCS_BottomPanelOrigin]
  Origin = -> Origin017
FEATURE [PartDesign::Pad] Pad048  label="Pad RightPanel UnderFrame"
  Direction = (0,-1,-2e-16)
  Length = 220
  Length2 = 10
  Midplane = true
  Placement = pos=(0,0,0) rot=(1,0,0;1.5708rad)
  Profile = -> Sketch069
  ReferenceAxis = -> Sketch069 [N_Axis]
  Type = 0
  expr: Length = <<Variables>>.GantorySpacing + <<Variables>>.CavitySpacingY * 2
FEATURE [Sketcher::SketchObject] Sketch114
  AttachmentOffset = pos=(0,0,10) rot=(0,0,1;0rad)
  FullyConstrained = true
  MapMode = 5
  Placement = pos=(0,0,10) rot=(0,0,1;0rad)
  Support = -> [XY_Plane015]
  expr: Constraints[5] = <<Variables>>.GantorySpacing
  sketch-geometry (8):
    g0: LineSegment StartX=0 StartY=100 StartZ=0 EndX=-190 EndY=100 EndZ=0
    g1: LineSegment StartX=-200 StartY=90 StartZ=0 EndX=-200 EndY=-90 EndZ=0
    g2: LineSegment StartX=-190 StartY=-100 StartZ=0 EndX=0 EndY=-100 EndZ=0
    g3: LineSegment StartX=0 StartY=-100 StartZ=0 EndX=0 EndY=100 EndZ=0
    g4: ArcOfCircle CenterX=-190 CenterY=90 CenterZ=0 NormalX=0 NormalY=0 NormalZ=1 AngleXU=0 Radius=10 StartAngle=1.5708 EndAngle=3.14159
    g5: GeomPoint X=-200 Y=100 Z=0
    g6: ArcOfCircle CenterX=-190 CenterY=-90 CenterZ=0 NormalX=0 NormalY=0 NormalZ=1 AngleXU=0 Radius=10 StartAngle=3.14159 EndAngle=4.71239
    g7: GeomPoint X=-200 Y=-100 Z=0
  constraints (18):
    c: Coincident(g2,g3)
    c: Coincident(g3,g0)
    c: Horizontal(g0)
    c: PointOnObject(g0,g-2)
    c: Symmetric(g0,g2,g-1)
    c: DistanceY(g2,g0) = 200
    c: Symmetric(g7,g5,g-1)
    c: PointOnObject(g5,g0)
    c: PointOnObject(g5,g1)
    c: Tangent(g0,g4) = -1.5708
    c: Tangent(g1,g4) = -1.5708
    c: PointOnObject(g7,g1)
    c: PointOnObject(g7,g2)
    c: Tangent(g1,g6) = -1.5708
    c: Tangent(g2,g6) = -1.5708
    c: Equal(g4,g6)
    c: Diameter(g4) = 20
    c: DistanceX(g5) = -200
FEATURE [PartDesign::Pocket] Pocket046  label="Pocket RightPanel UnderFrameCut"
  BaseFeature = -> Pad048
  Direction = (0,0,-1)
  Length = 5
  Length2 = 5
  Placement = pos=(0,0,0) rot=(1,0,0;1.5708rad)
  Profile = -> Sketch114
  ReferenceAxis = -> Sketch114 [N_Axis]
  Reversed = true
  Type = 1
FEATURE [Sketcher::SketchObject] Sketch115
  FullyConstrained = true
  MapMode = 5
  Placement = pos=(0,0,0) rot=(1,0,0;1.5708rad)
  Support = -> [XZ_Plane015]
  sketch-geometry (5):
    g0: LineSegment StartX=-190 StartY=0 StartZ=0 EndX=-210 EndY=0 EndZ=0
    g1: LineSegment StartX=-210 StartY=0 StartZ=0 EndX=-210 EndY=20 EndZ=0
    g2: ArcOfCircle CenterX=-190 CenterY=20 CenterZ=0 NormalX=0 NormalY=0 NormalZ=1 AngleXU=0 Radius=10 StartAngle=3.14159 EndAngle=4.71239
    g3: LineSegment StartX=-210 StartY=20 StartZ=0 EndX=-200 EndY=20 EndZ=0
    g4: LineSegment StartX=-190 StartY=10 StartZ=0 EndX=-190 EndY=0 EndZ=0
  constraints (16):
    c: Horizontal(g0)
    c: Coincident(g0,g1)
    c: Vertical(g1)
    c: PointOnObject(g0,g-1)
    c: DistanceX(g0) = -210
    c: DistanceY(g1) = 20
    c: Coincident(g3,g1)
    c: Horizontal(g3)
    c: Coincident(g3,g2)
    c: DistanceX(g3,g3) = 10
    c: Coincident(g4,g2)
    c: Vertical(g4)
    c: Coincident(g4,g0)
    c: DistanceY(g4,g4) = 10
    c: DistanceX(g0,g0) = 20
    c: Diameter(g2) = 20
FEATURE [PartDesign::Pad] Pad050  label="Pad RightPanel UnderFrameFillet"
  BaseFeature = -> Pocket046
  Direction = (0,-1,-2e-16)
  Length = 220
  Length2 = 10
  Midplane = true
  Placement = pos=(0,0,0) rot=(1,0,0;1.5708rad)
  Profile = -> Sketch115
  ReferenceAxis = -> Sketch115 [N_Axis]
  Type = 0
  expr: Length = <<Variables>>.GantorySpacing + <<Variables>>.CavitySpacingY * 2
FEATURE [PartDesign::Pad] Pad032  label="Pad RightPanel Plate"
  BaseFeature = -> Pad050
  Direction = (1,-2e-16,3e-16)
  Length = 210
  Length2 = 10
  Placement = pos=(0,0,0) rot=(1,0,0;1.5708rad)
  Profile = -> Sketch026
  ReferenceAxis = -> Sketch026 [N_Axis]
  Reversed = true
  Type = 0
FEATURE [PartDesign::Pad] Pad046  label="Pad RightPanel Frame"
  BaseFeature = -> Pad032
  Direction = (0,0,1)
  Length = 10
  Length2 = 10
  Placement = pos=(0,0,0) rot=(1,0,0;1.5708rad)
  Profile = -> Sketch035
  ReferenceAxis = -> Sketch035 [N_Axis]
  Type = 0
FEATURE [Sketcher::SketchObject] Sketch116
  AttachmentOffset = pos=(0,0,-210) rot=(0,0,1;0rad)
  FullyConstrained = true
  MapMode = 5
  Placement = pos=(-210,4.66e-14,-4.66e-14) rot=(0.57735,0.57735,0.57735;2.0944rad)
  Support = -> [YZ_Plane015]
  expr: Constraints[1] = <<Variables>>.GantorySpacing
  expr: Constraints[2] = <<Variables>>.CavitySpacingX
  sketch-geometry (2):
    g0: Circle CenterX=-100 CenterY=10 CenterZ=0 NormalX=0 NormalY=0 NormalZ=1 AngleXU=0 Radius=10
    g1: Circle CenterX=100 CenterY=10 CenterZ=0 NormalX=0 NormalY=0 NormalZ=1 AngleXU=0 Radius=10
  constraints (5):
    c: Symmetric(g0,g1,g-2)
    c: DistanceX(g0,g1) = 200
    c: DistanceY(g0) = 10
    c: Equal(g0,g1)
    c: Diameter(g0) = 20
FEATURE [PartDesign::CoordinateSystem] LCS_Pully80TOrigin
  AttacherType = Attacher::AttachEngine3D
  AttachmentOffset = pos=(0,-12.73,255) rot=(0,0,1;0rad)
  MapMode = 2
  Placement = pos=(0,-12.73,255) rot=(0,0,1;0rad)
  Support = -> [X_Axis048]
  expr: .AttachmentOffset.Base.y = -(<<Variables>>.PullyDiameterDrive + <<Variables>>.PullyDiameterIdler) / 2
FEATURE [Sketcher::SketchObject] Sketch118
  FullyConstrained = true
  MapMode = 5
  Support = -> [XY_Plane051]
  sketch-geometry (4):
    g0: LineSegment StartX=-75 StartY=75 StartZ=0 EndX=75 EndY=75 EndZ=0
    g1: LineSegment StartX=75 StartY=75 StartZ=0 EndX=75 EndY=-75 EndZ=0
    g2: LineSegment StartX=75 StartY=-75 StartZ=0 EndX=-75 EndY=-75 EndZ=0
    g3: LineSegment StartX=-75 StartY=-75 StartZ=0 EndX=-75 EndY=75 EndZ=0
  constraints (11):
    c: Coincident(g0,g1)
    c: Coincident(g1,g2)
    c: Coincident(g2,g3)
    c: Coincident(g3,g0)
    c: Horizontal(g0)
    c: Horizontal(g2)
    c: Vertical(g1)
    c: Vertical(g3)
    c: Symmetric(g0,g1,g-1)
    c: Equal(g0,g3)
    c: DistanceY(g3,g3) = 150
FEATURE [PartDesign::Pad] Pad051
  Direction = (0,0,1)
  Length = 7
  Length2 = 10
  Profile = -> Sketch118
  ReferenceAxis = -> Sketch118 [N_Axis]
  Reversed = true
  Type = 0
FEATURE [PartDesign::Body] Body027  label="PrintBedPlate"
  Group = -> [Sketch118,Pad051]
  Origin = -> Origin051
  Tip = -> Pad051
FEATURE [PartDesign::CoordinateSystem] LCS_PrintBedOrigin
  AttacherType = Attacher::AttachEngine3D
  AttachmentOffset = pos=(0,0,60) rot=(0,0,1;0rad)
  MapMode = 2
  Placement = pos=(0,0,60) rot=(0,0,1;0rad)
  Support = -> [X_Axis050]
FEATURE [App::Link] PrintBed  label="PrintBed001"
  AssemblyType = Part::Link
  AttachedBy = #LCS_PrintBedOrigin
  AttachedTo = Parent Assembly#LCS_Origin
  AttachmentOffset = pos=(0,0,-140) rot=(0,0,1;0rad)
  LinkPlacement = pos=(0,0,-200) rot=(0,0,1;0rad)
  LinkedObject = -> Part020
  Placement = pos=(0,0,-200) rot=(0,0,1;0rad)
  SolverId = Asm4EE
  expr: .AttachmentOffset.Base.z = -<<Variables>>.PrintBedPosition
  expr: Placement = LCS_Origin.Placement * AttachmentOffset * LCS_PrintBedOrigin.Placement ^ -1
FEATURE [Sketcher::SketchObject] Sketch119
  FullyConstrained = true
  MapMode = 5
  Support = -> [XY_Plane052]
  sketch-geometry (4):
    g0: LineSegment StartX=-60 StartY=60 StartZ=0 EndX=60 EndY=60 EndZ=0
    g1: LineSegment StartX=60 StartY=60 StartZ=0 EndX=60 EndY=-60 EndZ=0
    g2: LineSegment StartX=60 StartY=-60 StartZ=0 EndX=-60 EndY=-60 EndZ=0
    g3: LineSegment StartX=-60 StartY=-60 StartZ=0 EndX=-60 EndY=60 EndZ=0
  constraints (11):
    c: Coincident(g0,g1)
    c: Coincident(g1,g2)
    c: Coincident(g2,g3)
    c: Coincident(g3,g0)
    c: Horizontal(g0)
    c: Horizontal(g2)
    c: Vertical(g1)
    c: Vertical(g3)
    c: Symmetric(g0,g1,g-1)
    c: Equal(g3,g0)
    c: DistanceY(g3,g3) = 120
FEATURE [PartDesign::Pad] Pad052
  Direction = (0,0,1)
  Length = 150
  Length2 = 10
  Profile = -> Sketch119
  ReferenceAxis = -> Sketch119 [N_Axis]
  Reversed = true
  Type = 0
FEATURE [PartDesign::Body] Body028  label="PrintBedBuildVolume"
  Group = -> [Sketch119,Pad052]
  Origin = -> Origin052
  Tip = -> Pad052
FEATURE [App::Link] Nema17
  AssemblyType = Part::Link
  LinkPlacement = pos=(50,-25,-255) rot=(0,1,0;1.5708rad)
  LinkedObject = -> <external Drive.FCStd>#Part
  Placement = pos=(50,-25,-255) rot=(0,1,0;1.5708rad)
FEATURE [Sketcher::SketchObject] Sketch120
  AttachmentOffset = pos=(0,0,-7) rot=(0,0,1;0rad)
  FullyConstrained = true
  MapMode = 5
  Placement = pos=(0,0,-7) rot=(0,0,1;0rad)
  Support = -> [XY_Plane053]
  sketch-geometry (7):
    g0: Circle CenterX=0 CenterY=60 CenterZ=0 NormalX=0 NormalY=0 NormalZ=1 AngleXU=0 Radius=6
    g1: Circle CenterX=-60 CenterY=-60 CenterZ=0 NormalX=0 NormalY=0 NormalZ=1 AngleXU=0 Radius=6
    g2: Circle CenterX=60 CenterY=-60 CenterZ=0 NormalX=0 NormalY=0 NormalZ=1 AngleXU=0 Radius=6
    g3: LineSegment StartX=-75 StartY=75 StartZ=0 EndX=75 EndY=75 EndZ=0
    g4: LineSegment StartX=75 StartY=75 StartZ=0 EndX=75 EndY=-75 EndZ=0
    g5: LineSegment StartX=75 StartY=-75 StartZ=0 EndX=-75 EndY=-75 EndZ=0
    g6: LineSegment StartX=-75 StartY=-75 StartZ=0 EndX=-75 EndY=75 EndZ=0
  constraints (19):
    c: PointOnObject(g0,g-2)
    c: Coincident(g3,g4)
    c: Coincident(g4,g5)
    c: Coincident(g5,g6)
    c: Coincident(g6,g3)
    c: Horizontal(g3)
    c: Horizontal(g5)
    c: Vertical(g4)
    c: Vertical(g6)
    c: Symmetric(g3,g4,g-1)
    c: Equal(g6,g3)
    c: DistanceY(g6,g6) = 150
    c: DistanceY(g0) = 60
    c: Symmetric(g1,g2,g-2)
    c: DistanceY(g1) = -60
    c: DistanceX(g1,g2) = 120
    c: Equal(g0,g1)
    c: Equal(g0,g2)
    c: Diameter(g0) = 12
FEATURE [PartDesign::Body] Body029  label="PrintBedSpacer"
  Group = -> [Sketch120]
  Origin = -> Origin053
FEATURE [App::Part] Part020  label="PrintBed"
  Group = -> [Body027,LCS_PrintBedOrigin,Body028,Body029]
  Origin = -> Origin050
FEATURE [Sketcher::SketchObject] Sketch004
  FullyConstrained = true
  MapMode = 5
  Placement = pos=(0,0,0) rot=(1,0,0;1.5708rad)
  Support = -> [XZ_Plane003]
  expr: Constraints[19] = <<Variables>>.PullyDiameterIdler / 2
  sketch-geometry (8):
    g0: LineSegment StartX=2.5 StartY=4.25 StartZ=0 EndX=2.5 EndY=-4.25 EndZ=0
    g1: LineSegment StartX=2.5 StartY=-4.25 StartZ=0 EndX=9 EndY=-4.25 EndZ=0
    g2: LineSegment StartX=9 StartY=-4.25 StartZ=0 EndX=9 EndY=-3.25 EndZ=0
    g3: LineSegment StartX=9 StartY=-3.25 StartZ=0 EndX=6.365 EndY=-3.25 EndZ=0
    g4: LineSegment StartX=6.365 StartY=-3.25 StartZ=0 EndX=6.365 EndY=3.25 EndZ=0
    g5: LineSegment StartX=6.365 StartY=3.25 StartZ=0 EndX=9 EndY=3.25 EndZ=0
    g6: LineSegment StartX=9 StartY=3.25 StartZ=0 EndX=9 EndY=4.25 EndZ=0
    g7: LineSegment StartX=9 StartY=4.25 StartZ=0 EndX=2.5 EndY=4.25 EndZ=0
  constraints (22):
    c: Coincident(g0,g1)
    c: Horizontal(g1)
    c: Coincident(g1,g2)
    c: Vertical(g2)
    c: Coincident(g2,g3)
    c: Horizontal(g3)
    c: Coincident(g3,g4)
    c: Coincident(g4,g5)
    c: Horizontal(g5)
    c: Coincident(g5,g6)
    c: Vertical(g6)
    c: Coincident(g6,g7)
    c: Coincident(g7,g0)
    c: Horizontal(g7)
    c: Symmetric(g0,g0,g-1)
    c: Symmetric(g4,g3,g-1)
    c: DistanceY(g6,g6) = 1
    c: DistanceY(g4,g4) = 6.5
    c: DistanceX(g-1,g0) = 2.5
    c: DistanceX(g-1,g4) = 6.365
    c: DistanceX(g-1,g6) = 9
    c: Vertical(g2,g5)
FEATURE [PartDesign::Revolution] Revolution
  Angle = 360
  Axis = (0,-2e-16,1)
  Base = (0,0,0)
  Placement = pos=(0,0,0) rot=(1,0,0;1.5708rad)
  Profile = -> Sketch004
  ReferenceAxis = -> Sketch004 [V_Axis]
FEATURE [PartDesign::Body] Body  label="IdlerBody"
  Group = -> [Sketch004,Revolution]
  Origin = -> Origin003
  Tip = -> Revolution
FEATURE [App::Part] Part001  label="PullyIdler"
  Group = -> [Body,LCS_PullyIdlerOrigin]
  Origin = -> Origin002
FEATURE [Sketcher::SketchObject] Sketch117
  FullyConstrained = true
  MapMode = 5
  Support = -> [XY_Plane049]
  expr: Constraints[58] = <<Variables>>.GantorySpacing + <<Variables>>.CavitySpacingX * 2 - 13
  expr: Constraints[61] = <<Variables>>.GantorySpacing - 44
  sketch-geometry (37):
    g0: LineSegment StartX=-103.5 StartY=0 StartZ=0 EndX=-103.5 EndY=-8 EndZ=0
    g1: LineSegment StartX=-89 StartY=-4 StartZ=0 EndX=-89 EndY=-8 EndZ=0
    g2: LineSegment StartX=-89 StartY=-8 StartZ=0 EndX=-81.5 EndY=-8 EndZ=0
    g3: LineSegment StartX=-81.5 StartY=-8 StartZ=0 EndX=-81.5 EndY=-6 EndZ=0
    g4: LineSegment StartX=-81.5 StartY=-6 StartZ=0 EndX=-74.5 EndY=-6 EndZ=0
    g5: LineSegment StartX=-74.5 StartY=-6 StartZ=0 EndX=-74.5 EndY=-8 EndZ=0
    g6: LineSegment StartX=-74.5 StartY=-8 StartZ=0 EndX=-73 EndY=-8 EndZ=0
    g7: LineSegment StartX=-73 StartY=-8 StartZ=0 EndX=-73 EndY=-2.5 EndZ=0
    g8: LineSegment StartX=73 StartY=-2.5 StartZ=0 EndX=73 EndY=-8 EndZ=0
    g9: LineSegment StartX=73 StartY=-8 StartZ=0 EndX=74.5 EndY=-8 EndZ=0
    g10: LineSegment StartX=74.5 StartY=-8 StartZ=0 EndX=74.5 EndY=-6 EndZ=0
    g11: LineSegment StartX=74.5 StartY=-6 StartZ=0 EndX=81.5 EndY=-6 EndZ=0
    g12: LineSegment StartX=81.5 StartY=-6 StartZ=0 EndX=81.5 EndY=-8 EndZ=0
    g13: LineSegment StartX=81.5 StartY=-8 StartZ=0 EndX=89 EndY=-8 EndZ=0
    g14: LineSegment StartX=89 StartY=-8 StartZ=0 EndX=89 EndY=-4 EndZ=0
    g15: LineSegment StartX=103.5 StartY=-8 StartZ=0 EndX=103.5 EndY=0 EndZ=0
    g16: LineSegment StartX=103.5 StartY=0 StartZ=0 EndX=-103.5 EndY=0 EndZ=0
    g17: LineSegment StartX=-103.5 StartY=-8 StartZ=0 EndX=-98.5 EndY=-8 EndZ=0
    g18: LineSegment StartX=-98.5 StartY=-8 StartZ=0 EndX=-98.5 EndY=-4 EndZ=0
    g19: LineSegment StartX=-98.5 StartY=-4 StartZ=0 EndX=-89 EndY=-4 EndZ=0
    g20: LineSegment StartX=89 StartY=-4 StartZ=0 EndX=98.5 EndY=-4 EndZ=0
    g21: LineSegment StartX=98.5 StartY=-4 StartZ=0 EndX=98.5 EndY=-8 EndZ=0
    g22: LineSegment StartX=98.5 StartY=-8 StartZ=0 EndX=103.5 EndY=-8 EndZ=0
    g23: GeomPoint X=0 Y=0 Z=0
    g24: GeomPoint X=-78 Y=-6 Z=0
    g25: GeomPoint X=78 Y=-6 Z=0
    g26: LineSegment StartX=72 StartY=-2.5 StartZ=0 EndX=73 EndY=-2.5 EndZ=0
    g27: LineSegment StartX=72 StartY=-4.5 StartZ=0 EndX=72 EndY=-2.5 EndZ=0
    g28: LineSegment StartX=66.5 StartY=-10 StartZ=0 EndX=72 EndY=-4.5 EndZ=0
    g29: LineSegment StartX=66.5 StartY=-26 StartZ=0 EndX=66.5 EndY=-10 EndZ=0
    g30: LineSegment StartX=65.5 StartY=-25 StartZ=0 EndX=66.5 EndY=-26 EndZ=0
    g31: LineSegment StartX=56.5 StartY=-25 StartZ=0 EndX=65.5 EndY=-25 EndZ=0
    g32: LineSegment StartX=55.5 StartY=-26 StartZ=0 EndX=56.5 EndY=-25 EndZ=0
    g33: LineSegment StartX=55.5 StartY=-6 StartZ=0 EndX=55.5 EndY=-26 EndZ=0
    g34: LineSegment StartX=-73 StartY=-2.5 StartZ=0 EndX=50 EndY=-2.5 EndZ=0
    g35: LineSegment StartX=50 StartY=-2.5 StartZ=0 EndX=50 EndY=-6 EndZ=0
    g36: LineSegment StartX=50 StartY=-6 StartZ=0 EndX=55.5 EndY=-6 EndZ=0
  constraints (93):
    c: Coincident(g0,g17)
    c: Coincident(g19,g1)
    c: Coincident(g1,g2)
    c: Coincident(g2,g3)
    c: Coincident(g3,g4)
    c: Coincident(g4,g5)
    c: Coincident(g5,g6)
    c: Coincident(g6,g7)
    c: Coincident(g7,g34)
    c: Coincident(g26,g8)
    c: Coincident(g8,g9)
    c: Coincident(g9,g10)
    c: Coincident(g10,g11)
    c: Coincident(g11,g12)
    c: Coincident(g12,g13)
    c: Coincident(g13,g14)
    c: Coincident(g14,g20)
    c: Coincident(g22,g15)
    c: Coincident(g15,g16)
    c: Coincident(g16,g0)
    c: Symmetric(g0,g15,g-2)
    c: Symmetric(g0,g22,g-2)
    c: Vertical(g0)
    c: Symmetric(g19,g14,g-2)
    c: Vertical(g1)
    c: Symmetric(g13,g1,g-2)
    c: Horizontal(g2)
    c: Symmetric(g2,g12,g-2)
    c: Symmetric(g3,g11,g-2)
    c: Vertical(g3)
    c: Horizontal(g4)
    c: Symmetric(g4,g10,g-2)
    c: Vertical(g5)
    c: Horizontal(g6)
    c: Vertical(g7)
    c: Symmetric(g5,g9,g-2)
    c: Symmetric(g6,g8,g-2)
    c: Symmetric(g7,g26,g-2)
    c: Coincident(g17,g18)
    c: Horizontal(g17)
    c: Coincident(g18,g19)
    c: Horizontal(g19)
    c: Coincident(g20,g21)
    c: Coincident(g21,g22)
    c: Vertical(g18)
    c: Symmetric(g17,g21,g-2)
    c: Symmetric(g18,g20,g-2)
    c: PointOnObject(g23,g16)
    c: DistanceY(g0,g23) = 8
    c: DistanceY(g1,g23) = 4
    c: DistanceY(g7,g23) = 2.5
    c: DistanceX(g17,g17) = 5
    c: DistanceX(g2,g2) = 7.5
    c: DistanceX(g6,g6) = 1.5
    c: DistanceX(g4,g4) = 7
    c: DistanceY(g1,g23) = 8
    c: DistanceY(g3,g23) = 6
    c: DistanceY(g5,g23) = 8
    c: DistanceX(g16,g16) = 207
    c: Symmetric(g3,g4,g24)
    c: Symmetric(g24,g25,g-2)
    c: DistanceX(g24,g25) = 156
    c: Coincident(g27,g26)
    c: Coincident(g28,g27)
    c: Coincident(g29,g28)
    c: Coincident(g30,g29)
    c: Coincident(g31,g30)
    c: Coincident(g32,g31)
    c: Coincident(g33,g32)
    c: Coincident(g36,g33)
    c: Coincident(g34,g35)
    c: Coincident(g35,g36)
    c: Horizontal(g34)
    c: Vertical(g35)
    c: Horizontal(g36)
    c: Vertical(g33)
    c: Angle(g32) = 0.785398
    c: Angle(g30) = -0.785398
    c: Angle(g28) = 0.785398
    c: Horizontal(g31)
    c: Vertical(g29)
    c: Horizontal(g26)
    c: Vertical(g27)
    c: DistanceY(g35,g23) = 6
    c: DistanceX(g36,g36) = 5.5
    c: DistanceY(g31,g23) = 25
    c: DistanceX(g31,g31) = 9
    c: DistanceX(g32,g31) = 1
    c: DistanceX(g30,g29) = 1
    c: DistanceX(g33,g27) = 16.5
    c: DistanceY(g27,g23) = 4.5
    c: DistanceX(g23,g34) = 50
    c: Coincident(g23,g-1)
FEATURE [PartDesign::Revolution] Revolution001
  Angle = 360
  Axis = (1,0,0)
  Base = (0,0,0)
  Profile = -> Sketch117
  ReferenceAxis = -> Sketch117 [H_Axis]
  Reversed = true
FEATURE [PartDesign::Body] Body026
  Group = -> [Sketch117,Revolution001]
  Origin = -> Origin049
  Tip = -> Revolution001
FEATURE [App::Part] Part019  label="ZDrive"
  Group = -> [Body026,LCS_Pully80TOrigin]
  Origin = -> Origin048
FEATURE [App::Link] miniXY_ZDrive
  AttachedBy = #LCS_Origin
  AttachedTo = Parent Assembly#LCS_Origin
  AttachmentOffset = pos=(0,12.73,-255) rot=(0,0,1;0rad)
  LinkPlacement = pos=(0,12.73,-255) rot=(0,0,1;0rad)
  LinkedObject = -> <external miniXY-ZDrive.FCStd>#Model
  Placement = pos=(0,12.73,-255) rot=(0,0,1;0rad)
  SolverId = Asm4EE
  expr: .AttachmentOffset.Base.y = (<<Variables>>.PullyDiameterDrive + <<Variables>>.PullyDiameterIdler) / 2
  expr: Placement = LCS_Origin.Placement * AttachmentOffset * miniXY_ZDrive#LCS_Origin.Placement ^ -1
FEATURE [App::Part] Assembly
  AssemblyType = Part::Link
  Group = -> [LCS_Origin,Variables,Constraints,Configurations,MGN9_X,Gantory,MGN9_Y_Left,MGN9_Y_Right,CarriageLeftOuterIdler,CarriageLeftInnerIdler,TopPanel,PullyIdlerFrontLeft,PullyIdlerFrontRight,StepperLeft,RearPanel,LeftPanel,RightPanel,BottomPanel,FrontPanel,Hat,MGN9_Z,StepperRight,StepperMountRight,UpperBracket,StepperMountLeft001,MGN9_Z_Left,MGN9_Z_Right,RightPullyMount,LimitSwitch_Y,PrintBed,Nema17,+1 more]
  Origin = -> Origin
  Type = Assembly
FEATURE [PartDesign::CoordinateSystem] LCS_DrivePullyRightOrigin
  AttacherType = Attacher::AttachEngine3D
  AttachmentOffset = pos=(-43.5,0,14.25) rot=(0,0,1;0rad)
  MapMode = 3
  Placement = pos=(-8.1e-15,-43.5,-14.25) rot=(0.707107,0.707107,0;3.14159rad)
  Support = -> [Y_Axis038]
  expr: .AttachmentOffset.Base.x = -(<<Variables>>.CavitySpacingY + <<Variables>>.WallThickness + 5.5 + 42 / 2)
  expr: .AttachmentOffset.Base.z = 8.5 * 1.5 + 1.5
FEATURE [PartDesign::CoordinateSystem] LCS_DrivePullyLeftOrigin
  AttacherType = Attacher::AttachEngine3D
  AttachmentOffset = pos=(0,-43.5,-4.75) rot=(0,0,1;0rad)
  MapMode = 2
  Placement = pos=(0,-43.5,-4.75) rot=(0,0,1;0rad)
  Support = -> [X_Axis042]
  expr: .AttachmentOffset.Base.y = -(<<Variables>>.CavitySpacingY + <<Variables>>.WallThickness + 5.5 + 42 / 2)
  expr: .AttachmentOffset.Base.z = -(8.5 / 2 + 0.5)
FEATURE [PartDesign::CoordinateSystem] LCS_IdlerRightRearOrigin
  AttacherType = Attacher::AttachEngine3D
  AttachmentOffset = pos=(0,0,4.75) rot=(0,0,1;0rad)
  MapMode = 3
  Placement = pos=(5e-16,-5e-16,-4.75) rot=(0.707107,0.707107,0;3.14159rad)
  Support = -> [Y_Axis038]
  expr: .AttachmentOffset.Base.z = 8.5 / 2 + 0.5
FEATURE [PartDesign::CoordinateSystem] LCS_IdlerStepperRightOrigin
  AttacherType = Attacher::AttachEngine3D
  AttachmentOffset = pos=(-12.73,-12.73,14.25) rot=(0,0,1;0rad)
  MapMode = 3
  Placement = pos=(-12.73,-12.73,-14.25) rot=(0.707107,0.707107,0;3.14159rad)
  Support = -> [Y_Axis038]
  expr: .AttachmentOffset.Base.x = -<<Variables>>.PullyDiameterIdler
  expr: .AttachmentOffset.Base.y = -(<<Variables>>.PullyDiameterDrive + <<Variables>>.PullyDiameterIdler) / 2
  expr: .AttachmentOffset.Base.z = 8.5 * 1.5 + 1.5
FEATURE [App::Part] Part015  label="StepperMountRight"
  Group = -> [StepperBracketRight,LCS_StepperMountRightOrigin,LCS_StepperRightOrigin,LCS_DrivePullyRightOrigin,LCS_IdlerRightRearOrigin,LCS_IdlerStepperRightOrigin]
  Origin = -> Origin038
FEATURE [PartDesign::CoordinateSystem] LCS_IdlerLeftRearOrigin
  AttacherType = Attacher::AttachEngine3D
  AttachmentOffset = pos=(0,0,14.25) rot=(0,0,1;0rad)
  MapMode = 3
  Placement = pos=(1.6e-15,-1.6e-15,-14.25) rot=(0.707107,0.707107,0;3.14159rad)
  Support = -> [Y_Axis042]
  expr: .AttachmentOffset.Base.z = 8.5 * 1.5 + 1.5
FEATURE [PartDesign::CoordinateSystem] LCS_IdlerStepperLeftOrigin
  AttacherType = Attacher::AttachEngine3D
  AttachmentOffset = pos=(-12.73,12.73,4.75) rot=(0,0,1;0rad)
  MapMode = 3
  Placement = pos=(12.73,-12.73,-4.75) rot=(0.707107,0.707107,0;3.14159rad)
  Support = -> [Y_Axis042]
  expr: .AttachmentOffset.Base.x = -<<Variables>>.PullyDiameterIdler
  expr: .AttachmentOffset.Base.y = (<<Variables>>.PullyDiameterDrive + <<Variables>>.PullyDiameterIdler) / 2
  expr: .AttachmentOffset.Base.z = 8.5 / 2 + 0.5
FEATURE [App::Part] StepperMountLeft
  Group = -> [LCS_StepperMountLeft,StepperBracketRight_link,StepperBracketRight_mirrored,LCS_StepperLeftOrigin,LCS_DrivePullyLeftOrigin,LCS_IdlerLeftRearOrigin,LCS_IdlerStepperLeftOrigin]
  Origin = -> Origin042
FEATURE [App::Link] RightPullyMountBody_link
  LinkedObject = -> Body023
FEATURE [Part::Mirroring] RightPullyMountBody_mirrored
  Base = (0,0,0)
  Normal = (1,0,0)
  Source = -> RightPullyMountBody_link
FEATURE [PartDesign::CoordinateSystem] LCS_LeftPullyMountOrigin
  AttacherType = Attacher::AttachEngine3D
  AttachmentOffset = pos=(100,-100,60) rot=(0,0,-1;1.5708rad)
  MapMode = 3
  Placement = pos=(-100,100,-60) rot=(0,1,0;3.14159rad)
  Support = -> [Y_Axis054]
  expr: .AttachmentOffset.Base.x = <<Variables>>.GantorySpacing / 2
  expr: .AttachmentOffset.Base.y = -<<Variables>>.GantorySpacing / 2
FEATURE [PartDesign::CoordinateSystem] LCS_IdlerLeftFrontOrigin
  AttacherType = Attacher::AttachEngine3D
  AttachmentOffset = pos=(0,0,18.75) rot=(0,0,1;0rad)
  MapMode = 3
  Placement = pos=(2.1e-15,-2.1e-15,-18.75) rot=(0.707107,0.707107,0;3.14159rad)
  Support = -> [Y_Axis054]
  expr: .AttachmentOffset.Base.z = 14 + 8.5 / 2 + 0.5
FEATURE [App::Part] LeftPullyMount
  Group = -> [RightPullyMountBody_link,RightPullyMountBody_mirrored,LCS_LeftPullyMountOrigin,LCS_IdlerLeftFrontOrigin]
  Origin = -> Origin054
FEATURE [PartDesign::CoordinateSystem] LCS_IdlerRightFrontOrigin
  AttacherType = Attacher::AttachEngine3D
  AttachmentOffset = pos=(0,0,28.25) rot=(0,0,1;0rad)
  MapMode = 3
  Placement = pos=(3.1e-15,-3.1e-15,-28.25) rot=(0.707107,0.707107,0;3.14159rad)
  Support = -> [Y_Axis043]
  expr: .AttachmentOffset.Base.z = 14 + 8.5 * 1.5 + 1.5
FEATURE [App::Part] Part017  label="RightPullyMount"
  Group = -> [Body023,LCS_RightPullyMountOrigin,LCS_IdlerRightFrontOrigin]
  Origin = -> Origin043
FEATURE [App::Link] RightPanelPlate_link
  LinkedObject = -> Body006
FEATURE [Part::Mirroring] RightPanelPlate_mirrored
  Base = (0,0,0)
  Normal = (1,0,0)
  Source = -> RightPanelPlate_link
FEATURE [PartDesign::CoordinateSystem] LCS_LeftPanelOrigin001  label="LCS_LeftPanelOrigin"
  AttacherType = Attacher::AttachEngine3D
  AttachmentOffset = pos=(110,0,60) rot=(0,0,1;0rad)
  MapMode = 3
  Placement = pos=(-60,5.66e-14,110) rot=(0,-1,0;1.5708rad)
  Support = -> [Z_Axis055]
  expr: .AttachmentOffset.Base.x = (<<Variables>>.GantorySpacing + <<Variables>>.CavitySpacingX * 2) / 2
FEATURE [PartDesign::CoordinateSystem] LCS_ZLeftRailOrigin
  AttacherType = Attacher::AttachEngine3D
  AttachmentOffset = pos=(100,-15,0) rot=(0,0,1;0rad)
  MapMode = 2
  Placement = pos=(100,-15,0) rot=(0,0,1;0rad)
  Support = -> [X_Axis055]
FEATURE [App::Part] LeftPanel001  label="LeftPanel"
  Group = -> [RightPanelPlate_link,RightPanelPlate_mirrored,LCS_LeftPanelOrigin001,LCS_ZLeftRailOrigin]
  Origin = -> Origin055
FEATURE [PartDesign::CoordinateSystem] LCS_ZRightRailOrigin
  AttacherType = Attacher::AttachEngine3D
  AttachmentOffset = pos=(-100,-15,0) rot=(0,0,1;3.14159rad)
  MapMode = 4
  Placement = pos=(-100,-15,-2.83e-14) rot=(0,0,1;3.14159rad)
  Support = -> [Z_Axis014]
FEATURE [Sketcher::SketchObject] Sketch121
  FullyConstrained = true
  MapMode = 5
  Support = -> [XY_Plane015]
  expr: Constraints[0] = Sketch039.Constraints[0]
  expr: Constraints[1] = Sketch039.Constraints[1]
  expr: Constraints[6] = Sketch039.Constraints[6]
  expr: Constraints[7] = Sketch039.Constraints[7]
  sketch-geometry (4):
    g0: GeomPoint X=-195 Y=-27.73 Z=0
    g1: GeomPoint X=-195 Y=-2.27 Z=0
    g2: Circle CenterX=-195 CenterY=-2.27 CenterZ=0 NormalX=0 NormalY=0 NormalZ=1 AngleXU=0 Radius=12
    g3: LineSegment StartX=0 StartY=-15 StartZ=0 EndX=-250 EndY=-15 EndZ=0
  constraints (9):
    c: DistanceX(g1) = -195
    c: DistanceY(g0,g1) = 25.46
    c: Coincident(g2,g1)
    c: Diameter(g2) = 24
    c: PointOnObject(g3,g-2)
    c: Horizontal(g3)
    c: DistanceX(g3,g3) = 250
    c: DistanceY(g3) = -15
    c: Symmetric(g2,g0,g3)
FEATURE [PartDesign::Pad] Pad053  label="Pad RightPanel BearingHold"
  BaseFeature = -> Pad046
  Direction = (0,0,1)
  Length = 15
  Length2 = 10
  Placement = pos=(0,0,0) rot=(1,0,0;1.5708rad)
  Profile = -> Sketch121
  ReferenceAxis = -> Sketch121 [N_Axis]
  Type = 0
  expr: Length = Variables.CavitySpacingX + 5
FEATURE [PartDesign::Pocket] Pocket035  label="Pocket RightPanel BearingHole"
  BaseFeature = -> Pad053
  Direction = (0,0,-1)
  Length = 10
  Length2 = 5
  Placement = pos=(0,0,0) rot=(1,0,0;1.5708rad)
  Profile = -> Sketch039
  ReferenceAxis = -> Sketch039 [N_Axis]
  Reversed = true
  Type = 1
FEATURE [Sketcher::SketchObject] Sketch122
  AttachmentOffset = pos=(0,0,5) rot=(0,0,1;0rad)
  FullyConstrained = true
  MapMode = 5
  Placement = pos=(0,0,5) rot=(0,0,1;0rad)
  Support = -> [XY_Plane015]
  expr: .AttachmentOffset.Base.z = Variables.CavitySpacingX - 5
  expr: Constraints[0] = Sketch039.Constraints[0]
  expr: Constraints[1] = Sketch039.Constraints[1]
  expr: Constraints[6] = Sketch039.Constraints[6]
  expr: Constraints[7] = Sketch039.Constraints[7]
  sketch-geometry (4):
    g0: GeomPoint X=-195 Y=-27.73 Z=0
    g1: GeomPoint X=-195 Y=-2.27 Z=0
    g2: Circle CenterX=-195 CenterY=-2.27 CenterZ=0 NormalX=0 NormalY=0 NormalZ=1 AngleXU=0 Radius=4
    g3: LineSegment StartX=0 StartY=-15 StartZ=0 EndX=-250 EndY=-15 EndZ=0
  constraints (9):
    c: DistanceX(g1) = -195
    c: DistanceY(g0,g1) = 25.46
    c: Coincident(g2,g1)
    c: Diameter(g2) = 8
    c: PointOnObject(g3,g-2)
    c: Horizontal(g3)
    c: DistanceX(g3,g3) = 250
    c: DistanceY(g3) = -15
    c: Symmetric(g2,g0,g3)
FEATURE [PartDesign::Pocket] Pocket048  label="Pocket RightPanel ShaftHole"
  BaseFeature = -> Pocket035
  Direction = (0,0,-1)
  Length = 5
  Length2 = 5
  Placement = pos=(0,0,0) rot=(1,0,0;1.5708rad)
  Profile = -> Sketch122
  ReferenceAxis = -> Sketch122 [N_Axis]
  Reversed = true
  Type = 1
FEATURE [Sketcher::SketchObject] Sketch123
  AttachmentOffset = pos=(0,0,15) rot=(0,0,1;0rad)
  FullyConstrained = true
  MapMode = 5
  Placement = pos=(0,0,15) rot=(0,0,1;0rad)
  Support = -> [XY_Plane015]
  expr: .AttachmentOffset.Base.z = Variables.CavitySpacingX + 5
  expr: Constraints[0] = Sketch039.Constraints[0]
  expr: Constraints[1] = Sketch039.Constraints[1]
  expr: Constraints[6] = Sketch039.Constraints[6]
  expr: Constraints[7] = Sketch039.Constraints[7]
  sketch-geometry (4):
    g0: GeomPoint X=-195 Y=-27.73 Z=0
    g1: GeomPoint X=-195 Y=-2.27 Z=0
    g2: Circle CenterX=-195 CenterY=-2.27 CenterZ=0 NormalX=0 NormalY=0 NormalZ=1 AngleXU=0 Radius=9
    g3: LineSegment StartX=0 StartY=-15 StartZ=0 EndX=-250 EndY=-15 EndZ=0
  constraints (9):
    c: DistanceX(g1) = -195
    c: DistanceY(g0,g1) = 25.46
    c: Coincident(g2,g1)
    c: Diameter(g2) = 18
    c: PointOnObject(g3,g-2)
    c: Horizontal(g3)
    c: DistanceX(g3,g3) = 250
    c: DistanceY(g3) = -15
    c: Symmetric(g2,g0,g3)
FEATURE [PartDesign::Pocket] Pocket049  label="Pocket RightPanel PullyHole"
  BaseFeature = -> Pocket048
  Direction = (0,0,-1)
  Length = 5
  Length2 = 5
  Placement = pos=(0,0,0) rot=(1,0,0;1.5708rad)
  Profile = -> Sketch123
  ReferenceAxis = -> Sketch123 [N_Axis]
  Reversed = true
  Type = 1
FEATURE [PartDesign::Pocket] Pocket023  label="Pocket RightPanel Rail"
  BaseFeature = -> Pocket049
  Direction = (0,0,-1)
  Length = 200
  Length2 = 5
  Placement = pos=(0,0,0) rot=(1,0,0;1.5708rad)
  Profile = -> Sketch072
  ReferenceAxis = -> Sketch072 [N_Axis]
  Reversed = true
  Type = 1
FEATURE [PartDesign::Pad] Pad049  label="Pad RightPanel FootHold"
  BaseFeature = -> Pocket023
  Direction = (1,-2e-16,3e-16)
  Length = 25
  Length2 = 10
  Placement = pos=(0,0,0) rot=(1,0,0;1.5708rad)
  Profile = -> Sketch029
  ReferenceAxis = -> Sketch029 [N_Axis]
  Reversed = true
  Type = 0
FEATURE [PartDesign::Pocket] Pocket047  label="Pocket RightPanel FootHole"
  BaseFeature = -> Pad049
  Direction = (-1,2e-16,-3e-16)
  Length = 10
  Length2 = 5
  Placement = pos=(0,0,0) rot=(1,0,0;1.5708rad)
  Profile = -> Sketch116
  ReferenceAxis = -> Sketch116 [N_Axis]
  Reversed = true
  Type = 0
FEATURE [PartDesign::Pocket] Pocket045  label="Pocket RightPanel UnderCut"
  BaseFeature = -> Pocket047
  Direction = (0,1,2e-16)
  Length = 5
  Length2 = 5
  Midplane = true
  Placement = pos=(0,0,0) rot=(1,0,0;1.5708rad)
  Profile = -> Sketch112
  ReferenceAxis = -> Sketch112 [N_Axis]
  Type = 1
FEATURE [PartDesign::Boolean] Boolean005  label="Boolean RightPanel Kumiko"
  BaseFeature = -> Pocket045
  Group = -> [Body019]
  Refine = true
  Type = 0
FEATURE [PartDesign::Pocket] Pocket024  label="Pocket RightPanel Window"
  BaseFeature = -> Boolean005
  Direction = (0,0,-1)
  Length = 5
  Length2 = 5
  Midplane = true
  Profile = -> Sketch077
  ReferenceAxis = -> Sketch077 [N_Axis]
  Type = 1
FEATURE [PartDesign::Body] Body006  label="RightPanelPlate"
  Group = -> [Pad048,Pocket046,Pad050,Pad032,Pad046,Pad053,Pocket035,Pocket048,Pocket049,Sketch069,Pocket023,Sketch039,Sketch072,Sketch077,Sketch112,Sketch026,Sketch029,Sketch035,Pad049,Pocket047,Pocket045,Sketch123,Boolean005,Pocket024,Sketch115,Sketch114,Sketch116,Sketch121,Sketch122]
  Origin = -> Origin015
  Tip = -> Pocket045
FEATURE [App::Part] Part007  label="RightPanel"
  Group = -> [Body006,LCS_RightPanelOrigin,LCS_RightPanelZRailOrigin,LCS_ZRightRailOrigin]
  Origin = -> Origin014
FEATURE [Part::FeaturePython] Clone086  label="M3 grooved Nut RearSide Left"  # Draft clone (typed FeaturePython)
  AttacherType = Attacher::AttachEngine3D
  Fuse = false
  Objects = -> [Body014]
  Placement = pos=(110,105,25) rot=(-0.250563,-0.935113,0.250563;1.63783rad)
  Scale = (1,1,1)
  expr: .Placement.Base.x = <<Variables>>.GantorySpacing / 2 + <<Variables>>.CavitySpacingX
  expr: .Placement.Base.y = <<Variables>>.GantorySpacing / 2 + 5
FEATURE [Part::FeaturePython] Clone087  label="M3 grooved Nut RearSide Right"  # Draft clone (typed FeaturePython)
  AttacherType = Attacher::AttachEngine3D
  Fuse = false
  Objects = -> [Body014]
  Placement = pos=(-110,105,25) rot=(0.707107,0,0.707107;3.14159rad)
  Scale = (1,1,1)
  expr: .Placement.Base.x = -(<<Variables>>.GantorySpacing / 2 + <<Variables>>.CavitySpacingX)
  expr: .Placement.Base.y = <<Variables>>.GantorySpacing / 2 + 5
FEATURE [Sketcher::SketchObject] Sketch124
  AttachmentOffset = pos=(0,0,117) rot=(0,0,1;0rad)
  FullyConstrained = true
  MapMode = 5
  Placement = pos=(0,-117,-2.6e-14) rot=(1,0,0;1.5708rad)
  Support = -> [XZ_Plane010]
  expr: .AttachmentOffset.Base.z = <<Variables>>.GantorySpacing / 2 + <<Variables>>.CavitySpacingY + <<Variables>>.WallThickness
  expr: Constraints[1] = <<Variables>>.GantorySpacing + 8
  sketch-geometry (2):
    g0: Circle CenterX=-104 CenterY=40 CenterZ=0 NormalX=0 NormalY=0 NormalZ=1 AngleXU=0 Radius=1.25
    g1: Circle CenterX=104 CenterY=40 CenterZ=0 NormalX=0 NormalY=0 NormalZ=1 AngleXU=0 Radius=1.25
  constraints (5):
    c: Symmetric(g0,g1,g-2)
    c: DistanceX(g0,g1) = 208
    c: Equal(g1,g0)
    c: Diameter(g1) = 2.5
    c: DistanceY(g0) = 40
FEATURE [Part::FeaturePython] Clone088  label="M3 inserted Nut Front Left"  # Draft clone (typed FeaturePython)
  AttacherType = Attacher::AttachEngine3D
  Fuse = false
  Objects = -> [Body013]
  Placement = pos=(104,-113,40) rot=(0.57735,-0.57735,-0.57735;4.18879rad)
  Scale = (1,1,1)
  expr: .Placement.Base.x = Variables.GantorySpacing / 2 + 4
  expr: .Placement.Base.y = -(<<Variables>>.GantorySpacing / 2 + <<Variables>>.CavitySpacingY + 3)
FEATURE [Part::FeaturePython] Clone089  label="M3 inserted Nut Front Right"  # Draft clone (typed FeaturePython)
  AttacherType = Attacher::AttachEngine3D
  Fuse = false
  Objects = -> [Body013]
  Placement = pos=(-104,-113,40) rot=(0.580515,-0.575535,-0.575987;4.18839rad)
  Scale = (1,1,1)
  expr: .Placement.Base.x = -(Variables.GantorySpacing / 2 + 4)
  expr: .Placement.Base.y = -(<<Variables>>.GantorySpacing / 2 + <<Variables>>.CavitySpacingY + 3)
FEATURE [PartDesign::Hole] Hole041  label="Hole TopPanel FrontLock"
  BaseFeature = -> Pad031
  CustomThreadClearance = 0
  Depth = 25
  DepthType = 0
  Diameter = 2.5
  DrillForDepth = false
  DrillPoint = 1
  DrillPointAngle = 118
  HoleCutCountersinkAngle = 90
  HoleCutCustomValues = false
  HoleCutDepth = 0
  HoleCutDiameter = 6.1
  HoleCutType = 0
  ModelThread = false
  Profile = -> Sketch124
  Tapered = false
  TaperedAngle = 90
  ThreadClass = 0
  ThreadDepth = 25
  ThreadDepthType = 0
  ThreadDirection = 0
  ThreadFit = 0
  ThreadSize = 9
  ThreadType = 1
  Threaded = true
  UseCustomThreadClearance = false
FEATURE [PartDesign::Hole] Hole040  label="Hole TopPanel LimitSwitchMount"
  BaseFeature = -> Hole041
  CustomThreadClearance = 0
  Depth = 25
  DepthType = 0
  Diameter = 1.6
  DrillForDepth = false
  DrillPoint = 1
  DrillPointAngle = 118
  HoleCutCountersinkAngle = 90
  HoleCutCustomValues = false
  HoleCutDepth = 8
  HoleCutDiameter = 4
  HoleCutType = 1
  ModelThread = false
  Profile = -> Sketch042
  Reversed = true
  Tapered = false
  TaperedAngle = 90
  ThreadClass = 0
  ThreadDepth = 25
  ThreadDepthType = 0
  ThreadDirection = 0
  ThreadFit = 0
  ThreadSize = 6
  ThreadType = 1
  Threaded = true
  UseCustomThreadClearance = false
  expr: HoleCutDepth = <<Variables>>.TopThickness + 7 - 9
FEATURE [PartDesign::Pad] Pad045  label="Pad TopPanel LimitSwitchMount Support"
  BaseFeature = -> Hole040
  Direction = (0,0,1)
  Length = 0.2
  Length2 = 10
  Profile = -> Sketch111
  ReferenceAxis = -> Sketch111 [N_Axis]
  Type = 0
FEATURE [PartDesign::Pocket] Pocket028  label="Pocket TopPanel TopWindow"
  BaseFeature = -> Pad045
  Direction = (0,0,-1)
  Length = 20
  Length2 = 5
  Midplane = true
  Profile = -> Sketch038
  ReferenceAxis = -> Sketch038 [N_Axis]
  Type = 0
  expr: Length = <<Variables>>.TopThickness * 2
FEATURE [PartDesign::SubtractiveLoft] SubtractiveLoft001  label="SubtractiveLoft TopPanel TopWindow 1"
  BaseFeature = -> Pocket028
  Closed = false
  Profile = -> Sketch038
  Ruled = false
  Sections = -> [Sketch084]
FEATURE [PartDesign::SubtractiveLoft] SubtractiveLoft002  label="SubtractiveLoft TopPanel TopWindow 2"
  BaseFeature = -> SubtractiveLoft001
  Closed = false
  Profile = -> Sketch085
  Ruled = false
  Sections = -> [Sketch086]
FEATURE [PartDesign::Pocket] Pocket029  label="Pocket TopPanel FrontWindow"
  BaseFeature = -> SubtractiveLoft002
  Direction = (0,1,2e-16)
  Length = 14
  Length2 = 5
  Midplane = true
  Profile = -> Sketch082
  ReferenceAxis = -> Sketch082 [N_Axis]
  Type = 0
  expr: Length = <<Variables>>.WallThickness * 2
FEATURE [PartDesign::SubtractiveLoft] SubtractiveLoft  label="SubtractiveLoft TopPanel FrontWindow"
  BaseFeature = -> Pocket029
  Closed = false
  Profile = -> Sketch082
  Ruled = false
  Sections = -> [Sketch083]
FEATURE [PartDesign::Hole] Hole006  label="Hole TopPanel Y Rail"
  BaseFeature = -> SubtractiveLoft
  CustomThreadClearance = 0
  Depth = 10
  DepthType = 0
  Diameter = 2.5
  DrillForDepth = false
  DrillPoint = 1
  DrillPointAngle = 118
  HoleCutCountersinkAngle = 90
  HoleCutCustomValues = false
  HoleCutDepth = 3.4
  HoleCutDiameter = 6
  HoleCutType = 0
  ModelThread = false
  Profile = -> Sketch014
  Tapered = false
  TaperedAngle = 90
  ThreadClass = 0
  ThreadDepth = 10
  ThreadDepthType = 0
  ThreadDirection = 0
  ThreadFit = 0
  ThreadSize = 9
  ThreadType = 1
  Threaded = true
  UseCustomThreadClearance = false
  expr: Depth = <<Variables>>.TopThickness
FEATURE [PartDesign::Pad] Pad029  label="Pad TopPanel Y Rail Hole Support"
  BaseFeature = -> Hole006
  Direction = (0,0,1)
  Length = 0.2
  Length2 = 10
  Profile = -> Binder007
  Type = 0
FEATURE [PartDesign::Hole] Hole014  label="Hole TopPanel RearCap"
  BaseFeature = -> Pad029
  CustomThreadClearance = 0
  Depth = 681.607
  DepthType = 1
  Diameter = 2.5
  DrillForDepth = false
  DrillPoint = 1
  DrillPointAngle = 118
  HoleCutCountersinkAngle = 90
  HoleCutCustomValues = false
  HoleCutDepth = 0
  HoleCutDiameter = 6.1
  HoleCutType = 0
  ModelThread = false
  Profile = -> Sketch041
  Reversed = true
  Tapered = false
  TaperedAngle = 90
  ThreadClass = 0
  ThreadDepth = 681.607
  ThreadDepthType = 0
  ThreadDirection = 0
  ThreadFit = 0
  ThreadSize = 9
  ThreadType = 1
  Threaded = true
  UseCustomThreadClearance = false
FEATURE [PartDesign::Hole] Hole013  label="Hole TopPanel FrontCap"
  BaseFeature = -> Hole014
  CustomThreadClearance = 0
  Depth = 677.746
  DepthType = 1
  Diameter = 2.5
  DrillForDepth = false
  DrillPoint = 1
  DrillPointAngle = 118
  HoleCutCountersinkAngle = 90
  HoleCutCustomValues = false
  HoleCutDepth = 0
  HoleCutDiameter = 6.1
  HoleCutType = 0
  ModelThread = false
  Profile = -> Sketch040
  Tapered = false
  TaperedAngle = 90
  ThreadClass = 0
  ThreadDepth = 677.746
  ThreadDepthType = 0
  ThreadDirection = 0
  ThreadFit = 0
  ThreadSize = 9
  ThreadType = 1
  Threaded = true
  UseCustomThreadClearance = false
FEATURE [PartDesign::Pocket] Pocket030  label="Pocket TopPanel FromtChamfer"
  BaseFeature = -> Hole013
  Direction = (0,-0.707107,0.707107)
  Length = 5
  Length2 = 5
  Midplane = true
  Profile = -> Binder005
  Type = 1
FEATURE [PartDesign::Pocket] Pocket031  label="Pocket TopPanel RearChamfer"
  BaseFeature = -> Pocket030
  Direction = (0,-0.707107,-0.707107)
  Length = 5
  Length2 = 5
  Midplane = true
  Profile = -> Binder006
  Type = 1
FEATURE [PartDesign::Pocket] Pocket043  label="Pocket TopPanel TopChamfer"
  BaseFeature = -> Pocket031
  Direction = (0,1,2e-16)
  Length = 5
  Length2 = 5
  Midplane = true
  Profile = -> Sketch027
  ReferenceAxis = -> Sketch027 [N_Axis]
  Type = 1
FEATURE [Part::FeaturePython] Clone090  label="M3 inserted Nut L6 RearSide Left"  # Draft clone (typed FeaturePython)
  AttacherType = Attacher::AttachEngine3D
  Fuse = false
  Objects = -> [Body015]
  Placement = pos=(113,105,25) rot=(0,-1,0;1.5708rad)
  Scale = (1,1,1)
  expr: .Placement.Base.x = <<Variables>>.GantorySpacing / 2 + <<Variables>>.CavitySpacingX + 3
  expr: .Placement.Base.y = <<Variables>>.GantorySpacing / 2 + 5
FEATURE [Part::FeaturePython] Clone091  label="M3 inserted Nut L6 RearSide Right"  # Draft clone (typed FeaturePython)
  AttacherType = Attacher::AttachEngine3D
  Fuse = false
  Objects = -> [Body015]
  Placement = pos=(-113,105,25) rot=(0,1,0;1.5708rad)
  Scale = (1,1,1)
  expr: .Placement.Base.x = -(<<Variables>>.GantorySpacing / 2 + <<Variables>>.CavitySpacingX + 3)
  expr: .Placement.Base.y = <<Variables>>.GantorySpacing / 2 + 5
FEATURE [App::Part] Part006  label="LeftPanel_1st"
  Group = -> [Body007,LCS_LeftPanelOrigin,Clone087,Clone090,Clone091,Clone086]
  Origin = -> Origin013
FEATURE [Part::FeaturePython] Clone096  label="M3 inserted Nut L6 FrontSide Left"  # Draft clone (typed FeaturePython)
  AttacherType = Attacher::AttachEngine3D
  Fuse = false
  Objects = -> [Body015]
  Placement = pos=(113,-105,25) rot=(0,-1,0;1.5708rad)
  Scale = (1,1,1)
  expr: .Placement.Base.x = <<Variables>>.GantorySpacing / 2 + <<Variables>>.CavitySpacingX + 3
  expr: .Placement.Base.y = -(<<Variables>>.GantorySpacing / 2 + 5)
FEATURE [Part::FeaturePython] Clone097  label="M3 inserted Nut L6 FrontSide Right"  # Draft clone (typed FeaturePython)
  AttacherType = Attacher::AttachEngine3D
  Fuse = false
  Objects = -> [Body015]
  Placement = pos=(-113,-105,25) rot=(0,1,0;1.5708rad)
  Scale = (1,1,1)
  expr: .Placement.Base.x = -(<<Variables>>.GantorySpacing / 2 + <<Variables>>.CavitySpacingX + 3)
  expr: .Placement.Base.y = -(<<Variables>>.GantorySpacing / 2 + 5)
FEATURE [Part::FeaturePython] Clone098  label="M3 inserted Nut MotorSupport Left"  # Draft clone (typed FeaturePython)
  AttacherType = Attacher::AttachEngine3D
  Fuse = false
  Objects = -> [Body013]
  Placement = pos=(70,113,40) rot=(0.57735,-0.57735,0.57735;2.0944rad)
  Scale = (1,1,1)
  expr: .Placement.Base.y = <<Variables>>.GantorySpacing / 2 + <<Variables>>.CavitySpacingY + 3
FEATURE [Part::FeaturePython] Clone099  label="M3 inserted Nut MotorSupport Right"  # Draft clone (typed FeaturePython)
  AttacherType = Attacher::AttachEngine3D
  Fuse = false
  Objects = -> [Body013]
  Placement = pos=(-70,113,40) rot=(0.57735,-0.57735,0.57735;2.0944rad)
  Scale = (1,1,1)
  expr: .Placement.Base.y = <<Variables>>.GantorySpacing / 2 + <<Variables>>.CavitySpacingY + 3
FEATURE [Sketcher::SketchObject] Sketch125
  FullyConstrained = true
  MapMode = 5
  Support = -> [XY_Plane056]
  sketch-geometry (4):
    g0: ArcOfCircle CenterX=0 CenterY=0 CenterZ=0 NormalX=0 NormalY=0 NormalZ=1 AngleXU=0 Radius=3.35 StartAngle=1.5708 EndAngle=4.71239
    g1: LineSegment StartX=0 StartY=3.35 StartZ=0 EndX=6 EndY=3.35 EndZ=0
    g2: LineSegment StartX=6 StartY=3.35 StartZ=0 EndX=6 EndY=-3.35 EndZ=0
    g3: LineSegment StartX=6 StartY=-3.35 StartZ=0 EndX=0 EndY=-3.35 EndZ=0
  constraints (11):
    c: Coincident(g0,g-1)
    c: PointOnObject(g0,g-2)
    c: PointOnObject(g0,g-2)
    c: Horizontal(g1)
    c: Coincident(g2,g1)
    c: Coincident(g3,g2)
    c: Symmetric(g1,g2,g-1)
    c: Coincident(g1,g0)
    c: Coincident(g3,g0)
    c: DistanceX(g1) = 6
    c: Radius(g0) = 3.35
FEATURE [PartDesign::Pad] Pad054
  Direction = (0,0,1)
  Length = 3
  Length2 = 10
  Profile = -> Sketch125
  ReferenceAxis = -> Sketch125 [N_Axis]
  Type = 0
FEATURE [PartDesign::Body] Body030  label="M3 groove L6"
  Group = -> [Sketch125,Pad054]
  Origin = -> Origin056
  Tip = -> Pad054
FEATURE [App::Part] Part012  label="NutHoles"
  Group = -> [Body013,Body014,Body015,Body020,Body030]
  Origin = -> Origin026
FEATURE [Part::FeaturePython] Clone100  label="M3 groove L6 FrontSide Left"  # Draft clone (typed FeaturePython)
  AttacherType = Attacher::AttachEngine3D
  Fuse = false
  Objects = -> [Body030]
  Placement = pos=(110,-105,25) rot=(-0.255249,-0.932862,0.254197;1.63605rad)
  Scale = (1,1,1)
  expr: .Placement.Base.x = <<Variables>>.GantorySpacing / 2 + <<Variables>>.CavitySpacingX
  expr: .Placement.Base.y = -(<<Variables>>.GantorySpacing / 2 + 5)
FEATURE [Part::FeaturePython] Clone101  label="M3 groove L6 FrontSide Right"  # Draft clone (typed FeaturePython)
  AttacherType = Attacher::AttachEngine3D
  Fuse = false
  Objects = -> [Body030]
  Placement = pos=(-110,-105,25) rot=(-0.6947,-0.190194,-0.693699;3.51028rad)
  Scale = (1,1,1)
  expr: .Placement.Base.x = -(<<Variables>>.GantorySpacing / 2 + <<Variables>>.CavitySpacingX)
  expr: .Placement.Base.y = -(<<Variables>>.GantorySpacing / 2 + 5)
FEATURE [PartDesign::Boolean] Boolean004  label="Boolean TopPanel NutHoles"
  BaseFeature = -> Pocket043
  Group = -> [Body021,Clone062,Clone063,Clone064,Clone065,Clone066,Clone067,Clone072,Clone073,Clone055,Clone070,Clone071,Clone060,Clone061,Clone056,Clone057,Clone058,Clone059,Clone098,Clone099,Clone088,Clone089,Clone096,Clone097,Clone100,Clone101]
  Refine = true
  Type = 1
FEATURE [PartDesign::Body] Body004  label="TopPanelPlate"
  Group = -> [Local_CS,Sketch036,Pad011,Pocket042,Pocket044,Pocket005,Mirrored,Hole031,Pocket010,Hole011,Pocket003,Pocket004,Hole009,Binder008,Pad030,Sketch028,Pad009,Pad044,Sketch030,Pocket009,Sketch031,Sketch032,Sketch033,Pocket011,Pocket012,Hole007,Pad031,Hole041,Hole040,Pad045,Pocket028,SubtractiveLoft001,SubtractiveLoft002,Pocket029,SubtractiveLoft,Hole006,Binder007,Pad029,Hole014,Sketch014,Sketch022,+26 more]
  Origin = -> Origin010
  Tip = -> Boolean004
FEATURE [App::Part] Part004  label="TopPanel"
  Group = -> [Body004,LCS_TopPanelOrigin,LCS_TopPanelGantoryOrigin]
  Origin = -> Origin009
FEATURE [App::DocumentObjectGroup] Parts
  Group = -> [Part,Part001,Part002,Part003,Part004,Part006,Part007,Part008,Part009,Part010,Part011,Part012,Part013,Part014,Part005,Part015,Part016,StepperMountLeft,Part017,Part018,Part019,Part020,LeftPullyMount,LeftPanel001]

RESOLVED EXTERNAL PARTS (link-assembly join: the EXTERNAL_REF files above that resolve inside this repo's crawl, each included once):
---- part Drive.FCStd = doc fcstd_4fe1558333d0 ----
FCSTD DOCUMENT  (FreeCAD 0.20R29177 (Git))
Label: Drive
License: All rights reserved
LicenseURL: http://en.wikipedia.org/wiki/All_rights_reserved
objects: PartDesign::Body×7, PartDesign::CoordinateSystem×7, App::Part×4, PartDesign::AdditiveBox×3, PartDesign::Chamfer×3, PartDesign::AdditiveCylinder×3, Sketcher::SketchObject×3, PartDesign::Revolution×2, PartDesign::AdditiveCone×2, PartDesign::Hole×1, PartDesign::SubtractiveCylinder×1
note: 47 computed .brp shape members not serialized (recipe doc carries the construction recipe); baked Part::Feature solids carry a one-line shape summary decoded from their .brp

FEATURE [PartDesign::AdditiveBox] Box
  AttacherType = Attacher::AttachEngine3D
  AttachmentOffset = pos=(-21,-21,0) rot=(0,0,1;0rad)
  Height = 8
  Length = 42
  MapMode = 2
  Placement = pos=(21,-21,0) rot=(0,1,0;3.14159rad)
  Support = -> [XY_Plane001]
  Width = 42
FEATURE [PartDesign::Chamfer] Chamfer
  Angle = 45
  Base = -> Box [Edge1,Edge3,Edge5,Edge7]
  BaseFeature = -> Box
  ChamferType = 0
  FlipDirection = false
  Placement = pos=(21,-21,0) rot=(0,1,0;3.14159rad)
  Size = 4
  Size2 = 1
  SupportTransform = false
  UseAllEdges = false
FEATURE [PartDesign::AdditiveBox] Box001
  AttacherType = Attacher::AttachEngine3D
  AttachmentOffset = pos=(-21,-21,0) rot=(0,0,1;0rad)
  Height = 20
  Length = 42
  MapMode = 2
  Placement = pos=(21,-21,0) rot=(0,1,0;3.14159rad)
  Support = -> [XY_Plane002]
  Width = 42
FEATURE [PartDesign::Chamfer] Chamfer001
  Angle = 45
  Base = -> Box001 [Edge1,Edge3,Edge5,Edge7]
  BaseFeature = -> Box001
  ChamferType = 0
  FlipDirection = false
  Placement = pos=(21,-21,0) rot=(0,1,0;3.14159rad)
  Size = 4
  Size2 = 1
  SupportTransform = false
  UseAllEdges = false
FEATURE [PartDesign::Body] Body001
  Group = -> [Box001,Chamfer001]
  Origin = -> Origin002
  Placement = pos=(0,0,-8) rot=(0,0,1;0rad)
  Tip = -> Chamfer001
FEATURE [PartDesign::AdditiveBox] Box002
  AttacherType = Attacher::AttachEngine3D
  AttachmentOffset = pos=(-21,-21,0) rot=(0,0,1;0rad)
  Height = 9
  Length = 42
  MapMode = 5
  Placement = pos=(21,-21,0) rot=(0,1,0;3.14159rad)
  Support = -> [XY_Plane003]
  Width = 42
FEATURE [PartDesign::Chamfer] Chamfer002
  Angle = 45
  Base = -> Box002 [Edge1,Edge3,Edge5,Edge7]
  BaseFeature = -> Box002
  ChamferType = 0
  FlipDirection = false
  Placement = pos=(21,-21,0) rot=(0,1,0;3.14159rad)
  Size = 4
  Size2 = 1
  SupportTransform = false
  UseAllEdges = false
FEATURE [PartDesign::Body] Body002
  Group = -> [Box002,Chamfer002]
  Origin = -> Origin003
  Placement = pos=(0,0,-28) rot=(0,0,1;0rad)
  Tip = -> Chamfer002
FEATURE [PartDesign::AdditiveCylinder] Cylinder
  Angle = 360
  AttacherType = Attacher::AttachEngine3D
  BaseFeature = -> Chamfer
  FirstAngle = 0
  Height = 2
  MapMode = 2
  Radius = 11
  SecondAngle = 0
  Support = -> [XY_Plane001]
FEATURE [PartDesign::AdditiveCylinder] Cylinder001
  Angle = 360
  AttacherType = Attacher::AttachEngine3D
  AttachmentOffset = pos=(0,0,2) rot=(0,0,1;0rad)
  FirstAngle = 0
  Height = 22
  MapMode = 5
  Placement = pos=(0,0,2) rot=(0,0,1;0rad)
  Radius = 2.5
  SecondAngle = 0
  Support = -> [XY_Plane004]
FEATURE [PartDesign::Body] Body003
  Group = -> [Cylinder001]
  Origin = -> Origin004
  Tip = -> Cylinder001
FEATURE [Sketcher::SketchObject] Sketch
  FullyConstrained = false
  MapMode = 5
  Support = -> [XY_Plane001]
  sketch-geometry (4):
    g0: Circle CenterX=-15.5 CenterY=15.3491 CenterZ=0 NormalX=0 NormalY=0 NormalZ=1 AngleXU=0 Radius=1.5
    g1: Circle CenterX=15.5 CenterY=15.3491 CenterZ=0 NormalX=0 NormalY=0 NormalZ=1 AngleXU=0 Radius=1.5
    g2: Circle CenterX=-15.5 CenterY=-15.3491 CenterZ=0 NormalX=0 NormalY=0 NormalZ=1 AngleXU=0 Radius=1.5
    g3: Circle CenterX=15.5 CenterY=-15.3491 CenterZ=0 NormalX=0 NormalY=0 NormalZ=1 AngleXU=0 Radius=1.5
  constraints (10):
    c: Horizontal(g0,g1)
    c: Vertical(g0,g2)
    c: Horizontal(g2,g3)
    c: Vertical(g1,g3)
    c: Symmetric(g0,g3,g-1)
    c: Equal(g0,g1)
    c: Equal(g0,g2)
    c: Equal(g0,g3)
    c: Diameter(g0) = 3
    c: DistanceX(g0,g1) = 31
FEATURE [PartDesign::Hole] Hole
  BaseFeature = -> Cylinder
  CustomThreadClearance = 0
  Depth = 5
  DepthType = 0
  Diameter = 3.4
  DrillForDepth = false
  DrillPoint = 1
  DrillPointAngle = 118
  HoleCutCountersinkAngle = 90
  HoleCutCustomValues = false
  HoleCutDepth = 0
  HoleCutDiameter = 6.1
  HoleCutType = 0
  ModelThread = false
  Profile = -> Sketch
  Tapered = false
  TaperedAngle = 90
  ThreadClass = 0
  ThreadDepth = 5
  ThreadDepthType = 0
  ThreadDirection = 0
  ThreadFit = 0
  ThreadSize = 9
  ThreadType = 1
  Threaded = false
  UseCustomThreadClearance = false
FEATURE [PartDesign::Body] Body
  Group = -> [Box,Chamfer,Cylinder,Sketch,Hole]
  Origin = -> Origin001
  Tip = -> Hole
FEATURE [Sketcher::SketchObject] Sketch001
  FullyConstrained = true
  MapMode = 5
  Placement = pos=(0,0,0) rot=(1,0,0;1.5708rad)
  Support = -> [XZ_Plane006]
  sketch-geometry (8):
    g0: LineSegment StartX=2.5 StartY=4.25 StartZ=0 EndX=2.5 EndY=-4.25 EndZ=0
    g1: LineSegment StartX=2.5 StartY=-4.25 StartZ=0 EndX=9 EndY=-4.25 EndZ=0
    g2: LineSegment StartX=9 StartY=-4.25 StartZ=0 EndX=9 EndY=-3.25 EndZ=0
    g3: LineSegment StartX=9 StartY=-3.25 StartZ=0 EndX=6.365 EndY=-3.25 EndZ=0
    g4: LineSegment StartX=6.365 StartY=-3.25 StartZ=0 EndX=6.365 EndY=3.25 EndZ=0
    g5: LineSegment StartX=6.365 StartY=3.25 StartZ=0 EndX=9 EndY=3.25 EndZ=0
    g6: LineSegment StartX=9 StartY=3.25 StartZ=0 EndX=9 EndY=4.25 EndZ=0
    g7: LineSegment StartX=9 StartY=4.25 StartZ=0 EndX=2.5 EndY=4.25 EndZ=0
  constraints (21):
    c: Coincident(g0,g1)
    c: Horizontal(g1)
    c: Coincident(g1,g2)
    c: Coincident(g2,g3)
    c: Coincident(g3,g4)
    c: Coincident(g4,g5)
    c: Horizontal(g5)
    c: Coincident(g5,g6)
    c: Coincident(g6,g7)
    c: Coincident(g7,g0)
    c: Horizontal(g7)
    c: Symmetric(g0,g0,g-1)
    c: Symmetric(g4,g3,g-1)
    c: Vertical(g6)
    c: Vertical(g2)
    c: Symmetric(g2,g5,g-1)
    c: DistanceX(g-1,g4) = 6.365
    c: DistanceX(g-1,g0) = 2.5
    c: DistanceY(g6,g6) = 1
    c: DistanceX(g-1,g6) = 9
    c: DistanceY(g3,g4) = 6.5
FEATURE [PartDesign::Revolution] Revolution
  Angle = 360
  Axis = (0,-2e-16,1)
  Base = (0,0,0)
  Placement = pos=(0,0,0) rot=(1,0,0;1.5708rad)
  Profile = -> Sketch001
  ReferenceAxis = -> Sketch001 [V_Axis]
FEATURE [PartDesign::Body] Body004
  Group = -> [Sketch001,Revolution]
  Origin = -> Origin006
  Tip = -> Revolution
FEATURE [PartDesign::CoordinateSystem] LCS_Nema17_Origin
  AttacherType = Attacher::AttachEngine3D
  MapMode = 2
  Support = -> [X_Axis]
FEATURE [App::Part] Part  label="Nema17"
  Group = -> [Body,Body001,Body002,Body003,LCS_Nema17_Origin]
  Origin = -> Origin
FEATURE [PartDesign::CoordinateSystem] LCS_PullyW6T20_Origin  label="LCS_IdlerW6T20_Origin"
  AttacherType = Attacher::AttachEngine3D
  MapMode = 2
  Support = -> [X_Axis005]
FEATURE [PartDesign::CoordinateSystem] LCS_PullyW6T20_Left  label="LCS_IdlerW6T20_Left"
  AttacherType = Attacher::AttachEngine3D
  AttachmentOffset = pos=(6.365,0,0) rot=(0,0,1;0rad)
  MapMode = 2
  Placement = pos=(6.365,0,0) rot=(0,0,1;0rad)
  Support = -> [LCS_PullyW6T20_Origin]
FEATURE [PartDesign::CoordinateSystem] LCS_PullyW6T20_Right  label="LCS_IdlerW6T20_Right"
  AttacherType = Attacher::AttachEngine3D
  AttachmentOffset = pos=(-6.365,0,0) rot=(0,0,1;0rad)
  MapMode = 2
  Placement = pos=(-6.365,0,0) rot=(0,0,1;0rad)
  Support = -> [LCS_PullyW6T20_Origin]
FEATURE [PartDesign::CoordinateSystem] LCS_PullyW6T20_Front  label="LCS_IdlerW6T20_Front"
  AttacherType = Attacher::AttachEngine3D
  AttachmentOffset = pos=(0,-6.365,0) rot=(0,0,1;0rad)
  MapMode = 2
  Placement = pos=(0,-6.365,0) rot=(0,0,1;0rad)
  Support = -> [LCS_PullyW6T20_Origin]
FEATURE [PartDesign::CoordinateSystem] LCS_PullyW6T20_Rear
  AttacherType = Attacher::AttachEngine3D
  AttachmentOffset = pos=(0,6.365,0) rot=(0,0,1;0rad)
  MapMode = 2
  Placement = pos=(0,6.365,0) rot=(0,0,1;0rad)
  Support = -> [LCS_PullyW6T20_Origin]
FEATURE [App::Part] Part001  label="IdlerW6T20"
  Group = -> [Body004,LCS_PullyW6T20_Origin,LCS_PullyW6T20_Left,LCS_PullyW6T20_Right,LCS_PullyW6T20_Front,LCS_PullyW6T20_Rear]
  Origin = -> Origin005
FEATURE [Sketcher::SketchObject] Sketch002
  FullyConstrained = true
  MapMode = 5
  Placement = pos=(0,0,0) rot=(1,0,0;1.5708rad)
  Support = -> [XZ_Plane008]
  sketch-geometry (8):
    g0: LineSegment StartX=2.5 StartY=4.9 StartZ=0 EndX=2.5 EndY=-11.1 EndZ=0
    g1: LineSegment StartX=2.5 StartY=-11.1 StartZ=0 EndX=8 EndY=-11.1 EndZ=0
    g2: LineSegment StartX=8 StartY=-11.1 StartZ=0 EndX=8 EndY=-3.6 EndZ=0
    g3: LineSegment StartX=8 StartY=-3.6 StartZ=0 EndX=6.365 EndY=-3.6 EndZ=0
    g4: LineSegment StartX=6.365 StartY=-3.6 StartZ=0 EndX=6.365 EndY=3.6 EndZ=0
    g5: LineSegment StartX=6.365 StartY=3.6 StartZ=0 EndX=8 EndY=3.6 EndZ=0
    g6: LineSegment StartX=8 StartY=3.6 StartZ=0 EndX=8 EndY=4.9 EndZ=0
    g7: LineSegment StartX=8 StartY=4.9 StartZ=0 EndX=2.5 EndY=4.9 EndZ=0
  constraints (23):
    c: Vertical(g0)
    c: Coincident(g0,g1)
    c: Coincident(g1,g2)
    c: Vertical(g2)
    c: Coincident(g2,g3)
    c: Coincident(g3,g4)
    c: Coincident(g4,g5)
    c: Horizontal(g5)
    c: Coincident(g5,g6)
    c: Vertical(g6)
    c: Coincident(g6,g7)
    c: Horizontal(g7)
    c: Coincident(g7,g0)
    c: Horizontal(g1)
    c: Horizontal(g3)
    c: DistanceX(g-1,g0) = 2.5
    c: DistanceY(g6,g6) = 1.3
    c: DistanceY(g4,g4) = 7.2
    c: DistanceY(g2,g2) = 7.5
    c: Symmetric(g4,g3,g-1)
    c: DistanceX(g-1,g4) = 6.365
    c: DistanceX(g-1,g1) = 8
    c: DistanceX(g-1,g6) = 8
FEATURE [PartDesign::Revolution] Revolution001
  Angle = 360
  Axis = (0,-2e-16,1)
  Base = (0,0,0)
  Placement = pos=(0,0,0) rot=(1,0,0;1.5708rad)
  Profile = -> Sketch002
  ReferenceAxis = -> Sketch002 [V_Axis]
FEATURE [PartDesign::Body] Body005
  Group = -> [Sketch002,Revolution001]
  Origin = -> Origin008
  Tip = -> Revolution001
FEATURE [PartDesign::CoordinateSystem] LCS_DriveW6T20
  AttacherType = Attacher::AttachEngine3D
  MapMode = 2
  Support = -> [X_Axis007]
FEATURE [App::Part] Part002  label="DriveW6T20"
  Group = -> [Body005,LCS_DriveW6T20]
  Origin = -> Origin007
FEATURE [PartDesign::AdditiveCylinder] Cylinder002
  Angle = 360
  AttacherType = Attacher::AttachEngine3D
  FirstAngle = 0
  Height = 8.5
  MapMode = 5
  Radius = 5.99
  SecondAngle = 0
  Support = -> [XY_Plane010]
FEATURE [PartDesign::AdditiveCone] Cone
  Angle = 360
  AttacherType = Attacher::AttachEngine3D
  BaseFeature = -> Cylinder002
  Height = 2
  MapMode = 5
  Radius1 = 7.1
  Radius2 = 5.1
  Support = -> [XY_Plane010]
FEATURE [PartDesign::AdditiveCone] Cone001
  Angle = 360
  AttacherType = Attacher::AttachEngine3D
  AttachmentOffset = pos=(0,0,-8.5) rot=(0,0,1;0rad)
  BaseFeature = -> Cone
  Height = 2
  MapMode = 5
  Placement = pos=(0,0,8.5) rot=(0,1,0;3.14159rad)
  Radius1 = 7.1
  Radius2 = 5.1
  Support = -> [XY_Plane010]
FEATURE [PartDesign::SubtractiveCylinder] Cylinder003
  Angle = 360
  AttacherType = Attacher::AttachEngine3D
  BaseFeature = -> Cone001
  FirstAngle = 0
  Height = 13
  MapMode = 5
  Radius = 4
  SecondAngle = 0
  Support = -> [XY_Plane010]
FEATURE [PartDesign::Body] Body006
  Group = -> [Cylinder002,Cone,Cone001,Cylinder003]
  Origin = -> Origin010
  Tip = -> Cylinder003
FEATURE [App::Part] Part003  label="Pully2GT20TSmooth"
  Group = -> [Body006]
  Origin = -> Origin009
---- part MGN9.FCStd = doc fcstd_087b5e8fa0dc ----
FCSTD DOCUMENT  (FreeCAD 0.20R29177 (Git))
Label: MGN9
License: All rights reserved
LicenseURL: http://en.wikipedia.org/wiki/All_rights_reserved
objects: PartDesign::Chamfer×7, PartDesign::Pad×6, PartDesign::Body×6, Sketcher::SketchObject×5, PartDesign::ShapeBinder×5, PartDesign::CoordinateSystem×4, App::DocumentObjectGroup×3, App::Part×3, PartDesign::Hole×2, App::Link×2, App::FeaturePython×1
note: 50 computed .brp shape members not serialized (recipe doc carries the construction recipe); baked Part::Feature solids carry a one-line shape summary decoded from their .brp

FEATURE [Sketcher::SketchObject] Sketch
  FullyConstrained = true
  MapMode = 5
  Placement = pos=(0,0,0) rot=(1,0,0;1.5708rad)
  Support = -> [XZ_Plane001]
  sketch-geometry (8):
    g0: LineSegment StartX=-4.5 StartY=6.5 StartZ=0 EndX=4.5 EndY=6.5 EndZ=0
    g1: LineSegment StartX=4.5 StartY=6.5 StartZ=0 EndX=4.5 EndY=5.5 EndZ=0
    g2: LineSegment StartX=4.5 StartY=0 StartZ=0 EndX=-4.5 EndY=0 EndZ=0
    g3: LineSegment StartX=-4.5 StartY=0 StartZ=0 EndX=-4.5 EndY=3.5 EndZ=0
    g4: ArcOfCircle CenterX=-4.5 CenterY=4.5 CenterZ=0 NormalX=0 NormalY=0 NormalZ=1 AngleXU=0 Radius=1 StartAngle=4.71239 EndAngle=7.85398
    g5: LineSegment StartX=-4.5 StartY=5.5 StartZ=0 EndX=-4.5 EndY=6.5 EndZ=0
    g6: ArcOfCircle CenterX=4.5 CenterY=4.5 CenterZ=0 NormalX=0 NormalY=0 NormalZ=1 AngleXU=0 Radius=1 StartAngle=1.5708 EndAngle=4.71239
    g7: LineSegment StartX=4.5 StartY=3.5 StartZ=0 EndX=4.5 EndY=0 EndZ=0
  constraints (22):
    c: Coincident(g0,g1)
    c: Coincident(g7,g2)
    c: Coincident(g2,g3)
    c: Coincident(g5,g0)
    c: Symmetric(g2,g7,g-2)
    c: Symmetric(g0,g0,g-2)
    c: Vertical(g3)
    c: DistanceX(g2,g2) = 9
    c: DistanceY(g3,g5) = 6.5
    c: PointOnObject(g2,g-1)
    c: PointOnObject(g4,g3)
    c: DistanceY(g-1,g4) = 4.5
    c: Radius(g4) = 1
    c: Coincident(g3,g4)
    c: Coincident(g5,g4)
    c: Vertical(g5)
    c: Vertical(g4,g3)
    c: PointOnObject(g6,g1)
    c: Coincident(g1,g6)
    c: Coincident(g7,g6)
    c: Symmetric(g4,g6,g-2)
    c: Symmetric(g3,g6,g-2)
FEATURE [Sketcher::SketchObject] Sketch001  label="UnitSketch"
  FullyConstrained = true
  MapMode = 5
  Placement = pos=(0,0,0) rot=(1,0,0;1.5708rad)
  Support = -> [XZ_Plane002]
  sketch-geometry (12):
    g0: LineSegment StartX=-10 StartY=8 StartZ=0 EndX=-4 EndY=8 EndZ=0
    g1: LineSegment StartX=10 StartY=8 StartZ=0 EndX=10 EndY=0 EndZ=0
    g2: LineSegment StartX=10 StartY=0 StartZ=0 EndX=4.5 EndY=0 EndZ=0
    g3: LineSegment StartX=-10 StartY=0 StartZ=0 EndX=-10 EndY=8 EndZ=0
    g4: LineSegment StartX=-4.5 StartY=4.5 StartZ=0 EndX=4.5 EndY=4.5 EndZ=0
    g5: LineSegment StartX=4.5 StartY=4.5 StartZ=0 EndX=4.5 EndY=0 EndZ=0
    g6: LineSegment StartX=-4.5 StartY=0 StartZ=0 EndX=-4.5 EndY=4.5 EndZ=0
    g7: LineSegment StartX=-4.5 StartY=0 StartZ=0 EndX=-10 EndY=0 EndZ=0
    g8: LineSegment StartX=4 StartY=8 StartZ=0 EndX=4 EndY=7.55 EndZ=0
    g9: LineSegment StartX=4 StartY=7.55 StartZ=0 EndX=-4 EndY=7.55 EndZ=0
    g10: LineSegment StartX=-4 StartY=7.55 StartZ=0 EndX=-4 EndY=8 EndZ=0
    g11: LineSegment StartX=4 StartY=8 StartZ=0 EndX=10 EndY=8 EndZ=0
  constraints (31):
    c: Coincident(g11,g1)
    c: Coincident(g1,g2)
    c: Coincident(g7,g3)
    c: Coincident(g3,g0)
    c: Symmetric(g7,g1,g-2)
    c: Symmetric(g0,g11,g-2)
    c: PointOnObject(g7,g-1)
    c: DistanceX(g7,g2) = 20
    c: DistanceY(g3,g3) = 8
    c: Vertical(g3)
    c: Coincident(g4,g5)
    c: Coincident(g6,g4)
    c: Horizontal(g4)
    c: Vertical(g5)
    c: Vertical(g6)
    c: Coincident(g2,g5)
    c: DistanceX(g6,g5) = 9
    c: DistanceY(g6,g6) = 4.5
    c: Symmetric(g6,g2,g-2)
    c: Coincident(g8,g9)
    c: Coincident(g9,g10)
    c: Coincident(g10,g0)
    c: Coincident(g8,g11)
    c: Symmetric(g0,g8,g-2)
    c: DistanceX(g9,g9) = 8
    c: Horizontal(g0)
    c: DistanceY(g10,g10) = 0.45
    c: Symmetric(g9,g8,g-2)
    c: Vertical(g10)
    c: Coincident(g7,g6)
    c: PointOnObject(g6,g-1)
FEATURE [Sketcher::SketchObject] Sketch002  label="CoverSketch"
  FullyConstrained = true
  MapMode = 5
  Placement = pos=(0,0,0) rot=(1,0,0;1.5708rad)
  Support = -> [XZ_Plane002]
  sketch-geometry (12):
    g0: LineSegment StartX=9.85 StartY=7.65 StartZ=0 EndX=9.85 EndY=0 EndZ=0
    g1: LineSegment StartX=9.85 StartY=0 StartZ=0 EndX=4.5 EndY=0 EndZ=0
    g2: LineSegment StartX=-9.85 StartY=0 StartZ=0 EndX=-9.85 EndY=7.65 EndZ=0
    g3: LineSegment StartX=-4.5 StartY=4.5 StartZ=0 EndX=4.5 EndY=4.5 EndZ=0
    g4: LineSegment StartX=4.5 StartY=4.5 StartZ=0 EndX=4.5 EndY=3.5 EndZ=0
    g5: LineSegment StartX=-4.5 StartY=0 StartZ=0 EndX=-4.5 EndY=1.5 EndZ=0
    g6: LineSegment StartX=-9.85 StartY=7.65 StartZ=0 EndX=9.85 EndY=7.65 EndZ=0
    g7: LineSegment StartX=-4.5 StartY=0 StartZ=0 EndX=-9.85 EndY=0 EndZ=0
    g8: ArcOfCircle CenterX=-4.5 CenterY=2.5 CenterZ=0 NormalX=0 NormalY=0 NormalZ=1 AngleXU=0 Radius=1 StartAngle=4.71239 EndAngle=7.85398
    g9: ArcOfCircle CenterX=4.5 CenterY=2.5 CenterZ=0 NormalX=0 NormalY=0 NormalZ=1 AngleXU=0 Radius=1 StartAngle=1.5708 EndAngle=4.71239
    g10: LineSegment StartX=-4.5 StartY=3.5 StartZ=0 EndX=-4.5 EndY=4.5 EndZ=0
    g11: LineSegment StartX=4.5 StartY=1.5 StartZ=0 EndX=4.5 EndY=0 EndZ=0
  constraints (32):
    c: Coincident(g6,g0)
    c: Coincident(g0,g1)
    c: Coincident(g7,g2)
    c: Vertical(g2)
    c: Coincident(g3,g4)
    c: Coincident(g10,g3)
    c: Vertical(g5)
    c: Coincident(g1,g11)
    c: Coincident(g5,g7)
    c: Symmetric(g2,g0,g-2)
    c: Symmetric(g5,g1,g-2)
    c: Symmetric(g3,g3,g-2)
    c: PointOnObject(g5,g-1)
    c: PointOnObject(g2,g-1)
    c: DistanceX(g3,g3) = 9
    c: DistanceY(g5,g10) = 4.5
    c: DistanceY(g2,g2) = 7.65
    c: Coincident(g6,g2)
    c: DistanceX(g6,g6) = 19.7
    c: Symmetric(g2,g0,g-2)
    c: PointOnObject(g8,g5)
    c: PointOnObject(g9,g4)
    c: Coincident(g5,g8)
    c: Coincident(g10,g8)
    c: Coincident(g4,g9)
    c: Coincident(g11,g9)
    c: Vertical(g8,g5)
    c: Vertical(g10)
    c: Symmetric(g8,g4,g-2)
    c: Symmetric(g9,g5,g-2)
    c: DistanceY(g5,g8) = 2.5
    c: Radius(g8) = 1
FEATURE [PartDesign::CoordinateSystem] LCS_Origin
  AttacherType = Attacher::AttachEngine3D
  MapMode = 2
  Support = -> [X_Axis008]
FEATURE [App::FeaturePython] Variables  # WARN: FeaturePython — macro-defined, semantics opaque (R4)
  Length = 100
  Position = 0
  Type = App::PropertyContainer
FEATURE [App::DocumentObjectGroup] Constraints
FEATURE [App::DocumentObjectGroup] Configurations
FEATURE [PartDesign::Pad] Pad
  Direction = (0,-1,-2e-16)
  Length = 100
  Length2 = 10
  Midplane = true
  Placement = pos=(0,0,0) rot=(1,0,0;1.5708rad)
  Profile = -> Sketch
  ReferenceAxis = -> Sketch [N_Axis]
  Type = 0
  expr: Length = <<Variables>>.Length
FEATURE [PartDesign::ShapeBinder] ShapeBinder
  Placement = pos=(0,0,0) rot=(1,0,0;1.5708rad)
  Support = -> [Sketch001]
  TraceSupport = false
FEATURE [PartDesign::Pad] Pad001
  Direction = (0,1,2e-16)
  Length = 18.9
  Length2 = 10
  Midplane = true
  Placement = pos=(0,0,0) rot=(1,0,0;1.5708rad)
  Profile = -> ShapeBinder
  Type = 0
FEATURE [PartDesign::ShapeBinder] ShapeBinder001
  Placement = pos=(0,0,0) rot=(1,0,0;1.5708rad)
  Support = -> [Sketch002]
  TraceSupport = false
FEATURE [PartDesign::Pad] Pad002
  Direction = (0,1,2e-16)
  Length = 4
  Length2 = 10
  Placement = pos=(0,0,0) rot=(1,0,0;1.5708rad)
  Profile = -> ShapeBinder001
  Type = 0
FEATURE [PartDesign::ShapeBinder] ShapeBinder002
  Placement = pos=(0,0,0) rot=(1,0,0;1.5708rad)
  Support = -> [Sketch002]
  TraceSupport = false
FEATURE [PartDesign::Pad] Pad003
  Direction = (0,1,2e-16)
  Length = 4
  Length2 = 10
  Placement = pos=(0,0,0) rot=(1,0,0;1.5708rad)
  Profile = -> ShapeBinder002
  Reversed = true
  Type = 0
FEATURE [PartDesign::Chamfer] Chamfer
  Angle = 45
  Base = -> Pad003 [Edge5,Edge8,Edge11,Edge2]
  BaseFeature = -> Pad003
  ChamferType = 0
  FlipDirection = false
  Placement = pos=(0,0,0) rot=(1,0,0;1.5708rad)
  Size = 1
  Size2 = 1
  SupportTransform = false
  UseAllEdges = false
FEATURE [PartDesign::Chamfer] Chamfer001
  Angle = 45
  Base = -> Pad001 [Edge5,Edge20,Edge23,Edge2]
  BaseFeature = -> Pad001
  ChamferType = 0
  FlipDirection = false
  Placement = pos=(0,0,0) rot=(1,0,0;1.5708rad)
  Size = 0.5
  Size2 = 1
  SupportTransform = false
  UseAllEdges = false
FEATURE [PartDesign::Chamfer] Chamfer002
  Angle = 45
  Base = -> Pad002 [Edge8,Edge5,Edge2,Edge11]
  BaseFeature = -> Pad002
  ChamferType = 0
  FlipDirection = false
  Placement = pos=(0,0,0) rot=(1,0,0;1.5708rad)
  Size = 1
  Size2 = 1
  SupportTransform = false
  UseAllEdges = false
FEATURE [PartDesign::Body] Body002  label="Returner001"
  Group = -> [ShapeBinder001,Pad002,Chamfer002]
  Origin = -> Origin004
  Placement = pos=(0,9.4,0) rot=(0,0,1;0rad)
  Tip = -> Chamfer002
FEATURE [PartDesign::Chamfer] Chamfer003
  Angle = 45
  Base = -> Pad [Edge2,Edge11,Edge14,Edge1]
  BaseFeature = -> Pad
  ChamferType = 0
  FlipDirection = false
  Placement = pos=(0,0,0) rot=(1,0,0;1.5708rad)
  Size = 0.35
  Size2 = 1
  SupportTransform = false
  UseAllEdges = false
FEATURE [PartDesign::ShapeBinder] ShapeBinder003
  Placement = pos=(0,0,0) rot=(1,0,0;1.5708rad)
  Support = -> [Sketch002]
  TraceSupport = false
FEATURE [PartDesign::Pad] Pad004
  Direction = (0,1,2e-16)
  Length = 1
  Length2 = 10
  Placement = pos=(0,0,0) rot=(1,0,0;1.5708rad)
  Profile = -> ShapeBinder003
  Type = 0
FEATURE [PartDesign::Chamfer] Chamfer004
  Angle = 45
  Base = -> Pad004 [Edge8,Edge5,Edge11,Edge2]
  BaseFeature = -> Pad004
  ChamferType = 0
  FlipDirection = false
  Placement = pos=(0,0,0) rot=(1,0,0;1.5708rad)
  Size = 1
  Size2 = 1
  SupportTransform = false
  UseAllEdges = false
FEATURE [PartDesign::Body] Body004  label="wiper001"
  Group = -> [ShapeBinder003,Pad004,Chamfer004]
  Origin = -> Origin006
  Placement = pos=(0,13.4,0) rot=(0,0,1;0rad)
  Tip = -> Chamfer004
FEATURE [PartDesign::ShapeBinder] ShapeBinder004
  Placement = pos=(0,0,0) rot=(1,0,0;1.5708rad)
  Support = -> [Sketch002]
  TraceSupport = false
FEATURE [PartDesign::Pad] Pad005
  Direction = (0,1,2e-16)
  Length = 1
  Length2 = 10
  Placement = pos=(0,0,0) rot=(1,0,0;1.5708rad)
  Profile = -> ShapeBinder004
  Reversed = true
  Type = 0
FEATURE [PartDesign::Chamfer] Chamfer005
  Angle = 45
  Base = -> Pad003 [Edge8,Edge11,Edge5,Edge2]
  BaseFeature = -> Pad003
  ChamferType = 0
  FlipDirection = false
  Placement = pos=(0,0,0) rot=(1,0,0;1.5708rad)
  Size = 1
  Size2 = 1
  SupportTransform = false
  UseAllEdges = false
FEATURE [PartDesign::Body] Body003  label="Returner002"
  Group = -> [ShapeBinder002,Pad003,Chamfer,Chamfer005]
  Origin = -> Origin005
  Placement = pos=(0,-9.4,0) rot=(0,0,1;0rad)
  Tip = -> Chamfer005
FEATURE [PartDesign::Chamfer] Chamfer006
  Angle = 45
  Base = -> Pad005 [Edge5,Edge2,Edge8,Edge11]
  BaseFeature = -> Pad005
  ChamferType = 0
  FlipDirection = false
  Placement = pos=(0,0,0) rot=(1,0,0;1.5708rad)
  Size = 1
  Size2 = 1
  SupportTransform = false
  UseAllEdges = false
FEATURE [PartDesign::Body] Body005  label="wiper002"
  Group = -> [ShapeBinder004,Pad005,Chamfer006]
  Origin = -> Origin007
  Placement = pos=(0,-13.4,0) rot=(0,0,1;0rad)
  Tip = -> Chamfer006
FEATURE [Sketcher::SketchObject] Sketch003
  FullyConstrained = true
  MapMode = 5
  Placement = pos=(0,1.8e-15,8) rot=(0,0,1;3.14159rad)
  Support = -> [Chamfer001]
  sketch-geometry (4):
    g0: Circle CenterX=-7.5 CenterY=5 CenterZ=0 NormalX=0 NormalY=0 NormalZ=1 AngleXU=0 Radius=1.5
    g1: Circle CenterX=7.5 CenterY=5 CenterZ=0 NormalX=0 NormalY=0 NormalZ=1 AngleXU=0 Radius=1.5
    g2: Circle CenterX=-7.5 CenterY=-5 CenterZ=0 NormalX=0 NormalY=0 NormalZ=1 AngleXU=0 Radius=1.5
    g3: Circle CenterX=7.5 CenterY=-5 CenterZ=0 NormalX=0 NormalY=0 NormalZ=1 AngleXU=0 Radius=1.5
  constraints (9):
    c: Symmetric(g0,g2,g-1)
    c: Symmetric(g0,g1,g-2)
    c: Symmetric(g2,g3,g-2)
    c: DistanceY(g2,g0) = 10
    c: DistanceX(g0,g1) = 15
    c: Equal(g0,g1)
    c: Equal(g0,g2)
    c: Equal(g0,g3)
    c: Diameter(g0) = 3
FEATURE [PartDesign::Hole] Hole
  BaseFeature = -> Chamfer001
  CustomThreadClearance = 0
  Depth = 4.4
  DepthType = 0
  Diameter = 2.5
  DrillForDepth = false
  DrillPoint = 1
  DrillPointAngle = 118
  HoleCutCountersinkAngle = 90
  HoleCutCustomValues = false
  HoleCutDepth = 0
  HoleCutDiameter = 6.1
  HoleCutType = 0
  ModelThread = false
  Placement = pos=(0,0,0) rot=(1,0,0;1.5708rad)
  Profile = -> Sketch003
  Tapered = false
  TaperedAngle = 90
  ThreadClass = 0
  ThreadDepth = 4.4
  ThreadDepthType = 0
  ThreadDirection = 0
  ThreadFit = 0
  ThreadSize = 9
  ThreadType = 1
  Threaded = true
  UseCustomThreadClearance = false
FEATURE [PartDesign::Body] Body001  label="UnitBody"
  Group = -> [ShapeBinder,Pad001,Chamfer001,Sketch003,Hole]
  Origin = -> Origin003
  Tip = -> Hole
FEATURE [PartDesign::CoordinateSystem] LCS_RailPartOrigin
  AttacherType = Attacher::AttachEngine3D
  MapMode = 3
  Placement = pos=(0,0,0) rot=(0,0,-1;1.5708rad)
  Support = -> [Y_Axis]
FEATURE [PartDesign::CoordinateSystem] LCS_RailPartTop
  AttacherType = Attacher::AttachEngine3D
  AttachmentOffset = pos=(0,0,6.5) rot=(0,0,1;0rad)
  MapMode = 3
  Placement = pos=(-7e-16,7e-16,6.5) rot=(0,0,-1;1.5708rad)
  Support = -> [Y_Axis]
FEATURE [PartDesign::CoordinateSystem] LCS_UnitPartOrigin
  AttacherType = Attacher::AttachEngine3D
  AttachmentOffset = pos=(0,0,4.5) rot=(0,0,1;0rad)
  MapMode = 3
  Placement = pos=(-5e-16,5e-16,4.5) rot=(0,0,-1;1.5708rad)
  Support = -> [Y_Axis002]
FEATURE [App::Part] Part001  label="Unit"
  Group = -> [Sketch001,Sketch002,Body001,Body002,Body003,Body004,Body005,LCS_UnitPartOrigin]
  Origin = -> Origin002
FEATURE [App::Link] Rail  label="Rail001"
  AssemblyType = Part::Link
  AttachedBy = #LCS_RailPartOrigin
  AttachedTo = Parent Assembly#LCS_Origin
  LinkPlacement = pos=(0,0,0) rot=(0,0,1;1.5708rad)
  LinkedObject = -> Part
  Placement = pos=(0,0,0) rot=(0,0,1;1.5708rad)
  SolverId = Asm4EE
  expr: Placement = LCS_Origin.Placement * AttachmentOffset * LCS_RailPartOrigin.Placement ^ -1
FEATURE [App::Link] Unit  label="Unit001"
  AssemblyType = Part::Link
  AttachedBy = #LCS_UnitPartOrigin
  AttachedTo = Rail#LCS_RailPartTop
  LinkPlacement = pos=(0,0,2) rot=(0,0,1;1.5708rad)
  LinkedObject = -> Part001
  Placement = pos=(0,0,2) rot=(0,0,1;1.5708rad)
  SolverId = Asm4EE
  expr: .AttachmentOffset.Base.x = <<Variables>>.Position
  expr: Placement = Rail.Placement * LCS_RailPartTop.Placement * AttachmentOffset * LCS_UnitPartOrigin.Placement ^ -1
FEATURE [App::Part] Assembly
  AssemblyType = Part::Link
  Group = -> [LCS_Origin,Variables,Constraints,Configurations,Rail,Unit]
  Origin = -> Origin008
  Type = Assembly
FEATURE [Sketcher::SketchObject] Sketch004
  AttachmentOffset = pos=(0,0,-6.5) rot=(0,0,1;0rad)
  FullyConstrained = true
  MapMode = 3
  Placement = pos=(-7e-16,7e-16,6.5) rot=(0.707107,0.707107,0;3.14159rad)
  Support = -> [Y_Axis001]
  sketch-geometry (19):
    g0: Circle CenterX=0 CenterY=0 CenterZ=0 NormalX=0 NormalY=0 NormalZ=1 AngleXU=0 Radius=1.5
    g1: Circle CenterX=-20 CenterY=0 CenterZ=0 NormalX=0 NormalY=0 NormalZ=1 AngleXU=0 Radius=1.5
    g2: Circle CenterX=-40 CenterY=0 CenterZ=0 NormalX=0 NormalY=0 NormalZ=1 AngleXU=0 Radius=1.5
    g3: Circle CenterX=-60 CenterY=0 CenterZ=0 NormalX=0 NormalY=0 NormalZ=1 AngleXU=0 Radius=1.5
    g4: Circle CenterX=-80 CenterY=0 CenterZ=0 NormalX=0 NormalY=0 NormalZ=1 AngleXU=0 Radius=1.5
    g5: Circle CenterX=-100 CenterY=0 CenterZ=0 NormalX=0 NormalY=0 NormalZ=1 AngleXU=0 Radius=1.5
    g6: Circle CenterX=-120 CenterY=0 CenterZ=0 NormalX=0 NormalY=0 NormalZ=1 AngleXU=0 Radius=1.5
    g7: Circle CenterX=-140 CenterY=0 CenterZ=0 NormalX=0 NormalY=0 NormalZ=1 AngleXU=0 Radius=1.5
    g8: Circle CenterX=-160 CenterY=0 CenterZ=0 NormalX=0 NormalY=0 NormalZ=1 AngleXU=0 Radius=1.5
    g9: Circle CenterX=-180 CenterY=0 CenterZ=0 NormalX=0 NormalY=0 NormalZ=1 AngleXU=0 Radius=1.5
    g10: Circle CenterX=20 CenterY=0 CenterZ=0 NormalX=0 NormalY=0 NormalZ=1 AngleXU=0 Radius=1.5
    g11: Circle CenterX=40 CenterY=0 CenterZ=0 NormalX=0 NormalY=0 NormalZ=1 AngleXU=0 Radius=1.5
    g12: Circle CenterX=60 CenterY=0 CenterZ=0 NormalX=0 NormalY=0 NormalZ=1 AngleXU=0 Radius=1.5
    g13: Circle CenterX=80 CenterY=0 CenterZ=0 NormalX=0 NormalY=0 NormalZ=1 AngleXU=0 Radius=1.5
    g14: Circle CenterX=100 CenterY=0 CenterZ=0 NormalX=0 NormalY=0 NormalZ=1 AngleXU=0 Radius=1.5
    g15: Circle CenterX=120 CenterY=0 CenterZ=0 NormalX=0 NormalY=0 NormalZ=1 AngleXU=0 Radius=1.5
    g16: Circle CenterX=140 CenterY=0 CenterZ=0 NormalX=0 NormalY=0 NormalZ=1 AngleXU=0 Radius=1.5
    g17: Circle CenterX=160 CenterY=0 CenterZ=0 NormalX=0 NormalY=0 NormalZ=1 AngleXU=0 Radius=1.5
    g18: Circle CenterX=180 CenterY=0 CenterZ=0 NormalX=0 NormalY=0 NormalZ=1 AngleXU=0 Radius=1.5
  constraints (30):
    c: PointOnObject(g1,g-1)
    c: PointOnObject(g2,g-1)
    c: PointOnObject(g3,g-1)
    c: PointOnObject(g4,g-1)
    c: PointOnObject(g5,g-1)
    c: PointOnObject(g6,g-1)
    c: PointOnObject(g7,g-1)
    c: PointOnObject(g8,g-1)
    c: PointOnObject(g9,g-1)
    c: Equal(g0, g1-g18) x18
    c: Diameter(g0) = 3
    c: Symmetric(g9,g18,g-2)
    c: Symmetric(g8,g17,g-2)
    c: DistanceX(g9,g8) = 20
    c: Symmetric(g7,g16,g-2)
    c: DistanceX(g8,g7) = 20
    c: Symmetric(g6,g15,g-2)
    c: DistanceX(g7,g6) = 20
    c: Symmetric(g14,g5,g-2)
    c: DistanceX(g6,g5) = 20
    c: Symmetric(g4,g13,g-2)
    c: DistanceX(g5,g4) = 20
    c: Symmetric(g12,g3,g-2)
    c: DistanceX(g4,g3) = 20
    c: Symmetric(g11,g2,g-2)
    c: DistanceX(g3,g2) = 20
    c: Symmetric(g10,g1,g-2)
    c: DistanceX(g2,g1) = 20
    c: DistanceX(g1,g0) = 20
    c: Coincident(g0,g-1)
FEATURE [PartDesign::Hole] Hole001
  BaseFeature = -> Chamfer003
  CustomThreadClearance = 0
  Depth = 733.603
  DepthType = 1
  Diameter = 3.7
  DrillForDepth = false
  DrillPoint = 1
  DrillPointAngle = 118
  HoleCutCountersinkAngle = 90
  HoleCutCustomValues = false
  HoleCutDepth = 3.06
  HoleCutDiameter = 6.1
  HoleCutType = 1
  ModelThread = false
  Placement = pos=(0,0,0) rot=(1,0,0;1.5708rad)
  Profile = -> Sketch004
  Reversed = true
  Tapered = false
  TaperedAngle = 90
  ThreadClass = 0
  ThreadDepth = 733.603
  ThreadDepthType = 0
  ThreadDirection = 0
  ThreadFit = 0
  ThreadSize = 0
  ThreadType = 0
  Threaded = false
  UseCustomThreadClearance = false
FEATURE [PartDesign::Body] Body  label="RailBody"
  Group = -> [Sketch,Pad,Sketch004,Chamfer003,Hole001]
  Origin = -> Origin001
  Tip = -> Hole001
FEATURE [App::Part] Part  label="Rail"
  Group = -> [Body,LCS_RailPartOrigin,LCS_RailPartTop]
  Origin = -> Origin
FEATURE [App::DocumentObjectGroup] Parts
  Group = -> [Part,Part001]
---- part miniXY-ZDrive.FCStd = doc fcstd_499f4646abeb ----
FCSTD DOCUMENT  (FreeCAD 0.20R29177 (Git))
Label: miniXY-ZDrive
License: All rights reserved
LicenseURL: http://en.wikipedia.org/wiki/All_rights_reserved
objects: App::Part×4, App::Link×4, App::DocumentObjectGroup×3, Sketcher::SketchObject×3, PartDesign::Revolution×3, PartDesign::Body×3, PartDesign::CoordinateSystem×1, App::FeaturePython×1
note: 13 computed .brp shape members not serialized (recipe doc carries the construction recipe); baked Part::Feature solids carry a one-line shape summary decoded from their .brp

FEATURE [PartDesign::CoordinateSystem] LCS_Origin
  AttacherType = Attacher::AttachEngine3D
  MapMode = 2
  Support = -> [X_Axis]
FEATURE [App::DocumentObjectGroup] Constraints
FEATURE [App::FeaturePython] Variables  # WARN: FeaturePython — macro-defined, semantics opaque (R4)
  DriveShaftLength = 200
  Pully80TPosition = 60
  PullyDriveDiameter = 12.73
  PullyDrivePosition = 83.5
  Type = App::PropertyContainer
FEATURE [App::DocumentObjectGroup] Configurations
FEATURE [Sketcher::SketchObject] Sketch
  FullyConstrained = true
  MapMode = 5
  Support = -> [XY_Plane004]
  expr: Constraints[21] = -50.93 / 2
  sketch-geometry (10):
    g0: LineSegment StartX=-11 StartY=-2.5 StartZ=0 EndX=-11 EndY=-8 EndZ=0
    g1: LineSegment StartX=-11 StartY=-8 StartZ=0 EndX=-5.5 EndY=-8 EndZ=0
    g2: LineSegment StartX=-5.5 StartY=-8 StartZ=0 EndX=-5.5 EndY=-26.465 EndZ=0
    g3: LineSegment StartX=-5.5 StartY=-26.465 StartZ=0 EndX=-4.5 EndY=-25.465 EndZ=0
    g4: LineSegment StartX=-4.5 StartY=-25.465 StartZ=0 EndX=4.5 EndY=-25.465 EndZ=0
    g5: LineSegment StartX=4.5 StartY=-25.465 StartZ=0 EndX=5.5 EndY=-26.465 EndZ=0
    g6: LineSegment StartX=5.5 StartY=-26.465 StartZ=0 EndX=5.5 EndY=-9 EndZ=0
    g7: LineSegment StartX=5.5 StartY=-9 StartZ=0 EndX=10.5 EndY=-4 EndZ=0
    g8: LineSegment StartX=10.5 StartY=-4 StartZ=0 EndX=10.5 EndY=-2.5 EndZ=0
    g9: LineSegment StartX=10.5 StartY=-2.5 StartZ=0 EndX=-11 EndY=-2.5 EndZ=0
  constraints (28):
    c: Vertical(g0)
    c: Coincident(g0,g1)
    c: Coincident(g1,g2)
    c: Vertical(g2)
    c: Coincident(g2,g3)
    c: Coincident(g3,g4)
    c: Coincident(g4,g5)
    c: Coincident(g5,g6)
    c: Coincident(g6,g7)
    c: Coincident(g7,g8)
    c: Coincident(g8,g9)
    c: Coincident(g9,g0)
    c: Horizontal(g9)
    c: Angle(g3) = 0.785398
    c: Parallel(g3,g7)
    c: Vertical(g6)
    c: Vertical(g8)
    c: Symmetric(g3,g4,g-2)
    c: DistanceX(g4,g4) = 9
    c: Symmetric(g2,g5,g-2)
    c: DistanceX(g2,g3) = 1
    c: DistanceY(g3) = -25.465
    c: Horizontal(g1)
    c: DistanceY(g0) = -2.5
    c: DistanceX(g1,g1) = 5.5
    c: DistanceY(g0) = -8
    c: DistanceX(g7,g7) = 5
    c: DistanceY(g8,g8) = 1.5
FEATURE [PartDesign::Revolution] Revolution
  Angle = 360
  Axis = (1,0,0)
  Base = (0,0,0)
  Profile = -> Sketch
  ReferenceAxis = -> Sketch [H_Axis]
  Reversed = true
FEATURE [PartDesign::Body] Body002  label="Pully80TBody"
  Group = -> [Sketch,Revolution]
  Origin = -> Origin004
  Tip = -> Revolution
FEATURE [App::Part] Part001  label="Pully80T"
  Group = -> [Body002]
  Origin = -> Origin005
FEATURE [Sketcher::SketchObject] Sketch118
  FullyConstrained = true
  MapMode = 5
  Support = -> [XY_Plane003]
  expr: Constraints[18] = -<<Variables>>.PullyDriveDiameter / 2
  sketch-geometry (8):
    g0: LineSegment StartX=-11 StartY=-2.5 StartZ=0 EndX=-11 EndY=-8 EndZ=0
    g1: LineSegment StartX=-11 StartY=-8 StartZ=0 EndX=-3.5 EndY=-8 EndZ=0
    g2: LineSegment StartX=-3.5 StartY=-8 StartZ=0 EndX=-3.5 EndY=-6.365 EndZ=0
    g3: LineSegment StartX=-3.5 StartY=-6.365 StartZ=0 EndX=3.5 EndY=-6.365 EndZ=0
    g4: LineSegment StartX=3.5 StartY=-6.365 StartZ=0 EndX=3.5 EndY=-8 EndZ=0
    g5: LineSegment StartX=3.5 StartY=-8 StartZ=0 EndX=5 EndY=-8 EndZ=0
    g6: LineSegment StartX=5 StartY=-8 StartZ=0 EndX=5 EndY=-2.5 EndZ=0
    g7: LineSegment StartX=5 StartY=-2.5 StartZ=0 EndX=-11 EndY=-2.5 EndZ=0
  constraints (23):
    c: Vertical(g0)
    c: Coincident(g0,g1)
    c: Horizontal(g1)
    c: Coincident(g1,g2)
    c: Coincident(g2,g3)
    c: Coincident(g3,g4)
    c: Vertical(g4)
    c: Coincident(g4,g5)
    c: Coincident(g5,g6)
    c: Vertical(g6)
    c: Coincident(g6,g7)
    c: Coincident(g7,g0)
    c: Horizontal(g7)
    c: Symmetric(g2,g3,g-2)
    c: Vertical(g2)
    c: DistanceX(g7,g7) = 16
    c: DistanceY(g0) = -2.5
    c: DistanceY(g0) = -8
    c: DistanceY(g2) = -6.365
    c: DistanceX(g5,g5) = 1.5
    c: DistanceX(g1,g1) = 7.5
    c: Horizontal(g5)
    c: DistanceY(g5) = -8
FEATURE [PartDesign::Revolution] Revolution001
  Angle = 360
  Axis = (1,0,0)
  Base = (0,0,0)
  Profile = -> Sketch118
  ReferenceAxis = -> Sketch118 [H_Axis]
  Reversed = true
FEATURE [PartDesign::Body] Body001  label="PullyDriveBody"
  Group = -> [Sketch118,Revolution001]
  Origin = -> Origin003
  Tip = -> Revolution001
FEATURE [App::Part] Part002  label="PullyDrive"
  Group = -> [Body001]
  Origin = -> Origin006
FEATURE [Sketcher::SketchObject] Sketch119
  FullyConstrained = true
  MapMode = 5
  Support = -> [XY_Plane002]
  expr: Constraints[13] = <<Variables>>.DriveShaftLength
  sketch-geometry (16):
    g0: LineSegment StartX=-100 StartY=-8 StartZ=0 EndX=-95 EndY=-8 EndZ=0
    g1: LineSegment StartX=-95 StartY=-8 StartZ=0 EndX=-95 EndY=-2.5 EndZ=0
    g2: LineSegment StartX=-95 StartY=-2.5 StartZ=0 EndX=95 EndY=-2.5 EndZ=0
    g3: LineSegment StartX=95 StartY=-2.5 StartZ=0 EndX=95 EndY=-8 EndZ=0
    g4: LineSegment StartX=95 StartY=-8 StartZ=0 EndX=100 EndY=-8 EndZ=0
    g5: LineSegment StartX=100 StartY=0 StartZ=0 EndX=-100 EndY=0 EndZ=0
    g6: LineSegment StartX=-100 StartY=-3.5 StartZ=0 EndX=100 EndY=-3.5 EndZ=0
    g7: LineSegment StartX=-100 StartY=-7 StartZ=0 EndX=100 EndY=-7 EndZ=0
    g8: LineSegment StartX=-100 StartY=0 StartZ=0 EndX=-100 EndY=-2.4 EndZ=0
    g9: LineSegment StartX=-100 StartY=-2.4 StartZ=0 EndX=-99.9 EndY=-2.5 EndZ=0
    g10: LineSegment StartX=-99.9 StartY=-2.5 StartZ=0 EndX=-100 EndY=-2.6 EndZ=0
    g11: LineSegment StartX=99.9 StartY=-2.5 StartZ=0 EndX=100 EndY=-2.4 EndZ=0
    g12: LineSegment StartX=100 StartY=-2.4 StartZ=0 EndX=100 EndY=0 EndZ=0
    g13: LineSegment StartX=100 StartY=-8 StartZ=0 EndX=100 EndY=-2.6 EndZ=0
    g14: LineSegment StartX=100 StartY=-2.6 StartZ=0 EndX=99.9 EndY=-2.5 EndZ=0
    g15: LineSegment StartX=-100 StartY=-2.6 StartZ=0 EndX=-100 EndY=-8 EndZ=0
  constraints (40):
    c: Coincident(g0,g1)
    c: Vertical(g1)
    c: Coincident(g1,g2)
    c: Coincident(g2,g3)
    c: Coincident(g3,g4)
    c: Coincident(g4,g13)
    c: Coincident(g12,g5)
    c: Horizontal(g0)
    c: Symmetric(g5,g12,g-2)
    c: Symmetric(g1,g2,g-2)
    c: Symmetric(g0,g3,g-2)
    c: Symmetric(g0,g4,g-2)
    c: PointOnObject(g5,g-1)
    c: DistanceX(g5,g5) = 200
    c: DistanceY(g0) = -8
    c: DistanceY(g1) = -2.5
    c: DistanceX(g0,g0) = 5
    c: Coincident(g8,g5)
    c: Symmetric(g6,g6,g-2)
    c: Symmetric(g7,g7,g-2)
    c: DistanceY(g6,g1) = 1
    c: Coincident(g9,g10)
    c: Coincident(g8,g9)
    c: Vertical(g8)
    c: Coincident(g10,g15)
    c: PointOnObject(g9,g2)
    c: Symmetric(g8,g10,g2)
    c: Angle(g9) = -0.785398
    c: DistanceY(g10,g8) = 0.2
    c: DistanceY(g0,g7) = 1
    c: Coincident(g14,g11)
    c: Coincident(g11,g12)
    c: Coincident(g13,g14)
    c: Symmetric(g11,g9,g-2)
    c: Symmetric(g8,g11,g-2)
    c: Symmetric(g13,g10,g-2)
    c: Vertical(g15)
    c: PointOnObject(g6,g8)
    c: PointOnObject(g7,g8)
    c: Coincident(g15,g0)
FEATURE [PartDesign::Revolution] Revolution002
  Angle = 360
  Axis = (1,0,0)
  Base = (0,0,0)
  Profile = -> Sketch119
  ReferenceAxis = -> Sketch119 [H_Axis]
  Reversed = true
FEATURE [PartDesign::Body] Body  label="ShaftBody"
  Group = -> [Sketch119,Revolution002]
  Origin = -> Origin002
  Tip = -> Revolution002
FEATURE [App::Part] Part  label="DriveShaft"
  Group = -> [Body]
  Origin = -> Origin001
FEATURE [App::DocumentObjectGroup] Parts
  Group = -> [Part,Part001,Part002]
FEATURE [App::Link] DriveShaft  label="DriveShaft001"
  LinkedObject = -> Part
FEATURE [App::Link] PullyDriveLeft
  LinkPlacement = pos=(-83.5,0,0) rot=(0,0,1;0rad)
  LinkedObject = -> Part002
  Placement = pos=(-83.5,0,0) rot=(0,0,1;0rad)
  expr: .Placement.Base.x = -<<Variables>>.PullyDrivePosition
FEATURE [App::Link] PullyDriveRight
  LinkPlacement = pos=(83.5,0,0) rot=(0,0,1;3.14159rad)
  LinkedObject = -> Part002
  Placement = pos=(83.5,0,0) rot=(0,0,1;3.14159rad)
  expr: .Placement.Base.x = <<Variables>>.PullyDrivePosition
FEATURE [App::Link] Pully80T  label="Pully80T001"
  LinkPlacement = pos=(60,0,0) rot=(0,0,1;0rad)
  LinkedObject = -> Part001
  Placement = pos=(60,0,0) rot=(0,0,1;0rad)
  expr: .Placement.Base.x = <<Variables>>.Pully80TPosition
FEATURE [App::Part] Model
  AssemblyType = Part::Link
  Group = -> [LCS_Origin,Constraints,Variables,Configurations,DriveShaft,PullyDriveLeft,PullyDriveRight,Pully80T]
  Origin = -> Origin
  Type = Assembly
